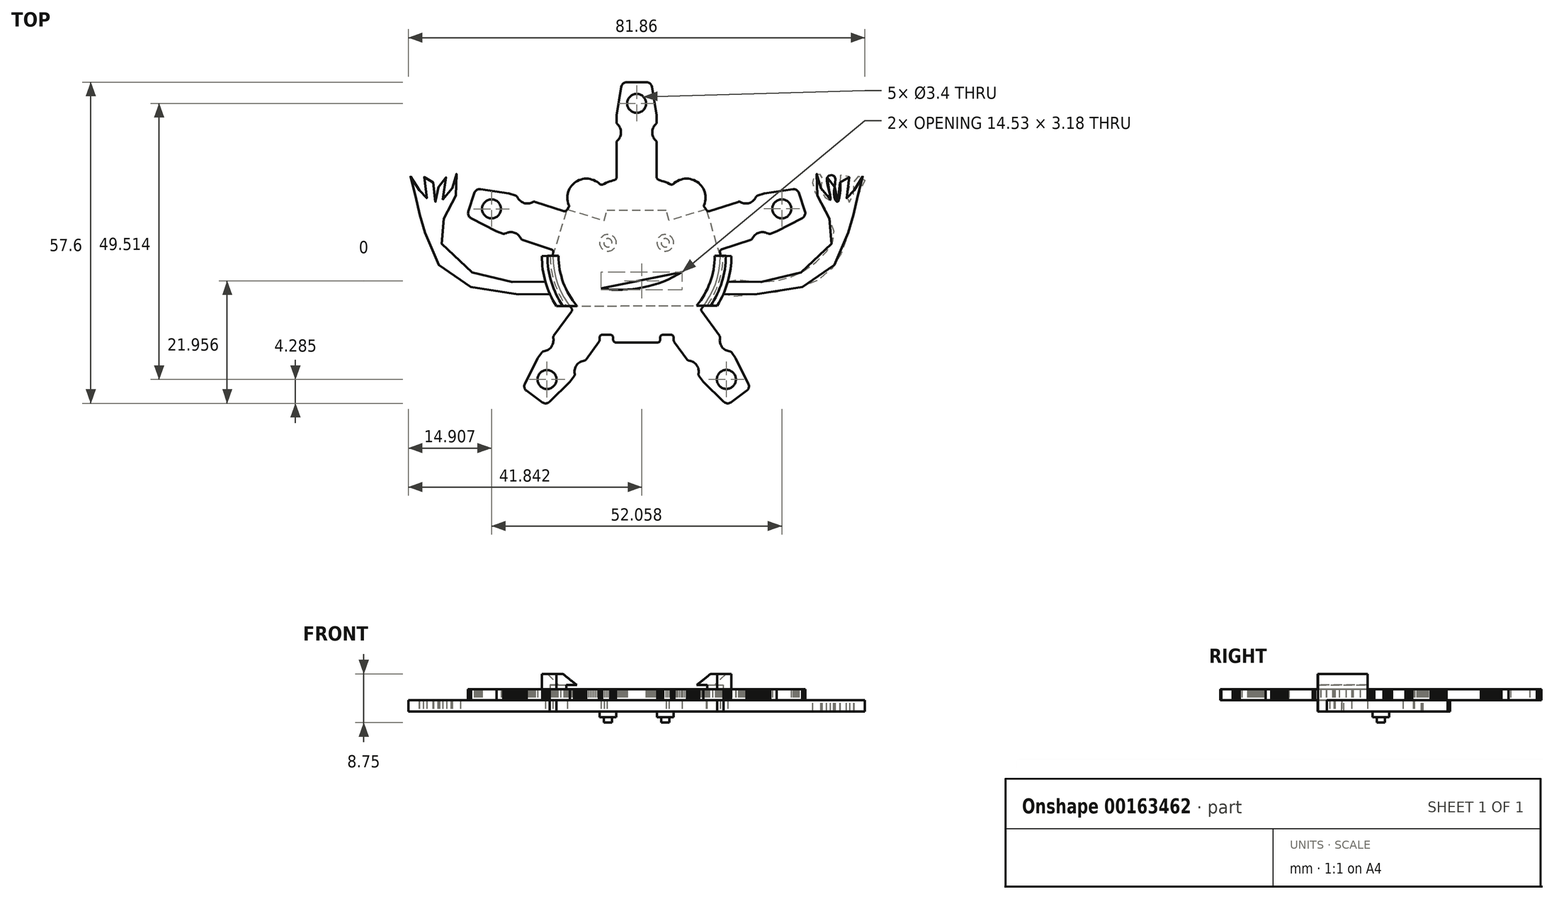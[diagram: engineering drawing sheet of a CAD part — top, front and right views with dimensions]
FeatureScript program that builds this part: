
annotation { "Feature Type Name" : "Feature", "Feature Type Description" : "" }
export const myFeature = defineFeature(function(context is Context, id is Id, definition is map)
    precondition{}
    {
        {
            var Q0;
            Q0=qCreatedBy(makeId("Top.planeOp"),FACE);
            var sketch = newSketch(context, id + "F0", { "sketchPlane" : qUnion([Q0])});
            skLineSegment(sketch, "E0", {"start": v(30.22, 5.42) * mm, "end": v(30.18, 5.6) * mm});
            skLineSegment(sketch, "E1", {"start": v(30.18, 5.6) * mm, "end": v(29.1, 8.94) * mm});
            skLineSegment(sketch, "E2", {"start": v(29.1, 8.94) * mm, "end": v(29.03, 9.1) * mm});
            skLineSegment(sketch, "E3", {"start": v(29.03, 9.1) * mm, "end": v(28.93, 9.25) * mm});
            skLineSegment(sketch, "E4", {"start": v(28.93, 9.25) * mm, "end": v(28.81, 9.38) * mm});
            skLineSegment(sketch, "E5", {"start": v(28.81, 9.38) * mm, "end": v(28.67, 9.48) * mm});
            skLineSegment(sketch, "E6", {"start": v(28.67, 9.48) * mm, "end": v(28.52, 9.56) * mm});
            skLineSegment(sketch, "E7", {"start": v(28.52, 9.56) * mm, "end": v(28.36, 9.6) * mm});
            skLineSegment(sketch, "E8", {"start": v(28.36, 9.6) * mm, "end": v(28.18, 9.63) * mm});
            skLineSegment(sketch, "E9", {"start": v(28.18, 9.63) * mm, "end": v(28, 9.62) * mm});
            skLineSegment(sketch, "E10", {"start": v(28, 9.62) * mm, "end": v(22.92, 8.87) * mm});
            skLineSegment(sketch, "E11", {"start": v(22.92, 8.87) * mm, "end": v(21.71, 8.48) * mm});
            skLineSegment(sketch, "E12", {"start": v(21.71, 8.48) * mm, "end": v(21.66, 8.46) * mm});
            skLineSegment(sketch, "E13", {"start": v(21.66, 8.46) * mm, "end": v(21.62, 8.44) * mm});
            skLineSegment(sketch, "E14", {"start": v(21.62, 8.44) * mm, "end": v(21.58, 8.4) * mm});
            skLineSegment(sketch, "E15", {"start": v(21.58, 8.4) * mm, "end": v(21.54, 8.38) * mm});
            skLineSegment(sketch, "E16", {"start": v(21.54, 8.38) * mm, "end": v(21.5, 8.34) * mm});
            skLineSegment(sketch, "E17", {"start": v(21.5, 8.34) * mm, "end": v(21.47, 8.3) * mm});
            skLineSegment(sketch, "E18", {"start": v(21.47, 8.3) * mm, "end": v(21.44, 8.26) * mm});
            skLineSegment(sketch, "E19", {"start": v(21.44, 8.26) * mm, "end": v(21.32, 8.03) * mm});
            skLineSegment(sketch, "E20", {"start": v(21.32, 8.03) * mm, "end": v(21.2, 7.86) * mm});
            skLineSegment(sketch, "E21", {"start": v(21.2, 7.86) * mm, "end": v(21.07, 7.7) * mm});
            skLineSegment(sketch, "E22", {"start": v(21.07, 7.7) * mm, "end": v(20.92, 7.56) * mm});
            skLineSegment(sketch, "E23", {"start": v(20.92, 7.56) * mm, "end": v(20.77, 7.43) * mm});
            skLineSegment(sketch, "E24", {"start": v(20.77, 7.43) * mm, "end": v(20.6, 7.32) * mm});
            skLineSegment(sketch, "E25", {"start": v(20.6, 7.32) * mm, "end": v(20.4, 7.22) * mm});
            skLineSegment(sketch, "E26", {"start": v(20.4, 7.22) * mm, "end": v(20.22, 7.15) * mm});
            skLineSegment(sketch, "E27", {"start": v(20.22, 7.15) * mm, "end": v(20.02, 7.1) * mm});
            skLineSegment(sketch, "E28", {"start": v(20.02, 7.1) * mm, "end": v(19.81, 7.06) * mm});
            skLineSegment(sketch, "E29", {"start": v(19.81, 7.06) * mm, "end": v(19.6, 7.05) * mm});
            skLineSegment(sketch, "E30", {"start": v(19.6, 7.05) * mm, "end": v(19.4, 7.06) * mm});
            skLineSegment(sketch, "E31", {"start": v(19.4, 7.06) * mm, "end": v(19.2, 7.1) * mm});
            skLineSegment(sketch, "E32", {"start": v(19.2, 7.1) * mm, "end": v(19, 7.14) * mm});
            skLineSegment(sketch, "E33", {"start": v(19, 7.14) * mm, "end": v(18.8, 7.21) * mm});
            skLineSegment(sketch, "E34", {"start": v(18.8, 7.21) * mm, "end": v(18.58, 7.33) * mm});
            skLineSegment(sketch, "E35", {"start": v(18.58, 7.33) * mm, "end": v(18.53, 7.35) * mm});
            skLineSegment(sketch, "E36", {"start": v(18.53, 7.35) * mm, "end": v(18.48, 7.36) * mm});
            skLineSegment(sketch, "E37", {"start": v(18.48, 7.36) * mm, "end": v(18.43, 7.37) * mm});
            skLineSegment(sketch, "E38", {"start": v(18.43, 7.37) * mm, "end": v(18.38, 7.37) * mm});
            skLineSegment(sketch, "E39", {"start": v(18.38, 7.37) * mm, "end": v(18.33, 7.37) * mm});
            skLineSegment(sketch, "E40", {"start": v(18.33, 7.37) * mm, "end": v(18.28, 7.36) * mm});
            skLineSegment(sketch, "E41", {"start": v(18.28, 7.36) * mm, "end": v(18.23, 7.34) * mm});
            skLineSegment(sketch, "E42", {"start": v(18.23, 7.34) * mm, "end": v(13.03, 5.66) * mm});
            skLineSegment(sketch, "E43", {"start": v(13.03, 5.66) * mm, "end": v(13, 5.65) * mm});
            skLineSegment(sketch, "E44", {"start": v(13, 5.65) * mm, "end": v(12.96, 5.65) * mm});
            skLineSegment(sketch, "E45", {"start": v(12.96, 5.65) * mm, "end": v(12.92, 5.64) * mm});
            skLineSegment(sketch, "E46", {"start": v(12.92, 5.64) * mm, "end": v(12.88, 5.64) * mm});
            skLineSegment(sketch, "E47", {"start": v(12.88, 5.64) * mm, "end": v(12.83, 5.64) * mm});
            skLineSegment(sketch, "E48", {"start": v(12.83, 5.64) * mm, "end": v(12.8, 5.64) * mm});
            skLineSegment(sketch, "E49", {"start": v(12.8, 5.64) * mm, "end": v(12.76, 5.65) * mm});
            skLineSegment(sketch, "E50", {"start": v(12.76, 5.65) * mm, "end": v(12.73, 5.66) * mm});
            skLineSegment(sketch, "E51", {"start": v(12.73, 5.66) * mm, "end": v(12.7, 5.68) * mm});
            skLineSegment(sketch, "E52", {"start": v(12.7, 5.68) * mm, "end": v(12.67, 5.7) * mm});
            skLineSegment(sketch, "E53", {"start": v(12.67, 5.7) * mm, "end": v(12.65, 5.72) * mm});
            skLineSegment(sketch, "E54", {"start": v(12.65, 5.72) * mm, "end": v(12.63, 5.74) * mm});
            skLineSegment(sketch, "E55", {"start": v(12.63, 5.74) * mm, "end": v(12.6, 5.77) * mm});
            skLineSegment(sketch, "E56", {"start": v(12.6, 5.77) * mm, "end": v(12.59, 5.8) * mm});
            skLineSegment(sketch, "E57", {"start": v(12.59, 5.8) * mm, "end": v(12.4, 6.07) * mm});
            skLineSegment(sketch, "E58", {"start": v(12.4, 6.07) * mm, "end": v(12.1, 6.48) * mm});
            skLineSegment(sketch, "E59", {"start": v(12.1, 6.48) * mm, "end": v(12.1, 6.5) * mm});
            skLineSegment(sketch, "E60", {"start": v(12.1, 6.5) * mm, "end": v(12.09, 6.52) * mm});
            skLineSegment(sketch, "E61", {"start": v(12.09, 6.52) * mm, "end": v(12.08, 6.54) * mm});
            skLineSegment(sketch, "E62", {"start": v(12.08, 6.54) * mm, "end": v(12.07, 6.56) * mm});
            skLineSegment(sketch, "E63", {"start": v(12.07, 6.56) * mm, "end": v(12.06, 6.58) * mm});
            skLineSegment(sketch, "E64", {"start": v(12.06, 6.58) * mm, "end": v(12.06, 6.6) * mm});
            skLineSegment(sketch, "E65", {"start": v(12.06, 6.6) * mm, "end": v(12.06, 6.63) * mm});
            skLineSegment(sketch, "E66", {"start": v(12.06, 6.63) * mm, "end": v(12.05, 6.65) * mm});
            skLineSegment(sketch, "E67", {"start": v(12.05, 6.65) * mm, "end": v(12.05, 6.67) * mm});
            skLineSegment(sketch, "E68", {"start": v(12.05, 6.67) * mm, "end": v(12.06, 6.7) * mm});
            skLineSegment(sketch, "E69", {"start": v(12.06, 6.7) * mm, "end": v(12.06, 6.71) * mm});
            skLineSegment(sketch, "E70", {"start": v(12.06, 6.71) * mm, "end": v(12.06, 6.73) * mm});
            skLineSegment(sketch, "E71", {"start": v(12.06, 6.73) * mm, "end": v(12.06, 6.73) * mm});
            skLineSegment(sketch, "E72", {"start": v(12.06, 6.73) * mm, "end": v(12.09, 6.78) * mm});
            skLineSegment(sketch, "E73", {"start": v(12.09, 6.78) * mm, "end": v(12.2, 7.09) * mm});
            skLineSegment(sketch, "E74", {"start": v(12.2, 7.09) * mm, "end": v(12.28, 7.42) * mm});
            skLineSegment(sketch, "E75", {"start": v(12.28, 7.42) * mm, "end": v(12.34, 7.75) * mm});
            skLineSegment(sketch, "E76", {"start": v(12.34, 7.75) * mm, "end": v(12.35, 8.1) * mm});
            skLineSegment(sketch, "E77", {"start": v(12.35, 8.1) * mm, "end": v(12.34, 8.45) * mm});
            skLineSegment(sketch, "E78", {"start": v(12.34, 8.45) * mm, "end": v(12.28, 8.79) * mm});
            skLineSegment(sketch, "E79", {"start": v(12.28, 8.79) * mm, "end": v(12.2, 9.11) * mm});
            skLineSegment(sketch, "E80", {"start": v(12.2, 9.11) * mm, "end": v(12.09, 9.42) * mm});
            skLineSegment(sketch, "E81", {"start": v(12.09, 9.42) * mm, "end": v(11.94, 9.72) * mm});
            skLineSegment(sketch, "E82", {"start": v(11.94, 9.72) * mm, "end": v(11.77, 10) * mm});
            skLineSegment(sketch, "E83", {"start": v(11.77, 10) * mm, "end": v(11.58, 10.26) * mm});
            skLineSegment(sketch, "E84", {"start": v(11.58, 10.26) * mm, "end": v(11.36, 10.5) * mm});
            skLineSegment(sketch, "E85", {"start": v(11.36, 10.5) * mm, "end": v(11.12, 10.72) * mm});
            skLineSegment(sketch, "E86", {"start": v(11.12, 10.72) * mm, "end": v(10.85, 10.92) * mm});
            skLineSegment(sketch, "E87", {"start": v(10.85, 10.92) * mm, "end": v(10.57, 11.09) * mm});
            skLineSegment(sketch, "E88", {"start": v(10.57, 11.09) * mm, "end": v(10.28, 11.23) * mm});
            skLineSegment(sketch, "E89", {"start": v(10.28, 11.23) * mm, "end": v(9.96, 11.35) * mm});
            skLineSegment(sketch, "E90", {"start": v(9.96, 11.35) * mm, "end": v(9.64, 11.43) * mm});
            skLineSegment(sketch, "E91", {"start": v(9.64, 11.43) * mm, "end": v(9.3, 11.48) * mm});
            skLineSegment(sketch, "E92", {"start": v(9.3, 11.48) * mm, "end": v(8.95, 11.5) * mm});
            skLineSegment(sketch, "E93", {"start": v(8.95, 11.5) * mm, "end": v(8.6, 11.48) * mm});
            skLineSegment(sketch, "E94", {"start": v(8.6, 11.48) * mm, "end": v(8.27, 11.43) * mm});
            skLineSegment(sketch, "E95", {"start": v(8.27, 11.43) * mm, "end": v(7.94, 11.35) * mm});
            skLineSegment(sketch, "E96", {"start": v(7.94, 11.35) * mm, "end": v(7.63, 11.23) * mm});
            skLineSegment(sketch, "E97", {"start": v(7.63, 11.23) * mm, "end": v(7.33, 11.1) * mm});
            skLineSegment(sketch, "E98", {"start": v(7.33, 11.1) * mm, "end": v(7.05, 10.92) * mm});
            skLineSegment(sketch, "E99", {"start": v(7.05, 10.92) * mm, "end": v(6.8, 10.72) * mm});
            skLineSegment(sketch, "E100", {"start": v(6.8, 10.72) * mm, "end": v(6.63, 10.58) * mm});
            skLineSegment(sketch, "E101", {"start": v(6.63, 10.58) * mm, "end": v(6.55, 10.51) * mm});
            skLineSegment(sketch, "E102", {"start": v(6.55, 10.51) * mm, "end": v(6.47, 10.47) * mm});
            skLineSegment(sketch, "E103", {"start": v(6.47, 10.47) * mm, "end": v(6.37, 10.44) * mm});
            skLineSegment(sketch, "E104", {"start": v(6.37, 10.44) * mm, "end": v(6.27, 10.43) * mm});
            skLineSegment(sketch, "E105", {"start": v(6.27, 10.43) * mm, "end": v(6.17, 10.44) * mm});
            skLineSegment(sketch, "E106", {"start": v(6.17, 10.44) * mm, "end": v(6.08, 10.47) * mm});
            skLineSegment(sketch, "E107", {"start": v(6.08, 10.47) * mm, "end": v(6.02, 10.5) * mm});
            skLineSegment(sketch, "E108", {"start": v(6.02, 10.5) * mm, "end": v(5.84, 10.58) * mm});
            skLineSegment(sketch, "E109", {"start": v(5.84, 10.58) * mm, "end": v(5.53, 10.72) * mm});
            skLineSegment(sketch, "E110", {"start": v(5.53, 10.72) * mm, "end": v(5.2, 10.85) * mm});
            skLineSegment(sketch, "E111", {"start": v(5.2, 10.85) * mm, "end": v(4.88, 10.97) * mm});
            skLineSegment(sketch, "E112", {"start": v(4.88, 10.97) * mm, "end": v(4.56, 11.1) * mm});
            skLineSegment(sketch, "E113", {"start": v(4.56, 11.1) * mm, "end": v(4.22, 11.2) * mm});
            skLineSegment(sketch, "E114", {"start": v(4.22, 11.2) * mm, "end": v(4.02, 11.26) * mm});
            skLineSegment(sketch, "E115", {"start": v(4.02, 11.26) * mm, "end": v(3.9, 11.29) * mm});
            skLineSegment(sketch, "E116", {"start": v(3.9, 11.29) * mm, "end": v(3.82, 11.34) * mm});
            skLineSegment(sketch, "E117", {"start": v(3.82, 11.34) * mm, "end": v(3.75, 11.4) * mm});
            skLineSegment(sketch, "E118", {"start": v(3.75, 11.4) * mm, "end": v(3.68, 11.47) * mm});
            skLineSegment(sketch, "E119", {"start": v(3.68, 11.47) * mm, "end": v(3.64, 11.56) * mm});
            skLineSegment(sketch, "E120", {"start": v(3.64, 11.56) * mm, "end": v(3.6, 11.65) * mm});
            skLineSegment(sketch, "E121", {"start": v(3.6, 11.65) * mm, "end": v(3.6, 11.76) * mm});
            skLineSegment(sketch, "E122", {"start": v(3.6, 11.76) * mm, "end": v(3.6, 17.97) * mm});
            skLineSegment(sketch, "E123", {"start": v(3.6, 17.97) * mm, "end": v(3.6, 18.02) * mm});
            skLineSegment(sketch, "E124", {"start": v(3.6, 18.02) * mm, "end": v(3.59, 18.07) * mm});
            skLineSegment(sketch, "E125", {"start": v(3.59, 18.07) * mm, "end": v(3.58, 18.12) * mm});
            skLineSegment(sketch, "E126", {"start": v(3.58, 18.12) * mm, "end": v(3.56, 18.17) * mm});
            skLineSegment(sketch, "E127", {"start": v(3.56, 18.17) * mm, "end": v(3.54, 18.21) * mm});
            skLineSegment(sketch, "E128", {"start": v(3.54, 18.21) * mm, "end": v(3.5, 18.26) * mm});
            skLineSegment(sketch, "E129", {"start": v(3.5, 18.26) * mm, "end": v(3.48, 18.3) * mm});
            skLineSegment(sketch, "E130", {"start": v(3.48, 18.3) * mm, "end": v(3.3, 18.48) * mm});
            skLineSegment(sketch, "E131", {"start": v(3.3, 18.48) * mm, "end": v(3.17, 18.65) * mm});
            skLineSegment(sketch, "E132", {"start": v(3.17, 18.65) * mm, "end": v(3.06, 18.82) * mm});
            skLineSegment(sketch, "E133", {"start": v(3.06, 18.82) * mm, "end": v(2.97, 19) * mm});
            skLineSegment(sketch, "E134", {"start": v(2.97, 19) * mm, "end": v(2.9, 19.2) * mm});
            skLineSegment(sketch, "E135", {"start": v(2.9, 19.2) * mm, "end": v(2.84, 19.4) * mm});
            skLineSegment(sketch, "E136", {"start": v(2.84, 19.4) * mm, "end": v(2.81, 19.6) * mm});
            skLineSegment(sketch, "E137", {"start": v(2.81, 19.6) * mm, "end": v(2.8, 19.8) * mm});
            skLineSegment(sketch, "E138", {"start": v(2.8, 19.8) * mm, "end": v(2.81, 20) * mm});
            skLineSegment(sketch, "E139", {"start": v(2.81, 20) * mm, "end": v(2.84, 20.21) * mm});
            skLineSegment(sketch, "E140", {"start": v(2.84, 20.21) * mm, "end": v(2.9, 20.41) * mm});
            skLineSegment(sketch, "E141", {"start": v(2.9, 20.41) * mm, "end": v(2.97, 20.6) * mm});
            skLineSegment(sketch, "E142", {"start": v(2.97, 20.6) * mm, "end": v(3.06, 20.78) * mm});
            skLineSegment(sketch, "E143", {"start": v(3.06, 20.78) * mm, "end": v(3.17, 20.96) * mm});
            skLineSegment(sketch, "E144", {"start": v(3.17, 20.96) * mm, "end": v(3.3, 21.12) * mm});
            skLineSegment(sketch, "E145", {"start": v(3.3, 21.12) * mm, "end": v(3.48, 21.3) * mm});
            skLineSegment(sketch, "E146", {"start": v(3.48, 21.3) * mm, "end": v(3.5, 21.35) * mm});
            skLineSegment(sketch, "E147", {"start": v(3.5, 21.35) * mm, "end": v(3.54, 21.39) * mm});
            skLineSegment(sketch, "E148", {"start": v(3.54, 21.39) * mm, "end": v(3.56, 21.44) * mm});
            skLineSegment(sketch, "E149", {"start": v(3.56, 21.44) * mm, "end": v(3.58, 21.48) * mm});
            skLineSegment(sketch, "E150", {"start": v(3.58, 21.48) * mm, "end": v(3.59, 21.53) * mm});
            skLineSegment(sketch, "E151", {"start": v(3.59, 21.53) * mm, "end": v(3.6, 21.58) * mm});
            skLineSegment(sketch, "E152", {"start": v(3.6, 21.58) * mm, "end": v(3.6, 21.63) * mm});
            skLineSegment(sketch, "E153", {"start": v(3.6, 21.63) * mm, "end": v(3.6, 22.9) * mm});
            skLineSegment(sketch, "E154", {"start": v(3.6, 22.9) * mm, "end": v(2.74, 27.97) * mm});
            skLineSegment(sketch, "E155", {"start": v(2.74, 27.97) * mm, "end": v(2.7, 28.14) * mm});
            skLineSegment(sketch, "E156", {"start": v(2.7, 28.14) * mm, "end": v(2.62, 28.3) * mm});
            skLineSegment(sketch, "E157", {"start": v(2.62, 28.3) * mm, "end": v(2.52, 28.44) * mm});
            skLineSegment(sketch, "E158", {"start": v(2.52, 28.44) * mm, "end": v(2.4, 28.57) * mm});
            skLineSegment(sketch, "E159", {"start": v(2.4, 28.57) * mm, "end": v(2.26, 28.67) * mm});
            skLineSegment(sketch, "E160", {"start": v(2.26, 28.67) * mm, "end": v(2.1, 28.74) * mm});
            skLineSegment(sketch, "E161", {"start": v(2.1, 28.74) * mm, "end": v(1.93, 28.79) * mm});
            skLineSegment(sketch, "E162", {"start": v(1.93, 28.79) * mm, "end": v(1.76, 28.8) * mm});
            skLineSegment(sketch, "E163", {"start": v(1.76, 28.8) * mm, "end": v(-1.4, 28.8) * mm});
            skLineSegment(sketch, "E164", {"start": v(-1.4, 28.8) * mm, "end": v(1.6, 28.8) * mm});
            skLineSegment(sketch, "E165", {"start": v(-1.4, 28.8) * mm, "end": v(-1.7, 28.8) * mm});
            skLineSegment(sketch, "E166", {"start": v(-1.7, 28.8) * mm, "end": v(-1.76, 28.8) * mm});
            skLineSegment(sketch, "E167", {"start": v(-1.76, 28.8) * mm, "end": v(-1.93, 28.79) * mm});
            skLineSegment(sketch, "E168", {"start": v(-1.93, 28.79) * mm, "end": v(-2.1, 28.74) * mm});
            skLineSegment(sketch, "E169", {"start": v(-2.1, 28.74) * mm, "end": v(-2.26, 28.67) * mm});
            skLineSegment(sketch, "E170", {"start": v(-2.26, 28.67) * mm, "end": v(-2.4, 28.57) * mm});
            skLineSegment(sketch, "E171", {"start": v(-2.4, 28.57) * mm, "end": v(-2.52, 28.44) * mm});
            skLineSegment(sketch, "E172", {"start": v(-2.52, 28.44) * mm, "end": v(-2.62, 28.3) * mm});
            skLineSegment(sketch, "E173", {"start": v(-2.62, 28.3) * mm, "end": v(-2.7, 28.14) * mm});
            skLineSegment(sketch, "E174", {"start": v(-2.7, 28.14) * mm, "end": v(-2.74, 27.97) * mm});
            skLineSegment(sketch, "E175", {"start": v(-2.74, 27.97) * mm, "end": v(-3.6, 22.9) * mm});
            skLineSegment(sketch, "E176", {"start": v(-3.6, 22.9) * mm, "end": v(-3.6, 21.63) * mm});
            skLineSegment(sketch, "E177", {"start": v(-3.6, 21.63) * mm, "end": v(-3.6, 21.58) * mm});
            skLineSegment(sketch, "E178", {"start": v(-3.6, 21.58) * mm, "end": v(-3.59, 21.53) * mm});
            skLineSegment(sketch, "E179", {"start": v(-3.59, 21.53) * mm, "end": v(-3.58, 21.48) * mm});
            skLineSegment(sketch, "E180", {"start": v(-3.58, 21.48) * mm, "end": v(-3.56, 21.44) * mm});
            skLineSegment(sketch, "E181", {"start": v(-3.56, 21.44) * mm, "end": v(-3.53, 21.39) * mm});
            skLineSegment(sketch, "E182", {"start": v(-3.53, 21.39) * mm, "end": v(-3.5, 21.35) * mm});
            skLineSegment(sketch, "E183", {"start": v(-3.5, 21.35) * mm, "end": v(-3.48, 21.3) * mm});
            skLineSegment(sketch, "E184", {"start": v(-3.48, 21.3) * mm, "end": v(-3.3, 21.12) * mm});
            skLineSegment(sketch, "E185", {"start": v(-3.3, 21.12) * mm, "end": v(-3.17, 20.96) * mm});
            skLineSegment(sketch, "E186", {"start": v(-3.17, 20.96) * mm, "end": v(-3.06, 20.78) * mm});
            skLineSegment(sketch, "E187", {"start": v(-3.06, 20.78) * mm, "end": v(-2.97, 20.6) * mm});
            skLineSegment(sketch, "E188", {"start": v(-2.97, 20.6) * mm, "end": v(-2.9, 20.41) * mm});
            skLineSegment(sketch, "E189", {"start": v(-2.9, 20.41) * mm, "end": v(-2.84, 20.21) * mm});
            skLineSegment(sketch, "E190", {"start": v(-2.84, 20.21) * mm, "end": v(-2.8, 20) * mm});
            skLineSegment(sketch, "E191", {"start": v(-2.8, 20) * mm, "end": v(-2.8, 19.8) * mm});
            skLineSegment(sketch, "E192", {"start": v(-2.8, 19.8) * mm, "end": v(-2.8, 19.6) * mm});
            skLineSegment(sketch, "E193", {"start": v(-2.8, 19.6) * mm, "end": v(-2.84, 19.4) * mm});
            skLineSegment(sketch, "E194", {"start": v(-2.84, 19.4) * mm, "end": v(-2.9, 19.2) * mm});
            skLineSegment(sketch, "E195", {"start": v(-2.9, 19.2) * mm, "end": v(-2.97, 19) * mm});
            skLineSegment(sketch, "E196", {"start": v(-2.97, 19) * mm, "end": v(-3.06, 18.82) * mm});
            skLineSegment(sketch, "E197", {"start": v(-3.06, 18.82) * mm, "end": v(-3.17, 18.65) * mm});
            skLineSegment(sketch, "E198", {"start": v(-3.17, 18.65) * mm, "end": v(-3.3, 18.48) * mm});
            skLineSegment(sketch, "E199", {"start": v(-3.3, 18.48) * mm, "end": v(-3.48, 18.3) * mm});
            skLineSegment(sketch, "E200", {"start": v(-3.48, 18.3) * mm, "end": v(-3.5, 18.26) * mm});
            skLineSegment(sketch, "E201", {"start": v(-3.5, 18.26) * mm, "end": v(-3.53, 18.21) * mm});
            skLineSegment(sketch, "E202", {"start": v(-3.53, 18.21) * mm, "end": v(-3.56, 18.17) * mm});
            skLineSegment(sketch, "E203", {"start": v(-3.56, 18.17) * mm, "end": v(-3.58, 18.12) * mm});
            skLineSegment(sketch, "E204", {"start": v(-3.58, 18.12) * mm, "end": v(-3.59, 18.07) * mm});
            skLineSegment(sketch, "E205", {"start": v(-3.59, 18.07) * mm, "end": v(-3.6, 18.02) * mm});
            skLineSegment(sketch, "E206", {"start": v(-3.6, 18.02) * mm, "end": v(-3.6, 17.97) * mm});
            skLineSegment(sketch, "E207", {"start": v(-3.6, 17.97) * mm, "end": v(-3.6, 11.83) * mm});
            skLineSegment(sketch, "E208", {"start": v(-3.6, 11.83) * mm, "end": v(-3.6, 11.66) * mm});
            skLineSegment(sketch, "E209", {"start": v(-3.6, 11.66) * mm, "end": v(-3.63, 11.56) * mm});
            skLineSegment(sketch, "E210", {"start": v(-3.63, 11.56) * mm, "end": v(-3.68, 11.48) * mm});
            skLineSegment(sketch, "E211", {"start": v(-3.68, 11.48) * mm, "end": v(-3.74, 11.4) * mm});
            skLineSegment(sketch, "E212", {"start": v(-3.74, 11.4) * mm, "end": v(-3.81, 11.34) * mm});
            skLineSegment(sketch, "E213", {"start": v(-3.81, 11.34) * mm, "end": v(-3.9, 11.3) * mm});
            skLineSegment(sketch, "E214", {"start": v(-3.9, 11.3) * mm, "end": v(-3.94, 11.28) * mm});
            skLineSegment(sketch, "E215", {"start": v(-3.94, 11.28) * mm, "end": v(-3.94, 11.28) * mm});
            skLineSegment(sketch, "E216", {"start": v(-3.94, 11.28) * mm, "end": v(-4, 11.27) * mm});
            skLineSegment(sketch, "E217", {"start": v(-4, 11.27) * mm, "end": v(-4.22, 11.2) * mm});
            skLineSegment(sketch, "E218", {"start": v(-4.22, 11.2) * mm, "end": v(-4.55, 11.1) * mm});
            skLineSegment(sketch, "E219", {"start": v(-4.55, 11.1) * mm, "end": v(-4.88, 10.97) * mm});
            skLineSegment(sketch, "E220", {"start": v(-4.88, 10.97) * mm, "end": v(-5.2, 10.85) * mm});
            skLineSegment(sketch, "E221", {"start": v(-5.2, 10.85) * mm, "end": v(-5.53, 10.72) * mm});
            skLineSegment(sketch, "E222", {"start": v(-5.53, 10.72) * mm, "end": v(-5.84, 10.58) * mm});
            skLineSegment(sketch, "E223", {"start": v(-5.84, 10.58) * mm, "end": v(-6.12, 10.45) * mm});
            skLineSegment(sketch, "E224", {"start": v(-6.12, 10.45) * mm, "end": v(-6.12, 10.45) * mm});
            skLineSegment(sketch, "E225", {"start": v(-6.12, 10.45) * mm, "end": v(-6.22, 10.42) * mm});
            skLineSegment(sketch, "E226", {"start": v(-6.22, 10.42) * mm, "end": v(-6.32, 10.41) * mm});
            skLineSegment(sketch, "E227", {"start": v(-6.32, 10.41) * mm, "end": v(-6.42, 10.42) * mm});
            skLineSegment(sketch, "E228", {"start": v(-6.42, 10.42) * mm, "end": v(-6.51, 10.45) * mm});
            skLineSegment(sketch, "E229", {"start": v(-6.51, 10.45) * mm, "end": v(-6.6, 10.5) * mm});
            skLineSegment(sketch, "E230", {"start": v(-6.6, 10.5) * mm, "end": v(-6.66, 10.55) * mm});
            skLineSegment(sketch, "E231", {"start": v(-6.66, 10.55) * mm, "end": v(-6.66, 10.55) * mm});
            skLineSegment(sketch, "E232", {"start": v(-6.66, 10.55) * mm, "end": v(-6.85, 10.72) * mm});
            skLineSegment(sketch, "E233", {"start": v(-6.85, 10.72) * mm, "end": v(-7.12, 10.92) * mm});
            skLineSegment(sketch, "E234", {"start": v(-7.12, 10.92) * mm, "end": v(-7.4, 11.09) * mm});
            skLineSegment(sketch, "E235", {"start": v(-7.4, 11.09) * mm, "end": v(-7.7, 11.23) * mm});
            skLineSegment(sketch, "E236", {"start": v(-7.7, 11.23) * mm, "end": v(-8, 11.35) * mm});
            skLineSegment(sketch, "E237", {"start": v(-8, 11.35) * mm, "end": v(-8.33, 11.43) * mm});
            skLineSegment(sketch, "E238", {"start": v(-8.33, 11.43) * mm, "end": v(-8.67, 11.48) * mm});
            skLineSegment(sketch, "E239", {"start": v(-8.67, 11.48) * mm, "end": v(-9.02, 11.5) * mm});
            skLineSegment(sketch, "E240", {"start": v(-9.02, 11.5) * mm, "end": v(-9.36, 11.48) * mm});
            skLineSegment(sketch, "E241", {"start": v(-9.36, 11.48) * mm, "end": v(-9.7, 11.43) * mm});
            skLineSegment(sketch, "E242", {"start": v(-9.7, 11.43) * mm, "end": v(-10.03, 11.35) * mm});
            skLineSegment(sketch, "E243", {"start": v(-10.03, 11.35) * mm, "end": v(-10.34, 11.23) * mm});
            skLineSegment(sketch, "E244", {"start": v(-10.34, 11.23) * mm, "end": v(-10.64, 11.09) * mm});
            skLineSegment(sketch, "E245", {"start": v(-10.64, 11.09) * mm, "end": v(-10.92, 10.92) * mm});
            skLineSegment(sketch, "E246", {"start": v(-10.92, 10.92) * mm, "end": v(-11.18, 10.72) * mm});
            skLineSegment(sketch, "E247", {"start": v(-11.18, 10.72) * mm, "end": v(-11.42, 10.5) * mm});
            skLineSegment(sketch, "E248", {"start": v(-11.42, 10.5) * mm, "end": v(-11.64, 10.26) * mm});
            skLineSegment(sketch, "E249", {"start": v(-11.64, 10.26) * mm, "end": v(-11.84, 10) * mm});
            skLineSegment(sketch, "E250", {"start": v(-11.84, 10) * mm, "end": v(-12, 9.72) * mm});
            skLineSegment(sketch, "E251", {"start": v(-12, 9.72) * mm, "end": v(-12.15, 9.42) * mm});
            skLineSegment(sketch, "E252", {"start": v(-12.15, 9.42) * mm, "end": v(-12.26, 9.11) * mm});
            skLineSegment(sketch, "E253", {"start": v(-12.26, 9.11) * mm, "end": v(-12.35, 8.79) * mm});
            skLineSegment(sketch, "E254", {"start": v(-12.35, 8.79) * mm, "end": v(-12.4, 8.45) * mm});
            skLineSegment(sketch, "E255", {"start": v(-12.4, 8.45) * mm, "end": v(-12.42, 8.1) * mm});
            skLineSegment(sketch, "E256", {"start": v(-12.42, 8.1) * mm, "end": v(-12.4, 7.75) * mm});
            skLineSegment(sketch, "E257", {"start": v(-12.4, 7.75) * mm, "end": v(-12.35, 7.42) * mm});
            skLineSegment(sketch, "E258", {"start": v(-12.35, 7.42) * mm, "end": v(-12.26, 7.09) * mm});
            skLineSegment(sketch, "E259", {"start": v(-12.26, 7.09) * mm, "end": v(-12.15, 6.78) * mm});
            skLineSegment(sketch, "E260", {"start": v(-12.15, 6.78) * mm, "end": v(-12.1, 6.67) * mm});
            skLineSegment(sketch, "E261", {"start": v(-12.1, 6.67) * mm, "end": v(-12.1, 6.67) * mm});
            skLineSegment(sketch, "E262", {"start": v(-12.1, 6.67) * mm, "end": v(-12.1, 6.64) * mm});
            skLineSegment(sketch, "E263", {"start": v(-12.1, 6.64) * mm, "end": v(-12.1, 6.61) * mm});
            skLineSegment(sketch, "E264", {"start": v(-12.1, 6.61) * mm, "end": v(-12.1, 6.58) * mm});
            skLineSegment(sketch, "E265", {"start": v(-12.1, 6.58) * mm, "end": v(-12.1, 6.56) * mm});
            skLineSegment(sketch, "E266", {"start": v(-12.1, 6.56) * mm, "end": v(-12.1, 6.53) * mm});
            skLineSegment(sketch, "E267", {"start": v(-12.1, 6.53) * mm, "end": v(-12.1, 6.51) * mm});
            skLineSegment(sketch, "E268", {"start": v(-12.1, 6.51) * mm, "end": v(-12.11, 6.5) * mm});
            skLineSegment(sketch, "E269", {"start": v(-12.11, 6.5) * mm, "end": v(-12.12, 6.47) * mm});
            skLineSegment(sketch, "E270", {"start": v(-12.12, 6.47) * mm, "end": v(-12.13, 6.45) * mm});
            skLineSegment(sketch, "E271", {"start": v(-12.13, 6.45) * mm, "end": v(-12.15, 6.43) * mm});
            skLineSegment(sketch, "E272", {"start": v(-12.15, 6.43) * mm, "end": v(-12.44, 6) * mm});
            skLineSegment(sketch, "E273", {"start": v(-12.44, 6) * mm, "end": v(-12.56, 5.83) * mm});
            skLineSegment(sketch, "E274", {"start": v(-12.56, 5.83) * mm, "end": v(-12.58, 5.8) * mm});
            skLineSegment(sketch, "E275", {"start": v(-12.58, 5.8) * mm, "end": v(-12.6, 5.77) * mm});
            skLineSegment(sketch, "E276", {"start": v(-12.6, 5.77) * mm, "end": v(-12.63, 5.74) * mm});
            skLineSegment(sketch, "E277", {"start": v(-12.63, 5.74) * mm, "end": v(-12.66, 5.71) * mm});
            skLineSegment(sketch, "E278", {"start": v(-12.66, 5.71) * mm, "end": v(-12.69, 5.7) * mm});
            skLineSegment(sketch, "E279", {"start": v(-12.69, 5.7) * mm, "end": v(-12.72, 5.67) * mm});
            skLineSegment(sketch, "E280", {"start": v(-12.72, 5.67) * mm, "end": v(-12.76, 5.66) * mm});
            skLineSegment(sketch, "E281", {"start": v(-12.76, 5.66) * mm, "end": v(-12.8, 5.65) * mm});
            skLineSegment(sketch, "E282", {"start": v(-12.8, 5.65) * mm, "end": v(-12.84, 5.64) * mm});
            skLineSegment(sketch, "E283", {"start": v(-12.84, 5.64) * mm, "end": v(-12.88, 5.64) * mm});
            skLineSegment(sketch, "E284", {"start": v(-12.88, 5.64) * mm, "end": v(-12.93, 5.65) * mm});
            skLineSegment(sketch, "E285", {"start": v(-12.93, 5.65) * mm, "end": v(-13, 5.65) * mm});
            skLineSegment(sketch, "E286", {"start": v(-13, 5.65) * mm, "end": v(-13.03, 5.66) * mm});
            skLineSegment(sketch, "E287", {"start": v(-13.03, 5.66) * mm, "end": v(-18.23, 7.34) * mm});
            skLineSegment(sketch, "E288", {"start": v(-18.23, 7.34) * mm, "end": v(-18.28, 7.36) * mm});
            skLineSegment(sketch, "E289", {"start": v(-18.28, 7.36) * mm, "end": v(-18.33, 7.37) * mm});
            skLineSegment(sketch, "E290", {"start": v(-18.33, 7.37) * mm, "end": v(-18.38, 7.37) * mm});
            skLineSegment(sketch, "E291", {"start": v(-18.38, 7.37) * mm, "end": v(-18.43, 7.37) * mm});
            skLineSegment(sketch, "E292", {"start": v(-18.43, 7.37) * mm, "end": v(-18.48, 7.36) * mm});
            skLineSegment(sketch, "E293", {"start": v(-18.48, 7.36) * mm, "end": v(-18.53, 7.35) * mm});
            skLineSegment(sketch, "E294", {"start": v(-18.53, 7.35) * mm, "end": v(-18.58, 7.33) * mm});
            skLineSegment(sketch, "E295", {"start": v(-18.58, 7.33) * mm, "end": v(-18.8, 7.21) * mm});
            skLineSegment(sketch, "E296", {"start": v(-18.8, 7.21) * mm, "end": v(-19, 7.14) * mm});
            skLineSegment(sketch, "E297", {"start": v(-19, 7.14) * mm, "end": v(-19.2, 7.1) * mm});
            skLineSegment(sketch, "E298", {"start": v(-19.2, 7.1) * mm, "end": v(-19.4, 7.06) * mm});
            skLineSegment(sketch, "E299", {"start": v(-19.4, 7.06) * mm, "end": v(-19.6, 7.05) * mm});
            skLineSegment(sketch, "E300", {"start": v(-19.6, 7.05) * mm, "end": v(-19.81, 7.06) * mm});
            skLineSegment(sketch, "E301", {"start": v(-19.81, 7.06) * mm, "end": v(-20.02, 7.1) * mm});
            skLineSegment(sketch, "E302", {"start": v(-20.02, 7.1) * mm, "end": v(-20.22, 7.15) * mm});
            skLineSegment(sketch, "E303", {"start": v(-20.22, 7.15) * mm, "end": v(-20.4, 7.22) * mm});
            skLineSegment(sketch, "E304", {"start": v(-20.4, 7.22) * mm, "end": v(-20.6, 7.32) * mm});
            skLineSegment(sketch, "E305", {"start": v(-20.6, 7.32) * mm, "end": v(-20.77, 7.43) * mm});
            skLineSegment(sketch, "E306", {"start": v(-20.77, 7.43) * mm, "end": v(-20.92, 7.56) * mm});
            skLineSegment(sketch, "E307", {"start": v(-20.92, 7.56) * mm, "end": v(-21.07, 7.7) * mm});
            skLineSegment(sketch, "E308", {"start": v(-21.07, 7.7) * mm, "end": v(-21.2, 7.86) * mm});
            skLineSegment(sketch, "E309", {"start": v(-21.2, 7.86) * mm, "end": v(-21.32, 8.03) * mm});
            skLineSegment(sketch, "E310", {"start": v(-21.32, 8.03) * mm, "end": v(-21.44, 8.26) * mm});
            skLineSegment(sketch, "E311", {"start": v(-21.44, 8.26) * mm, "end": v(-21.47, 8.3) * mm});
            skLineSegment(sketch, "E312", {"start": v(-21.47, 8.3) * mm, "end": v(-21.5, 8.34) * mm});
            skLineSegment(sketch, "E313", {"start": v(-21.5, 8.34) * mm, "end": v(-21.53, 8.38) * mm});
            skLineSegment(sketch, "E314", {"start": v(-21.53, 8.38) * mm, "end": v(-21.57, 8.4) * mm});
            skLineSegment(sketch, "E315", {"start": v(-21.57, 8.4) * mm, "end": v(-21.62, 8.44) * mm});
            skLineSegment(sketch, "E316", {"start": v(-21.62, 8.44) * mm, "end": v(-21.66, 8.46) * mm});
            skLineSegment(sketch, "E317", {"start": v(-21.66, 8.46) * mm, "end": v(-21.71, 8.48) * mm});
            skLineSegment(sketch, "E318", {"start": v(-21.71, 8.48) * mm, "end": v(-22.92, 8.87) * mm});
            skLineSegment(sketch, "E319", {"start": v(-22.92, 8.87) * mm, "end": v(-28, 9.62) * mm});
            skLineSegment(sketch, "E320", {"start": v(-28, 9.62) * mm, "end": v(-28.18, 9.63) * mm});
            skLineSegment(sketch, "E321", {"start": v(-28.18, 9.63) * mm, "end": v(-28.36, 9.6) * mm});
            skLineSegment(sketch, "E322", {"start": v(-28.36, 9.6) * mm, "end": v(-28.52, 9.56) * mm});
            skLineSegment(sketch, "E323", {"start": v(-28.52, 9.56) * mm, "end": v(-28.67, 9.48) * mm});
            skLineSegment(sketch, "E324", {"start": v(-28.67, 9.48) * mm, "end": v(-28.81, 9.37) * mm});
            skLineSegment(sketch, "E325", {"start": v(-28.81, 9.37) * mm, "end": v(-28.93, 9.25) * mm});
            skLineSegment(sketch, "E326", {"start": v(-28.93, 9.25) * mm, "end": v(-29.03, 9.1) * mm});
            skLineSegment(sketch, "E327", {"start": v(-29.03, 9.1) * mm, "end": v(-29.1, 8.94) * mm});
            skLineSegment(sketch, "E328", {"start": v(-29.1, 8.94) * mm, "end": v(-30.18, 5.6) * mm});
            skLineSegment(sketch, "E329", {"start": v(-30.18, 5.6) * mm, "end": v(-30.22, 5.42) * mm});
            skLineSegment(sketch, "E330", {"start": v(-30.22, 5.42) * mm, "end": v(-30.23, 5.25) * mm});
            skLineSegment(sketch, "E331", {"start": v(-30.23, 5.25) * mm, "end": v(-30.2, 5.08) * mm});
            skLineSegment(sketch, "E332", {"start": v(-30.2, 5.08) * mm, "end": v(-30.16, 4.91) * mm});
            skLineSegment(sketch, "E333", {"start": v(-30.16, 4.91) * mm, "end": v(-30.08, 4.76) * mm});
            skLineSegment(sketch, "E334", {"start": v(-30.08, 4.76) * mm, "end": v(-29.98, 4.62) * mm});
            skLineSegment(sketch, "E335", {"start": v(-29.98, 4.62) * mm, "end": v(-29.85, 4.5) * mm});
            skLineSegment(sketch, "E336", {"start": v(-29.85, 4.5) * mm, "end": v(-29.7, 4.4) * mm});
            skLineSegment(sketch, "E337", {"start": v(-29.7, 4.4) * mm, "end": v(-25.14, 2.02) * mm});
            skLineSegment(sketch, "E338", {"start": v(-25.14, 2.02) * mm, "end": v(-23.94, 1.63) * mm});
            skLineSegment(sketch, "E339", {"start": v(-23.94, 1.63) * mm, "end": v(-23.89, 1.62) * mm});
            skLineSegment(sketch, "E340", {"start": v(-23.89, 1.62) * mm, "end": v(-23.84, 1.6) * mm});
            skLineSegment(sketch, "E341", {"start": v(-23.84, 1.6) * mm, "end": v(-23.79, 1.6) * mm});
            skLineSegment(sketch, "E342", {"start": v(-23.79, 1.6) * mm, "end": v(-23.73, 1.6) * mm});
            skLineSegment(sketch, "E343", {"start": v(-23.73, 1.6) * mm, "end": v(-23.68, 1.61) * mm});
            skLineSegment(sketch, "E344", {"start": v(-23.68, 1.61) * mm, "end": v(-23.63, 1.63) * mm});
            skLineSegment(sketch, "E345", {"start": v(-23.63, 1.63) * mm, "end": v(-23.59, 1.65) * mm});
            skLineSegment(sketch, "E346", {"start": v(-23.59, 1.65) * mm, "end": v(-23.35, 1.76) * mm});
            skLineSegment(sketch, "E347", {"start": v(-23.35, 1.76) * mm, "end": v(-23.16, 1.83) * mm});
            skLineSegment(sketch, "E348", {"start": v(-23.16, 1.83) * mm, "end": v(-22.96, 1.88) * mm});
            skLineSegment(sketch, "E349", {"start": v(-22.96, 1.88) * mm, "end": v(-22.76, 1.91) * mm});
            skLineSegment(sketch, "E350", {"start": v(-22.76, 1.91) * mm, "end": v(-22.55, 1.92) * mm});
            skLineSegment(sketch, "E351", {"start": v(-22.55, 1.92) * mm, "end": v(-22.35, 1.91) * mm});
            skLineSegment(sketch, "E352", {"start": v(-22.35, 1.91) * mm, "end": v(-22.15, 1.88) * mm});
            skLineSegment(sketch, "E353", {"start": v(-22.15, 1.88) * mm, "end": v(-21.95, 1.82) * mm});
            skLineSegment(sketch, "E354", {"start": v(-21.95, 1.82) * mm, "end": v(-21.75, 1.75) * mm});
            skLineSegment(sketch, "E355", {"start": v(-21.75, 1.75) * mm, "end": v(-21.57, 1.66) * mm});
            skLineSegment(sketch, "E356", {"start": v(-21.57, 1.66) * mm, "end": v(-21.4, 1.55) * mm});
            skLineSegment(sketch, "E357", {"start": v(-21.4, 1.55) * mm, "end": v(-21.24, 1.42) * mm});
            skLineSegment(sketch, "E358", {"start": v(-21.24, 1.42) * mm, "end": v(-21.1, 1.27) * mm});
            skLineSegment(sketch, "E359", {"start": v(-21.1, 1.27) * mm, "end": v(-20.96, 1.12) * mm});
            skLineSegment(sketch, "E360", {"start": v(-20.96, 1.12) * mm, "end": v(-20.85, 0.95) * mm});
            skLineSegment(sketch, "E361", {"start": v(-20.85, 0.95) * mm, "end": v(-20.72, 0.72) * mm});
            skLineSegment(sketch, "E362", {"start": v(-20.72, 0.72) * mm, "end": v(-20.7, 0.67) * mm});
            skLineSegment(sketch, "E363", {"start": v(-20.7, 0.67) * mm, "end": v(-20.66, 0.63) * mm});
            skLineSegment(sketch, "E364", {"start": v(-20.66, 0.63) * mm, "end": v(-20.63, 0.6) * mm});
            skLineSegment(sketch, "E365", {"start": v(-20.63, 0.6) * mm, "end": v(-20.59, 0.57) * mm});
            skLineSegment(sketch, "E366", {"start": v(-20.59, 0.57) * mm, "end": v(-20.54, 0.54) * mm});
            skLineSegment(sketch, "E367", {"start": v(-20.54, 0.54) * mm, "end": v(-20.5, 0.52) * mm});
            skLineSegment(sketch, "E368", {"start": v(-20.5, 0.52) * mm, "end": v(-20.45, 0.5) * mm});
            skLineSegment(sketch, "E369", {"start": v(-20.45, 0.5) * mm, "end": v(-15.32, -1.17) * mm});
            skLineSegment(sketch, "E370", {"start": v(-15.32, -1.17) * mm, "end": v(-15.3, -1.18) * mm});
            skLineSegment(sketch, "E371", {"start": v(-15.3, -1.18) * mm, "end": v(-15.25, -1.2) * mm});
            skLineSegment(sketch, "E372", {"start": v(-15.25, -1.2) * mm, "end": v(-15.21, -1.21) * mm});
            skLineSegment(sketch, "E373", {"start": v(-15.21, -1.21) * mm, "end": v(-15.16, -1.23) * mm});
            skLineSegment(sketch, "E374", {"start": v(-15.16, -1.23) * mm, "end": v(-15.12, -1.26) * mm});
            skLineSegment(sketch, "E375", {"start": v(-15.12, -1.26) * mm, "end": v(-15.08, -1.29) * mm});
            skLineSegment(sketch, "E376", {"start": v(-15.08, -1.29) * mm, "end": v(-15.05, -1.32) * mm});
            skLineSegment(sketch, "E377", {"start": v(-15.05, -1.32) * mm, "end": v(-15.03, -1.35) * mm});
            skLineSegment(sketch, "E378", {"start": v(-15.03, -1.35) * mm, "end": v(-15.01, -1.39) * mm});
            skLineSegment(sketch, "E379", {"start": v(-15.01, -1.39) * mm, "end": v(-15, -1.43) * mm});
            skLineSegment(sketch, "E380", {"start": v(-15, -1.43) * mm, "end": v(-14.99, -1.46) * mm});
            skLineSegment(sketch, "E381", {"start": v(-14.99, -1.46) * mm, "end": v(-14.98, -1.5) * mm});
            skLineSegment(sketch, "E382", {"start": v(-14.98, -1.5) * mm, "end": v(-14.98, -1.54) * mm});
            skLineSegment(sketch, "E383", {"start": v(-14.98, -1.54) * mm, "end": v(-14.98, -1.58) * mm});
            skLineSegment(sketch, "E384", {"start": v(-14.98, -1.58) * mm, "end": v(-15, -2.18) * mm});
            skLineSegment(sketch, "E385", {"start": v(-15, -2.18) * mm, "end": v(-15, -2.36) * mm});
            skLineSegment(sketch, "E386", {"start": v(-15, -2.36) * mm, "end": v(-14.94, -3.7) * mm});
            skLineSegment(sketch, "E387", {"start": v(-14.94, -3.7) * mm, "end": v(-14.77, -5) * mm});
            skLineSegment(sketch, "E388", {"start": v(-14.77, -5) * mm, "end": v(-14.49, -6.26) * mm});
            skLineSegment(sketch, "E389", {"start": v(-14.49, -6.26) * mm, "end": v(-14.1, -7.48) * mm});
            skLineSegment(sketch, "E390", {"start": v(-14.1, -7.48) * mm, "end": v(-13.62, -8.65) * mm});
            skLineSegment(sketch, "E391", {"start": v(-13.62, -8.65) * mm, "end": v(-13.04, -9.77) * mm});
            skLineSegment(sketch, "E392", {"start": v(-13.04, -9.77) * mm, "end": v(-12.38, -10.84) * mm});
            skLineSegment(sketch, "E393", {"start": v(-12.38, -10.84) * mm, "end": v(-11.6, -11.86) * mm});
            skLineSegment(sketch, "E394", {"start": v(-11.6, -11.86) * mm, "end": v(-11.6, -11.88) * mm});
            skLineSegment(sketch, "E395", {"start": v(-11.6, -11.88) * mm, "end": v(-11.59, -11.9) * mm});
            skLineSegment(sketch, "E396", {"start": v(-11.59, -11.9) * mm, "end": v(-11.58, -11.93) * mm});
            skLineSegment(sketch, "E397", {"start": v(-11.58, -11.93) * mm, "end": v(-11.57, -11.95) * mm});
            skLineSegment(sketch, "E398", {"start": v(-11.57, -11.95) * mm, "end": v(-11.57, -11.98) * mm});
            skLineSegment(sketch, "E399", {"start": v(-11.57, -11.98) * mm, "end": v(-11.57, -12) * mm});
            skLineSegment(sketch, "E400", {"start": v(-11.57, -12) * mm, "end": v(-11.57, -12.03) * mm});
            skLineSegment(sketch, "E401", {"start": v(-11.57, -12.03) * mm, "end": v(-11.57, -12.06) * mm});
            skLineSegment(sketch, "E402", {"start": v(-11.57, -12.06) * mm, "end": v(-11.58, -12.1) * mm});
            skLineSegment(sketch, "E403", {"start": v(-11.58, -12.1) * mm, "end": v(-11.6, -12.14) * mm});
            skLineSegment(sketch, "E404", {"start": v(-11.6, -12.14) * mm, "end": v(-11.6, -12.18) * mm});
            skLineSegment(sketch, "E405", {"start": v(-11.6, -12.18) * mm, "end": v(-11.62, -12.22) * mm});
            skLineSegment(sketch, "E406", {"start": v(-11.62, -12.22) * mm, "end": v(-11.65, -12.27) * mm});
            skLineSegment(sketch, "E407", {"start": v(-11.65, -12.27) * mm, "end": v(-11.65, -12.28) * mm});
            skLineSegment(sketch, "E408", {"start": v(-11.65, -12.28) * mm, "end": v(-14.87, -16.7) * mm});
            skLineSegment(sketch, "E409", {"start": v(-14.87, -16.7) * mm, "end": v(-14.9, -16.75) * mm});
            skLineSegment(sketch, "E410", {"start": v(-14.9, -16.75) * mm, "end": v(-14.92, -16.8) * mm});
            skLineSegment(sketch, "E411", {"start": v(-14.92, -16.8) * mm, "end": v(-14.94, -16.84) * mm});
            skLineSegment(sketch, "E412", {"start": v(-14.94, -16.84) * mm, "end": v(-14.95, -16.89) * mm});
            skLineSegment(sketch, "E413", {"start": v(-14.95, -16.89) * mm, "end": v(-14.96, -16.94) * mm});
            skLineSegment(sketch, "E414", {"start": v(-14.96, -16.94) * mm, "end": v(-14.96, -16.99) * mm});
            skLineSegment(sketch, "E415", {"start": v(-14.96, -16.99) * mm, "end": v(-14.96, -17.04) * mm});
            skLineSegment(sketch, "E416", {"start": v(-14.96, -17.04) * mm, "end": v(-14.92, -17.3) * mm});
            skLineSegment(sketch, "E417", {"start": v(-14.92, -17.3) * mm, "end": v(-14.92, -17.5) * mm});
            skLineSegment(sketch, "E418", {"start": v(-14.92, -17.5) * mm, "end": v(-14.93, -17.7) * mm});
            skLineSegment(sketch, "E419", {"start": v(-14.93, -17.7) * mm, "end": v(-14.96, -17.9) * mm});
            skLineSegment(sketch, "E420", {"start": v(-14.96, -17.9) * mm, "end": v(-15.02, -18.1) * mm});
            skLineSegment(sketch, "E421", {"start": v(-15.02, -18.1) * mm, "end": v(-15.1, -18.3) * mm});
            skLineSegment(sketch, "E422", {"start": v(-15.1, -18.3) * mm, "end": v(-15.18, -18.48) * mm});
            skLineSegment(sketch, "E423", {"start": v(-15.18, -18.48) * mm, "end": v(-15.3, -18.65) * mm});
            skLineSegment(sketch, "E424", {"start": v(-15.3, -18.65) * mm, "end": v(-15.43, -18.82) * mm});
            skLineSegment(sketch, "E425", {"start": v(-15.43, -18.82) * mm, "end": v(-15.57, -18.96) * mm});
            skLineSegment(sketch, "E426", {"start": v(-15.57, -18.96) * mm, "end": v(-15.73, -19.1) * mm});
            skLineSegment(sketch, "E427", {"start": v(-15.73, -19.1) * mm, "end": v(-15.9, -19.2) * mm});
            skLineSegment(sketch, "E428", {"start": v(-15.9, -19.2) * mm, "end": v(-16.08, -19.3) * mm});
            skLineSegment(sketch, "E429", {"start": v(-16.08, -19.3) * mm, "end": v(-16.27, -19.37) * mm});
            skLineSegment(sketch, "E430", {"start": v(-16.27, -19.37) * mm, "end": v(-16.47, -19.43) * mm});
            skLineSegment(sketch, "E431", {"start": v(-16.47, -19.43) * mm, "end": v(-16.73, -19.47) * mm});
            skLineSegment(sketch, "E432", {"start": v(-16.73, -19.47) * mm, "end": v(-16.78, -19.49) * mm});
            skLineSegment(sketch, "E433", {"start": v(-16.78, -19.49) * mm, "end": v(-16.83, -19.5) * mm});
            skLineSegment(sketch, "E434", {"start": v(-16.83, -19.5) * mm, "end": v(-16.87, -19.53) * mm});
            skLineSegment(sketch, "E435", {"start": v(-16.87, -19.53) * mm, "end": v(-16.91, -19.56) * mm});
            skLineSegment(sketch, "E436", {"start": v(-16.91, -19.56) * mm, "end": v(-16.95, -19.6) * mm});
            skLineSegment(sketch, "E437", {"start": v(-16.95, -19.6) * mm, "end": v(-16.99, -19.63) * mm});
            skLineSegment(sketch, "E438", {"start": v(-16.99, -19.63) * mm, "end": v(-17.02, -19.67) * mm});
            skLineSegment(sketch, "E439", {"start": v(-17.02, -19.67) * mm, "end": v(-17.77, -20.7) * mm});
            skLineSegment(sketch, "E440", {"start": v(-17.77, -20.7) * mm, "end": v(-20.05, -25.3) * mm});
            skLineSegment(sketch, "E441", {"start": v(-20.05, -25.3) * mm, "end": v(-20.12, -25.46) * mm});
            skLineSegment(sketch, "E442", {"start": v(-20.12, -25.46) * mm, "end": v(-20.15, -25.64) * mm});
            skLineSegment(sketch, "E443", {"start": v(-20.15, -25.64) * mm, "end": v(-20.15, -25.8) * mm});
            skLineSegment(sketch, "E444", {"start": v(-20.15, -25.8) * mm, "end": v(-20.13, -25.98) * mm});
            skLineSegment(sketch, "E445", {"start": v(-20.13, -25.98) * mm, "end": v(-20.07, -26.14) * mm});
            skLineSegment(sketch, "E446", {"start": v(-20.07, -26.14) * mm, "end": v(-19.99, -26.3) * mm});
            skLineSegment(sketch, "E447", {"start": v(-19.99, -26.3) * mm, "end": v(-19.88, -26.43) * mm});
            skLineSegment(sketch, "E448", {"start": v(-19.88, -26.43) * mm, "end": v(-19.74, -26.55) * mm});
            skLineSegment(sketch, "E449", {"start": v(-19.74, -26.55) * mm, "end": v(-16.9, -28.61) * mm});
            skLineSegment(sketch, "E450", {"start": v(-16.9, -28.61) * mm, "end": v(-16.75, -28.7) * mm});
            skLineSegment(sketch, "E451", {"start": v(-16.75, -28.7) * mm, "end": v(-16.58, -28.77) * mm});
            skLineSegment(sketch, "E452", {"start": v(-16.58, -28.77) * mm, "end": v(-16.41, -28.8) * mm});
            skLineSegment(sketch, "E453", {"start": v(-16.41, -28.8) * mm, "end": v(-16.24, -28.8) * mm});
            skLineSegment(sketch, "E454", {"start": v(-16.24, -28.8) * mm, "end": v(-16.07, -28.78) * mm});
            skLineSegment(sketch, "E455", {"start": v(-16.07, -28.78) * mm, "end": v(-15.9, -28.72) * mm});
            skLineSegment(sketch, "E456", {"start": v(-15.9, -28.72) * mm, "end": v(-15.75, -28.63) * mm});
            skLineSegment(sketch, "E457", {"start": v(-15.75, -28.63) * mm, "end": v(-15.61, -28.52) * mm});
            skLineSegment(sketch, "E458", {"start": v(-15.61, -28.52) * mm, "end": v(-11.94, -24.92) * mm});
            skLineSegment(sketch, "E459", {"start": v(-11.94, -24.92) * mm, "end": v(-11.2, -23.9) * mm});
            skLineSegment(sketch, "E460", {"start": v(-11.2, -23.9) * mm, "end": v(-11.17, -23.86) * mm});
            skLineSegment(sketch, "E461", {"start": v(-11.17, -23.86) * mm, "end": v(-11.15, -23.81) * mm});
            skLineSegment(sketch, "E462", {"start": v(-11.15, -23.81) * mm, "end": v(-11.13, -23.76) * mm});
            skLineSegment(sketch, "E463", {"start": v(-11.13, -23.76) * mm, "end": v(-11.11, -23.71) * mm});
            skLineSegment(sketch, "E464", {"start": v(-11.11, -23.71) * mm, "end": v(-11.1, -23.66) * mm});
            skLineSegment(sketch, "E465", {"start": v(-11.1, -23.66) * mm, "end": v(-11.1, -23.61) * mm});
            skLineSegment(sketch, "E466", {"start": v(-11.1, -23.61) * mm, "end": v(-11.1, -23.56) * mm});
            skLineSegment(sketch, "E467", {"start": v(-11.1, -23.56) * mm, "end": v(-11.14, -23.3) * mm});
            skLineSegment(sketch, "E468", {"start": v(-11.14, -23.3) * mm, "end": v(-11.15, -23.1) * mm});
            skLineSegment(sketch, "E469", {"start": v(-11.15, -23.1) * mm, "end": v(-11.14, -22.9) * mm});
            skLineSegment(sketch, "E470", {"start": v(-11.14, -22.9) * mm, "end": v(-11.1, -22.7) * mm});
            skLineSegment(sketch, "E471", {"start": v(-11.1, -22.7) * mm, "end": v(-11.05, -22.5) * mm});
            skLineSegment(sketch, "E472", {"start": v(-11.05, -22.5) * mm, "end": v(-10.97, -22.3) * mm});
            skLineSegment(sketch, "E473", {"start": v(-10.97, -22.3) * mm, "end": v(-10.88, -22.12) * mm});
            skLineSegment(sketch, "E474", {"start": v(-10.88, -22.12) * mm, "end": v(-10.77, -21.95) * mm});
            skLineSegment(sketch, "E475", {"start": v(-10.77, -21.95) * mm, "end": v(-10.64, -21.78) * mm});
            skLineSegment(sketch, "E476", {"start": v(-10.64, -21.78) * mm, "end": v(-10.5, -21.64) * mm});
            skLineSegment(sketch, "E477", {"start": v(-10.5, -21.64) * mm, "end": v(-10.33, -21.51) * mm});
            skLineSegment(sketch, "E478", {"start": v(-10.33, -21.51) * mm, "end": v(-10.16, -21.4) * mm});
            skLineSegment(sketch, "E479", {"start": v(-10.16, -21.4) * mm, "end": v(-9.98, -21.3) * mm});
            skLineSegment(sketch, "E480", {"start": v(-9.98, -21.3) * mm, "end": v(-9.79, -21.23) * mm});
            skLineSegment(sketch, "E481", {"start": v(-9.79, -21.23) * mm, "end": v(-9.6, -21.17) * mm});
            skLineSegment(sketch, "E482", {"start": v(-9.6, -21.17) * mm, "end": v(-9.34, -21.13) * mm});
            skLineSegment(sketch, "E483", {"start": v(-9.34, -21.13) * mm, "end": v(-9.29, -21.11) * mm});
            skLineSegment(sketch, "E484", {"start": v(-9.29, -21.11) * mm, "end": v(-9.24, -21.1) * mm});
            skLineSegment(sketch, "E485", {"start": v(-9.24, -21.1) * mm, "end": v(-9.2, -21.07) * mm});
            skLineSegment(sketch, "E486", {"start": v(-9.2, -21.07) * mm, "end": v(-9.15, -21.04) * mm});
            skLineSegment(sketch, "E487", {"start": v(-9.15, -21.04) * mm, "end": v(-9.11, -21.01) * mm});
            skLineSegment(sketch, "E488", {"start": v(-9.11, -21.01) * mm, "end": v(-9.07, -20.97) * mm});
            skLineSegment(sketch, "E489", {"start": v(-9.07, -20.97) * mm, "end": v(-9.04, -20.93) * mm});
            skLineSegment(sketch, "E490", {"start": v(-9.04, -20.93) * mm, "end": v(-6.75, -17.8) * mm});
            skLineSegment(sketch, "E491", {"start": v(-6.75, -17.8) * mm, "end": v(-6.7, -17.7) * mm});
            skLineSegment(sketch, "E492", {"start": v(-6.7, -17.7) * mm, "end": v(-6.67, -17.6) * mm});
            skLineSegment(sketch, "E493", {"start": v(-6.67, -17.6) * mm, "end": v(-6.66, -17.52) * mm});
            skLineSegment(sketch, "E494", {"start": v(-6.66, -17.52) * mm, "end": v(-6.66, -17.02) * mm});
            skLineSegment(sketch, "E495", {"start": v(-6.66, -17.02) * mm, "end": v(-6.65, -16.9) * mm});
            skLineSegment(sketch, "E496", {"start": v(-6.65, -16.9) * mm, "end": v(-6.62, -16.8) * mm});
            skLineSegment(sketch, "E497", {"start": v(-6.62, -16.8) * mm, "end": v(-6.58, -16.72) * mm});
            skLineSegment(sketch, "E498", {"start": v(-6.58, -16.72) * mm, "end": v(-6.52, -16.65) * mm});
            skLineSegment(sketch, "E499", {"start": v(-6.52, -16.65) * mm, "end": v(-6.44, -16.59) * mm});
            skLineSegment(sketch, "E500", {"start": v(-6.44, -16.59) * mm, "end": v(-6.36, -16.54) * mm});
            skLineSegment(sketch, "E501", {"start": v(-6.36, -16.54) * mm, "end": v(-6.26, -16.51) * mm});
            skLineSegment(sketch, "E502", {"start": v(-6.26, -16.51) * mm, "end": v(-6.18, -16.5) * mm});
            skLineSegment(sketch, "E503", {"start": v(-6.18, -16.5) * mm, "end": v(-4.7, -16.5) * mm});
            skLineSegment(sketch, "E504", {"start": v(-4.7, -16.5) * mm, "end": v(-4.7, -16.5) * mm});
            skLineSegment(sketch, "E505", {"start": v(-4.7, -16.5) * mm, "end": v(-4.6, -16.51) * mm});
            skLineSegment(sketch, "E506", {"start": v(-4.6, -16.51) * mm, "end": v(-4.51, -16.54) * mm});
            skLineSegment(sketch, "E507", {"start": v(-4.51, -16.54) * mm, "end": v(-4.43, -16.59) * mm});
            skLineSegment(sketch, "E508", {"start": v(-4.43, -16.59) * mm, "end": v(-4.35, -16.65) * mm});
            skLineSegment(sketch, "E509", {"start": v(-4.35, -16.65) * mm, "end": v(-4.3, -16.72) * mm});
            skLineSegment(sketch, "E510", {"start": v(-4.3, -16.72) * mm, "end": v(-4.24, -16.8) * mm});
            skLineSegment(sketch, "E511", {"start": v(-4.24, -16.8) * mm, "end": v(-4.21, -16.9) * mm});
            skLineSegment(sketch, "E512", {"start": v(-4.21, -16.9) * mm, "end": v(-4.2, -17.05) * mm});
            skLineSegment(sketch, "E513", {"start": v(-4.2, -17.05) * mm, "end": v(-4.2, -17.37) * mm});
            skLineSegment(sketch, "E514", {"start": v(-4.2, -17.37) * mm, "end": v(-4.2, -17.5) * mm});
            skLineSegment(sketch, "E515", {"start": v(-4.2, -17.5) * mm, "end": v(-4.17, -17.59) * mm});
            skLineSegment(sketch, "E516", {"start": v(-4.17, -17.59) * mm, "end": v(-4.12, -17.67) * mm});
            skLineSegment(sketch, "E517", {"start": v(-4.12, -17.67) * mm, "end": v(-4.06, -17.75) * mm});
            skLineSegment(sketch, "E518", {"start": v(-4.06, -17.75) * mm, "end": v(-3.99, -17.8) * mm});
            skLineSegment(sketch, "E519", {"start": v(-3.99, -17.8) * mm, "end": v(-3.9, -17.85) * mm});
            skLineSegment(sketch, "E520", {"start": v(-3.9, -17.85) * mm, "end": v(-3.8, -17.88) * mm});
            skLineSegment(sketch, "E521", {"start": v(-3.8, -17.88) * mm, "end": v(-3.7, -17.9) * mm});
            skLineSegment(sketch, "E522", {"start": v(-3.7, -17.9) * mm, "end": v(3.71, -17.9) * mm});
            skLineSegment(sketch, "E523", {"start": v(3.71, -17.9) * mm, "end": v(3.81, -17.89) * mm});
            skLineSegment(sketch, "E524", {"start": v(3.81, -17.89) * mm, "end": v(3.9, -17.86) * mm});
            skLineSegment(sketch, "E525", {"start": v(3.9, -17.86) * mm, "end": v(4, -17.81) * mm});
            skLineSegment(sketch, "E526", {"start": v(4, -17.81) * mm, "end": v(4.06, -17.75) * mm});
            skLineSegment(sketch, "E527", {"start": v(4.06, -17.75) * mm, "end": v(4.13, -17.68) * mm});
            skLineSegment(sketch, "E528", {"start": v(4.13, -17.68) * mm, "end": v(4.17, -17.6) * mm});
            skLineSegment(sketch, "E529", {"start": v(4.17, -17.6) * mm, "end": v(4.2, -17.5) * mm});
            skLineSegment(sketch, "E530", {"start": v(4.2, -17.5) * mm, "end": v(4.21, -17.37) * mm});
            skLineSegment(sketch, "E531", {"start": v(4.21, -17.37) * mm, "end": v(4.21, -17) * mm});
            skLineSegment(sketch, "E532", {"start": v(4.21, -17) * mm, "end": v(4.22, -16.9) * mm});
            skLineSegment(sketch, "E533", {"start": v(4.22, -16.9) * mm, "end": v(4.25, -16.8) * mm});
            skLineSegment(sketch, "E534", {"start": v(4.25, -16.8) * mm, "end": v(4.3, -16.72) * mm});
            skLineSegment(sketch, "E535", {"start": v(4.3, -16.72) * mm, "end": v(4.36, -16.64) * mm});
            skLineSegment(sketch, "E536", {"start": v(4.36, -16.64) * mm, "end": v(4.43, -16.58) * mm});
            skLineSegment(sketch, "E537", {"start": v(4.43, -16.58) * mm, "end": v(4.52, -16.54) * mm});
            skLineSegment(sketch, "E538", {"start": v(4.52, -16.54) * mm, "end": v(4.6, -16.5) * mm});
            skLineSegment(sketch, "E539", {"start": v(4.6, -16.5) * mm, "end": v(4.71, -16.5) * mm});
            skLineSegment(sketch, "E540", {"start": v(4.71, -16.5) * mm, "end": v(4.71, -16.5) * mm});
            skLineSegment(sketch, "E541", {"start": v(4.71, -16.5) * mm, "end": v(6.16, -16.5) * mm});
            skLineSegment(sketch, "E542", {"start": v(6.16, -16.5) * mm, "end": v(6.16, -16.5) * mm});
            skLineSegment(sketch, "E543", {"start": v(6.16, -16.5) * mm, "end": v(6.26, -16.5) * mm});
            skLineSegment(sketch, "E544", {"start": v(6.26, -16.5) * mm, "end": v(6.35, -16.54) * mm});
            skLineSegment(sketch, "E545", {"start": v(6.35, -16.54) * mm, "end": v(6.44, -16.58) * mm});
            skLineSegment(sketch, "E546", {"start": v(6.44, -16.58) * mm, "end": v(6.51, -16.64) * mm});
            skLineSegment(sketch, "E547", {"start": v(6.51, -16.64) * mm, "end": v(6.57, -16.72) * mm});
            skLineSegment(sketch, "E548", {"start": v(6.57, -16.72) * mm, "end": v(6.62, -16.8) * mm});
            skLineSegment(sketch, "E549", {"start": v(6.62, -16.8) * mm, "end": v(6.65, -16.9) * mm});
            skLineSegment(sketch, "E550", {"start": v(6.65, -16.9) * mm, "end": v(6.66, -17) * mm});
            skLineSegment(sketch, "E551", {"start": v(6.66, -17) * mm, "end": v(6.66, -17) * mm});
            skLineSegment(sketch, "E552", {"start": v(6.66, -17) * mm, "end": v(6.66, -17.52) * mm});
            skLineSegment(sketch, "E553", {"start": v(6.66, -17.52) * mm, "end": v(6.67, -17.6) * mm});
            skLineSegment(sketch, "E554", {"start": v(6.67, -17.6) * mm, "end": v(6.7, -17.7) * mm});
            skLineSegment(sketch, "E555", {"start": v(6.7, -17.7) * mm, "end": v(6.75, -17.79) * mm});
            skLineSegment(sketch, "E556", {"start": v(6.75, -17.79) * mm, "end": v(6.76, -17.8) * mm});
            skLineSegment(sketch, "E557", {"start": v(6.76, -17.8) * mm, "end": v(9.04, -20.93) * mm});
            skLineSegment(sketch, "E558", {"start": v(9.04, -20.93) * mm, "end": v(9.07, -20.97) * mm});
            skLineSegment(sketch, "E559", {"start": v(9.07, -20.97) * mm, "end": v(9.1, -21) * mm});
            skLineSegment(sketch, "E560", {"start": v(9.1, -21) * mm, "end": v(9.15, -21.04) * mm});
            skLineSegment(sketch, "E561", {"start": v(9.15, -21.04) * mm, "end": v(9.2, -21.07) * mm});
            skLineSegment(sketch, "E562", {"start": v(9.2, -21.07) * mm, "end": v(9.24, -21.1) * mm});
            skLineSegment(sketch, "E563", {"start": v(9.24, -21.1) * mm, "end": v(9.29, -21.1) * mm});
            skLineSegment(sketch, "E564", {"start": v(9.29, -21.1) * mm, "end": v(9.33, -21.12) * mm});
            skLineSegment(sketch, "E565", {"start": v(9.33, -21.12) * mm, "end": v(9.59, -21.17) * mm});
            skLineSegment(sketch, "E566", {"start": v(9.59, -21.17) * mm, "end": v(9.79, -21.22) * mm});
            skLineSegment(sketch, "E567", {"start": v(9.79, -21.22) * mm, "end": v(9.98, -21.3) * mm});
            skLineSegment(sketch, "E568", {"start": v(9.98, -21.3) * mm, "end": v(10.16, -21.4) * mm});
            skLineSegment(sketch, "E569", {"start": v(10.16, -21.4) * mm, "end": v(10.33, -21.5) * mm});
            skLineSegment(sketch, "E570", {"start": v(10.33, -21.5) * mm, "end": v(10.49, -21.64) * mm});
            skLineSegment(sketch, "E571", {"start": v(10.49, -21.64) * mm, "end": v(10.63, -21.78) * mm});
            skLineSegment(sketch, "E572", {"start": v(10.63, -21.78) * mm, "end": v(10.77, -21.94) * mm});
            skLineSegment(sketch, "E573", {"start": v(10.77, -21.94) * mm, "end": v(10.88, -22.12) * mm});
            skLineSegment(sketch, "E574", {"start": v(10.88, -22.12) * mm, "end": v(10.97, -22.3) * mm});
            skLineSegment(sketch, "E575", {"start": v(10.97, -22.3) * mm, "end": v(11.05, -22.5) * mm});
            skLineSegment(sketch, "E576", {"start": v(11.05, -22.5) * mm, "end": v(11.1, -22.69) * mm});
            skLineSegment(sketch, "E577", {"start": v(11.1, -22.69) * mm, "end": v(11.13, -22.89) * mm});
            skLineSegment(sketch, "E578", {"start": v(11.13, -22.89) * mm, "end": v(11.15, -23.1) * mm});
            skLineSegment(sketch, "E579", {"start": v(11.15, -23.1) * mm, "end": v(11.14, -23.3) * mm});
            skLineSegment(sketch, "E580", {"start": v(11.14, -23.3) * mm, "end": v(11.1, -23.56) * mm});
            skLineSegment(sketch, "E581", {"start": v(11.1, -23.56) * mm, "end": v(11.1, -23.6) * mm});
            skLineSegment(sketch, "E582", {"start": v(11.1, -23.6) * mm, "end": v(11.1, -23.66) * mm});
            skLineSegment(sketch, "E583", {"start": v(11.1, -23.66) * mm, "end": v(11.11, -23.7) * mm});
            skLineSegment(sketch, "E584", {"start": v(11.11, -23.7) * mm, "end": v(11.13, -23.76) * mm});
            skLineSegment(sketch, "E585", {"start": v(11.13, -23.76) * mm, "end": v(11.14, -23.8) * mm});
            skLineSegment(sketch, "E586", {"start": v(11.14, -23.8) * mm, "end": v(11.17, -23.85) * mm});
            skLineSegment(sketch, "E587", {"start": v(11.17, -23.85) * mm, "end": v(11.2, -23.9) * mm});
            skLineSegment(sketch, "E588", {"start": v(11.2, -23.9) * mm, "end": v(11.94, -24.92) * mm});
            skLineSegment(sketch, "E589", {"start": v(11.94, -24.92) * mm, "end": v(15.61, -28.51) * mm});
            skLineSegment(sketch, "E590", {"start": v(15.61, -28.51) * mm, "end": v(15.75, -28.63) * mm});
            skLineSegment(sketch, "E591", {"start": v(15.75, -28.63) * mm, "end": v(15.9, -28.71) * mm});
            skLineSegment(sketch, "E592", {"start": v(15.9, -28.71) * mm, "end": v(16.07, -28.77) * mm});
            skLineSegment(sketch, "E593", {"start": v(16.07, -28.77) * mm, "end": v(16.24, -28.8) * mm});
            skLineSegment(sketch, "E594", {"start": v(16.24, -28.8) * mm, "end": v(16.41, -28.8) * mm});
            skLineSegment(sketch, "E595", {"start": v(16.41, -28.8) * mm, "end": v(16.58, -28.76) * mm});
            skLineSegment(sketch, "E596", {"start": v(16.58, -28.76) * mm, "end": v(16.75, -28.7) * mm});
            skLineSegment(sketch, "E597", {"start": v(16.75, -28.7) * mm, "end": v(16.9, -28.6) * mm});
            skLineSegment(sketch, "E598", {"start": v(16.9, -28.6) * mm, "end": v(19.74, -26.55) * mm});
            skLineSegment(sketch, "E599", {"start": v(19.74, -26.55) * mm, "end": v(19.88, -26.43) * mm});
            skLineSegment(sketch, "E600", {"start": v(19.88, -26.43) * mm, "end": v(19.99, -26.3) * mm});
            skLineSegment(sketch, "E601", {"start": v(19.99, -26.3) * mm, "end": v(20.07, -26.14) * mm});
            skLineSegment(sketch, "E602", {"start": v(20.07, -26.14) * mm, "end": v(20.12, -25.97) * mm});
            skLineSegment(sketch, "E603", {"start": v(20.12, -25.97) * mm, "end": v(20.15, -25.8) * mm});
            skLineSegment(sketch, "E604", {"start": v(20.15, -25.8) * mm, "end": v(20.15, -25.63) * mm});
            skLineSegment(sketch, "E605", {"start": v(20.15, -25.63) * mm, "end": v(20.11, -25.46) * mm});
            skLineSegment(sketch, "E606", {"start": v(20.11, -25.46) * mm, "end": v(20.05, -25.3) * mm});
            skLineSegment(sketch, "E607", {"start": v(20.05, -25.3) * mm, "end": v(17.76, -20.69) * mm});
            skLineSegment(sketch, "E608", {"start": v(17.76, -20.69) * mm, "end": v(17.02, -19.66) * mm});
            skLineSegment(sketch, "E609", {"start": v(17.02, -19.66) * mm, "end": v(16.99, -19.62) * mm});
            skLineSegment(sketch, "E610", {"start": v(16.99, -19.62) * mm, "end": v(16.95, -19.59) * mm});
            skLineSegment(sketch, "E611", {"start": v(16.95, -19.59) * mm, "end": v(16.91, -19.55) * mm});
            skLineSegment(sketch, "E612", {"start": v(16.91, -19.55) * mm, "end": v(16.87, -19.53) * mm});
            skLineSegment(sketch, "E613", {"start": v(16.87, -19.53) * mm, "end": v(16.82, -19.5) * mm});
            skLineSegment(sketch, "E614", {"start": v(16.82, -19.5) * mm, "end": v(16.78, -19.48) * mm});
            skLineSegment(sketch, "E615", {"start": v(16.78, -19.48) * mm, "end": v(16.73, -19.47) * mm});
            skLineSegment(sketch, "E616", {"start": v(16.73, -19.47) * mm, "end": v(16.47, -19.42) * mm});
            skLineSegment(sketch, "E617", {"start": v(16.47, -19.42) * mm, "end": v(16.27, -19.37) * mm});
            skLineSegment(sketch, "E618", {"start": v(16.27, -19.37) * mm, "end": v(16.08, -19.3) * mm});
            skLineSegment(sketch, "E619", {"start": v(16.08, -19.3) * mm, "end": v(15.9, -19.2) * mm});
            skLineSegment(sketch, "E620", {"start": v(15.9, -19.2) * mm, "end": v(15.73, -19.09) * mm});
            skLineSegment(sketch, "E621", {"start": v(15.73, -19.09) * mm, "end": v(15.57, -18.96) * mm});
            skLineSegment(sketch, "E622", {"start": v(15.57, -18.96) * mm, "end": v(15.43, -18.81) * mm});
            skLineSegment(sketch, "E623", {"start": v(15.43, -18.81) * mm, "end": v(15.3, -18.65) * mm});
            skLineSegment(sketch, "E624", {"start": v(15.3, -18.65) * mm, "end": v(15.18, -18.48) * mm});
            skLineSegment(sketch, "E625", {"start": v(15.18, -18.48) * mm, "end": v(15.09, -18.3) * mm});
            skLineSegment(sketch, "E626", {"start": v(15.09, -18.3) * mm, "end": v(15.01, -18.1) * mm});
            skLineSegment(sketch, "E627", {"start": v(15.01, -18.1) * mm, "end": v(14.96, -17.9) * mm});
            skLineSegment(sketch, "E628", {"start": v(14.96, -17.9) * mm, "end": v(14.93, -17.7) * mm});
            skLineSegment(sketch, "E629", {"start": v(14.93, -17.7) * mm, "end": v(14.91, -17.5) * mm});
            skLineSegment(sketch, "E630", {"start": v(14.91, -17.5) * mm, "end": v(14.92, -17.3) * mm});
            skLineSegment(sketch, "E631", {"start": v(14.92, -17.3) * mm, "end": v(14.96, -17.04) * mm});
            skLineSegment(sketch, "E632", {"start": v(14.96, -17.04) * mm, "end": v(14.96, -16.98) * mm});
            skLineSegment(sketch, "E633", {"start": v(14.96, -16.98) * mm, "end": v(14.96, -16.93) * mm});
            skLineSegment(sketch, "E634", {"start": v(14.96, -16.93) * mm, "end": v(14.95, -16.88) * mm});
            skLineSegment(sketch, "E635", {"start": v(14.95, -16.88) * mm, "end": v(14.94, -16.83) * mm});
            skLineSegment(sketch, "E636", {"start": v(14.94, -16.83) * mm, "end": v(14.92, -16.79) * mm});
            skLineSegment(sketch, "E637", {"start": v(14.92, -16.79) * mm, "end": v(14.9, -16.74) * mm});
            skLineSegment(sketch, "E638", {"start": v(14.9, -16.74) * mm, "end": v(14.87, -16.7) * mm});
            skLineSegment(sketch, "E639", {"start": v(14.87, -16.7) * mm, "end": v(11.63, -12.24) * mm});
            skLineSegment(sketch, "E640", {"start": v(11.63, -12.24) * mm, "end": v(11.6, -12.2) * mm});
            skLineSegment(sketch, "E641", {"start": v(11.6, -12.2) * mm, "end": v(11.6, -12.16) * mm});
            skLineSegment(sketch, "E642", {"start": v(11.6, -12.16) * mm, "end": v(11.58, -12.13) * mm});
            skLineSegment(sketch, "E643", {"start": v(11.58, -12.13) * mm, "end": v(11.57, -12.1) * mm});
            skLineSegment(sketch, "E644", {"start": v(11.57, -12.1) * mm, "end": v(11.57, -12.06) * mm});
            skLineSegment(sketch, "E645", {"start": v(11.57, -12.06) * mm, "end": v(11.57, -12.04) * mm});
            skLineSegment(sketch, "E646", {"start": v(11.57, -12.04) * mm, "end": v(11.57, -12) * mm});
            skLineSegment(sketch, "E647", {"start": v(11.57, -12) * mm, "end": v(11.57, -11.96) * mm});
            skLineSegment(sketch, "E648", {"start": v(11.57, -11.96) * mm, "end": v(11.58, -11.93) * mm});
            skLineSegment(sketch, "E649", {"start": v(11.58, -11.93) * mm, "end": v(11.6, -11.9) * mm});
            skLineSegment(sketch, "E650", {"start": v(11.6, -11.9) * mm, "end": v(11.6, -11.87) * mm});
            skLineSegment(sketch, "E651", {"start": v(11.6, -11.87) * mm, "end": v(11.63, -11.84) * mm});
            skLineSegment(sketch, "E652", {"start": v(11.63, -11.84) * mm, "end": v(11.65, -11.81) * mm});
            skLineSegment(sketch, "E653", {"start": v(11.65, -11.81) * mm, "end": v(11.67, -11.78) * mm});
            skLineSegment(sketch, "E654", {"start": v(11.67, -11.78) * mm, "end": v(12.41, -10.79) * mm});
            skLineSegment(sketch, "E655", {"start": v(12.41, -10.79) * mm, "end": v(13.07, -9.73) * mm});
            skLineSegment(sketch, "E656", {"start": v(13.07, -9.73) * mm, "end": v(13.64, -8.61) * mm});
            skLineSegment(sketch, "E657", {"start": v(13.64, -8.61) * mm, "end": v(14.12, -7.45) * mm});
            skLineSegment(sketch, "E658", {"start": v(14.12, -7.45) * mm, "end": v(14.5, -6.23) * mm});
            skLineSegment(sketch, "E659", {"start": v(14.5, -6.23) * mm, "end": v(14.77, -4.98) * mm});
            skLineSegment(sketch, "E660", {"start": v(14.77, -4.98) * mm, "end": v(14.94, -3.69) * mm});
            skLineSegment(sketch, "E661", {"start": v(14.94, -3.69) * mm, "end": v(15, -2.36) * mm});
            skLineSegment(sketch, "E662", {"start": v(15, -2.36) * mm, "end": v(15, -2) * mm});
            skLineSegment(sketch, "E663", {"start": v(15, -2) * mm, "end": v(14.98, -1.58) * mm});
            skLineSegment(sketch, "E664", {"start": v(14.98, -1.58) * mm, "end": v(14.98, -1.55) * mm});
            skLineSegment(sketch, "E665", {"start": v(14.98, -1.55) * mm, "end": v(14.98, -1.5) * mm});
            skLineSegment(sketch, "E666", {"start": v(14.98, -1.5) * mm, "end": v(14.99, -1.47) * mm});
            skLineSegment(sketch, "E667", {"start": v(14.99, -1.47) * mm, "end": v(15, -1.43) * mm});
            skLineSegment(sketch, "E668", {"start": v(15, -1.43) * mm, "end": v(15, -1.4) * mm});
            skLineSegment(sketch, "E669", {"start": v(15, -1.4) * mm, "end": v(15.02, -1.36) * mm});
            skLineSegment(sketch, "E670", {"start": v(15.02, -1.36) * mm, "end": v(15.04, -1.33) * mm});
            skLineSegment(sketch, "E671", {"start": v(15.04, -1.33) * mm, "end": v(15.06, -1.3) * mm});
            skLineSegment(sketch, "E672", {"start": v(15.06, -1.3) * mm, "end": v(15.1, -1.28) * mm});
            skLineSegment(sketch, "E673", {"start": v(15.1, -1.28) * mm, "end": v(15.12, -1.26) * mm});
            skLineSegment(sketch, "E674", {"start": v(15.12, -1.26) * mm, "end": v(15.15, -1.24) * mm});
            skLineSegment(sketch, "E675", {"start": v(15.15, -1.24) * mm, "end": v(15.18, -1.22) * mm});
            skLineSegment(sketch, "E676", {"start": v(15.18, -1.22) * mm, "end": v(15.2, -1.21) * mm});
            skLineSegment(sketch, "E677", {"start": v(15.2, -1.21) * mm, "end": v(15.23, -1.2) * mm});
            skLineSegment(sketch, "E678", {"start": v(15.23, -1.2) * mm, "end": v(20.45, 0.5) * mm});
            skLineSegment(sketch, "E679", {"start": v(20.45, 0.5) * mm, "end": v(20.5, 0.52) * mm});
            skLineSegment(sketch, "E680", {"start": v(20.5, 0.52) * mm, "end": v(20.54, 0.54) * mm});
            skLineSegment(sketch, "E681", {"start": v(20.54, 0.54) * mm, "end": v(20.59, 0.57) * mm});
            skLineSegment(sketch, "E682", {"start": v(20.59, 0.57) * mm, "end": v(20.63, 0.6) * mm});
            skLineSegment(sketch, "E683", {"start": v(20.63, 0.6) * mm, "end": v(20.66, 0.63) * mm});
            skLineSegment(sketch, "E684", {"start": v(20.66, 0.63) * mm, "end": v(20.7, 0.67) * mm});
            skLineSegment(sketch, "E685", {"start": v(20.7, 0.67) * mm, "end": v(20.73, 0.72) * mm});
            skLineSegment(sketch, "E686", {"start": v(20.73, 0.72) * mm, "end": v(20.85, 0.95) * mm});
            skLineSegment(sketch, "E687", {"start": v(20.85, 0.95) * mm, "end": v(20.96, 1.12) * mm});
            skLineSegment(sketch, "E688", {"start": v(20.96, 1.12) * mm, "end": v(21.1, 1.27) * mm});
            skLineSegment(sketch, "E689", {"start": v(21.1, 1.27) * mm, "end": v(21.24, 1.42) * mm});
            skLineSegment(sketch, "E690", {"start": v(21.24, 1.42) * mm, "end": v(21.4, 1.55) * mm});
            skLineSegment(sketch, "E691", {"start": v(21.4, 1.55) * mm, "end": v(21.57, 1.66) * mm});
            skLineSegment(sketch, "E692", {"start": v(21.57, 1.66) * mm, "end": v(21.75, 1.75) * mm});
            skLineSegment(sketch, "E693", {"start": v(21.75, 1.75) * mm, "end": v(21.95, 1.82) * mm});
            skLineSegment(sketch, "E694", {"start": v(21.95, 1.82) * mm, "end": v(22.15, 1.88) * mm});
            skLineSegment(sketch, "E695", {"start": v(22.15, 1.88) * mm, "end": v(22.35, 1.91) * mm});
            skLineSegment(sketch, "E696", {"start": v(22.35, 1.91) * mm, "end": v(22.55, 1.92) * mm});
            skLineSegment(sketch, "E697", {"start": v(22.55, 1.92) * mm, "end": v(22.76, 1.91) * mm});
            skLineSegment(sketch, "E698", {"start": v(22.76, 1.91) * mm, "end": v(22.96, 1.88) * mm});
            skLineSegment(sketch, "E699", {"start": v(22.96, 1.88) * mm, "end": v(23.16, 1.83) * mm});
            skLineSegment(sketch, "E700", {"start": v(23.16, 1.83) * mm, "end": v(23.35, 1.76) * mm});
            skLineSegment(sketch, "E701", {"start": v(23.35, 1.76) * mm, "end": v(23.59, 1.65) * mm});
            skLineSegment(sketch, "E702", {"start": v(23.59, 1.65) * mm, "end": v(23.63, 1.63) * mm});
            skLineSegment(sketch, "E703", {"start": v(23.63, 1.63) * mm, "end": v(23.68, 1.61) * mm});
            skLineSegment(sketch, "E704", {"start": v(23.68, 1.61) * mm, "end": v(23.73, 1.6) * mm});
            skLineSegment(sketch, "E705", {"start": v(23.73, 1.6) * mm, "end": v(23.79, 1.6) * mm});
            skLineSegment(sketch, "E706", {"start": v(23.79, 1.6) * mm, "end": v(23.84, 1.6) * mm});
            skLineSegment(sketch, "E707", {"start": v(23.84, 1.6) * mm, "end": v(23.89, 1.62) * mm});
            skLineSegment(sketch, "E708", {"start": v(23.89, 1.62) * mm, "end": v(23.94, 1.63) * mm});
            skLineSegment(sketch, "E709", {"start": v(23.94, 1.63) * mm, "end": v(25.14, 2.02) * mm});
            skLineSegment(sketch, "E710", {"start": v(25.14, 2.02) * mm, "end": v(29.7, 4.4) * mm});
            skLineSegment(sketch, "E711", {"start": v(29.7, 4.4) * mm, "end": v(29.85, 4.5) * mm});
            skLineSegment(sketch, "E712", {"start": v(29.85, 4.5) * mm, "end": v(29.98, 4.62) * mm});
            skLineSegment(sketch, "E713", {"start": v(29.98, 4.62) * mm, "end": v(30.08, 4.76) * mm});
            skLineSegment(sketch, "E714", {"start": v(30.08, 4.76) * mm, "end": v(30.16, 4.91) * mm});
            skLineSegment(sketch, "E715", {"start": v(30.16, 4.91) * mm, "end": v(30.2, 5.08) * mm});
            skLineSegment(sketch, "E716", {"start": v(30.2, 5.08) * mm, "end": v(30.23, 5.25) * mm});
            skLineSegment(sketch, "E717", {"start": v(30.23, 5.25) * mm, "end": v(30.22, 5.42) * mm});
            skLineSegment(sketch, "E718", {"start": v(-6.23, -2.28) * mm, "end": v(-6.23, -1.51) * mm});
            skArc(sketch, "E719", {"start": v(-6.23, -1.51) * mm, "mid": v(-6.26, -1.45) * mm, "end": v(-6.31, -1.43) * mm});
            skLineSegment(sketch, "E720", {"start": v(-6.31, -1.43) * mm, "end": v(-7.19, -1.43) * mm});
            skArc(sketch, "E721", {"start": v(-7.19, -1.43) * mm, "mid": v(-7.24, -1.45) * mm, "end": v(-7.27, -1.51) * mm});
            skLineSegment(sketch, "E722", {"start": v(-7.27, -1.51) * mm, "end": v(-7.27, -2.28) * mm});
            skArc(sketch, "E723", {"start": v(-7.27, -2.28) * mm, "mid": v(-7.24, -2.34) * mm, "end": v(-7.19, -2.37) * mm});
            skLineSegment(sketch, "E724", {"start": v(-7.19, -2.37) * mm, "end": v(-6.31, -2.37) * mm});
            skArc(sketch, "E725", {"start": v(-6.31, -2.37) * mm, "mid": v(-6.26, -2.34) * mm, "end": v(-6.23, -2.28) * mm});
            skLineSegment(sketch, "E726", {"start": v(-4.53, -2.28) * mm, "end": v(-4.53, -1.51) * mm});
            skArc(sketch, "E727", {"start": v(-4.53, -1.51) * mm, "mid": v(-4.56, -1.45) * mm, "end": v(-4.61, -1.43) * mm});
            skLineSegment(sketch, "E728", {"start": v(-4.61, -1.43) * mm, "end": v(-5.49, -1.43) * mm});
            skArc(sketch, "E729", {"start": v(-5.49, -1.43) * mm, "mid": v(-5.54, -1.45) * mm, "end": v(-5.57, -1.51) * mm});
            skLineSegment(sketch, "E730", {"start": v(-5.57, -1.51) * mm, "end": v(-5.57, -2.28) * mm});
            skArc(sketch, "E731", {"start": v(-5.57, -2.28) * mm, "mid": v(-5.54, -2.34) * mm, "end": v(-5.49, -2.37) * mm});
            skLineSegment(sketch, "E732", {"start": v(-5.49, -2.37) * mm, "end": v(-4.61, -2.37) * mm});
            skArc(sketch, "E733", {"start": v(-4.61, -2.37) * mm, "mid": v(-4.56, -2.34) * mm, "end": v(-4.53, -2.28) * mm});
            skLineSegment(sketch, "E734", {"start": v(-6.27, 1.37) * mm, "end": v(-6.27, 2.14) * mm});
            skArc(sketch, "E735", {"start": v(-6.27, 2.14) * mm, "mid": v(-6.3, 2.2) * mm, "end": v(-6.35, 2.22) * mm});
            skLineSegment(sketch, "E736", {"start": v(-6.35, 2.22) * mm, "end": v(-7.23, 2.22) * mm});
            skArc(sketch, "E737", {"start": v(-7.23, 2.22) * mm, "mid": v(-7.28, 2.2) * mm, "end": v(-7.3, 2.14) * mm});
            skLineSegment(sketch, "E738", {"start": v(-7.3, 2.14) * mm, "end": v(-7.3, 1.37) * mm});
            skArc(sketch, "E739", {"start": v(-7.3, 1.37) * mm, "mid": v(-7.28, 1.3) * mm, "end": v(-7.23, 1.28) * mm});
            skLineSegment(sketch, "E740", {"start": v(-7.23, 1.28) * mm, "end": v(-6.35, 1.28) * mm});
            skArc(sketch, "E741", {"start": v(-6.35, 1.28) * mm, "mid": v(-6.3, 1.3) * mm, "end": v(-6.27, 1.37) * mm});
            skLineSegment(sketch, "E742", {"start": v(-4.57, 1.37) * mm, "end": v(-4.57, 2.14) * mm});
            skArc(sketch, "E743", {"start": v(-4.57, 2.14) * mm, "mid": v(-4.6, 2.2) * mm, "end": v(-4.65, 2.22) * mm});
            skLineSegment(sketch, "E744", {"start": v(-4.65, 2.22) * mm, "end": v(-5.53, 2.22) * mm});
            skArc(sketch, "E745", {"start": v(-5.53, 2.22) * mm, "mid": v(-5.58, 2.2) * mm, "end": v(-5.6, 2.14) * mm});
            skLineSegment(sketch, "E746", {"start": v(-5.6, 2.14) * mm, "end": v(-5.6, 1.37) * mm});
            skArc(sketch, "E747", {"start": v(-5.6, 1.37) * mm, "mid": v(-5.58, 1.3) * mm, "end": v(-5.53, 1.28) * mm});
            skLineSegment(sketch, "E748", {"start": v(-5.53, 1.28) * mm, "end": v(-4.65, 1.28) * mm});
            skArc(sketch, "E749", {"start": v(-4.65, 1.28) * mm, "mid": v(-4.6, 1.3) * mm, "end": v(-4.57, 1.37) * mm});
            skLineSegment(sketch, "E750", {"start": v(8.02, -5.3) * mm, "end": v(8.02, -6.07) * mm});
            skArc(sketch, "E751", {"start": v(8.02, -6.07) * mm, "mid": v(8.05, -6.13) * mm, "end": v(8.1, -6.16) * mm});
            skLineSegment(sketch, "E752", {"start": v(8.1, -6.16) * mm, "end": v(8.98, -6.16) * mm});
            skArc(sketch, "E753", {"start": v(8.98, -6.16) * mm, "mid": v(9.03, -6.13) * mm, "end": v(9.06, -6.07) * mm});
            skLineSegment(sketch, "E754", {"start": v(9.06, -6.07) * mm, "end": v(9.06, -5.3) * mm});
            skArc(sketch, "E755", {"start": v(9.06, -5.3) * mm, "mid": v(9.03, -5.24) * mm, "end": v(8.98, -5.22) * mm});
            skLineSegment(sketch, "E756", {"start": v(8.98, -5.22) * mm, "end": v(8.1, -5.22) * mm});
            skArc(sketch, "E757", {"start": v(8.1, -5.22) * mm, "mid": v(8.05, -5.24) * mm, "end": v(8.02, -5.3) * mm});
            skLineSegment(sketch, "E758", {"start": v(6.32, -5.3) * mm, "end": v(6.32, -6.07) * mm});
            skArc(sketch, "E759", {"start": v(6.32, -6.07) * mm, "mid": v(6.35, -6.13) * mm, "end": v(6.4, -6.16) * mm});
            skLineSegment(sketch, "E760", {"start": v(6.4, -6.16) * mm, "end": v(7.28, -6.16) * mm});
            skArc(sketch, "E761", {"start": v(7.28, -6.16) * mm, "mid": v(7.33, -6.13) * mm, "end": v(7.36, -6.07) * mm});
            skLineSegment(sketch, "E762", {"start": v(7.36, -6.07) * mm, "end": v(7.36, -5.3) * mm});
            skArc(sketch, "E763", {"start": v(7.36, -5.3) * mm, "mid": v(7.33, -5.24) * mm, "end": v(7.28, -5.22) * mm});
            skLineSegment(sketch, "E764", {"start": v(7.28, -5.22) * mm, "end": v(6.4, -5.22) * mm});
            skArc(sketch, "E765", {"start": v(6.4, -5.22) * mm, "mid": v(6.35, -5.24) * mm, "end": v(6.32, -5.3) * mm});
            skLineSegment(sketch, "E766", {"start": v(-2.19, -9.57) * mm, "end": v(-1.41, -9.57) * mm});
            skArc(sketch, "E767", {"start": v(-1.41, -9.57) * mm, "mid": v(-1.36, -9.54) * mm, "end": v(-1.33, -9.48) * mm});
            skLineSegment(sketch, "E768", {"start": v(-1.33, -9.48) * mm, "end": v(-1.33, -8.61) * mm});
            skArc(sketch, "E769", {"start": v(-1.33, -8.61) * mm, "mid": v(-1.36, -8.55) * mm, "end": v(-1.41, -8.53) * mm});
            skLineSegment(sketch, "E770", {"start": v(-1.41, -8.53) * mm, "end": v(-2.19, -8.53) * mm});
            skArc(sketch, "E771", {"start": v(-2.19, -8.53) * mm, "mid": v(-2.24, -8.55) * mm, "end": v(-2.27, -8.61) * mm});
            skLineSegment(sketch, "E772", {"start": v(-2.27, -8.61) * mm, "end": v(-2.27, -9.48) * mm});
            skArc(sketch, "E773", {"start": v(-2.27, -9.48) * mm, "mid": v(-2.24, -9.54) * mm, "end": v(-2.19, -9.57) * mm});
            skLineSegment(sketch, "E774", {"start": v(-2.19, -11.27) * mm, "end": v(-1.41, -11.27) * mm});
            skArc(sketch, "E775", {"start": v(-1.41, -11.27) * mm, "mid": v(-1.36, -11.24) * mm, "end": v(-1.33, -11.18) * mm});
            skLineSegment(sketch, "E776", {"start": v(-1.33, -11.18) * mm, "end": v(-1.33, -10.31) * mm});
            skArc(sketch, "E777", {"start": v(-1.33, -10.31) * mm, "mid": v(-1.36, -10.25) * mm, "end": v(-1.41, -10.23) * mm});
            skLineSegment(sketch, "E778", {"start": v(-1.41, -10.23) * mm, "end": v(-2.19, -10.23) * mm});
            skArc(sketch, "E779", {"start": v(-2.19, -10.23) * mm, "mid": v(-2.24, -10.25) * mm, "end": v(-2.27, -10.31) * mm});
            skLineSegment(sketch, "E780", {"start": v(-2.27, -10.31) * mm, "end": v(-2.27, -11.18) * mm});
            skArc(sketch, "E781", {"start": v(-2.27, -11.18) * mm, "mid": v(-2.24, -11.24) * mm, "end": v(-2.19, -11.27) * mm});
            skLineSegment(sketch, "E782", {"start": v(-0.37, -9.59) * mm, "end": v(0.4, -9.59) * mm});
            skArc(sketch, "E783", {"start": v(0.4, -9.59) * mm, "mid": v(0.46, -9.56) * mm, "end": v(0.49, -9.5) * mm});
            skLineSegment(sketch, "E784", {"start": v(0.49, -9.5) * mm, "end": v(0.49, -8.63) * mm});
            skArc(sketch, "E785", {"start": v(0.49, -8.63) * mm, "mid": v(0.46, -8.57) * mm, "end": v(0.4, -8.55) * mm});
            skLineSegment(sketch, "E786", {"start": v(0.4, -8.55) * mm, "end": v(-0.37, -8.55) * mm});
            skArc(sketch, "E787", {"start": v(-0.37, -8.55) * mm, "mid": v(-0.42, -8.57) * mm, "end": v(-0.45, -8.63) * mm});
            skLineSegment(sketch, "E788", {"start": v(-0.45, -8.63) * mm, "end": v(-0.45, -9.5) * mm});
            skArc(sketch, "E789", {"start": v(-0.45, -9.5) * mm, "mid": v(-0.42, -9.56) * mm, "end": v(-0.37, -9.59) * mm});
            skLineSegment(sketch, "E790", {"start": v(-0.37, -11.29) * mm, "end": v(0.4, -11.29) * mm});
            skArc(sketch, "E791", {"start": v(0.4, -11.29) * mm, "mid": v(0.46, -11.26) * mm, "end": v(0.49, -11.2) * mm});
            skLineSegment(sketch, "E792", {"start": v(0.49, -11.2) * mm, "end": v(0.49, -10.33) * mm});
            skArc(sketch, "E793", {"start": v(0.49, -10.33) * mm, "mid": v(0.46, -10.27) * mm, "end": v(0.4, -10.25) * mm});
            skLineSegment(sketch, "E794", {"start": v(0.4, -10.25) * mm, "end": v(-0.37, -10.25) * mm});
            skArc(sketch, "E795", {"start": v(-0.37, -10.25) * mm, "mid": v(-0.42, -10.27) * mm, "end": v(-0.45, -10.33) * mm});
            skLineSegment(sketch, "E796", {"start": v(-0.45, -10.33) * mm, "end": v(-0.45, -11.2) * mm});
            skArc(sketch, "E797", {"start": v(-0.45, -11.2) * mm, "mid": v(-0.42, -11.26) * mm, "end": v(-0.37, -11.29) * mm});
            skLineSegment(sketch, "E798", {"start": v(-2.25, 18.36) * mm, "end": v(-2.23, 14.76) * mm});
            skArc(sketch, "E799", {"start": v(-2.36, 14.76) * mm, "mid": v(-2.23, 14.63) * mm, "end": v(-2.1, 14.76) * mm});
            skArc(sketch, "E800", {"start": v(-2.12, 18.36) * mm, "mid": v(-2.25, 18.48) * mm, "end": v(-2.37, 18.36) * mm});
            skLineSegment(sketch, "E801", {"start": v(-2.23, 14.76) * mm, "end": v(-2.2, 14.53) * mm});
            skArc(sketch, "E802", {"start": v(-2.32, 14.51) * mm, "mid": v(-2.18, 14.4) * mm, "end": v(-2.07, 14.55) * mm});
            skArc(sketch, "E803", {"start": v(-2.1, 14.78) * mm, "mid": v(-2.25, 14.88) * mm, "end": v(-2.36, 14.74) * mm});
            skLineSegment(sketch, "E804", {"start": v(-2.2, 14.53) * mm, "end": v(-2.14, 14.32) * mm});
            skArc(sketch, "E805", {"start": v(-2.26, 14.29) * mm, "mid": v(-2.11, 14.2) * mm, "end": v(-2.02, 14.35) * mm});
            skArc(sketch, "E806", {"start": v(-2.08, 14.56) * mm, "mid": v(-2.23, 14.65) * mm, "end": v(-2.32, 14.5) * mm});
            skLineSegment(sketch, "E807", {"start": v(-2.14, 14.32) * mm, "end": v(-2.06, 14.11) * mm});
            skArc(sketch, "E808", {"start": v(-2.18, 14.07) * mm, "mid": v(-2.02, 14) * mm, "end": v(-1.95, 14.16) * mm});
            skArc(sketch, "E809", {"start": v(-2.02, 14.36) * mm, "mid": v(-2.19, 14.43) * mm, "end": v(-2.26, 14.27) * mm});
            skLineSegment(sketch, "E810", {"start": v(-2.06, 14.11) * mm, "end": v(-1.97, 13.92) * mm});
            skArc(sketch, "E811", {"start": v(-2.08, 13.86) * mm, "mid": v(-1.91, 13.8) * mm, "end": v(-1.86, 13.97) * mm});
            skArc(sketch, "E812", {"start": v(-1.95, 14.17) * mm, "mid": v(-2.12, 14.22) * mm, "end": v(-2.18, 14.06) * mm});
            skLineSegment(sketch, "E813", {"start": v(-1.97, 13.92) * mm, "end": v(-1.86, 13.73) * mm});
            skArc(sketch, "E814", {"start": v(-1.96, 13.67) * mm, "mid": v(-1.8, 13.62) * mm, "end": v(-1.75, 13.8) * mm});
            skArc(sketch, "E815", {"start": v(-1.86, 13.98) * mm, "mid": v(-2.03, 14.02) * mm, "end": v(-2.08, 13.85) * mm});
            skLineSegment(sketch, "E816", {"start": v(-1.86, 13.73) * mm, "end": v(-1.72, 13.56) * mm});
            skArc(sketch, "E817", {"start": v(-1.82, 13.48) * mm, "mid": v(-1.65, 13.46) * mm, "end": v(-1.63, 13.63) * mm});
            skArc(sketch, "E818", {"start": v(-1.76, 13.8) * mm, "mid": v(-1.93, 13.83) * mm, "end": v(-1.96, 13.66) * mm});
            skLineSegment(sketch, "E819", {"start": v(-1.72, 13.56) * mm, "end": v(-1.58, 13.4) * mm});
            skArc(sketch, "E820", {"start": v(-1.67, 13.31) * mm, "mid": v(-1.5, 13.3) * mm, "end": v(-1.49, 13.48) * mm});
            skArc(sketch, "E821", {"start": v(-1.63, 13.64) * mm, "mid": v(-1.8, 13.65) * mm, "end": v(-1.82, 13.47) * mm});
            skLineSegment(sketch, "E822", {"start": v(-1.58, 13.4) * mm, "end": v(-1.42, 13.25) * mm});
            skArc(sketch, "E823", {"start": v(-1.5, 13.16) * mm, "mid": v(-1.33, 13.17) * mm, "end": v(-1.33, 13.35) * mm});
            skArc(sketch, "E824", {"start": v(-1.5, 13.5) * mm, "mid": v(-1.67, 13.48) * mm, "end": v(-1.66, 13.3) * mm});
            skLineSegment(sketch, "E825", {"start": v(-1.42, 13.25) * mm, "end": v(-1.24, 13.13) * mm});
            skArc(sketch, "E826", {"start": v(-1.32, 13.03) * mm, "mid": v(-1.14, 13.05) * mm, "end": v(-1.17, 13.23) * mm});
            skArc(sketch, "E827", {"start": v(-1.34, 13.36) * mm, "mid": v(-1.52, 13.33) * mm, "end": v(-1.5, 13.15) * mm});
            skLineSegment(sketch, "E828", {"start": v(-1.24, 13.13) * mm, "end": v(-1.06, 13.01) * mm});
            skArc(sketch, "E829", {"start": v(-1.12, 12.9) * mm, "mid": v(-0.95, 12.95) * mm, "end": v(-1, 13.12) * mm});
            skArc(sketch, "E830", {"start": v(-1.18, 13.23) * mm, "mid": v(-1.35, 13.2) * mm, "end": v(-1.3, 13.02) * mm});
            skLineSegment(sketch, "E831", {"start": v(-1.06, 13.01) * mm, "end": v(-0.86, 12.92) * mm});
            skArc(sketch, "E832", {"start": v(-0.91, 12.8) * mm, "mid": v(-0.75, 12.87) * mm, "end": v(-0.8, 13.03) * mm});
            skArc(sketch, "E833", {"start": v(-1, 13.13) * mm, "mid": v(-1.17, 13.07) * mm, "end": v(-1.11, 12.9) * mm});
            skLineSegment(sketch, "E834", {"start": v(-0.86, 12.92) * mm, "end": v(-0.65, 12.85) * mm});
            skArc(sketch, "E835", {"start": v(-0.7, 12.73) * mm, "mid": v(-0.54, 12.8) * mm, "end": v(-0.61, 12.96) * mm});
            skArc(sketch, "E836", {"start": v(-0.82, 13.04) * mm, "mid": v(-0.98, 12.96) * mm, "end": v(-0.9, 12.8) * mm});
            skLineSegment(sketch, "E837", {"start": v(-0.65, 12.85) * mm, "end": v(-0.44, 12.8) * mm});
            skArc(sketch, "E838", {"start": v(-0.47, 12.67) * mm, "mid": v(-0.32, 12.76) * mm, "end": v(-0.4, 12.91) * mm});
            skArc(sketch, "E839", {"start": v(-0.62, 12.97) * mm, "mid": v(-0.77, 12.88) * mm, "end": v(-0.68, 12.72) * mm});
            skLineSegment(sketch, "E840", {"start": v(-0.44, 12.8) * mm, "end": v(-0.21, 12.76) * mm});
            skArc(sketch, "E841", {"start": v(-0.23, 12.64) * mm, "mid": v(-0.1, 12.74) * mm, "end": v(-0.2, 12.88) * mm});
            skArc(sketch, "E842", {"start": v(-0.42, 12.92) * mm, "mid": v(-0.56, 12.8) * mm, "end": v(-0.46, 12.67) * mm});
            skLineSegment(sketch, "E843", {"start": v(-0.21, 12.76) * mm, "end": v(0, 12.75) * mm});
            skArc(sketch, "E844", {"start": v(0, 12.62) * mm, "mid": v(0.13, 12.74) * mm, "end": v(0, 12.87) * mm});
            skArc(sketch, "E845", {"start": v(-0.2, 12.88) * mm, "mid": v(-0.34, 12.76) * mm, "end": v(-0.22, 12.63) * mm});
            skLineSegment(sketch, "E846", {"start": v(0, 12.75) * mm, "end": v(0.25, 12.76) * mm});
            skArc(sketch, "E847", {"start": v(0.25, 12.64) * mm, "mid": v(0.37, 12.77) * mm, "end": v(0.24, 12.89) * mm});
            skArc(sketch, "E848", {"start": v(0, 12.87) * mm, "mid": v(-0.12, 12.74) * mm, "end": v(0, 12.62) * mm});
            skLineSegment(sketch, "E849", {"start": v(0.25, 12.76) * mm, "end": v(0.47, 12.8) * mm});
            skArc(sketch, "E850", {"start": v(0.49, 12.67) * mm, "mid": v(0.6, 12.82) * mm, "end": v(0.45, 12.92) * mm});
            skArc(sketch, "E851", {"start": v(0.23, 12.88) * mm, "mid": v(0.12, 12.74) * mm, "end": v(0.27, 12.64) * mm});
            skLineSegment(sketch, "E852", {"start": v(0.47, 12.8) * mm, "end": v(0.69, 12.85) * mm});
            skArc(sketch, "E853", {"start": v(0.72, 12.73) * mm, "mid": v(0.8, 12.88) * mm, "end": v(0.65, 12.97) * mm});
            skArc(sketch, "E854", {"start": v(0.44, 12.92) * mm, "mid": v(0.35, 12.76) * mm, "end": v(0.5, 12.68) * mm});
            skLineSegment(sketch, "E855", {"start": v(0.69, 12.85) * mm, "end": v(0.9, 12.93) * mm});
            skArc(sketch, "E856", {"start": v(0.93, 12.81) * mm, "mid": v(1, 12.97) * mm, "end": v(0.85, 13.05) * mm});
            skArc(sketch, "E857", {"start": v(0.64, 12.97) * mm, "mid": v(0.57, 12.8) * mm, "end": v(0.73, 12.74) * mm});
            skLineSegment(sketch, "E858", {"start": v(0.9, 12.93) * mm, "end": v(1.09, 13.03) * mm});
            skArc(sketch, "E859", {"start": v(1.14, 12.91) * mm, "mid": v(1.2, 13.08) * mm, "end": v(1.03, 13.14) * mm});
            skArc(sketch, "E860", {"start": v(0.84, 13.04) * mm, "mid": v(0.78, 12.88) * mm, "end": v(0.95, 12.82) * mm});
            skLineSegment(sketch, "E861", {"start": v(1.09, 13.03) * mm, "end": v(1.27, 13.14) * mm});
            skArc(sketch, "E862", {"start": v(1.34, 13.03) * mm, "mid": v(1.38, 13.2) * mm, "end": v(1.2, 13.25) * mm});
            skArc(sketch, "E863", {"start": v(1.02, 13.13) * mm, "mid": v(0.98, 12.96) * mm, "end": v(1.15, 12.92) * mm});
            skLineSegment(sketch, "E864", {"start": v(1.27, 13.14) * mm, "end": v(1.44, 13.27) * mm});
            skArc(sketch, "E865", {"start": v(1.52, 13.17) * mm, "mid": v(1.54, 13.35) * mm, "end": v(1.37, 13.37) * mm});
            skArc(sketch, "E866", {"start": v(1.2, 13.24) * mm, "mid": v(1.17, 13.06) * mm, "end": v(1.35, 13.04) * mm});
            skLineSegment(sketch, "E867", {"start": v(1.44, 13.27) * mm, "end": v(1.6, 13.42) * mm});
            skArc(sketch, "E868", {"start": v(1.69, 13.32) * mm, "mid": v(1.7, 13.5) * mm, "end": v(1.52, 13.5) * mm});
            skArc(sketch, "E869", {"start": v(1.36, 13.36) * mm, "mid": v(1.35, 13.19) * mm, "end": v(1.53, 13.18) * mm});
            skLineSegment(sketch, "E870", {"start": v(1.6, 13.42) * mm, "end": v(1.75, 13.58) * mm});
            skArc(sketch, "E871", {"start": v(1.84, 13.5) * mm, "mid": v(1.83, 13.67) * mm, "end": v(1.65, 13.66) * mm});
            skArc(sketch, "E872", {"start": v(1.51, 13.5) * mm, "mid": v(1.52, 13.32) * mm, "end": v(1.7, 13.33) * mm});
            skLineSegment(sketch, "E873", {"start": v(1.75, 13.58) * mm, "end": v(1.88, 13.75) * mm});
            skArc(sketch, "E874", {"start": v(1.98, 13.68) * mm, "mid": v(1.95, 13.85) * mm, "end": v(1.78, 13.82) * mm});
            skArc(sketch, "E875", {"start": v(1.65, 13.65) * mm, "mid": v(1.67, 13.48) * mm, "end": v(1.85, 13.5) * mm});
            skLineSegment(sketch, "E876", {"start": v(1.88, 13.75) * mm, "end": v(1.99, 13.94) * mm});
            skArc(sketch, "E877", {"start": v(2.1, 13.87) * mm, "mid": v(2.05, 14.04) * mm, "end": v(1.88, 14) * mm});
            skArc(sketch, "E878", {"start": v(1.77, 13.81) * mm, "mid": v(1.81, 13.64) * mm, "end": v(1.98, 13.69) * mm});
            skLineSegment(sketch, "E879", {"start": v(1.99, 13.94) * mm, "end": v(2.08, 14.13) * mm});
            skArc(sketch, "E880", {"start": v(2.2, 14.08) * mm, "mid": v(2.14, 14.25) * mm, "end": v(1.97, 14.19) * mm});
            skArc(sketch, "E881", {"start": v(1.88, 14) * mm, "mid": v(1.94, 13.82) * mm, "end": v(2.1, 13.88) * mm});
            skLineSegment(sketch, "E882", {"start": v(2.08, 14.13) * mm, "end": v(2.16, 14.34) * mm});
            skArc(sketch, "E883", {"start": v(2.27, 14.3) * mm, "mid": v(2.2, 14.46) * mm, "end": v(2.04, 14.38) * mm});
            skArc(sketch, "E884", {"start": v(1.96, 14.18) * mm, "mid": v(2.04, 14.02) * mm, "end": v(2.2, 14.1) * mm});
            skLineSegment(sketch, "E885", {"start": v(2.16, 14.34) * mm, "end": v(2.21, 14.56) * mm});
            skArc(sketch, "E886", {"start": v(2.33, 14.53) * mm, "mid": v(2.24, 14.68) * mm, "end": v(2.09, 14.59) * mm});
            skArc(sketch, "E887", {"start": v(2.04, 14.37) * mm, "mid": v(2.13, 14.22) * mm, "end": v(2.28, 14.31) * mm});
            skLineSegment(sketch, "E888", {"start": v(2.21, 14.56) * mm, "end": v(2.24, 14.78) * mm});
            skArc(sketch, "E889", {"start": v(2.37, 14.76) * mm, "mid": v(2.26, 14.9) * mm, "end": v(2.12, 14.8) * mm});
            skArc(sketch, "E890", {"start": v(2.09, 14.58) * mm, "mid": v(2.2, 14.43) * mm, "end": v(2.33, 14.54) * mm});
            skLineSegment(sketch, "E891", {"start": v(2.24, 14.78) * mm, "end": v(2.25, 15.03) * mm});
            skArc(sketch, "E892", {"start": v(2.38, 15.02) * mm, "mid": v(2.26, 15.15) * mm, "end": v(2.13, 15.03) * mm});
            skArc(sketch, "E893", {"start": v(2.12, 14.79) * mm, "mid": v(2.24, 14.66) * mm, "end": v(2.37, 14.78) * mm});
            skLineSegment(sketch, "E894", {"start": v(2.25, 15.03) * mm, "end": v(2.25, 18.36) * mm});
            skArc(sketch, "E895", {"start": v(2.38, 18.36) * mm, "mid": v(2.25, 18.48) * mm, "end": v(2.13, 18.36) * mm});
            skArc(sketch, "E896", {"start": v(2.13, 15.03) * mm, "mid": v(2.25, 14.9) * mm, "end": v(2.38, 15.03) * mm});
            skLineSegment(sketch, "E897", {"start": v(2.25, 18.36) * mm, "end": v(1.53, 20.57) * mm});
            skArc(sketch, "E898", {"start": v(1.65, 20.61) * mm, "mid": v(1.5, 20.7) * mm, "end": v(1.41, 20.54) * mm});
            skArc(sketch, "E899", {"start": v(2.14, 18.32) * mm, "mid": v(2.3, 18.24) * mm, "end": v(2.37, 18.4) * mm});
            skLineSegment(sketch, "E900", {"start": v(1.53, 20.57) * mm, "end": v(0.96, 21.46) * mm});
            skArc(sketch, "E901", {"start": v(1.06, 21.53) * mm, "mid": v(0.9, 21.56) * mm, "end": v(0.85, 21.4) * mm});
            skArc(sketch, "E902", {"start": v(1.43, 20.5) * mm, "mid": v(1.6, 20.47) * mm, "end": v(1.64, 20.64) * mm});
            skLineSegment(sketch, "E903", {"start": v(0.96, 21.46) * mm, "end": v(-0.95, 21.46) * mm});
            skArc(sketch, "E904", {"start": v(-0.95, 21.58) * mm, "mid": v(-1.07, 21.46) * mm, "end": v(-0.95, 21.33) * mm});
            skArc(sketch, "E905", {"start": v(0.96, 21.33) * mm, "mid": v(1.08, 21.46) * mm, "end": v(0.96, 21.58) * mm});
            skLineSegment(sketch, "E906", {"start": v(-0.95, 21.46) * mm, "end": v(-1.52, 20.57) * mm});
            skArc(sketch, "E907", {"start": v(-1.63, 20.64) * mm, "mid": v(-1.6, 20.47) * mm, "end": v(-1.42, 20.5) * mm});
            skArc(sketch, "E908", {"start": v(-0.84, 21.4) * mm, "mid": v(-0.88, 21.56) * mm, "end": v(-1.05, 21.53) * mm});
            skLineSegment(sketch, "E909", {"start": v(-1.52, 20.57) * mm, "end": v(-2.25, 18.36) * mm});
            skArc(sketch, "E910", {"start": v(-2.36, 18.4) * mm, "mid": v(-2.28, 18.24) * mm, "end": v(-2.13, 18.32) * mm});
            skArc(sketch, "E911", {"start": v(-1.4, 20.54) * mm, "mid": v(-1.49, 20.7) * mm, "end": v(-1.64, 20.61) * mm});
            skLineSegment(sketch, "E912", {"start": v(-1.03, 13) * mm, "end": v(1.03, 13) * mm});
            skArc(sketch, "E913", {"start": v(1.03, 12.87) * mm, "mid": v(1.16, 13) * mm, "end": v(1.03, 13.12) * mm});
            skArc(sketch, "E914", {"start": v(-1.03, 13.12) * mm, "mid": v(-1.15, 13) * mm, "end": v(-1.03, 12.87) * mm});
            skLineSegment(sketch, "E915", {"start": v(-1.67, 13.5) * mm, "end": v(1.68, 13.5) * mm});
            skArc(sketch, "E916", {"start": v(1.68, 13.37) * mm, "mid": v(1.8, 13.5) * mm, "end": v(1.68, 13.62) * mm});
            skArc(sketch, "E917", {"start": v(-1.67, 13.62) * mm, "mid": v(-1.8, 13.5) * mm, "end": v(-1.67, 13.37) * mm});
            skLineSegment(sketch, "E918", {"start": v(-2, 14) * mm, "end": v(2.02, 14) * mm});
            skArc(sketch, "E919", {"start": v(2.02, 13.87) * mm, "mid": v(2.14, 14) * mm, "end": v(2.02, 14.12) * mm});
            skArc(sketch, "E920", {"start": v(-2, 14.12) * mm, "mid": v(-2.13, 14) * mm, "end": v(-2, 13.87) * mm});
            skLineSegment(sketch, "E921", {"start": v(-2.19, 14.5) * mm, "end": v(2.2, 14.5) * mm});
            skArc(sketch, "E922", {"start": v(2.2, 14.37) * mm, "mid": v(2.32, 14.5) * mm, "end": v(2.2, 14.62) * mm});
            skArc(sketch, "E923", {"start": v(-2.19, 14.62) * mm, "mid": v(-2.31, 14.5) * mm, "end": v(-2.19, 14.37) * mm});
            skLineSegment(sketch, "E924", {"start": v(-2.23, 15) * mm, "end": v(2.25, 15) * mm});
            skArc(sketch, "E925", {"start": v(2.25, 14.87) * mm, "mid": v(2.38, 15) * mm, "end": v(2.25, 15.12) * mm});
            skArc(sketch, "E926", {"start": v(-2.23, 15.12) * mm, "mid": v(-2.36, 15) * mm, "end": v(-2.23, 14.87) * mm});
            skLineSegment(sketch, "E927", {"start": v(-2.24, 15.5) * mm, "end": v(2.25, 15.5) * mm});
            skArc(sketch, "E928", {"start": v(2.25, 15.37) * mm, "mid": v(2.38, 15.5) * mm, "end": v(2.25, 15.62) * mm});
            skArc(sketch, "E929", {"start": v(-2.24, 15.62) * mm, "mid": v(-2.36, 15.5) * mm, "end": v(-2.24, 15.37) * mm});
            skLineSegment(sketch, "E930", {"start": v(-2.24, 16) * mm, "end": v(2.25, 16) * mm});
            skArc(sketch, "E931", {"start": v(2.25, 15.87) * mm, "mid": v(2.38, 16) * mm, "end": v(2.25, 16.12) * mm});
            skArc(sketch, "E932", {"start": v(-2.24, 16.12) * mm, "mid": v(-2.36, 16) * mm, "end": v(-2.24, 15.87) * mm});
            skLineSegment(sketch, "E933", {"start": v(-2.24, 16.5) * mm, "end": v(2.25, 16.5) * mm});
            skArc(sketch, "E934", {"start": v(2.25, 16.37) * mm, "mid": v(2.38, 16.5) * mm, "end": v(2.25, 16.62) * mm});
            skArc(sketch, "E935", {"start": v(-2.24, 16.62) * mm, "mid": v(-2.36, 16.5) * mm, "end": v(-2.24, 16.37) * mm});
            skLineSegment(sketch, "E936", {"start": v(-2.24, 17) * mm, "end": v(2.25, 17) * mm});
            skArc(sketch, "E937", {"start": v(2.25, 16.87) * mm, "mid": v(2.38, 17) * mm, "end": v(2.25, 17.12) * mm});
            skArc(sketch, "E938", {"start": v(-2.24, 17.12) * mm, "mid": v(-2.37, 17) * mm, "end": v(-2.24, 16.87) * mm});
            skLineSegment(sketch, "E939", {"start": v(-2.24, 17.5) * mm, "end": v(2.25, 17.5) * mm});
            skArc(sketch, "E940", {"start": v(2.25, 17.37) * mm, "mid": v(2.38, 17.5) * mm, "end": v(2.25, 17.62) * mm});
            skArc(sketch, "E941", {"start": v(-2.24, 17.62) * mm, "mid": v(-2.37, 17.5) * mm, "end": v(-2.24, 17.37) * mm});
            skLineSegment(sketch, "E942", {"start": v(-2.24, 18) * mm, "end": v(2.25, 18) * mm});
            skArc(sketch, "E943", {"start": v(2.25, 17.87) * mm, "mid": v(2.38, 18) * mm, "end": v(2.25, 18.12) * mm});
            skArc(sketch, "E944", {"start": v(-2.24, 18.12) * mm, "mid": v(-2.37, 18) * mm, "end": v(-2.24, 17.87) * mm});
            skLineSegment(sketch, "E945", {"start": v(-2.2, 18.5) * mm, "end": v(2.2, 18.5) * mm});
            skArc(sketch, "E946", {"start": v(2.2, 18.37) * mm, "mid": v(2.33, 18.5) * mm, "end": v(2.2, 18.62) * mm});
            skArc(sketch, "E947", {"start": v(-2.2, 18.62) * mm, "mid": v(-2.32, 18.5) * mm, "end": v(-2.2, 18.37) * mm});
            skLineSegment(sketch, "E948", {"start": v(-2.04, 19) * mm, "end": v(2.05, 19) * mm});
            skArc(sketch, "E949", {"start": v(2.05, 18.87) * mm, "mid": v(2.17, 19) * mm, "end": v(2.05, 19.12) * mm});
            skArc(sketch, "E950", {"start": v(-2.04, 19.12) * mm, "mid": v(-2.16, 19) * mm, "end": v(-2.04, 18.87) * mm});
            skLineSegment(sketch, "E951", {"start": v(-1.87, 19.5) * mm, "end": v(1.88, 19.5) * mm});
            skArc(sketch, "E952", {"start": v(1.88, 19.37) * mm, "mid": v(2, 19.5) * mm, "end": v(1.88, 19.62) * mm});
            skArc(sketch, "E953", {"start": v(-1.87, 19.62) * mm, "mid": v(-2, 19.5) * mm, "end": v(-1.87, 19.37) * mm});
            skLineSegment(sketch, "E954", {"start": v(-1.71, 20) * mm, "end": v(1.72, 20) * mm});
            skArc(sketch, "E955", {"start": v(1.72, 19.87) * mm, "mid": v(1.85, 20) * mm, "end": v(1.72, 20.12) * mm});
            skArc(sketch, "E956", {"start": v(-1.71, 20.12) * mm, "mid": v(-1.84, 20) * mm, "end": v(-1.71, 19.87) * mm});
            skLineSegment(sketch, "E957", {"start": v(-1.55, 20.5) * mm, "end": v(1.56, 20.5) * mm});
            skArc(sketch, "E958", {"start": v(1.56, 20.37) * mm, "mid": v(1.68, 20.5) * mm, "end": v(1.56, 20.62) * mm});
            skArc(sketch, "E959", {"start": v(-1.55, 20.62) * mm, "mid": v(-1.67, 20.5) * mm, "end": v(-1.55, 20.37) * mm});
            skLineSegment(sketch, "E960", {"start": v(-1.25, 21) * mm, "end": v(1.26, 21) * mm});
            skArc(sketch, "E961", {"start": v(1.26, 20.87) * mm, "mid": v(1.38, 21) * mm, "end": v(1.26, 21.12) * mm});
            skArc(sketch, "E962", {"start": v(-1.25, 21.12) * mm, "mid": v(-1.37, 21) * mm, "end": v(-1.25, 20.87) * mm});
            skLineSegment(sketch, "E963", {"start": v(-2.43, 28.4) * mm, "end": v(-2.33, 28.3) * mm});
            skArc(sketch, "E964", {"start": v(-2.36, 28.26) * mm, "mid": v(-2.3, 28.26) * mm, "end": v(-2.3, 28.33) * mm});
            skArc(sketch, "E965", {"start": v(-2.4, 28.43) * mm, "mid": v(-2.47, 28.43) * mm, "end": v(-2.47, 28.36) * mm});
            skLineSegment(sketch, "E966", {"start": v(-2.33, 28.3) * mm, "end": v(-2.2, 28.2) * mm});
            skArc(sketch, "E967", {"start": v(-2.23, 28.16) * mm, "mid": v(-2.16, 28.18) * mm, "end": v(-2.17, 28.25) * mm});
            skArc(sketch, "E968", {"start": v(-2.3, 28.34) * mm, "mid": v(-2.37, 28.32) * mm, "end": v(-2.36, 28.25) * mm});
            skLineSegment(sketch, "E969", {"start": v(-2.2, 28.2) * mm, "end": v(-2.06, 28.14) * mm});
            skArc(sketch, "E970", {"start": v(-2.08, 28.1) * mm, "mid": v(-2.02, 28.12) * mm, "end": v(-2.04, 28.18) * mm});
            skArc(sketch, "E971", {"start": v(-2.18, 28.25) * mm, "mid": v(-2.25, 28.23) * mm, "end": v(-2.22, 28.16) * mm});
            skLineSegment(sketch, "E972", {"start": v(-2.06, 28.14) * mm, "end": v(-1.9, 28.1) * mm});
            skArc(sketch, "E973", {"start": v(-1.92, 28.05) * mm, "mid": v(-1.86, 28.09) * mm, "end": v(-1.9, 28.15) * mm});
            skArc(sketch, "E974", {"start": v(-2.05, 28.19) * mm, "mid": v(-2.11, 28.15) * mm, "end": v(-2.07, 28.1) * mm});
            skLineSegment(sketch, "E975", {"start": v(-1.9, 28.1) * mm, "end": v(-1.83, 28.09) * mm});
            skArc(sketch, "E976", {"start": v(-1.84, 28.04) * mm, "mid": v(-1.78, 28.08) * mm, "end": v(-1.82, 28.14) * mm});
            skArc(sketch, "E977", {"start": v(-1.9, 28.15) * mm, "mid": v(-1.96, 28.1) * mm, "end": v(-1.92, 28.05) * mm});
            skLineSegment(sketch, "E978", {"start": v(-1.83, 28.09) * mm, "end": v(1.92, 28.1) * mm});
            skArc(sketch, "E979", {"start": v(1.92, 28.05) * mm, "mid": v(1.97, 28.1) * mm, "end": v(1.92, 28.15) * mm});
            skArc(sketch, "E980", {"start": v(-1.83, 28.14) * mm, "mid": v(-1.88, 28.09) * mm, "end": v(-1.83, 28.04) * mm});
            skLineSegment(sketch, "E981", {"start": v(1.92, 28.1) * mm, "end": v(2.08, 28.14) * mm});
            skArc(sketch, "E982", {"start": v(2.1, 28.1) * mm, "mid": v(2.12, 28.16) * mm, "end": v(2.06, 28.2) * mm});
            skArc(sketch, "E983", {"start": v(1.91, 28.15) * mm, "mid": v(1.88, 28.09) * mm, "end": v(1.94, 28.05) * mm});
            skLineSegment(sketch, "E984", {"start": v(2.08, 28.14) * mm, "end": v(2.22, 28.2) * mm});
            skArc(sketch, "E985", {"start": v(2.24, 28.16) * mm, "mid": v(2.26, 28.23) * mm, "end": v(2.2, 28.25) * mm});
            skArc(sketch, "E986", {"start": v(2.05, 28.19) * mm, "mid": v(2.03, 28.12) * mm, "end": v(2.1, 28.1) * mm});
            skLineSegment(sketch, "E987", {"start": v(2.22, 28.2) * mm, "end": v(2.34, 28.3) * mm});
            skArc(sketch, "E988", {"start": v(2.37, 28.26) * mm, "mid": v(2.38, 28.33) * mm, "end": v(2.31, 28.34) * mm});
            skArc(sketch, "E989", {"start": v(2.19, 28.25) * mm, "mid": v(2.18, 28.18) * mm, "end": v(2.25, 28.17) * mm});
            skLineSegment(sketch, "E990", {"start": v(2.34, 28.3) * mm, "end": v(2.44, 28.4) * mm});
            skArc(sketch, "E991", {"start": v(2.47, 28.36) * mm, "mid": v(2.47, 28.43) * mm, "end": v(2.4, 28.43) * mm});
            skArc(sketch, "E992", {"start": v(2.3, 28.34) * mm, "mid": v(2.3, 28.26) * mm, "end": v(2.38, 28.26) * mm});
            skLineSegment(sketch, "E993", {"start": v(2.44, 28.4) * mm, "end": v(2.34, 28.5) * mm});
            skArc(sketch, "E994", {"start": v(2.37, 28.53) * mm, "mid": v(2.3, 28.53) * mm, "end": v(2.3, 28.46) * mm});
            skArc(sketch, "E995", {"start": v(2.4, 28.36) * mm, "mid": v(2.47, 28.36) * mm, "end": v(2.47, 28.43) * mm});
            skLineSegment(sketch, "E996", {"start": v(2.34, 28.5) * mm, "end": v(2.2, 28.58) * mm});
            skArc(sketch, "E997", {"start": v(2.24, 28.62) * mm, "mid": v(2.17, 28.6) * mm, "end": v(2.18, 28.54) * mm});
            skArc(sketch, "E998", {"start": v(2.3, 28.45) * mm, "mid": v(2.38, 28.46) * mm, "end": v(2.36, 28.53) * mm});
            skLineSegment(sketch, "E999", {"start": v(2.2, 28.58) * mm, "end": v(2.07, 28.65) * mm});
            skArc(sketch, "E1000", {"start": v(2.09, 28.7) * mm, "mid": v(2.02, 28.67) * mm, "end": v(2.05, 28.6) * mm});
            skArc(sketch, "E1001", {"start": v(2.19, 28.54) * mm, "mid": v(2.25, 28.56) * mm, "end": v(2.23, 28.63) * mm});
            skLineSegment(sketch, "E1002", {"start": v(2.07, 28.65) * mm, "end": v(1.91, 28.69) * mm});
            skArc(sketch, "E1003", {"start": v(1.93, 28.74) * mm, "mid": v(1.87, 28.7) * mm, "end": v(1.9, 28.64) * mm});
            skArc(sketch, "E1004", {"start": v(2.05, 28.6) * mm, "mid": v(2.12, 28.63) * mm, "end": v(2.08, 28.7) * mm});
            skLineSegment(sketch, "E1005", {"start": v(1.91, 28.69) * mm, "end": v(1.84, 28.7) * mm});
            skArc(sketch, "E1006", {"start": v(1.84, 28.75) * mm, "mid": v(1.79, 28.7) * mm, "end": v(1.83, 28.65) * mm});
            skArc(sketch, "E1007", {"start": v(1.9, 28.64) * mm, "mid": v(1.96, 28.68) * mm, "end": v(1.92, 28.74) * mm});
            skLineSegment(sketch, "E1008", {"start": v(1.84, 28.7) * mm, "end": v(-1.92, 28.69) * mm});
            skArc(sketch, "E1009", {"start": v(-1.92, 28.74) * mm, "mid": v(-1.97, 28.69) * mm, "end": v(-1.92, 28.64) * mm});
            skArc(sketch, "E1010", {"start": v(1.84, 28.65) * mm, "mid": v(1.88, 28.7) * mm, "end": v(1.83, 28.75) * mm});
            skLineSegment(sketch, "E1011", {"start": v(-1.92, 28.69) * mm, "end": v(-2.07, 28.64) * mm});
            skArc(sketch, "E1012", {"start": v(-2.08, 28.7) * mm, "mid": v(-2.12, 28.63) * mm, "end": v(-2.06, 28.6) * mm});
            skArc(sketch, "E1013", {"start": v(-1.9, 28.64) * mm, "mid": v(-1.87, 28.7) * mm, "end": v(-1.93, 28.74) * mm});
            skLineSegment(sketch, "E1014", {"start": v(-2.07, 28.64) * mm, "end": v(-2.21, 28.58) * mm});
            skArc(sketch, "E1015", {"start": v(-2.23, 28.62) * mm, "mid": v(-2.26, 28.56) * mm, "end": v(-2.19, 28.53) * mm});
            skArc(sketch, "E1016", {"start": v(-2.05, 28.6) * mm, "mid": v(-2.03, 28.67) * mm, "end": v(-2.1, 28.69) * mm});
            skLineSegment(sketch, "E1017", {"start": v(-2.21, 28.58) * mm, "end": v(-2.34, 28.49) * mm});
            skArc(sketch, "E1018", {"start": v(-2.37, 28.53) * mm, "mid": v(-2.38, 28.46) * mm, "end": v(-2.3, 28.45) * mm});
            skArc(sketch, "E1019", {"start": v(-2.18, 28.54) * mm, "mid": v(-2.17, 28.6) * mm, "end": v(-2.24, 28.62) * mm});
            skLineSegment(sketch, "E1020", {"start": v(-2.34, 28.49) * mm, "end": v(-2.43, 28.4) * mm});
            skArc(sketch, "E1021", {"start": v(-2.47, 28.43) * mm, "mid": v(-2.47, 28.36) * mm, "end": v(-2.4, 28.36) * mm});
            skArc(sketch, "E1022", {"start": v(-2.3, 28.45) * mm, "mid": v(-2.3, 28.52) * mm, "end": v(-2.37, 28.52) * mm});
            skLineSegment(sketch, "E1023", {"start": v(-2.19, 28.2) * mm, "end": v(2.2, 28.2) * mm});
            skArc(sketch, "E1024", {"start": v(2.2, 28.15) * mm, "mid": v(2.24, 28.2) * mm, "end": v(2.2, 28.25) * mm});
            skArc(sketch, "E1025", {"start": v(-2.19, 28.25) * mm, "mid": v(-2.24, 28.2) * mm, "end": v(-2.19, 28.15) * mm});
            skLineSegment(sketch, "E1026", {"start": v(-2.43, 28.4) * mm, "end": v(2.43, 28.4) * mm});
            skArc(sketch, "E1027", {"start": v(2.43, 28.35) * mm, "mid": v(2.48, 28.4) * mm, "end": v(2.43, 28.45) * mm});
            skArc(sketch, "E1028", {"start": v(-2.43, 28.45) * mm, "mid": v(-2.48, 28.4) * mm, "end": v(-2.43, 28.35) * mm});
            skLineSegment(sketch, "E1029", {"start": v(-2.17, 28.6) * mm, "end": v(2.17, 28.6) * mm});
            skArc(sketch, "E1030", {"start": v(2.17, 28.55) * mm, "mid": v(2.22, 28.6) * mm, "end": v(2.17, 28.65) * mm});
            skArc(sketch, "E1031", {"start": v(-2.17, 28.65) * mm, "mid": v(-2.22, 28.6) * mm, "end": v(-2.17, 28.55) * mm});
            skCircle(sketch, "E1032", {"center": v(0, 15) * mm, "radius": 1.7 * mm});
            skArc(sketch, "E1033", {"start": v(0, 14.12) * mm, "mid": v(0.88, 15) * mm, "end": v(0, 15.87) * mm});
            skArc(sketch, "E1034", {"start": v(0, 15.87) * mm, "mid": v(-0.87, 15) * mm, "end": v(0, 14.12) * mm});
            skCircle(sketch, "E1035", {"center": v(0, 25) * mm, "radius": 1.7 * mm});
            skArc(sketch, "E1036", {"start": v(0, 24.12) * mm, "mid": v(0.88, 25) * mm, "end": v(0, 25.87) * mm});
            skArc(sketch, "E1037", {"start": v(0, 25.87) * mm, "mid": v(-0.87, 25) * mm, "end": v(0, 24.12) * mm});
            skLineSegment(sketch, "E1038", {"start": v(-3.8, 0.7) * mm, "end": v(-3.8, 0.5) * mm});
            skArc(sketch, "E1039", {"start": v(-3.8, 0.5) * mm, "mid": v(-3.78, 0.47) * mm, "end": v(-3.75, 0.45) * mm});
            skLineSegment(sketch, "E1040", {"start": v(-3.75, 0.45) * mm, "end": v(-3.05, 0.45) * mm});
            skArc(sketch, "E1041", {"start": v(-3.05, 0.45) * mm, "mid": v(-3.02, 0.47) * mm, "end": v(-3, 0.5) * mm});
            skLineSegment(sketch, "E1042", {"start": v(-3, 0.5) * mm, "end": v(-3, 0.7) * mm});
            skArc(sketch, "E1043", {"start": v(-3, 0.7) * mm, "mid": v(-3.02, 0.74) * mm, "end": v(-3.05, 0.75) * mm});
            skLineSegment(sketch, "E1044", {"start": v(-3.05, 0.75) * mm, "end": v(-3.75, 0.75) * mm});
            skArc(sketch, "E1045", {"start": v(-3.75, 0.75) * mm, "mid": v(-3.78, 0.74) * mm, "end": v(-3.8, 0.7) * mm});
            skLineSegment(sketch, "E1046", {"start": v(-3.8, 0.2) * mm, "end": v(-3.8, 0) * mm});
            skArc(sketch, "E1047", {"start": v(-3.8, 0) * mm, "mid": v(-3.78, -0.03) * mm, "end": v(-3.75, -0.05) * mm});
            skLineSegment(sketch, "E1048", {"start": v(-3.75, -0.05) * mm, "end": v(-3.05, -0.05) * mm});
            skArc(sketch, "E1049", {"start": v(-3.05, -0.05) * mm, "mid": v(-3.02, -0.03) * mm, "end": v(-3, 0) * mm});
            skLineSegment(sketch, "E1050", {"start": v(-3, 0) * mm, "end": v(-3, 0.2) * mm});
            skArc(sketch, "E1051", {"start": v(-3, 0.2) * mm, "mid": v(-3.02, 0.24) * mm, "end": v(-3.05, 0.25) * mm});
            skLineSegment(sketch, "E1052", {"start": v(-3.05, 0.25) * mm, "end": v(-3.75, 0.25) * mm});
            skArc(sketch, "E1053", {"start": v(-3.75, 0.25) * mm, "mid": v(-3.78, 0.24) * mm, "end": v(-3.8, 0.2) * mm});
            skLineSegment(sketch, "E1054", {"start": v(-3.8, -0.3) * mm, "end": v(-3.8, -0.5) * mm});
            skArc(sketch, "E1055", {"start": v(-3.8, -0.5) * mm, "mid": v(-3.78, -0.53) * mm, "end": v(-3.75, -0.55) * mm});
            skLineSegment(sketch, "E1056", {"start": v(-3.75, -0.55) * mm, "end": v(-3.05, -0.55) * mm});
            skArc(sketch, "E1057", {"start": v(-3.05, -0.55) * mm, "mid": v(-3.02, -0.53) * mm, "end": v(-3, -0.5) * mm});
            skLineSegment(sketch, "E1058", {"start": v(-3, -0.5) * mm, "end": v(-3, -0.3) * mm});
            skArc(sketch, "E1059", {"start": v(-3, -0.3) * mm, "mid": v(-3.02, -0.26) * mm, "end": v(-3.05, -0.25) * mm});
            skLineSegment(sketch, "E1060", {"start": v(-3.05, -0.25) * mm, "end": v(-3.75, -0.25) * mm});
            skArc(sketch, "E1061", {"start": v(-3.75, -0.25) * mm, "mid": v(-3.78, -0.26) * mm, "end": v(-3.8, -0.3) * mm});
            skLineSegment(sketch, "E1062", {"start": v(-3.8, -0.8) * mm, "end": v(-3.8, -1) * mm});
            skArc(sketch, "E1063", {"start": v(-3.8, -1) * mm, "mid": v(-3.78, -1.03) * mm, "end": v(-3.75, -1.05) * mm});
            skLineSegment(sketch, "E1064", {"start": v(-3.75, -1.05) * mm, "end": v(-3.05, -1.05) * mm});
            skArc(sketch, "E1065", {"start": v(-3.05, -1.05) * mm, "mid": v(-3.02, -1.03) * mm, "end": v(-3, -1) * mm});
            skLineSegment(sketch, "E1066", {"start": v(-3, -1) * mm, "end": v(-3, -0.8) * mm});
            skArc(sketch, "E1067", {"start": v(-3, -0.8) * mm, "mid": v(-3.02, -0.76) * mm, "end": v(-3.05, -0.75) * mm});
            skLineSegment(sketch, "E1068", {"start": v(-3.05, -0.75) * mm, "end": v(-3.75, -0.75) * mm});
            skArc(sketch, "E1069", {"start": v(-3.75, -0.75) * mm, "mid": v(-3.78, -0.76) * mm, "end": v(-3.8, -0.8) * mm});
            skLineSegment(sketch, "E1070", {"start": v(-3.8, -1.3) * mm, "end": v(-3.8, -1.5) * mm});
            skArc(sketch, "E1071", {"start": v(-3.8, -1.5) * mm, "mid": v(-3.78, -1.53) * mm, "end": v(-3.75, -1.55) * mm});
            skLineSegment(sketch, "E1072", {"start": v(-3.75, -1.55) * mm, "end": v(-3.05, -1.55) * mm});
            skArc(sketch, "E1073", {"start": v(-3.05, -1.55) * mm, "mid": v(-3.02, -1.53) * mm, "end": v(-3, -1.5) * mm});
            skLineSegment(sketch, "E1074", {"start": v(-3, -1.5) * mm, "end": v(-3, -1.3) * mm});
            skArc(sketch, "E1075", {"start": v(-3, -1.3) * mm, "mid": v(-3.02, -1.26) * mm, "end": v(-3.05, -1.25) * mm});
            skLineSegment(sketch, "E1076", {"start": v(-3.05, -1.25) * mm, "end": v(-3.75, -1.25) * mm});
            skArc(sketch, "E1077", {"start": v(-3.75, -1.25) * mm, "mid": v(-3.78, -1.26) * mm, "end": v(-3.8, -1.3) * mm});
            skLineSegment(sketch, "E1078", {"start": v(-3.8, -1.8) * mm, "end": v(-3.8, -2) * mm});
            skArc(sketch, "E1079", {"start": v(-3.8, -2) * mm, "mid": v(-3.78, -2.03) * mm, "end": v(-3.75, -2.05) * mm});
            skLineSegment(sketch, "E1080", {"start": v(-3.75, -2.05) * mm, "end": v(-3.05, -2.05) * mm});
            skArc(sketch, "E1081", {"start": v(-3.05, -2.05) * mm, "mid": v(-3.02, -2.03) * mm, "end": v(-3, -2) * mm});
            skLineSegment(sketch, "E1082", {"start": v(-3, -2) * mm, "end": v(-3, -1.8) * mm});
            skArc(sketch, "E1083", {"start": v(-3, -1.8) * mm, "mid": v(-3.02, -1.76) * mm, "end": v(-3.05, -1.75) * mm});
            skLineSegment(sketch, "E1084", {"start": v(-3.05, -1.75) * mm, "end": v(-3.75, -1.75) * mm});
            skArc(sketch, "E1085", {"start": v(-3.75, -1.75) * mm, "mid": v(-3.78, -1.76) * mm, "end": v(-3.8, -1.8) * mm});
            skLineSegment(sketch, "E1086", {"start": v(-3, -2.5) * mm, "end": v(-3, -2.3) * mm});
            skArc(sketch, "E1087", {"start": v(-3, -2.3) * mm, "mid": v(-3.02, -2.26) * mm, "end": v(-3.05, -2.25) * mm});
            skLineSegment(sketch, "E1088", {"start": v(-3.05, -2.25) * mm, "end": v(-3.75, -2.25) * mm});
            skArc(sketch, "E1089", {"start": v(-3.75, -2.25) * mm, "mid": v(-3.78, -2.26) * mm, "end": v(-3.8, -2.3) * mm});
            skLineSegment(sketch, "E1090", {"start": v(-3.8, -2.3) * mm, "end": v(-3.8, -2.5) * mm});
            skArc(sketch, "E1091", {"start": v(-3.8, -2.5) * mm, "mid": v(-3.78, -2.53) * mm, "end": v(-3.75, -2.55) * mm});
            skLineSegment(sketch, "E1092", {"start": v(-3.75, -2.55) * mm, "end": v(-3.05, -2.55) * mm});
            skArc(sketch, "E1093", {"start": v(-3.05, -2.55) * mm, "mid": v(-3.02, -2.53) * mm, "end": v(-3, -2.5) * mm});
            skLineSegment(sketch, "E1094", {"start": v(-3, -3) * mm, "end": v(-3, -2.8) * mm});
            skArc(sketch, "E1095", {"start": v(-3, -2.8) * mm, "mid": v(-3.02, -2.76) * mm, "end": v(-3.05, -2.75) * mm});
            skLineSegment(sketch, "E1096", {"start": v(-3.05, -2.75) * mm, "end": v(-3.75, -2.75) * mm});
            skArc(sketch, "E1097", {"start": v(-3.75, -2.75) * mm, "mid": v(-3.78, -2.76) * mm, "end": v(-3.8, -2.8) * mm});
            skLineSegment(sketch, "E1098", {"start": v(-3.8, -2.8) * mm, "end": v(-3.8, -3) * mm});
            skArc(sketch, "E1099", {"start": v(-3.8, -3) * mm, "mid": v(-3.78, -3.03) * mm, "end": v(-3.75, -3.05) * mm});
            skLineSegment(sketch, "E1100", {"start": v(-3.75, -3.05) * mm, "end": v(-3.05, -3.05) * mm});
            skArc(sketch, "E1101", {"start": v(-3.05, -3.05) * mm, "mid": v(-3.02, -3.03) * mm, "end": v(-3, -3) * mm});
            skLineSegment(sketch, "E1102", {"start": v(-3, -3.5) * mm, "end": v(-3, -3.3) * mm});
            skArc(sketch, "E1103", {"start": v(-3, -3.3) * mm, "mid": v(-3.02, -3.26) * mm, "end": v(-3.05, -3.25) * mm});
            skLineSegment(sketch, "E1104", {"start": v(-3.05, -3.25) * mm, "end": v(-3.75, -3.25) * mm});
            skArc(sketch, "E1105", {"start": v(-3.75, -3.25) * mm, "mid": v(-3.78, -3.26) * mm, "end": v(-3.8, -3.3) * mm});
            skLineSegment(sketch, "E1106", {"start": v(-3.8, -3.3) * mm, "end": v(-3.8, -3.5) * mm});
            skArc(sketch, "E1107", {"start": v(-3.8, -3.5) * mm, "mid": v(-3.78, -3.53) * mm, "end": v(-3.75, -3.55) * mm});
            skLineSegment(sketch, "E1108", {"start": v(-3.75, -3.55) * mm, "end": v(-3.05, -3.55) * mm});
            skArc(sketch, "E1109", {"start": v(-3.05, -3.55) * mm, "mid": v(-3.02, -3.53) * mm, "end": v(-3, -3.5) * mm});
            skLineSegment(sketch, "E1110", {"start": v(-3, -4) * mm, "end": v(-3, -3.8) * mm});
            skArc(sketch, "E1111", {"start": v(-3, -3.8) * mm, "mid": v(-3.02, -3.76) * mm, "end": v(-3.05, -3.75) * mm});
            skLineSegment(sketch, "E1112", {"start": v(-3.05, -3.75) * mm, "end": v(-3.75, -3.75) * mm});
            skArc(sketch, "E1113", {"start": v(-3.75, -3.75) * mm, "mid": v(-3.78, -3.76) * mm, "end": v(-3.8, -3.8) * mm});
            skLineSegment(sketch, "E1114", {"start": v(-3.8, -3.8) * mm, "end": v(-3.8, -4) * mm});
            skArc(sketch, "E1115", {"start": v(-3.8, -4) * mm, "mid": v(-3.78, -4.03) * mm, "end": v(-3.75, -4.05) * mm});
            skLineSegment(sketch, "E1116", {"start": v(-3.75, -4.05) * mm, "end": v(-3.05, -4.05) * mm});
            skArc(sketch, "E1117", {"start": v(-3.05, -4.05) * mm, "mid": v(-3.02, -4.03) * mm, "end": v(-3, -4) * mm});
            skLineSegment(sketch, "E1118", {"start": v(-3, -4.5) * mm, "end": v(-3, -4.3) * mm});
            skArc(sketch, "E1119", {"start": v(-3, -4.3) * mm, "mid": v(-3.02, -4.26) * mm, "end": v(-3.05, -4.25) * mm});
            skLineSegment(sketch, "E1120", {"start": v(-3.05, -4.25) * mm, "end": v(-3.75, -4.25) * mm});
            skArc(sketch, "E1121", {"start": v(-3.75, -4.25) * mm, "mid": v(-3.78, -4.26) * mm, "end": v(-3.8, -4.3) * mm});
            skLineSegment(sketch, "E1122", {"start": v(-3.8, -4.3) * mm, "end": v(-3.8, -4.5) * mm});
            skArc(sketch, "E1123", {"start": v(-3.8, -4.5) * mm, "mid": v(-3.78, -4.53) * mm, "end": v(-3.75, -4.55) * mm});
            skLineSegment(sketch, "E1124", {"start": v(-3.75, -4.55) * mm, "end": v(-3.05, -4.55) * mm});
            skArc(sketch, "E1125", {"start": v(-3.05, -4.55) * mm, "mid": v(-3.02, -4.53) * mm, "end": v(-3, -4.5) * mm});
            skLineSegment(sketch, "E1126", {"start": v(-2.6, -5.7) * mm, "end": v(-2.4, -5.7) * mm});
            skArc(sketch, "E1127", {"start": v(-2.4, -5.7) * mm, "mid": v(-2.37, -5.68) * mm, "end": v(-2.35, -5.65) * mm});
            skLineSegment(sketch, "E1128", {"start": v(-2.35, -5.65) * mm, "end": v(-2.35, -4.95) * mm});
            skArc(sketch, "E1129", {"start": v(-2.35, -4.95) * mm, "mid": v(-2.37, -4.91) * mm, "end": v(-2.4, -4.9) * mm});
            skLineSegment(sketch, "E1130", {"start": v(-2.4, -4.9) * mm, "end": v(-2.6, -4.9) * mm});
            skArc(sketch, "E1131", {"start": v(-2.6, -4.9) * mm, "mid": v(-2.63, -4.91) * mm, "end": v(-2.65, -4.95) * mm});
            skLineSegment(sketch, "E1132", {"start": v(-2.65, -4.95) * mm, "end": v(-2.65, -5.65) * mm});
            skArc(sketch, "E1133", {"start": v(-2.65, -5.65) * mm, "mid": v(-2.63, -5.68) * mm, "end": v(-2.6, -5.7) * mm});
            skLineSegment(sketch, "E1134", {"start": v(-2.1, -5.7) * mm, "end": v(-1.9, -5.7) * mm});
            skArc(sketch, "E1135", {"start": v(-1.9, -5.7) * mm, "mid": v(-1.87, -5.68) * mm, "end": v(-1.85, -5.65) * mm});
            skLineSegment(sketch, "E1136", {"start": v(-1.85, -5.65) * mm, "end": v(-1.85, -4.95) * mm});
            skArc(sketch, "E1137", {"start": v(-1.85, -4.95) * mm, "mid": v(-1.87, -4.91) * mm, "end": v(-1.9, -4.9) * mm});
            skLineSegment(sketch, "E1138", {"start": v(-1.9, -4.9) * mm, "end": v(-2.1, -4.9) * mm});
            skArc(sketch, "E1139", {"start": v(-2.1, -4.9) * mm, "mid": v(-2.13, -4.91) * mm, "end": v(-2.15, -4.95) * mm});
            skLineSegment(sketch, "E1140", {"start": v(-2.15, -4.95) * mm, "end": v(-2.15, -5.65) * mm});
            skArc(sketch, "E1141", {"start": v(-2.15, -5.65) * mm, "mid": v(-2.13, -5.68) * mm, "end": v(-2.1, -5.7) * mm});
            skLineSegment(sketch, "E1142", {"start": v(-1.6, -5.7) * mm, "end": v(-1.4, -5.7) * mm});
            skArc(sketch, "E1143", {"start": v(-1.4, -5.7) * mm, "mid": v(-1.37, -5.68) * mm, "end": v(-1.35, -5.65) * mm});
            skLineSegment(sketch, "E1144", {"start": v(-1.35, -5.65) * mm, "end": v(-1.35, -4.95) * mm});
            skArc(sketch, "E1145", {"start": v(-1.35, -4.95) * mm, "mid": v(-1.37, -4.91) * mm, "end": v(-1.4, -4.9) * mm});
            skLineSegment(sketch, "E1146", {"start": v(-1.4, -4.9) * mm, "end": v(-1.6, -4.9) * mm});
            skArc(sketch, "E1147", {"start": v(-1.6, -4.9) * mm, "mid": v(-1.63, -4.91) * mm, "end": v(-1.65, -4.95) * mm});
            skLineSegment(sketch, "E1148", {"start": v(-1.65, -4.95) * mm, "end": v(-1.65, -5.65) * mm});
            skArc(sketch, "E1149", {"start": v(-1.65, -5.65) * mm, "mid": v(-1.63, -5.68) * mm, "end": v(-1.6, -5.7) * mm});
            skLineSegment(sketch, "E1150", {"start": v(-1.1, -5.7) * mm, "end": v(-0.9, -5.7) * mm});
            skArc(sketch, "E1151", {"start": v(-0.9, -5.7) * mm, "mid": v(-0.87, -5.68) * mm, "end": v(-0.85, -5.65) * mm});
            skLineSegment(sketch, "E1152", {"start": v(-0.85, -5.65) * mm, "end": v(-0.85, -4.95) * mm});
            skArc(sketch, "E1153", {"start": v(-0.85, -4.95) * mm, "mid": v(-0.87, -4.91) * mm, "end": v(-0.9, -4.9) * mm});
            skLineSegment(sketch, "E1154", {"start": v(-0.9, -4.9) * mm, "end": v(-1.1, -4.9) * mm});
            skArc(sketch, "E1155", {"start": v(-1.1, -4.9) * mm, "mid": v(-1.13, -4.91) * mm, "end": v(-1.15, -4.95) * mm});
            skLineSegment(sketch, "E1156", {"start": v(-1.15, -4.95) * mm, "end": v(-1.15, -5.65) * mm});
            skArc(sketch, "E1157", {"start": v(-1.15, -5.65) * mm, "mid": v(-1.13, -5.68) * mm, "end": v(-1.1, -5.7) * mm});
            skLineSegment(sketch, "E1158", {"start": v(-0.6, -5.7) * mm, "end": v(-0.4, -5.7) * mm});
            skArc(sketch, "E1159", {"start": v(-0.4, -5.7) * mm, "mid": v(-0.37, -5.68) * mm, "end": v(-0.35, -5.65) * mm});
            skLineSegment(sketch, "E1160", {"start": v(-0.35, -5.65) * mm, "end": v(-0.35, -4.95) * mm});
            skArc(sketch, "E1161", {"start": v(-0.35, -4.95) * mm, "mid": v(-0.37, -4.91) * mm, "end": v(-0.4, -4.9) * mm});
            skLineSegment(sketch, "E1162", {"start": v(-0.4, -4.9) * mm, "end": v(-0.6, -4.9) * mm});
            skArc(sketch, "E1163", {"start": v(-0.6, -4.9) * mm, "mid": v(-0.63, -4.91) * mm, "end": v(-0.65, -4.95) * mm});
            skLineSegment(sketch, "E1164", {"start": v(-0.65, -4.95) * mm, "end": v(-0.65, -5.65) * mm});
            skArc(sketch, "E1165", {"start": v(-0.65, -5.65) * mm, "mid": v(-0.63, -5.68) * mm, "end": v(-0.6, -5.7) * mm});
            skLineSegment(sketch, "E1166", {"start": v(-0.1, -5.7) * mm, "end": v(0.1, -5.7) * mm});
            skArc(sketch, "E1167", {"start": v(0.1, -5.7) * mm, "mid": v(0.13, -5.68) * mm, "end": v(0.15, -5.65) * mm});
            skLineSegment(sketch, "E1168", {"start": v(0.15, -5.65) * mm, "end": v(0.15, -4.95) * mm});
            skArc(sketch, "E1169", {"start": v(0.15, -4.95) * mm, "mid": v(0.13, -4.91) * mm, "end": v(0.1, -4.9) * mm});
            skLineSegment(sketch, "E1170", {"start": v(0.1, -4.9) * mm, "end": v(-0.1, -4.9) * mm});
            skArc(sketch, "E1171", {"start": v(-0.1, -4.9) * mm, "mid": v(-0.13, -4.91) * mm, "end": v(-0.15, -4.95) * mm});
            skLineSegment(sketch, "E1172", {"start": v(-0.15, -4.95) * mm, "end": v(-0.15, -5.65) * mm});
            skArc(sketch, "E1173", {"start": v(-0.15, -5.65) * mm, "mid": v(-0.13, -5.68) * mm, "end": v(-0.1, -5.7) * mm});
            skLineSegment(sketch, "E1174", {"start": v(0.6, -4.9) * mm, "end": v(0.4, -4.9) * mm});
            skArc(sketch, "E1175", {"start": v(0.4, -4.9) * mm, "mid": v(0.37, -4.91) * mm, "end": v(0.35, -4.95) * mm});
            skLineSegment(sketch, "E1176", {"start": v(0.35, -4.95) * mm, "end": v(0.35, -5.65) * mm});
            skArc(sketch, "E1177", {"start": v(0.35, -5.65) * mm, "mid": v(0.37, -5.68) * mm, "end": v(0.4, -5.7) * mm});
            skLineSegment(sketch, "E1178", {"start": v(0.4, -5.7) * mm, "end": v(0.6, -5.7) * mm});
            skArc(sketch, "E1179", {"start": v(0.6, -5.7) * mm, "mid": v(0.63, -5.68) * mm, "end": v(0.65, -5.65) * mm});
            skLineSegment(sketch, "E1180", {"start": v(0.65, -5.65) * mm, "end": v(0.65, -4.95) * mm});
            skArc(sketch, "E1181", {"start": v(0.65, -4.95) * mm, "mid": v(0.63, -4.91) * mm, "end": v(0.6, -4.9) * mm});
            skLineSegment(sketch, "E1182", {"start": v(1.1, -4.9) * mm, "end": v(0.9, -4.9) * mm});
            skArc(sketch, "E1183", {"start": v(0.9, -4.9) * mm, "mid": v(0.87, -4.91) * mm, "end": v(0.85, -4.95) * mm});
            skLineSegment(sketch, "E1184", {"start": v(0.85, -4.95) * mm, "end": v(0.85, -5.65) * mm});
            skArc(sketch, "E1185", {"start": v(0.85, -5.65) * mm, "mid": v(0.87, -5.68) * mm, "end": v(0.9, -5.7) * mm});
            skLineSegment(sketch, "E1186", {"start": v(0.9, -5.7) * mm, "end": v(1.1, -5.7) * mm});
            skArc(sketch, "E1187", {"start": v(1.1, -5.7) * mm, "mid": v(1.13, -5.68) * mm, "end": v(1.15, -5.65) * mm});
            skLineSegment(sketch, "E1188", {"start": v(1.15, -5.65) * mm, "end": v(1.15, -4.95) * mm});
            skArc(sketch, "E1189", {"start": v(1.15, -4.95) * mm, "mid": v(1.13, -4.91) * mm, "end": v(1.1, -4.9) * mm});
            skLineSegment(sketch, "E1190", {"start": v(1.6, -4.9) * mm, "end": v(1.4, -4.9) * mm});
            skArc(sketch, "E1191", {"start": v(1.4, -4.9) * mm, "mid": v(1.37, -4.91) * mm, "end": v(1.35, -4.95) * mm});
            skLineSegment(sketch, "E1192", {"start": v(1.35, -4.95) * mm, "end": v(1.35, -5.65) * mm});
            skArc(sketch, "E1193", {"start": v(1.35, -5.65) * mm, "mid": v(1.37, -5.68) * mm, "end": v(1.4, -5.7) * mm});
            skLineSegment(sketch, "E1194", {"start": v(1.4, -5.7) * mm, "end": v(1.6, -5.7) * mm});
            skArc(sketch, "E1195", {"start": v(1.6, -5.7) * mm, "mid": v(1.63, -5.68) * mm, "end": v(1.65, -5.65) * mm});
            skLineSegment(sketch, "E1196", {"start": v(1.65, -5.65) * mm, "end": v(1.65, -4.95) * mm});
            skArc(sketch, "E1197", {"start": v(1.65, -4.95) * mm, "mid": v(1.63, -4.91) * mm, "end": v(1.6, -4.9) * mm});
            skLineSegment(sketch, "E1198", {"start": v(2.1, -4.9) * mm, "end": v(1.9, -4.9) * mm});
            skArc(sketch, "E1199", {"start": v(1.9, -4.9) * mm, "mid": v(1.87, -4.91) * mm, "end": v(1.85, -4.95) * mm});
            skLineSegment(sketch, "E1200", {"start": v(1.85, -4.95) * mm, "end": v(1.85, -5.65) * mm});
            skArc(sketch, "E1201", {"start": v(1.85, -5.65) * mm, "mid": v(1.87, -5.68) * mm, "end": v(1.9, -5.7) * mm});
            skLineSegment(sketch, "E1202", {"start": v(1.9, -5.7) * mm, "end": v(2.1, -5.7) * mm});
            skArc(sketch, "E1203", {"start": v(2.1, -5.7) * mm, "mid": v(2.13, -5.68) * mm, "end": v(2.15, -5.65) * mm});
            skLineSegment(sketch, "E1204", {"start": v(2.15, -5.65) * mm, "end": v(2.15, -4.95) * mm});
            skArc(sketch, "E1205", {"start": v(2.15, -4.95) * mm, "mid": v(2.13, -4.91) * mm, "end": v(2.1, -4.9) * mm});
            skLineSegment(sketch, "E1206", {"start": v(2.6, -4.9) * mm, "end": v(2.4, -4.9) * mm});
            skArc(sketch, "E1207", {"start": v(2.4, -4.9) * mm, "mid": v(2.37, -4.91) * mm, "end": v(2.35, -4.95) * mm});
            skLineSegment(sketch, "E1208", {"start": v(2.35, -4.95) * mm, "end": v(2.35, -5.65) * mm});
            skArc(sketch, "E1209", {"start": v(2.35, -5.65) * mm, "mid": v(2.37, -5.68) * mm, "end": v(2.4, -5.7) * mm});
            skLineSegment(sketch, "E1210", {"start": v(2.4, -5.7) * mm, "end": v(2.6, -5.7) * mm});
            skArc(sketch, "E1211", {"start": v(2.6, -5.7) * mm, "mid": v(2.63, -5.68) * mm, "end": v(2.65, -5.65) * mm});
            skLineSegment(sketch, "E1212", {"start": v(2.65, -5.65) * mm, "end": v(2.65, -4.95) * mm});
            skArc(sketch, "E1213", {"start": v(2.65, -4.95) * mm, "mid": v(2.63, -4.91) * mm, "end": v(2.6, -4.9) * mm});
            skLineSegment(sketch, "E1214", {"start": v(3.8, -4.5) * mm, "end": v(3.8, -4.3) * mm});
            skArc(sketch, "E1215", {"start": v(3.8, -4.3) * mm, "mid": v(3.78, -4.26) * mm, "end": v(3.75, -4.25) * mm});
            skLineSegment(sketch, "E1216", {"start": v(3.75, -4.25) * mm, "end": v(3.05, -4.25) * mm});
            skArc(sketch, "E1217", {"start": v(3.05, -4.25) * mm, "mid": v(3.02, -4.26) * mm, "end": v(3, -4.3) * mm});
            skLineSegment(sketch, "E1218", {"start": v(3, -4.3) * mm, "end": v(3, -4.5) * mm});
            skArc(sketch, "E1219", {"start": v(3, -4.5) * mm, "mid": v(3.02, -4.53) * mm, "end": v(3.05, -4.55) * mm});
            skLineSegment(sketch, "E1220", {"start": v(3.05, -4.55) * mm, "end": v(3.75, -4.55) * mm});
            skArc(sketch, "E1221", {"start": v(3.75, -4.55) * mm, "mid": v(3.78, -4.53) * mm, "end": v(3.8, -4.5) * mm});
            skLineSegment(sketch, "E1222", {"start": v(3.8, -4) * mm, "end": v(3.8, -3.8) * mm});
            skArc(sketch, "E1223", {"start": v(3.8, -3.8) * mm, "mid": v(3.78, -3.76) * mm, "end": v(3.75, -3.75) * mm});
            skLineSegment(sketch, "E1224", {"start": v(3.75, -3.75) * mm, "end": v(3.05, -3.75) * mm});
            skArc(sketch, "E1225", {"start": v(3.05, -3.75) * mm, "mid": v(3.02, -3.76) * mm, "end": v(3, -3.8) * mm});
            skLineSegment(sketch, "E1226", {"start": v(3, -3.8) * mm, "end": v(3, -4) * mm});
            skArc(sketch, "E1227", {"start": v(3, -4) * mm, "mid": v(3.02, -4.03) * mm, "end": v(3.05, -4.05) * mm});
            skLineSegment(sketch, "E1228", {"start": v(3.05, -4.05) * mm, "end": v(3.75, -4.05) * mm});
            skArc(sketch, "E1229", {"start": v(3.75, -4.05) * mm, "mid": v(3.78, -4.03) * mm, "end": v(3.8, -4) * mm});
            skLineSegment(sketch, "E1230", {"start": v(3.8, -3.5) * mm, "end": v(3.8, -3.3) * mm});
            skArc(sketch, "E1231", {"start": v(3.8, -3.3) * mm, "mid": v(3.78, -3.26) * mm, "end": v(3.75, -3.25) * mm});
            skLineSegment(sketch, "E1232", {"start": v(3.75, -3.25) * mm, "end": v(3.05, -3.25) * mm});
            skArc(sketch, "E1233", {"start": v(3.05, -3.25) * mm, "mid": v(3.02, -3.26) * mm, "end": v(3, -3.3) * mm});
            skLineSegment(sketch, "E1234", {"start": v(3, -3.3) * mm, "end": v(3, -3.5) * mm});
            skArc(sketch, "E1235", {"start": v(3, -3.5) * mm, "mid": v(3.02, -3.53) * mm, "end": v(3.05, -3.55) * mm});
            skLineSegment(sketch, "E1236", {"start": v(3.05, -3.55) * mm, "end": v(3.75, -3.55) * mm});
            skArc(sketch, "E1237", {"start": v(3.75, -3.55) * mm, "mid": v(3.78, -3.53) * mm, "end": v(3.8, -3.5) * mm});
            skLineSegment(sketch, "E1238", {"start": v(3.8, -3) * mm, "end": v(3.8, -2.8) * mm});
            skArc(sketch, "E1239", {"start": v(3.8, -2.8) * mm, "mid": v(3.78, -2.76) * mm, "end": v(3.75, -2.75) * mm});
            skLineSegment(sketch, "E1240", {"start": v(3.75, -2.75) * mm, "end": v(3.05, -2.75) * mm});
            skArc(sketch, "E1241", {"start": v(3.05, -2.75) * mm, "mid": v(3.02, -2.76) * mm, "end": v(3, -2.8) * mm});
            skLineSegment(sketch, "E1242", {"start": v(3, -2.8) * mm, "end": v(3, -3) * mm});
            skArc(sketch, "E1243", {"start": v(3, -3) * mm, "mid": v(3.02, -3.03) * mm, "end": v(3.05, -3.05) * mm});
            skLineSegment(sketch, "E1244", {"start": v(3.05, -3.05) * mm, "end": v(3.75, -3.05) * mm});
            skArc(sketch, "E1245", {"start": v(3.75, -3.05) * mm, "mid": v(3.78, -3.03) * mm, "end": v(3.8, -3) * mm});
            skLineSegment(sketch, "E1246", {"start": v(3.8, -2.5) * mm, "end": v(3.8, -2.3) * mm});
            skArc(sketch, "E1247", {"start": v(3.8, -2.3) * mm, "mid": v(3.78, -2.26) * mm, "end": v(3.75, -2.25) * mm});
            skLineSegment(sketch, "E1248", {"start": v(3.75, -2.25) * mm, "end": v(3.05, -2.25) * mm});
            skArc(sketch, "E1249", {"start": v(3.05, -2.25) * mm, "mid": v(3.02, -2.26) * mm, "end": v(3, -2.3) * mm});
            skLineSegment(sketch, "E1250", {"start": v(3, -2.3) * mm, "end": v(3, -2.5) * mm});
            skArc(sketch, "E1251", {"start": v(3, -2.5) * mm, "mid": v(3.02, -2.53) * mm, "end": v(3.05, -2.55) * mm});
            skLineSegment(sketch, "E1252", {"start": v(3.05, -2.55) * mm, "end": v(3.75, -2.55) * mm});
            skArc(sketch, "E1253", {"start": v(3.75, -2.55) * mm, "mid": v(3.78, -2.53) * mm, "end": v(3.8, -2.5) * mm});
            skLineSegment(sketch, "E1254", {"start": v(3.8, -2) * mm, "end": v(3.8, -1.8) * mm});
            skArc(sketch, "E1255", {"start": v(3.8, -1.8) * mm, "mid": v(3.78, -1.76) * mm, "end": v(3.75, -1.75) * mm});
            skLineSegment(sketch, "E1256", {"start": v(3.75, -1.75) * mm, "end": v(3.05, -1.75) * mm});
            skArc(sketch, "E1257", {"start": v(3.05, -1.75) * mm, "mid": v(3.02, -1.76) * mm, "end": v(3, -1.8) * mm});
            skLineSegment(sketch, "E1258", {"start": v(3, -1.8) * mm, "end": v(3, -2) * mm});
            skArc(sketch, "E1259", {"start": v(3, -2) * mm, "mid": v(3.02, -2.03) * mm, "end": v(3.05, -2.05) * mm});
            skLineSegment(sketch, "E1260", {"start": v(3.05, -2.05) * mm, "end": v(3.75, -2.05) * mm});
            skArc(sketch, "E1261", {"start": v(3.75, -2.05) * mm, "mid": v(3.78, -2.03) * mm, "end": v(3.8, -2) * mm});
            skLineSegment(sketch, "E1262", {"start": v(3, -1.3) * mm, "end": v(3, -1.5) * mm});
            skArc(sketch, "E1263", {"start": v(3, -1.5) * mm, "mid": v(3.02, -1.53) * mm, "end": v(3.05, -1.55) * mm});
            skLineSegment(sketch, "E1264", {"start": v(3.05, -1.55) * mm, "end": v(3.75, -1.55) * mm});
            skArc(sketch, "E1265", {"start": v(3.75, -1.55) * mm, "mid": v(3.78, -1.53) * mm, "end": v(3.8, -1.5) * mm});
            skLineSegment(sketch, "E1266", {"start": v(3.8, -1.5) * mm, "end": v(3.8, -1.3) * mm});
            skArc(sketch, "E1267", {"start": v(3.8, -1.3) * mm, "mid": v(3.78, -1.26) * mm, "end": v(3.75, -1.25) * mm});
            skLineSegment(sketch, "E1268", {"start": v(3.75, -1.25) * mm, "end": v(3.05, -1.25) * mm});
            skArc(sketch, "E1269", {"start": v(3.05, -1.25) * mm, "mid": v(3.02, -1.26) * mm, "end": v(3, -1.3) * mm});
            skLineSegment(sketch, "E1270", {"start": v(3, -0.8) * mm, "end": v(3, -1) * mm});
            skArc(sketch, "E1271", {"start": v(3, -1) * mm, "mid": v(3.02, -1.03) * mm, "end": v(3.05, -1.05) * mm});
            skLineSegment(sketch, "E1272", {"start": v(3.05, -1.05) * mm, "end": v(3.75, -1.05) * mm});
            skArc(sketch, "E1273", {"start": v(3.75, -1.05) * mm, "mid": v(3.78, -1.03) * mm, "end": v(3.8, -1) * mm});
            skLineSegment(sketch, "E1274", {"start": v(3.8, -1) * mm, "end": v(3.8, -0.8) * mm});
            skArc(sketch, "E1275", {"start": v(3.8, -0.8) * mm, "mid": v(3.78, -0.76) * mm, "end": v(3.75, -0.75) * mm});
            skLineSegment(sketch, "E1276", {"start": v(3.75, -0.75) * mm, "end": v(3.05, -0.75) * mm});
            skArc(sketch, "E1277", {"start": v(3.05, -0.75) * mm, "mid": v(3.02, -0.76) * mm, "end": v(3, -0.8) * mm});
            skLineSegment(sketch, "E1278", {"start": v(3, -0.3) * mm, "end": v(3, -0.5) * mm});
            skArc(sketch, "E1279", {"start": v(3, -0.5) * mm, "mid": v(3.02, -0.53) * mm, "end": v(3.05, -0.55) * mm});
            skLineSegment(sketch, "E1280", {"start": v(3.05, -0.55) * mm, "end": v(3.75, -0.55) * mm});
            skArc(sketch, "E1281", {"start": v(3.75, -0.55) * mm, "mid": v(3.78, -0.53) * mm, "end": v(3.8, -0.5) * mm});
            skLineSegment(sketch, "E1282", {"start": v(3.8, -0.5) * mm, "end": v(3.8, -0.3) * mm});
            skArc(sketch, "E1283", {"start": v(3.8, -0.3) * mm, "mid": v(3.78, -0.26) * mm, "end": v(3.75, -0.25) * mm});
            skLineSegment(sketch, "E1284", {"start": v(3.75, -0.25) * mm, "end": v(3.05, -0.25) * mm});
            skArc(sketch, "E1285", {"start": v(3.05, -0.25) * mm, "mid": v(3.02, -0.26) * mm, "end": v(3, -0.3) * mm});
            skLineSegment(sketch, "E1286", {"start": v(3, 0.2) * mm, "end": v(3, 0) * mm});
            skArc(sketch, "E1287", {"start": v(3, 0) * mm, "mid": v(3.02, -0.03) * mm, "end": v(3.05, -0.05) * mm});
            skLineSegment(sketch, "E1288", {"start": v(3.05, -0.05) * mm, "end": v(3.75, -0.05) * mm});
            skArc(sketch, "E1289", {"start": v(3.75, -0.05) * mm, "mid": v(3.78, -0.03) * mm, "end": v(3.8, 0) * mm});
            skLineSegment(sketch, "E1290", {"start": v(3.8, 0) * mm, "end": v(3.8, 0.2) * mm});
            skArc(sketch, "E1291", {"start": v(3.8, 0.2) * mm, "mid": v(3.78, 0.24) * mm, "end": v(3.75, 0.25) * mm});
            skLineSegment(sketch, "E1292", {"start": v(3.75, 0.25) * mm, "end": v(3.05, 0.25) * mm});
            skArc(sketch, "E1293", {"start": v(3.05, 0.25) * mm, "mid": v(3.02, 0.24) * mm, "end": v(3, 0.2) * mm});
            skLineSegment(sketch, "E1294", {"start": v(3, 0.7) * mm, "end": v(3, 0.5) * mm});
            skArc(sketch, "E1295", {"start": v(3, 0.5) * mm, "mid": v(3.02, 0.47) * mm, "end": v(3.05, 0.45) * mm});
            skLineSegment(sketch, "E1296", {"start": v(3.05, 0.45) * mm, "end": v(3.75, 0.45) * mm});
            skArc(sketch, "E1297", {"start": v(3.75, 0.45) * mm, "mid": v(3.78, 0.47) * mm, "end": v(3.8, 0.5) * mm});
            skLineSegment(sketch, "E1298", {"start": v(3.8, 0.5) * mm, "end": v(3.8, 0.7) * mm});
            skArc(sketch, "E1299", {"start": v(3.8, 0.7) * mm, "mid": v(3.78, 0.74) * mm, "end": v(3.75, 0.75) * mm});
            skLineSegment(sketch, "E1300", {"start": v(3.75, 0.75) * mm, "end": v(3.05, 0.75) * mm});
            skArc(sketch, "E1301", {"start": v(3.05, 0.75) * mm, "mid": v(3.02, 0.74) * mm, "end": v(3, 0.7) * mm});
            skLineSegment(sketch, "E1302", {"start": v(2.6, 1.9) * mm, "end": v(2.4, 1.9) * mm});
            skArc(sketch, "E1303", {"start": v(2.4, 1.9) * mm, "mid": v(2.37, 1.89) * mm, "end": v(2.35, 1.85) * mm});
            skLineSegment(sketch, "E1304", {"start": v(2.35, 1.85) * mm, "end": v(2.35, 1.15) * mm});
            skArc(sketch, "E1305", {"start": v(2.35, 1.15) * mm, "mid": v(2.37, 1.12) * mm, "end": v(2.4, 1.1) * mm});
            skLineSegment(sketch, "E1306", {"start": v(2.4, 1.1) * mm, "end": v(2.6, 1.1) * mm});
            skArc(sketch, "E1307", {"start": v(2.6, 1.1) * mm, "mid": v(2.63, 1.12) * mm, "end": v(2.65, 1.15) * mm});
            skLineSegment(sketch, "E1308", {"start": v(2.65, 1.15) * mm, "end": v(2.65, 1.85) * mm});
            skArc(sketch, "E1309", {"start": v(2.65, 1.85) * mm, "mid": v(2.63, 1.89) * mm, "end": v(2.6, 1.9) * mm});
            skLineSegment(sketch, "E1310", {"start": v(2.1, 1.9) * mm, "end": v(1.9, 1.9) * mm});
            skArc(sketch, "E1311", {"start": v(1.9, 1.9) * mm, "mid": v(1.87, 1.89) * mm, "end": v(1.85, 1.85) * mm});
            skLineSegment(sketch, "E1312", {"start": v(1.85, 1.85) * mm, "end": v(1.85, 1.15) * mm});
            skArc(sketch, "E1313", {"start": v(1.85, 1.15) * mm, "mid": v(1.87, 1.12) * mm, "end": v(1.9, 1.1) * mm});
            skLineSegment(sketch, "E1314", {"start": v(1.9, 1.1) * mm, "end": v(2.1, 1.1) * mm});
            skArc(sketch, "E1315", {"start": v(2.1, 1.1) * mm, "mid": v(2.13, 1.12) * mm, "end": v(2.15, 1.15) * mm});
            skLineSegment(sketch, "E1316", {"start": v(2.15, 1.15) * mm, "end": v(2.15, 1.85) * mm});
            skArc(sketch, "E1317", {"start": v(2.15, 1.85) * mm, "mid": v(2.13, 1.89) * mm, "end": v(2.1, 1.9) * mm});
            skLineSegment(sketch, "E1318", {"start": v(1.6, 1.9) * mm, "end": v(1.4, 1.9) * mm});
            skArc(sketch, "E1319", {"start": v(1.4, 1.9) * mm, "mid": v(1.37, 1.89) * mm, "end": v(1.35, 1.85) * mm});
            skLineSegment(sketch, "E1320", {"start": v(1.35, 1.85) * mm, "end": v(1.35, 1.15) * mm});
            skArc(sketch, "E1321", {"start": v(1.35, 1.15) * mm, "mid": v(1.37, 1.12) * mm, "end": v(1.4, 1.1) * mm});
            skLineSegment(sketch, "E1322", {"start": v(1.4, 1.1) * mm, "end": v(1.6, 1.1) * mm});
            skArc(sketch, "E1323", {"start": v(1.6, 1.1) * mm, "mid": v(1.63, 1.12) * mm, "end": v(1.65, 1.15) * mm});
            skLineSegment(sketch, "E1324", {"start": v(1.65, 1.15) * mm, "end": v(1.65, 1.85) * mm});
            skArc(sketch, "E1325", {"start": v(1.65, 1.85) * mm, "mid": v(1.63, 1.89) * mm, "end": v(1.6, 1.9) * mm});
            skLineSegment(sketch, "E1326", {"start": v(1.1, 1.9) * mm, "end": v(0.9, 1.9) * mm});
            skArc(sketch, "E1327", {"start": v(0.9, 1.9) * mm, "mid": v(0.87, 1.89) * mm, "end": v(0.85, 1.85) * mm});
            skLineSegment(sketch, "E1328", {"start": v(0.85, 1.85) * mm, "end": v(0.85, 1.15) * mm});
            skArc(sketch, "E1329", {"start": v(0.85, 1.15) * mm, "mid": v(0.87, 1.12) * mm, "end": v(0.9, 1.1) * mm});
            skLineSegment(sketch, "E1330", {"start": v(0.9, 1.1) * mm, "end": v(1.1, 1.1) * mm});
            skArc(sketch, "E1331", {"start": v(1.1, 1.1) * mm, "mid": v(1.13, 1.12) * mm, "end": v(1.15, 1.15) * mm});
            skLineSegment(sketch, "E1332", {"start": v(1.15, 1.15) * mm, "end": v(1.15, 1.85) * mm});
            skArc(sketch, "E1333", {"start": v(1.15, 1.85) * mm, "mid": v(1.13, 1.89) * mm, "end": v(1.1, 1.9) * mm});
            skLineSegment(sketch, "E1334", {"start": v(0.6, 1.9) * mm, "end": v(0.4, 1.9) * mm});
            skArc(sketch, "E1335", {"start": v(0.4, 1.9) * mm, "mid": v(0.37, 1.89) * mm, "end": v(0.35, 1.85) * mm});
            skLineSegment(sketch, "E1336", {"start": v(0.35, 1.85) * mm, "end": v(0.35, 1.15) * mm});
            skArc(sketch, "E1337", {"start": v(0.35, 1.15) * mm, "mid": v(0.37, 1.12) * mm, "end": v(0.4, 1.1) * mm});
            skLineSegment(sketch, "E1338", {"start": v(0.4, 1.1) * mm, "end": v(0.6, 1.1) * mm});
            skArc(sketch, "E1339", {"start": v(0.6, 1.1) * mm, "mid": v(0.63, 1.12) * mm, "end": v(0.65, 1.15) * mm});
            skLineSegment(sketch, "E1340", {"start": v(0.65, 1.15) * mm, "end": v(0.65, 1.85) * mm});
            skArc(sketch, "E1341", {"start": v(0.65, 1.85) * mm, "mid": v(0.63, 1.89) * mm, "end": v(0.6, 1.9) * mm});
            skLineSegment(sketch, "E1342", {"start": v(0.1, 1.9) * mm, "end": v(-0.1, 1.9) * mm});
            skArc(sketch, "E1343", {"start": v(-0.1, 1.9) * mm, "mid": v(-0.13, 1.89) * mm, "end": v(-0.15, 1.85) * mm});
            skLineSegment(sketch, "E1344", {"start": v(-0.15, 1.85) * mm, "end": v(-0.15, 1.15) * mm});
            skArc(sketch, "E1345", {"start": v(-0.15, 1.15) * mm, "mid": v(-0.13, 1.12) * mm, "end": v(-0.1, 1.1) * mm});
            skLineSegment(sketch, "E1346", {"start": v(-0.1, 1.1) * mm, "end": v(0.1, 1.1) * mm});
            skArc(sketch, "E1347", {"start": v(0.1, 1.1) * mm, "mid": v(0.13, 1.12) * mm, "end": v(0.15, 1.15) * mm});
            skLineSegment(sketch, "E1348", {"start": v(0.15, 1.15) * mm, "end": v(0.15, 1.85) * mm});
            skArc(sketch, "E1349", {"start": v(0.15, 1.85) * mm, "mid": v(0.13, 1.89) * mm, "end": v(0.1, 1.9) * mm});
            skLineSegment(sketch, "E1350", {"start": v(-0.6, 1.1) * mm, "end": v(-0.4, 1.1) * mm});
            skArc(sketch, "E1351", {"start": v(-0.4, 1.1) * mm, "mid": v(-0.37, 1.12) * mm, "end": v(-0.35, 1.15) * mm});
            skLineSegment(sketch, "E1352", {"start": v(-0.35, 1.15) * mm, "end": v(-0.35, 1.85) * mm});
            skArc(sketch, "E1353", {"start": v(-0.35, 1.85) * mm, "mid": v(-0.37, 1.89) * mm, "end": v(-0.4, 1.9) * mm});
            skLineSegment(sketch, "E1354", {"start": v(-0.4, 1.9) * mm, "end": v(-0.6, 1.9) * mm});
            skArc(sketch, "E1355", {"start": v(-0.6, 1.9) * mm, "mid": v(-0.63, 1.89) * mm, "end": v(-0.65, 1.85) * mm});
            skLineSegment(sketch, "E1356", {"start": v(-0.65, 1.85) * mm, "end": v(-0.65, 1.15) * mm});
            skArc(sketch, "E1357", {"start": v(-0.65, 1.15) * mm, "mid": v(-0.63, 1.12) * mm, "end": v(-0.6, 1.1) * mm});
            skLineSegment(sketch, "E1358", {"start": v(-1.1, 1.1) * mm, "end": v(-0.9, 1.1) * mm});
            skArc(sketch, "E1359", {"start": v(-0.9, 1.1) * mm, "mid": v(-0.87, 1.12) * mm, "end": v(-0.85, 1.15) * mm});
            skLineSegment(sketch, "E1360", {"start": v(-0.85, 1.15) * mm, "end": v(-0.85, 1.85) * mm});
            skArc(sketch, "E1361", {"start": v(-0.85, 1.85) * mm, "mid": v(-0.87, 1.89) * mm, "end": v(-0.9, 1.9) * mm});
            skLineSegment(sketch, "E1362", {"start": v(-0.9, 1.9) * mm, "end": v(-1.1, 1.9) * mm});
            skArc(sketch, "E1363", {"start": v(-1.1, 1.9) * mm, "mid": v(-1.13, 1.89) * mm, "end": v(-1.15, 1.85) * mm});
            skLineSegment(sketch, "E1364", {"start": v(-1.15, 1.85) * mm, "end": v(-1.15, 1.15) * mm});
            skArc(sketch, "E1365", {"start": v(-1.15, 1.15) * mm, "mid": v(-1.13, 1.12) * mm, "end": v(-1.1, 1.1) * mm});
            skLineSegment(sketch, "E1366", {"start": v(-1.6, 1.1) * mm, "end": v(-1.4, 1.1) * mm});
            skArc(sketch, "E1367", {"start": v(-1.4, 1.1) * mm, "mid": v(-1.37, 1.12) * mm, "end": v(-1.35, 1.15) * mm});
            skLineSegment(sketch, "E1368", {"start": v(-1.35, 1.15) * mm, "end": v(-1.35, 1.85) * mm});
            skArc(sketch, "E1369", {"start": v(-1.35, 1.85) * mm, "mid": v(-1.37, 1.89) * mm, "end": v(-1.4, 1.9) * mm});
            skLineSegment(sketch, "E1370", {"start": v(-1.4, 1.9) * mm, "end": v(-1.6, 1.9) * mm});
            skArc(sketch, "E1371", {"start": v(-1.6, 1.9) * mm, "mid": v(-1.63, 1.89) * mm, "end": v(-1.65, 1.85) * mm});
            skLineSegment(sketch, "E1372", {"start": v(-1.65, 1.85) * mm, "end": v(-1.65, 1.15) * mm});
            skArc(sketch, "E1373", {"start": v(-1.65, 1.15) * mm, "mid": v(-1.63, 1.12) * mm, "end": v(-1.6, 1.1) * mm});
            skLineSegment(sketch, "E1374", {"start": v(-2.1, 1.1) * mm, "end": v(-1.9, 1.1) * mm});
            skArc(sketch, "E1375", {"start": v(-1.9, 1.1) * mm, "mid": v(-1.87, 1.12) * mm, "end": v(-1.85, 1.15) * mm});
            skLineSegment(sketch, "E1376", {"start": v(-1.85, 1.15) * mm, "end": v(-1.85, 1.85) * mm});
            skArc(sketch, "E1377", {"start": v(-1.85, 1.85) * mm, "mid": v(-1.87, 1.89) * mm, "end": v(-1.9, 1.9) * mm});
            skLineSegment(sketch, "E1378", {"start": v(-1.9, 1.9) * mm, "end": v(-2.1, 1.9) * mm});
            skArc(sketch, "E1379", {"start": v(-2.1, 1.9) * mm, "mid": v(-2.13, 1.89) * mm, "end": v(-2.15, 1.85) * mm});
            skLineSegment(sketch, "E1380", {"start": v(-2.15, 1.85) * mm, "end": v(-2.15, 1.15) * mm});
            skArc(sketch, "E1381", {"start": v(-2.15, 1.15) * mm, "mid": v(-2.13, 1.12) * mm, "end": v(-2.1, 1.1) * mm});
            skLineSegment(sketch, "E1382", {"start": v(-2.6, 1.1) * mm, "end": v(-2.4, 1.1) * mm});
            skArc(sketch, "E1383", {"start": v(-2.4, 1.1) * mm, "mid": v(-2.37, 1.12) * mm, "end": v(-2.35, 1.15) * mm});
            skLineSegment(sketch, "E1384", {"start": v(-2.35, 1.15) * mm, "end": v(-2.35, 1.85) * mm});
            skArc(sketch, "E1385", {"start": v(-2.35, 1.85) * mm, "mid": v(-2.37, 1.89) * mm, "end": v(-2.4, 1.9) * mm});
            skLineSegment(sketch, "E1386", {"start": v(-2.4, 1.9) * mm, "end": v(-2.6, 1.9) * mm});
            skArc(sketch, "E1387", {"start": v(-2.6, 1.9) * mm, "mid": v(-2.63, 1.89) * mm, "end": v(-2.65, 1.85) * mm});
            skLineSegment(sketch, "E1388", {"start": v(-2.65, 1.85) * mm, "end": v(-2.65, 1.15) * mm});
            skArc(sketch, "E1389", {"start": v(-2.65, 1.15) * mm, "mid": v(-2.63, 1.12) * mm, "end": v(-2.6, 1.1) * mm});
            skLineSegment(sketch, "E1390", {"start": v(2.94, -8.5) * mm, "end": v(2.94, -9.6) * mm});
            skArc(sketch, "E1391", {"start": v(2.94, -9.6) * mm, "mid": v(2.96, -9.64) * mm, "end": v(3, -9.65) * mm});
            skLineSegment(sketch, "E1392", {"start": v(3, -9.65) * mm, "end": v(3.45, -9.65) * mm});
            skArc(sketch, "E1393", {"start": v(3.45, -9.65) * mm, "mid": v(3.48, -9.64) * mm, "end": v(3.5, -9.6) * mm});
            skLineSegment(sketch, "E1394", {"start": v(3.5, -9.6) * mm, "end": v(3.5, -8.5) * mm});
            skArc(sketch, "E1395", {"start": v(3.5, -8.5) * mm, "mid": v(3.48, -8.46) * mm, "end": v(3.45, -8.45) * mm});
            skLineSegment(sketch, "E1396", {"start": v(3.45, -8.45) * mm, "end": v(3, -8.45) * mm});
            skArc(sketch, "E1397", {"start": v(3, -8.45) * mm, "mid": v(2.96, -8.46) * mm, "end": v(2.94, -8.5) * mm});
            skLineSegment(sketch, "E1398", {"start": v(2, -8.5) * mm, "end": v(2, -9.6) * mm});
            skArc(sketch, "E1399", {"start": v(2, -9.6) * mm, "mid": v(2, -9.64) * mm, "end": v(2.04, -9.65) * mm});
            skLineSegment(sketch, "E1400", {"start": v(2.04, -9.65) * mm, "end": v(2.5, -9.65) * mm});
            skArc(sketch, "E1401", {"start": v(2.5, -9.65) * mm, "mid": v(2.53, -9.64) * mm, "end": v(2.55, -9.6) * mm});
            skLineSegment(sketch, "E1402", {"start": v(2.55, -9.6) * mm, "end": v(2.55, -8.5) * mm});
            skArc(sketch, "E1403", {"start": v(2.55, -8.5) * mm, "mid": v(2.53, -8.46) * mm, "end": v(2.5, -8.45) * mm});
            skLineSegment(sketch, "E1404", {"start": v(2.5, -8.45) * mm, "end": v(2.04, -8.45) * mm});
            skArc(sketch, "E1405", {"start": v(2.04, -8.45) * mm, "mid": v(2, -8.46) * mm, "end": v(2, -8.5) * mm});
            skLineSegment(sketch, "E1406", {"start": v(1.04, -8.5) * mm, "end": v(1.04, -9.6) * mm});
            skArc(sketch, "E1407", {"start": v(1.04, -9.6) * mm, "mid": v(1.06, -9.64) * mm, "end": v(1.1, -9.65) * mm});
            skLineSegment(sketch, "E1408", {"start": v(1.1, -9.65) * mm, "end": v(1.55, -9.65) * mm});
            skArc(sketch, "E1409", {"start": v(1.55, -9.65) * mm, "mid": v(1.58, -9.64) * mm, "end": v(1.6, -9.6) * mm});
            skLineSegment(sketch, "E1410", {"start": v(1.6, -9.6) * mm, "end": v(1.6, -8.5) * mm});
            skArc(sketch, "E1411", {"start": v(1.6, -8.5) * mm, "mid": v(1.58, -8.46) * mm, "end": v(1.55, -8.45) * mm});
            skLineSegment(sketch, "E1412", {"start": v(1.55, -8.45) * mm, "end": v(1.1, -8.45) * mm});
            skArc(sketch, "E1413", {"start": v(1.1, -8.45) * mm, "mid": v(1.06, -8.46) * mm, "end": v(1.04, -8.5) * mm});
            skLineSegment(sketch, "E1414", {"start": v(1.04, -11.1) * mm, "end": v(1.04, -12.2) * mm});
            skArc(sketch, "E1415", {"start": v(1.04, -12.2) * mm, "mid": v(1.06, -12.24) * mm, "end": v(1.1, -12.25) * mm});
            skLineSegment(sketch, "E1416", {"start": v(1.1, -12.25) * mm, "end": v(1.55, -12.25) * mm});
            skArc(sketch, "E1417", {"start": v(1.55, -12.25) * mm, "mid": v(1.58, -12.24) * mm, "end": v(1.6, -12.2) * mm});
            skLineSegment(sketch, "E1418", {"start": v(1.6, -12.2) * mm, "end": v(1.6, -11.1) * mm});
            skArc(sketch, "E1419", {"start": v(1.6, -11.1) * mm, "mid": v(1.58, -11.06) * mm, "end": v(1.55, -11.05) * mm});
            skLineSegment(sketch, "E1420", {"start": v(1.55, -11.05) * mm, "end": v(1.1, -11.05) * mm});
            skArc(sketch, "E1421", {"start": v(1.1, -11.05) * mm, "mid": v(1.06, -11.06) * mm, "end": v(1.04, -11.1) * mm});
            skLineSegment(sketch, "E1422", {"start": v(2.94, -11.1) * mm, "end": v(2.94, -12.2) * mm});
            skArc(sketch, "E1423", {"start": v(2.94, -12.2) * mm, "mid": v(2.96, -12.24) * mm, "end": v(3, -12.25) * mm});
            skLineSegment(sketch, "E1424", {"start": v(3, -12.25) * mm, "end": v(3.45, -12.25) * mm});
            skArc(sketch, "E1425", {"start": v(3.45, -12.25) * mm, "mid": v(3.48, -12.24) * mm, "end": v(3.5, -12.2) * mm});
            skLineSegment(sketch, "E1426", {"start": v(3.5, -12.2) * mm, "end": v(3.5, -11.1) * mm});
            skArc(sketch, "E1427", {"start": v(3.5, -11.1) * mm, "mid": v(3.48, -11.06) * mm, "end": v(3.45, -11.05) * mm});
            skLineSegment(sketch, "E1428", {"start": v(3.45, -11.05) * mm, "end": v(3, -11.05) * mm});
            skArc(sketch, "E1429", {"start": v(3, -11.05) * mm, "mid": v(2.96, -11.06) * mm, "end": v(2.94, -11.1) * mm});
            skLineSegment(sketch, "E1430", {"start": v(6.07, -8.91) * mm, "end": v(5.43, -8.91) * mm});
            skArc(sketch, "E1431", {"start": v(5.43, -8.91) * mm, "mid": v(5.39, -8.93) * mm, "end": v(5.37, -8.98) * mm});
            skLineSegment(sketch, "E1432", {"start": v(5.37, -8.98) * mm, "end": v(5.37, -9.61) * mm});
            skArc(sketch, "E1433", {"start": v(5.37, -9.61) * mm, "mid": v(5.39, -9.66) * mm, "end": v(5.43, -9.68) * mm});
            skLineSegment(sketch, "E1434", {"start": v(5.43, -9.68) * mm, "end": v(6.07, -9.68) * mm});
            skArc(sketch, "E1435", {"start": v(6.07, -9.68) * mm, "mid": v(6.11, -9.66) * mm, "end": v(6.13, -9.61) * mm});
            skLineSegment(sketch, "E1436", {"start": v(6.13, -9.61) * mm, "end": v(6.13, -8.98) * mm});
            skArc(sketch, "E1437", {"start": v(6.13, -8.98) * mm, "mid": v(6.11, -8.93) * mm, "end": v(6.07, -8.91) * mm});
            skLineSegment(sketch, "E1438", {"start": v(4.57, -8.91) * mm, "end": v(3.93, -8.91) * mm});
            skArc(sketch, "E1439", {"start": v(3.93, -8.91) * mm, "mid": v(3.89, -8.93) * mm, "end": v(3.87, -8.98) * mm});
            skLineSegment(sketch, "E1440", {"start": v(3.87, -8.98) * mm, "end": v(3.87, -9.61) * mm});
            skArc(sketch, "E1441", {"start": v(3.87, -9.61) * mm, "mid": v(3.89, -9.66) * mm, "end": v(3.93, -9.68) * mm});
            skLineSegment(sketch, "E1442", {"start": v(3.93, -9.68) * mm, "end": v(4.57, -9.68) * mm});
            skArc(sketch, "E1443", {"start": v(4.57, -9.68) * mm, "mid": v(4.61, -9.66) * mm, "end": v(4.63, -9.61) * mm});
            skLineSegment(sketch, "E1444", {"start": v(4.63, -9.61) * mm, "end": v(4.63, -8.98) * mm});
            skArc(sketch, "E1445", {"start": v(4.63, -8.98) * mm, "mid": v(4.61, -8.93) * mm, "end": v(4.57, -8.91) * mm});
            skLineSegment(sketch, "E1446", {"start": v(4.27, -7.21) * mm, "end": v(3.63, -7.21) * mm});
            skArc(sketch, "E1447", {"start": v(3.63, -7.21) * mm, "mid": v(3.59, -7.23) * mm, "end": v(3.57, -7.28) * mm});
            skLineSegment(sketch, "E1448", {"start": v(3.57, -7.28) * mm, "end": v(3.57, -7.91) * mm});
            skArc(sketch, "E1449", {"start": v(3.57, -7.91) * mm, "mid": v(3.59, -7.96) * mm, "end": v(3.63, -7.98) * mm});
            skLineSegment(sketch, "E1450", {"start": v(3.63, -7.98) * mm, "end": v(4.27, -7.98) * mm});
            skArc(sketch, "E1451", {"start": v(4.27, -7.98) * mm, "mid": v(4.31, -7.96) * mm, "end": v(4.33, -7.91) * mm});
            skLineSegment(sketch, "E1452", {"start": v(4.33, -7.91) * mm, "end": v(4.33, -7.28) * mm});
            skArc(sketch, "E1453", {"start": v(4.33, -7.28) * mm, "mid": v(4.31, -7.23) * mm, "end": v(4.27, -7.21) * mm});
            skLineSegment(sketch, "E1454", {"start": v(2.77, -7.21) * mm, "end": v(2.13, -7.21) * mm});
            skArc(sketch, "E1455", {"start": v(2.13, -7.21) * mm, "mid": v(2.09, -7.23) * mm, "end": v(2.07, -7.28) * mm});
            skLineSegment(sketch, "E1456", {"start": v(2.07, -7.28) * mm, "end": v(2.07, -7.91) * mm});
            skArc(sketch, "E1457", {"start": v(2.07, -7.91) * mm, "mid": v(2.09, -7.96) * mm, "end": v(2.13, -7.98) * mm});
            skLineSegment(sketch, "E1458", {"start": v(2.13, -7.98) * mm, "end": v(2.77, -7.98) * mm});
            skArc(sketch, "E1459", {"start": v(2.77, -7.98) * mm, "mid": v(2.81, -7.96) * mm, "end": v(2.83, -7.91) * mm});
            skLineSegment(sketch, "E1460", {"start": v(2.83, -7.91) * mm, "end": v(2.83, -7.28) * mm});
            skArc(sketch, "E1461", {"start": v(2.83, -7.28) * mm, "mid": v(2.81, -7.23) * mm, "end": v(2.77, -7.21) * mm});
            skLineSegment(sketch, "E1462", {"start": v(-4.27, -7.98) * mm, "end": v(-3.63, -7.98) * mm});
            skArc(sketch, "E1463", {"start": v(-3.63, -7.98) * mm, "mid": v(-3.59, -7.96) * mm, "end": v(-3.57, -7.91) * mm});
            skLineSegment(sketch, "E1464", {"start": v(-3.57, -7.91) * mm, "end": v(-3.57, -7.28) * mm});
            skArc(sketch, "E1465", {"start": v(-3.57, -7.28) * mm, "mid": v(-3.59, -7.23) * mm, "end": v(-3.63, -7.21) * mm});
            skLineSegment(sketch, "E1466", {"start": v(-3.63, -7.21) * mm, "end": v(-4.27, -7.21) * mm});
            skArc(sketch, "E1467", {"start": v(-4.27, -7.21) * mm, "mid": v(-4.31, -7.23) * mm, "end": v(-4.33, -7.28) * mm});
            skLineSegment(sketch, "E1468", {"start": v(-4.33, -7.28) * mm, "end": v(-4.33, -7.91) * mm});
            skArc(sketch, "E1469", {"start": v(-4.33, -7.91) * mm, "mid": v(-4.31, -7.96) * mm, "end": v(-4.27, -7.98) * mm});
            skLineSegment(sketch, "E1470", {"start": v(-2.77, -7.98) * mm, "end": v(-2.13, -7.98) * mm});
            skArc(sketch, "E1471", {"start": v(-2.13, -7.98) * mm, "mid": v(-2.09, -7.96) * mm, "end": v(-2.07, -7.91) * mm});
            skLineSegment(sketch, "E1472", {"start": v(-2.07, -7.91) * mm, "end": v(-2.07, -7.28) * mm});
            skArc(sketch, "E1473", {"start": v(-2.07, -7.28) * mm, "mid": v(-2.09, -7.23) * mm, "end": v(-2.13, -7.21) * mm});
            skLineSegment(sketch, "E1474", {"start": v(-2.13, -7.21) * mm, "end": v(-2.77, -7.21) * mm});
            skArc(sketch, "E1475", {"start": v(-2.77, -7.21) * mm, "mid": v(-2.81, -7.23) * mm, "end": v(-2.83, -7.28) * mm});
            skLineSegment(sketch, "E1476", {"start": v(-2.83, -7.28) * mm, "end": v(-2.83, -7.91) * mm});
            skArc(sketch, "E1477", {"start": v(-2.83, -7.91) * mm, "mid": v(-2.81, -7.96) * mm, "end": v(-2.77, -7.98) * mm});
            skLineSegment(sketch, "E1478", {"start": v(-5.8, 7.32) * mm, "end": v(-6.11, 6.77) * mm});
            skArc(sketch, "E1479", {"start": v(-6.11, 6.77) * mm, "mid": v(-6.12, 6.72) * mm, "end": v(-6.09, 6.68) * mm});
            skLineSegment(sketch, "E1480", {"start": v(-6.09, 6.68) * mm, "end": v(-5.54, 6.36) * mm});
            skArc(sketch, "E1481", {"start": v(-5.54, 6.36) * mm, "mid": v(-5.5, 6.36) * mm, "end": v(-5.45, 6.39) * mm});
            skLineSegment(sketch, "E1482", {"start": v(-5.45, 6.39) * mm, "end": v(-5.14, 6.93) * mm});
            skArc(sketch, "E1483", {"start": v(-5.14, 6.93) * mm, "mid": v(-5.13, 6.98) * mm, "end": v(-5.16, 7.03) * mm});
            skLineSegment(sketch, "E1484", {"start": v(-5.16, 7.03) * mm, "end": v(-5.7, 7.34) * mm});
            skArc(sketch, "E1485", {"start": v(-5.7, 7.34) * mm, "mid": v(-5.76, 7.35) * mm, "end": v(-5.8, 7.32) * mm});
            skLineSegment(sketch, "E1486", {"start": v(-6.55, 6.02) * mm, "end": v(-6.86, 5.47) * mm});
            skArc(sketch, "E1487", {"start": v(-6.86, 5.47) * mm, "mid": v(-6.87, 5.42) * mm, "end": v(-6.84, 5.38) * mm});
            skLineSegment(sketch, "E1488", {"start": v(-6.84, 5.38) * mm, "end": v(-6.3, 5.06) * mm});
            skArc(sketch, "E1489", {"start": v(-6.3, 5.06) * mm, "mid": v(-6.24, 5.06) * mm, "end": v(-6.2, 5.09) * mm});
            skLineSegment(sketch, "E1490", {"start": v(-6.2, 5.09) * mm, "end": v(-5.89, 5.63) * mm});
            skArc(sketch, "E1491", {"start": v(-5.89, 5.63) * mm, "mid": v(-5.88, 5.69) * mm, "end": v(-5.91, 5.73) * mm});
            skLineSegment(sketch, "E1492", {"start": v(-5.91, 5.73) * mm, "end": v(-6.46, 6.04) * mm});
            skArc(sketch, "E1493", {"start": v(-6.46, 6.04) * mm, "mid": v(-6.5, 6.05) * mm, "end": v(-6.55, 6.02) * mm});
            skLineSegment(sketch, "E1494", {"start": v(6.86, 5.47) * mm, "end": v(6.55, 6.02) * mm});
            skArc(sketch, "E1495", {"start": v(6.55, 6.02) * mm, "mid": v(6.5, 6.05) * mm, "end": v(6.46, 6.04) * mm});
            skLineSegment(sketch, "E1496", {"start": v(6.46, 6.04) * mm, "end": v(5.91, 5.73) * mm});
            skArc(sketch, "E1497", {"start": v(5.91, 5.73) * mm, "mid": v(5.88, 5.69) * mm, "end": v(5.89, 5.63) * mm});
            skLineSegment(sketch, "E1498", {"start": v(5.89, 5.63) * mm, "end": v(6.2, 5.09) * mm});
            skArc(sketch, "E1499", {"start": v(6.2, 5.09) * mm, "mid": v(6.24, 5.06) * mm, "end": v(6.3, 5.06) * mm});
            skLineSegment(sketch, "E1500", {"start": v(6.3, 5.06) * mm, "end": v(6.84, 5.38) * mm});
            skArc(sketch, "E1501", {"start": v(6.84, 5.38) * mm, "mid": v(6.87, 5.42) * mm, "end": v(6.86, 5.47) * mm});
            skLineSegment(sketch, "E1502", {"start": v(6.11, 6.77) * mm, "end": v(5.8, 7.32) * mm});
            skArc(sketch, "E1503", {"start": v(5.8, 7.32) * mm, "mid": v(5.76, 7.35) * mm, "end": v(5.7, 7.34) * mm});
            skLineSegment(sketch, "E1504", {"start": v(5.7, 7.34) * mm, "end": v(5.16, 7.03) * mm});
            skArc(sketch, "E1505", {"start": v(5.16, 7.03) * mm, "mid": v(5.13, 6.98) * mm, "end": v(5.14, 6.93) * mm});
            skLineSegment(sketch, "E1506", {"start": v(5.14, 6.93) * mm, "end": v(5.45, 6.39) * mm});
            skArc(sketch, "E1507", {"start": v(5.45, 6.39) * mm, "mid": v(5.5, 6.36) * mm, "end": v(5.54, 6.36) * mm});
            skLineSegment(sketch, "E1508", {"start": v(5.54, 6.36) * mm, "end": v(6.09, 6.68) * mm});
            skArc(sketch, "E1509", {"start": v(6.09, 6.68) * mm, "mid": v(6.12, 6.72) * mm, "end": v(6.11, 6.77) * mm});
            skLineSegment(sketch, "E1510", {"start": v(19.02, 6.17) * mm, "end": v(15.6, 5.05) * mm});
            skArc(sketch, "E1511", {"start": v(15.56, 5.17) * mm, "mid": v(15.48, 5) * mm, "end": v(15.64, 4.93) * mm});
            skArc(sketch, "E1512", {"start": v(19.06, 6.05) * mm, "mid": v(19.14, 6.21) * mm, "end": v(18.98, 6.3) * mm});
            skLineSegment(sketch, "E1513", {"start": v(15.6, 5.05) * mm, "end": v(15.4, 4.95) * mm});
            skArc(sketch, "E1514", {"start": v(15.34, 5.06) * mm, "mid": v(15.29, 4.89) * mm, "end": v(15.46, 4.83) * mm});
            skArc(sketch, "E1515", {"start": v(15.66, 4.94) * mm, "mid": v(15.71, 5.1) * mm, "end": v(15.55, 5.16) * mm});
            skLineSegment(sketch, "E1516", {"start": v(15.4, 4.95) * mm, "end": v(15.21, 4.83) * mm});
            skArc(sketch, "E1517", {"start": v(15.15, 4.93) * mm, "mid": v(15.1, 4.76) * mm, "end": v(15.28, 4.72) * mm});
            skArc(sketch, "E1518", {"start": v(15.47, 4.84) * mm, "mid": v(15.5, 5.01) * mm, "end": v(15.33, 5.05) * mm});
            skLineSegment(sketch, "E1519", {"start": v(15.21, 4.83) * mm, "end": v(15.04, 4.69) * mm});
            skArc(sketch, "E1520", {"start": v(14.96, 4.79) * mm, "mid": v(14.94, 4.61) * mm, "end": v(15.12, 4.6) * mm});
            skArc(sketch, "E1521", {"start": v(15.3, 4.73) * mm, "mid": v(15.31, 4.9) * mm, "end": v(15.14, 4.92) * mm});
            skLineSegment(sketch, "E1522", {"start": v(15.04, 4.69) * mm, "end": v(14.88, 4.54) * mm});
            skArc(sketch, "E1523", {"start": v(14.8, 4.63) * mm, "mid": v(14.8, 4.45) * mm, "end": v(14.97, 4.45) * mm});
            skArc(sketch, "E1524", {"start": v(15.13, 4.6) * mm, "mid": v(15.13, 4.78) * mm, "end": v(14.95, 4.78) * mm});
            skLineSegment(sketch, "E1525", {"start": v(14.88, 4.54) * mm, "end": v(14.74, 4.37) * mm});
            skArc(sketch, "E1526", {"start": v(14.65, 4.45) * mm, "mid": v(14.66, 4.28) * mm, "end": v(14.84, 4.3) * mm});
            skArc(sketch, "E1527", {"start": v(14.98, 4.46) * mm, "mid": v(14.97, 4.63) * mm, "end": v(14.79, 4.62) * mm});
            skLineSegment(sketch, "E1528", {"start": v(14.74, 4.37) * mm, "end": v(14.62, 4.2) * mm});
            skArc(sketch, "E1529", {"start": v(14.52, 4.27) * mm, "mid": v(14.55, 4.1) * mm, "end": v(14.72, 4.12) * mm});
            skArc(sketch, "E1530", {"start": v(14.85, 4.3) * mm, "mid": v(14.82, 4.47) * mm, "end": v(14.64, 4.44) * mm});
            skLineSegment(sketch, "E1531", {"start": v(14.62, 4.2) * mm, "end": v(14.51, 4) * mm});
            skArc(sketch, "E1532", {"start": v(14.4, 4.07) * mm, "mid": v(14.45, 3.9) * mm, "end": v(14.62, 3.94) * mm});
            skArc(sketch, "E1533", {"start": v(14.73, 4.13) * mm, "mid": v(14.68, 4.3) * mm, "end": v(14.51, 4.26) * mm});
            skLineSegment(sketch, "E1534", {"start": v(14.51, 4) * mm, "end": v(14.43, 3.8) * mm});
            skArc(sketch, "E1535", {"start": v(14.31, 3.86) * mm, "mid": v(14.38, 3.7) * mm, "end": v(14.54, 3.76) * mm});
            skArc(sketch, "E1536", {"start": v(14.63, 3.96) * mm, "mid": v(14.56, 4.12) * mm, "end": v(14.4, 4.06) * mm});
            skLineSegment(sketch, "E1537", {"start": v(14.43, 3.8) * mm, "end": v(14.36, 3.6) * mm});
            skArc(sketch, "E1538", {"start": v(14.24, 3.64) * mm, "mid": v(14.32, 3.48) * mm, "end": v(14.48, 3.56) * mm});
            skArc(sketch, "E1539", {"start": v(14.54, 3.77) * mm, "mid": v(14.47, 3.93) * mm, "end": v(14.3, 3.85) * mm});
            skLineSegment(sketch, "E1540", {"start": v(14.36, 3.6) * mm, "end": v(14.3, 3.4) * mm});
            skArc(sketch, "E1541", {"start": v(14.19, 3.42) * mm, "mid": v(14.28, 3.27) * mm, "end": v(14.43, 3.36) * mm});
            skArc(sketch, "E1542", {"start": v(14.48, 3.57) * mm, "mid": v(14.39, 3.72) * mm, "end": v(14.24, 3.63) * mm});
            skLineSegment(sketch, "E1543", {"start": v(14.3, 3.4) * mm, "end": v(14.28, 3.18) * mm});
            skArc(sketch, "E1544", {"start": v(14.16, 3.2) * mm, "mid": v(14.26, 3.05) * mm, "end": v(14.4, 3.16) * mm});
            skArc(sketch, "E1545", {"start": v(14.43, 3.38) * mm, "mid": v(14.32, 3.52) * mm, "end": v(14.18, 3.4) * mm});
            skLineSegment(sketch, "E1546", {"start": v(14.28, 3.18) * mm, "end": v(14.27, 2.95) * mm});
            skArc(sketch, "E1547", {"start": v(14.15, 2.96) * mm, "mid": v(14.27, 2.83) * mm, "end": v(14.4, 2.95) * mm});
            skArc(sketch, "E1548", {"start": v(14.4, 3.17) * mm, "mid": v(14.28, 3.3) * mm, "end": v(14.16, 3.18) * mm});
            skLineSegment(sketch, "E1549", {"start": v(14.27, 2.95) * mm, "end": v(14.29, 2.73) * mm});
            skArc(sketch, "E1550", {"start": v(14.16, 2.72) * mm, "mid": v(14.3, 2.6) * mm, "end": v(14.41, 2.74) * mm});
            skArc(sketch, "E1551", {"start": v(14.4, 2.96) * mm, "mid": v(14.27, 3.08) * mm, "end": v(14.15, 2.95) * mm});
            skLineSegment(sketch, "E1552", {"start": v(14.29, 2.73) * mm, "end": v(14.33, 2.5) * mm});
            skArc(sketch, "E1553", {"start": v(14.2, 2.49) * mm, "mid": v(14.35, 2.39) * mm, "end": v(14.45, 2.53) * mm});
            skArc(sketch, "E1554", {"start": v(14.41, 2.75) * mm, "mid": v(14.27, 2.86) * mm, "end": v(14.17, 2.71) * mm});
            skLineSegment(sketch, "E1555", {"start": v(14.33, 2.5) * mm, "end": v(14.38, 2.3) * mm});
            skArc(sketch, "E1556", {"start": v(14.26, 2.27) * mm, "mid": v(14.42, 2.18) * mm, "end": v(14.5, 2.33) * mm});
            skArc(sketch, "E1557", {"start": v(14.45, 2.54) * mm, "mid": v(14.3, 2.63) * mm, "end": v(14.2, 2.48) * mm});
            skLineSegment(sketch, "E1558", {"start": v(14.38, 2.3) * mm, "end": v(14.47, 2.07) * mm});
            skArc(sketch, "E1559", {"start": v(14.35, 2.03) * mm, "mid": v(14.52, 1.96) * mm, "end": v(14.59, 2.12) * mm});
            skArc(sketch, "E1560", {"start": v(14.5, 2.35) * mm, "mid": v(14.34, 2.42) * mm, "end": v(14.27, 2.26) * mm});
            skLineSegment(sketch, "E1561", {"start": v(14.47, 2.07) * mm, "end": v(14.57, 1.87) * mm});
            skArc(sketch, "E1562", {"start": v(14.46, 1.81) * mm, "mid": v(14.63, 1.76) * mm, "end": v(14.69, 1.93) * mm});
            skArc(sketch, "E1563", {"start": v(14.58, 2.13) * mm, "mid": v(14.41, 2.18) * mm, "end": v(14.36, 2.02) * mm});
            skLineSegment(sketch, "E1564", {"start": v(14.57, 1.87) * mm, "end": v(14.7, 1.68) * mm});
            skArc(sketch, "E1565", {"start": v(14.59, 1.62) * mm, "mid": v(14.76, 1.58) * mm, "end": v(14.8, 1.75) * mm});
            skArc(sketch, "E1566", {"start": v(14.68, 1.94) * mm, "mid": v(14.5, 1.98) * mm, "end": v(14.47, 1.8) * mm});
            skLineSegment(sketch, "E1567", {"start": v(14.7, 1.68) * mm, "end": v(14.83, 1.51) * mm});
            skArc(sketch, "E1568", {"start": v(14.73, 1.43) * mm, "mid": v(14.9, 1.41) * mm, "end": v(14.93, 1.6) * mm});
            skArc(sketch, "E1569", {"start": v(14.8, 1.76) * mm, "mid": v(14.62, 1.78) * mm, "end": v(14.6, 1.6) * mm});
            skLineSegment(sketch, "E1570", {"start": v(14.83, 1.51) * mm, "end": v(14.98, 1.36) * mm});
            skArc(sketch, "E1571", {"start": v(14.9, 1.27) * mm, "mid": v(15.07, 1.27) * mm, "end": v(15.07, 1.44) * mm});
            skArc(sketch, "E1572", {"start": v(14.92, 1.6) * mm, "mid": v(14.74, 1.6) * mm, "end": v(14.74, 1.43) * mm});
            skLineSegment(sketch, "E1573", {"start": v(14.98, 1.36) * mm, "end": v(15.15, 1.21) * mm});
            skArc(sketch, "E1574", {"start": v(15.07, 1.12) * mm, "mid": v(15.24, 1.13) * mm, "end": v(15.23, 1.3) * mm});
            skArc(sketch, "E1575", {"start": v(15.06, 1.45) * mm, "mid": v(14.89, 1.44) * mm, "end": v(14.9, 1.26) * mm});
            skLineSegment(sketch, "E1576", {"start": v(15.15, 1.21) * mm, "end": v(15.33, 1.1) * mm});
            skArc(sketch, "E1577", {"start": v(15.25, 0.99) * mm, "mid": v(15.43, 1.02) * mm, "end": v(15.4, 1.2) * mm});
            skArc(sketch, "E1578", {"start": v(15.22, 1.32) * mm, "mid": v(15.05, 1.29) * mm, "end": v(15.08, 1.11) * mm});
            skLineSegment(sketch, "E1579", {"start": v(15.33, 1.1) * mm, "end": v(15.51, 0.98) * mm});
            skArc(sketch, "E1580", {"start": v(15.45, 0.88) * mm, "mid": v(15.62, 0.92) * mm, "end": v(15.57, 1.1) * mm});
            skArc(sketch, "E1581", {"start": v(15.39, 1.2) * mm, "mid": v(15.22, 1.15) * mm, "end": v(15.26, 0.98) * mm});
            skLineSegment(sketch, "E1582", {"start": v(15.51, 0.98) * mm, "end": v(15.71, 0.9) * mm});
            skArc(sketch, "E1583", {"start": v(15.66, 0.78) * mm, "mid": v(15.83, 0.85) * mm, "end": v(15.76, 1.01) * mm});
            skArc(sketch, "E1584", {"start": v(15.56, 1.1) * mm, "mid": v(15.4, 1.04) * mm, "end": v(15.46, 0.87) * mm});
            skLineSegment(sketch, "E1585", {"start": v(15.71, 0.9) * mm, "end": v(15.92, 0.83) * mm});
            skArc(sketch, "E1586", {"start": v(15.88, 0.7) * mm, "mid": v(16.03, 0.79) * mm, "end": v(15.96, 0.95) * mm});
            skArc(sketch, "E1587", {"start": v(15.75, 1.02) * mm, "mid": v(15.6, 0.94) * mm, "end": v(15.67, 0.78) * mm});
            skLineSegment(sketch, "E1588", {"start": v(15.92, 0.83) * mm, "end": v(16.13, 0.78) * mm});
            skArc(sketch, "E1589", {"start": v(16.1, 0.66) * mm, "mid": v(16.25, 0.75) * mm, "end": v(16.16, 0.9) * mm});
            skArc(sketch, "E1590", {"start": v(15.94, 0.95) * mm, "mid": v(15.8, 0.86) * mm, "end": v(15.89, 0.7) * mm});
            skLineSegment(sketch, "E1591", {"start": v(16.13, 0.78) * mm, "end": v(16.34, 0.75) * mm});
            skArc(sketch, "E1592", {"start": v(16.33, 0.63) * mm, "mid": v(16.47, 0.74) * mm, "end": v(16.36, 0.88) * mm});
            skArc(sketch, "E1593", {"start": v(16.14, 0.9) * mm, "mid": v(16, 0.8) * mm, "end": v(16.11, 0.66) * mm});
            skLineSegment(sketch, "E1594", {"start": v(16.34, 0.75) * mm, "end": v(16.56, 0.74) * mm});
            skArc(sketch, "E1595", {"start": v(16.56, 0.62) * mm, "mid": v(16.69, 0.74) * mm, "end": v(16.57, 0.87) * mm});
            skArc(sketch, "E1596", {"start": v(16.35, 0.88) * mm, "mid": v(16.22, 0.76) * mm, "end": v(16.34, 0.63) * mm});
            skLineSegment(sketch, "E1597", {"start": v(16.56, 0.74) * mm, "end": v(16.79, 0.76) * mm});
            skArc(sketch, "E1598", {"start": v(16.8, 0.63) * mm, "mid": v(16.91, 0.77) * mm, "end": v(16.78, 0.88) * mm});
            skArc(sketch, "E1599", {"start": v(16.56, 0.87) * mm, "mid": v(16.44, 0.74) * mm, "end": v(16.57, 0.62) * mm});
            skLineSegment(sketch, "E1600", {"start": v(16.79, 0.76) * mm, "end": v(17, 0.8) * mm});
            skArc(sketch, "E1601", {"start": v(17.03, 0.67) * mm, "mid": v(17.13, 0.82) * mm, "end": v(16.99, 0.92) * mm});
            skArc(sketch, "E1602", {"start": v(16.77, 0.88) * mm, "mid": v(16.66, 0.74) * mm, "end": v(16.8, 0.64) * mm});
            skLineSegment(sketch, "E1603", {"start": v(17, 0.8) * mm, "end": v(17.25, 0.86) * mm});
            skArc(sketch, "E1604", {"start": v(17.28, 0.74) * mm, "mid": v(17.37, 0.9) * mm, "end": v(17.22, 0.98) * mm});
            skArc(sketch, "E1605", {"start": v(16.98, 0.92) * mm, "mid": v(16.89, 0.76) * mm, "end": v(17.04, 0.68) * mm});
            skLineSegment(sketch, "E1606", {"start": v(17.25, 0.86) * mm, "end": v(20.41, 1.9) * mm});
            skArc(sketch, "E1607", {"start": v(20.45, 1.77) * mm, "mid": v(20.53, 1.93) * mm, "end": v(20.38, 2.01) * mm});
            skArc(sketch, "E1608", {"start": v(17.2, 0.98) * mm, "mid": v(17.13, 0.82) * mm, "end": v(17.29, 0.74) * mm});
            skLineSegment(sketch, "E1609", {"start": v(20.41, 1.9) * mm, "end": v(22.3, 3.26) * mm});
            skArc(sketch, "E1610", {"start": v(22.37, 3.16) * mm, "mid": v(22.4, 3.34) * mm, "end": v(22.23, 3.36) * mm});
            skArc(sketch, "E1611", {"start": v(20.34, 2) * mm, "mid": v(20.31, 1.82) * mm, "end": v(20.49, 1.8) * mm});
            skLineSegment(sketch, "E1612", {"start": v(22.3, 3.26) * mm, "end": v(22.96, 4.08) * mm});
            skArc(sketch, "E1613", {"start": v(23.06, 4) * mm, "mid": v(23.04, 4.18) * mm, "end": v(22.87, 4.16) * mm});
            skArc(sketch, "E1614", {"start": v(22.2, 3.34) * mm, "mid": v(22.22, 3.17) * mm, "end": v(22.4, 3.18) * mm});
            skLineSegment(sketch, "E1615", {"start": v(22.96, 4.08) * mm, "end": v(22.38, 5.9) * mm});
            skArc(sketch, "E1616", {"start": v(22.5, 5.94) * mm, "mid": v(22.34, 6.02) * mm, "end": v(22.26, 5.86) * mm});
            skArc(sketch, "E1617", {"start": v(22.85, 4.05) * mm, "mid": v(23, 3.97) * mm, "end": v(23.08, 4.12) * mm});
            skLineSegment(sketch, "E1618", {"start": v(22.38, 5.9) * mm, "end": v(21.35, 6.17) * mm});
            skArc(sketch, "E1619", {"start": v(21.39, 6.3) * mm, "mid": v(21.23, 6.2) * mm, "end": v(21.32, 6.05) * mm});
            skArc(sketch, "E1620", {"start": v(22.34, 5.78) * mm, "mid": v(22.5, 5.86) * mm, "end": v(22.4, 6.02) * mm});
            skLineSegment(sketch, "E1621", {"start": v(21.35, 6.17) * mm, "end": v(19.02, 6.17) * mm});
            skArc(sketch, "E1622", {"start": v(19.02, 6.3) * mm, "mid": v(18.9, 6.17) * mm, "end": v(19.02, 6.05) * mm});
            skArc(sketch, "E1623", {"start": v(21.35, 6.05) * mm, "mid": v(21.48, 6.17) * mm, "end": v(21.35, 6.3) * mm});
            skLineSegment(sketch, "E1624", {"start": v(14.3, 3.36) * mm, "end": v(14.94, 1.4) * mm});
            skArc(sketch, "E1625", {"start": v(14.82, 1.36) * mm, "mid": v(14.98, 1.28) * mm, "end": v(15.06, 1.44) * mm});
            skArc(sketch, "E1626", {"start": v(14.42, 3.4) * mm, "mid": v(14.27, 3.48) * mm, "end": v(14.19, 3.32) * mm});
            skLineSegment(sketch, "E1627", {"start": v(14.58, 4.12) * mm, "end": v(15.62, 0.94) * mm});
            skArc(sketch, "E1628", {"start": v(15.5, 0.9) * mm, "mid": v(15.65, 0.82) * mm, "end": v(15.73, 0.98) * mm});
            skArc(sketch, "E1629", {"start": v(14.7, 4.16) * mm, "mid": v(14.54, 4.24) * mm, "end": v(14.46, 4.09) * mm});
            skLineSegment(sketch, "E1630", {"start": v(14.95, 4.6) * mm, "end": v(16.2, 0.77) * mm});
            skArc(sketch, "E1631", {"start": v(16.08, 0.73) * mm, "mid": v(16.23, 0.65) * mm, "end": v(16.32, 0.8) * mm});
            skArc(sketch, "E1632", {"start": v(15.07, 4.64) * mm, "mid": v(14.91, 4.72) * mm, "end": v(14.83, 4.56) * mm});
            skLineSegment(sketch, "E1633", {"start": v(15.37, 4.93) * mm, "end": v(16.73, 0.76) * mm});
            skArc(sketch, "E1634", {"start": v(16.6, 0.72) * mm, "mid": v(16.77, 0.64) * mm, "end": v(16.85, 0.8) * mm});
            skArc(sketch, "E1635", {"start": v(15.5, 4.97) * mm, "mid": v(15.33, 5.05) * mm, "end": v(15.25, 4.89) * mm});
            skLineSegment(sketch, "E1636", {"start": v(15.83, 5.12) * mm, "end": v(17.22, 0.86) * mm});
            skArc(sketch, "E1637", {"start": v(17.1, 0.82) * mm, "mid": v(17.26, 0.74) * mm, "end": v(17.34, 0.9) * mm});
            skArc(sketch, "E1638", {"start": v(15.95, 5.16) * mm, "mid": v(15.8, 5.24) * mm, "end": v(15.71, 5.09) * mm});
            skLineSegment(sketch, "E1639", {"start": v(16.3, 5.28) * mm, "end": v(17.7, 1) * mm});
            skArc(sketch, "E1640", {"start": v(17.58, 0.97) * mm, "mid": v(17.73, 0.89) * mm, "end": v(17.81, 1.05) * mm});
            skArc(sketch, "E1641", {"start": v(16.43, 5.32) * mm, "mid": v(16.27, 5.4) * mm, "end": v(16.19, 5.24) * mm});
            skLineSegment(sketch, "E1642", {"start": v(16.78, 5.44) * mm, "end": v(18.17, 1.16) * mm});
            skArc(sketch, "E1643", {"start": v(18.05, 1.12) * mm, "mid": v(18.21, 1.04) * mm, "end": v(18.3, 1.2) * mm});
            skArc(sketch, "E1644", {"start": v(16.9, 5.47) * mm, "mid": v(16.74, 5.55) * mm, "end": v(16.66, 5.4) * mm});
            skLineSegment(sketch, "E1645", {"start": v(17.26, 5.6) * mm, "end": v(18.65, 1.32) * mm});
            skArc(sketch, "E1646", {"start": v(18.53, 1.28) * mm, "mid": v(18.69, 1.2) * mm, "end": v(18.77, 1.36) * mm});
            skArc(sketch, "E1647", {"start": v(17.38, 5.63) * mm, "mid": v(17.22, 5.71) * mm, "end": v(17.14, 5.55) * mm});
            skLineSegment(sketch, "E1648", {"start": v(17.73, 5.75) * mm, "end": v(19.12, 1.47) * mm});
            skArc(sketch, "E1649", {"start": v(19, 1.43) * mm, "mid": v(19.16, 1.35) * mm, "end": v(19.24, 1.51) * mm});
            skArc(sketch, "E1650", {"start": v(17.85, 5.79) * mm, "mid": v(17.7, 5.87) * mm, "end": v(17.61, 5.7) * mm});
            skLineSegment(sketch, "E1651", {"start": v(18.2, 5.9) * mm, "end": v(19.6, 1.63) * mm});
            skArc(sketch, "E1652", {"start": v(19.48, 1.59) * mm, "mid": v(19.64, 1.5) * mm, "end": v(19.72, 1.67) * mm});
            skArc(sketch, "E1653", {"start": v(18.33, 5.94) * mm, "mid": v(18.17, 6.02) * mm, "end": v(18.09, 5.87) * mm});
            skLineSegment(sketch, "E1654", {"start": v(18.68, 6.06) * mm, "end": v(20.07, 1.78) * mm});
            skArc(sketch, "E1655", {"start": v(19.95, 1.74) * mm, "mid": v(20.11, 1.66) * mm, "end": v(20.2, 1.82) * mm});
            skArc(sketch, "E1656", {"start": v(18.8, 6.1) * mm, "mid": v(18.64, 6.18) * mm, "end": v(18.56, 6.02) * mm});
            skLineSegment(sketch, "E1657", {"start": v(19.17, 6.17) * mm, "end": v(20.53, 1.98) * mm});
            skArc(sketch, "E1658", {"start": v(20.42, 1.94) * mm, "mid": v(20.57, 1.86) * mm, "end": v(20.65, 2.02) * mm});
            skArc(sketch, "E1659", {"start": v(19.3, 6.21) * mm, "mid": v(19.13, 6.3) * mm, "end": v(19.05, 6.13) * mm});
            skLineSegment(sketch, "E1660", {"start": v(19.7, 6.17) * mm, "end": v(20.96, 2.29) * mm});
            skArc(sketch, "E1661", {"start": v(20.84, 2.25) * mm, "mid": v(21, 2.17) * mm, "end": v(21.08, 2.33) * mm});
            skArc(sketch, "E1662", {"start": v(19.82, 6.21) * mm, "mid": v(19.66, 6.3) * mm, "end": v(19.58, 6.13) * mm});
            skLineSegment(sketch, "E1663", {"start": v(20.22, 6.17) * mm, "end": v(21.39, 2.6) * mm});
            skArc(sketch, "E1664", {"start": v(21.27, 2.56) * mm, "mid": v(21.42, 2.48) * mm, "end": v(21.5, 2.64) * mm});
            skArc(sketch, "E1665", {"start": v(20.34, 6.2) * mm, "mid": v(20.19, 6.3) * mm, "end": v(20.1, 6.13) * mm});
            skLineSegment(sketch, "E1666", {"start": v(20.75, 6.17) * mm, "end": v(21.81, 2.9) * mm});
            skArc(sketch, "E1667", {"start": v(21.7, 2.87) * mm, "mid": v(21.85, 2.79) * mm, "end": v(21.93, 2.95) * mm});
            skArc(sketch, "E1668", {"start": v(20.87, 6.2) * mm, "mid": v(20.71, 6.29) * mm, "end": v(20.63, 6.13) * mm});
            skLineSegment(sketch, "E1669", {"start": v(21.28, 6.17) * mm, "end": v(22.24, 3.22) * mm});
            skArc(sketch, "E1670", {"start": v(22.12, 3.18) * mm, "mid": v(22.27, 3.1) * mm, "end": v(22.35, 3.26) * mm});
            skArc(sketch, "E1671", {"start": v(21.4, 6.2) * mm, "mid": v(21.24, 6.29) * mm, "end": v(21.16, 6.13) * mm});
            skLineSegment(sketch, "E1672", {"start": v(21.84, 6.04) * mm, "end": v(22.62, 3.66) * mm});
            skArc(sketch, "E1673", {"start": v(22.5, 3.62) * mm, "mid": v(22.66, 3.54) * mm, "end": v(22.74, 3.7) * mm});
            skArc(sketch, "E1674", {"start": v(21.96, 6.08) * mm, "mid": v(21.8, 6.16) * mm, "end": v(21.73, 6) * mm});
            skLineSegment(sketch, "E1675", {"start": v(28.51, 9.45) * mm, "end": v(28.45, 9.32) * mm});
            skArc(sketch, "E1676", {"start": v(28.4, 9.35) * mm, "mid": v(28.43, 9.28) * mm, "end": v(28.5, 9.3) * mm});
            skArc(sketch, "E1677", {"start": v(28.56, 9.43) * mm, "mid": v(28.53, 9.5) * mm, "end": v(28.47, 9.47) * mm});
            skLineSegment(sketch, "E1678", {"start": v(28.45, 9.32) * mm, "end": v(28.4, 9.18) * mm});
            skArc(sketch, "E1679", {"start": v(28.36, 9.19) * mm, "mid": v(28.39, 9.13) * mm, "end": v(28.45, 9.16) * mm});
            skArc(sketch, "E1680", {"start": v(28.5, 9.3) * mm, "mid": v(28.46, 9.37) * mm, "end": v(28.4, 9.34) * mm});
            skLineSegment(sketch, "E1681", {"start": v(28.4, 9.18) * mm, "end": v(28.38, 9.02) * mm});
            skArc(sketch, "E1682", {"start": v(28.33, 9.03) * mm, "mid": v(28.38, 8.97) * mm, "end": v(28.43, 9.01) * mm});
            skArc(sketch, "E1683", {"start": v(28.45, 9.17) * mm, "mid": v(28.4, 9.22) * mm, "end": v(28.35, 9.18) * mm});
            skLineSegment(sketch, "E1684", {"start": v(28.38, 9.02) * mm, "end": v(28.4, 8.86) * mm});
            skArc(sketch, "E1685", {"start": v(28.34, 8.86) * mm, "mid": v(28.4, 8.81) * mm, "end": v(28.44, 8.86) * mm});
            skArc(sketch, "E1686", {"start": v(28.43, 9.02) * mm, "mid": v(28.38, 9.07) * mm, "end": v(28.33, 9.02) * mm});
            skLineSegment(sketch, "E1687", {"start": v(28.4, 8.86) * mm, "end": v(28.4, 8.78) * mm});
            skArc(sketch, "E1688", {"start": v(28.36, 8.77) * mm, "mid": v(28.42, 8.73) * mm, "end": v(28.46, 8.8) * mm});
            skArc(sketch, "E1689", {"start": v(28.44, 8.87) * mm, "mid": v(28.38, 8.91) * mm, "end": v(28.34, 8.85) * mm});
            skLineSegment(sketch, "E1690", {"start": v(28.4, 8.78) * mm, "end": v(29.58, 5.22) * mm});
            skArc(sketch, "E1691", {"start": v(29.53, 5.2) * mm, "mid": v(29.6, 5.17) * mm, "end": v(29.63, 5.23) * mm});
            skArc(sketch, "E1692", {"start": v(28.45, 8.8) * mm, "mid": v(28.4, 8.83) * mm, "end": v(28.36, 8.77) * mm});
            skLineSegment(sketch, "E1693", {"start": v(29.58, 5.22) * mm, "end": v(29.67, 5.09) * mm});
            skArc(sketch, "E1694", {"start": v(29.62, 5.06) * mm, "mid": v(29.7, 5.04) * mm, "end": v(29.7, 5.11) * mm});
            skArc(sketch, "E1695", {"start": v(29.62, 5.24) * mm, "mid": v(29.55, 5.26) * mm, "end": v(29.54, 5.19) * mm});
            skLineSegment(sketch, "E1696", {"start": v(29.67, 5.09) * mm, "end": v(29.77, 4.97) * mm});
            skArc(sketch, "E1697", {"start": v(29.74, 4.94) * mm, "mid": v(29.8, 4.94) * mm, "end": v(29.8, 5) * mm});
            skArc(sketch, "E1698", {"start": v(29.7, 5.12) * mm, "mid": v(29.63, 5.12) * mm, "end": v(29.63, 5.05) * mm});
            skLineSegment(sketch, "E1699", {"start": v(29.77, 4.97) * mm, "end": v(29.9, 4.88) * mm});
            skArc(sketch, "E1700", {"start": v(29.87, 4.84) * mm, "mid": v(29.94, 4.85) * mm, "end": v(29.93, 4.92) * mm});
            skArc(sketch, "E1701", {"start": v(29.8, 5.01) * mm, "mid": v(29.73, 5) * mm, "end": v(29.74, 4.93) * mm});
            skLineSegment(sketch, "E1702", {"start": v(29.9, 4.88) * mm, "end": v(30.01, 4.82) * mm});
            skArc(sketch, "E1703", {"start": v(30, 4.78) * mm, "mid": v(30.06, 4.8) * mm, "end": v(30.04, 4.87) * mm});
            skArc(sketch, "E1704", {"start": v(29.92, 4.93) * mm, "mid": v(29.85, 4.9) * mm, "end": v(29.87, 4.84) * mm});
            skLineSegment(sketch, "E1705", {"start": v(30.01, 4.82) * mm, "end": v(30.08, 4.95) * mm});
            skArc(sketch, "E1706", {"start": v(30.12, 4.92) * mm, "mid": v(30.1, 5) * mm, "end": v(30.03, 4.97) * mm});
            skArc(sketch, "E1707", {"start": v(29.97, 4.84) * mm, "mid": v(30, 4.78) * mm, "end": v(30.06, 4.8) * mm});
            skLineSegment(sketch, "E1708", {"start": v(30.08, 4.95) * mm, "end": v(30.12, 5.1) * mm});
            skArc(sketch, "E1709", {"start": v(30.17, 5.08) * mm, "mid": v(30.14, 5.14) * mm, "end": v(30.08, 5.11) * mm});
            skArc(sketch, "E1710", {"start": v(30.03, 4.96) * mm, "mid": v(30.06, 4.9) * mm, "end": v(30.13, 4.93) * mm});
            skLineSegment(sketch, "E1711", {"start": v(30.12, 5.1) * mm, "end": v(30.14, 5.25) * mm});
            skArc(sketch, "E1712", {"start": v(30.2, 5.24) * mm, "mid": v(30.15, 5.3) * mm, "end": v(30.1, 5.26) * mm});
            skArc(sketch, "E1713", {"start": v(30.07, 5.1) * mm, "mid": v(30.12, 5.05) * mm, "end": v(30.17, 5.09) * mm});
            skLineSegment(sketch, "E1714", {"start": v(30.14, 5.25) * mm, "end": v(30.13, 5.4) * mm});
            skArc(sketch, "E1715", {"start": v(30.18, 5.41) * mm, "mid": v(30.13, 5.46) * mm, "end": v(30.08, 5.4) * mm});
            skArc(sketch, "E1716", {"start": v(30.1, 5.25) * mm, "mid": v(30.15, 5.2) * mm, "end": v(30.2, 5.25) * mm});
            skLineSegment(sketch, "E1717", {"start": v(30.13, 5.4) * mm, "end": v(30.12, 5.49) * mm});
            skArc(sketch, "E1718", {"start": v(30.17, 5.5) * mm, "mid": v(30.11, 5.54) * mm, "end": v(30.07, 5.48) * mm});
            skArc(sketch, "E1719", {"start": v(30.09, 5.4) * mm, "mid": v(30.14, 5.36) * mm, "end": v(30.18, 5.42) * mm});
            skLineSegment(sketch, "E1720", {"start": v(30.12, 5.49) * mm, "end": v(28.95, 9.05) * mm});
            skArc(sketch, "E1721", {"start": v(29, 9.07) * mm, "mid": v(28.93, 9.1) * mm, "end": v(28.9, 9.04) * mm});
            skArc(sketch, "E1722", {"start": v(30.07, 5.47) * mm, "mid": v(30.14, 5.44) * mm, "end": v(30.17, 5.5) * mm});
            skLineSegment(sketch, "E1723", {"start": v(28.95, 9.05) * mm, "end": v(28.86, 9.19) * mm});
            skArc(sketch, "E1724", {"start": v(28.9, 9.21) * mm, "mid": v(28.83, 9.23) * mm, "end": v(28.82, 9.16) * mm});
            skArc(sketch, "E1725", {"start": v(28.9, 9.03) * mm, "mid": v(28.98, 9.01) * mm, "end": v(29, 9.08) * mm});
            skLineSegment(sketch, "E1726", {"start": v(28.86, 9.19) * mm, "end": v(28.75, 9.3) * mm});
            skArc(sketch, "E1727", {"start": v(28.79, 9.33) * mm, "mid": v(28.72, 9.33) * mm, "end": v(28.72, 9.26) * mm});
            skArc(sketch, "E1728", {"start": v(28.82, 9.15) * mm, "mid": v(28.9, 9.15) * mm, "end": v(28.9, 9.22) * mm});
            skLineSegment(sketch, "E1729", {"start": v(28.75, 9.3) * mm, "end": v(28.63, 9.39) * mm});
            skArc(sketch, "E1730", {"start": v(28.66, 9.43) * mm, "mid": v(28.59, 9.42) * mm, "end": v(28.6, 9.35) * mm});
            skArc(sketch, "E1731", {"start": v(28.72, 9.26) * mm, "mid": v(28.8, 9.27) * mm, "end": v(28.78, 9.34) * mm});
            skLineSegment(sketch, "E1732", {"start": v(28.63, 9.39) * mm, "end": v(28.51, 9.45) * mm});
            skArc(sketch, "E1733", {"start": v(28.53, 9.5) * mm, "mid": v(28.47, 9.47) * mm, "end": v(28.49, 9.4) * mm});
            skArc(sketch, "E1734", {"start": v(28.6, 9.35) * mm, "mid": v(28.67, 9.37) * mm, "end": v(28.65, 9.43) * mm});
            skLineSegment(sketch, "E1735", {"start": v(28.4, 9.16) * mm, "end": v(29.76, 5) * mm});
            skArc(sketch, "E1736", {"start": v(29.7, 4.98) * mm, "mid": v(29.77, 4.94) * mm, "end": v(29.8, 5) * mm});
            skArc(sketch, "E1737", {"start": v(28.45, 9.18) * mm, "mid": v(28.39, 9.2) * mm, "end": v(28.35, 9.14) * mm});
            skLineSegment(sketch, "E1738", {"start": v(28.52, 9.45) * mm, "end": v(30.02, 4.83) * mm});
            skArc(sketch, "E1739", {"start": v(29.97, 4.81) * mm, "mid": v(30.03, 4.78) * mm, "end": v(30.07, 4.84) * mm});
            skArc(sketch, "E1740", {"start": v(28.57, 9.46) * mm, "mid": v(28.5, 9.5) * mm, "end": v(28.47, 9.43) * mm});
            skLineSegment(sketch, "E1741", {"start": v(28.79, 9.26) * mm, "end": v(30.13, 5.14) * mm});
            skArc(sketch, "E1742", {"start": v(30.08, 5.12) * mm, "mid": v(30.14, 5.09) * mm, "end": v(30.18, 5.15) * mm});
            skArc(sketch, "E1743", {"start": v(28.84, 9.28) * mm, "mid": v(28.77, 9.3) * mm, "end": v(28.74, 9.25) * mm});
            skCircle(sketch, "E1744", {"center": v(16.52, 3) * mm, "radius": 1.7 * mm});
            skArc(sketch, "E1745", {"start": v(16.52, 2.12) * mm, "mid": v(17.4, 3) * mm, "end": v(16.52, 3.87) * mm});
            skArc(sketch, "E1746", {"start": v(16.52, 3.87) * mm, "mid": v(15.65, 3) * mm, "end": v(16.52, 2.12) * mm});
            skCircle(sketch, "E1747", {"center": v(26.03, 6.09) * mm, "radius": 1.7 * mm});
            skArc(sketch, "E1748", {"start": v(26.03, 5.21) * mm, "mid": v(26.91, 6.09) * mm, "end": v(26.03, 6.96) * mm});
            skArc(sketch, "E1749", {"start": v(26.03, 6.96) * mm, "mid": v(25.16, 6.09) * mm, "end": v(26.03, 5.21) * mm});
            skLineSegment(sketch, "E1750", {"start": v(14.01, -17.8) * mm, "end": v(11.89, -14.9) * mm});
            skArc(sketch, "E1751", {"start": v(11.99, -14.83) * mm, "mid": v(11.81, -14.8) * mm, "end": v(11.79, -14.97) * mm});
            skArc(sketch, "E1752", {"start": v(13.91, -17.88) * mm, "mid": v(14.09, -17.9) * mm, "end": v(14.12, -17.73) * mm});
            skLineSegment(sketch, "E1753", {"start": v(11.89, -14.9) * mm, "end": v(11.73, -14.74) * mm});
            skArc(sketch, "E1754", {"start": v(11.82, -14.65) * mm, "mid": v(11.64, -14.65) * mm, "end": v(11.64, -14.83) * mm});
            skArc(sketch, "E1755", {"start": v(11.8, -14.99) * mm, "mid": v(11.98, -14.99) * mm, "end": v(11.98, -14.81) * mm});
            skLineSegment(sketch, "E1756", {"start": v(11.73, -14.74) * mm, "end": v(11.56, -14.6) * mm});
            skArc(sketch, "E1757", {"start": v(11.64, -14.5) * mm, "mid": v(11.46, -14.52) * mm, "end": v(11.48, -14.7) * mm});
            skArc(sketch, "E1758", {"start": v(11.65, -14.84) * mm, "mid": v(11.83, -14.82) * mm, "end": v(11.8, -14.64) * mm});
            skLineSegment(sketch, "E1759", {"start": v(11.56, -14.6) * mm, "end": v(11.37, -14.48) * mm});
            skArc(sketch, "E1760", {"start": v(11.44, -14.37) * mm, "mid": v(11.27, -14.4) * mm, "end": v(11.3, -14.58) * mm});
            skArc(sketch, "E1761", {"start": v(11.49, -14.7) * mm, "mid": v(11.66, -14.67) * mm, "end": v(11.63, -14.5) * mm});
            skLineSegment(sketch, "E1762", {"start": v(11.37, -14.48) * mm, "end": v(11.18, -14.38) * mm});
            skArc(sketch, "E1763", {"start": v(11.24, -14.27) * mm, "mid": v(11.07, -14.32) * mm, "end": v(11.12, -14.49) * mm});
            skArc(sketch, "E1764", {"start": v(11.31, -14.59) * mm, "mid": v(11.48, -14.54) * mm, "end": v(11.43, -14.37) * mm});
            skLineSegment(sketch, "E1765", {"start": v(11.18, -14.38) * mm, "end": v(10.98, -14.3) * mm});
            skArc(sketch, "E1766", {"start": v(11.03, -14.18) * mm, "mid": v(10.86, -14.25) * mm, "end": v(10.93, -14.4) * mm});
            skArc(sketch, "E1767", {"start": v(11.13, -14.5) * mm, "mid": v(11.3, -14.42) * mm, "end": v(11.23, -14.26) * mm});
            skLineSegment(sketch, "E1768", {"start": v(10.98, -14.3) * mm, "end": v(10.77, -14.23) * mm});
            skArc(sketch, "E1769", {"start": v(10.8, -14.11) * mm, "mid": v(10.65, -14.2) * mm, "end": v(10.74, -14.35) * mm});
            skArc(sketch, "E1770", {"start": v(10.94, -14.41) * mm, "mid": v(11.1, -14.33) * mm, "end": v(11.02, -14.17) * mm});
            skLineSegment(sketch, "E1771", {"start": v(10.77, -14.23) * mm, "end": v(10.56, -14.19) * mm});
            skArc(sketch, "E1772", {"start": v(10.59, -14.06) * mm, "mid": v(10.44, -14.16) * mm, "end": v(10.54, -14.3) * mm});
            skArc(sketch, "E1773", {"start": v(10.75, -14.35) * mm, "mid": v(10.9, -14.25) * mm, "end": v(10.8, -14.1) * mm});
            skLineSegment(sketch, "E1774", {"start": v(10.56, -14.19) * mm, "end": v(10.35, -14.16) * mm});
            skArc(sketch, "E1775", {"start": v(10.36, -14.04) * mm, "mid": v(10.22, -14.15) * mm, "end": v(10.33, -14.29) * mm});
            skArc(sketch, "E1776", {"start": v(10.55, -14.31) * mm, "mid": v(10.69, -14.2) * mm, "end": v(10.57, -14.06) * mm});
            skLineSegment(sketch, "E1777", {"start": v(10.35, -14.16) * mm, "end": v(10.13, -14.16) * mm});
            skArc(sketch, "E1778", {"start": v(10.13, -14.04) * mm, "mid": v(10, -14.16) * mm, "end": v(10.13, -14.29) * mm});
            skArc(sketch, "E1779", {"start": v(10.35, -14.29) * mm, "mid": v(10.47, -14.17) * mm, "end": v(10.35, -14.04) * mm});
            skLineSegment(sketch, "E1780", {"start": v(10.13, -14.16) * mm, "end": v(9.91, -14.18) * mm});
            skArc(sketch, "E1781", {"start": v(9.9, -14.06) * mm, "mid": v(9.79, -14.2) * mm, "end": v(9.92, -14.3) * mm});
            skArc(sketch, "E1782", {"start": v(10.14, -14.29) * mm, "mid": v(10.25, -14.15) * mm, "end": v(10.12, -14.04) * mm});
            skLineSegment(sketch, "E1783", {"start": v(9.91, -14.18) * mm, "end": v(9.7, -14.22) * mm});
            skArc(sketch, "E1784", {"start": v(9.68, -14.1) * mm, "mid": v(9.58, -14.25) * mm, "end": v(9.72, -14.34) * mm});
            skArc(sketch, "E1785", {"start": v(9.94, -14.3) * mm, "mid": v(10.04, -14.16) * mm, "end": v(9.9, -14.06) * mm});
            skLineSegment(sketch, "E1786", {"start": v(9.7, -14.22) * mm, "end": v(9.49, -14.28) * mm});
            skArc(sketch, "E1787", {"start": v(9.45, -14.16) * mm, "mid": v(9.37, -14.32) * mm, "end": v(9.52, -14.4) * mm});
            skArc(sketch, "E1788", {"start": v(9.73, -14.34) * mm, "mid": v(9.82, -14.19) * mm, "end": v(9.66, -14.1) * mm});
            skLineSegment(sketch, "E1789", {"start": v(9.49, -14.28) * mm, "end": v(9.28, -14.37) * mm});
            skArc(sketch, "E1790", {"start": v(9.23, -14.25) * mm, "mid": v(9.16, -14.41) * mm, "end": v(9.33, -14.48) * mm});
            skArc(sketch, "E1791", {"start": v(9.53, -14.4) * mm, "mid": v(9.6, -14.24) * mm, "end": v(9.44, -14.17) * mm});
            skLineSegment(sketch, "E1792", {"start": v(9.28, -14.37) * mm, "end": v(9.08, -14.47) * mm});
            skArc(sketch, "E1793", {"start": v(9.02, -14.36) * mm, "mid": v(8.97, -14.53) * mm, "end": v(9.14, -14.58) * mm});
            skArc(sketch, "E1794", {"start": v(9.34, -14.48) * mm, "mid": v(9.4, -14.3) * mm, "end": v(9.22, -14.26) * mm});
            skLineSegment(sketch, "E1795", {"start": v(9.08, -14.47) * mm, "end": v(8.9, -14.6) * mm});
            skArc(sketch, "E1796", {"start": v(8.83, -14.49) * mm, "mid": v(8.8, -14.66) * mm, "end": v(8.97, -14.7) * mm});
            skArc(sketch, "E1797", {"start": v(9.15, -14.58) * mm, "mid": v(9.18, -14.4) * mm, "end": v(9.01, -14.37) * mm});
            skLineSegment(sketch, "E1798", {"start": v(8.9, -14.6) * mm, "end": v(8.7, -14.74) * mm});
            skArc(sketch, "E1799", {"start": v(8.63, -14.65) * mm, "mid": v(8.61, -14.82) * mm, "end": v(8.79, -14.84) * mm});
            skArc(sketch, "E1800", {"start": v(8.98, -14.69) * mm, "mid": v(9, -14.51) * mm, "end": v(8.82, -14.5) * mm});
            skLineSegment(sketch, "E1801", {"start": v(8.7, -14.74) * mm, "end": v(8.55, -14.9) * mm});
            skArc(sketch, "E1802", {"start": v(8.46, -14.82) * mm, "mid": v(8.46, -15) * mm, "end": v(8.64, -15) * mm});
            skArc(sketch, "E1803", {"start": v(8.8, -14.83) * mm, "mid": v(8.8, -14.66) * mm, "end": v(8.62, -14.66) * mm});
            skLineSegment(sketch, "E1804", {"start": v(8.55, -14.9) * mm, "end": v(8.4, -15.08) * mm});
            skArc(sketch, "E1805", {"start": v(8.31, -15) * mm, "mid": v(8.33, -15.17) * mm, "end": v(8.5, -15.16) * mm});
            skArc(sketch, "E1806", {"start": v(8.65, -14.98) * mm, "mid": v(8.63, -14.8) * mm, "end": v(8.45, -14.82) * mm});
            skLineSegment(sketch, "E1807", {"start": v(8.4, -15.08) * mm, "end": v(8.29, -15.26) * mm});
            skArc(sketch, "E1808", {"start": v(8.18, -15.2) * mm, "mid": v(8.22, -15.36) * mm, "end": v(8.4, -15.33) * mm});
            skArc(sketch, "E1809", {"start": v(8.51, -15.15) * mm, "mid": v(8.48, -14.97) * mm, "end": v(8.3, -15) * mm});
            skLineSegment(sketch, "E1810", {"start": v(8.29, -15.26) * mm, "end": v(8.18, -15.45) * mm});
            skArc(sketch, "E1811", {"start": v(8.07, -15.4) * mm, "mid": v(8.13, -15.56) * mm, "end": v(8.3, -15.51) * mm});
            skArc(sketch, "E1812", {"start": v(8.4, -15.32) * mm, "mid": v(8.35, -15.15) * mm, "end": v(8.18, -15.2) * mm});
            skLineSegment(sketch, "E1813", {"start": v(8.18, -15.45) * mm, "end": v(8.1, -15.65) * mm});
            skArc(sketch, "E1814", {"start": v(7.99, -15.6) * mm, "mid": v(8.05, -15.77) * mm, "end": v(8.22, -15.7) * mm});
            skArc(sketch, "E1815", {"start": v(8.3, -15.5) * mm, "mid": v(8.23, -15.34) * mm, "end": v(8.07, -15.4) * mm});
            skLineSegment(sketch, "E1816", {"start": v(8.1, -15.65) * mm, "end": v(8.04, -15.86) * mm});
            skArc(sketch, "E1817", {"start": v(7.92, -15.82) * mm, "mid": v(8, -15.98) * mm, "end": v(8.16, -15.9) * mm});
            skArc(sketch, "E1818", {"start": v(8.22, -15.69) * mm, "mid": v(8.14, -15.53) * mm, "end": v(7.98, -15.62) * mm});
            skLineSegment(sketch, "E1819", {"start": v(8.04, -15.86) * mm, "end": v(8, -16.07) * mm});
            skArc(sketch, "E1820", {"start": v(7.87, -16.05) * mm, "mid": v(7.97, -16.2) * mm, "end": v(8.12, -16.1) * mm});
            skArc(sketch, "E1821", {"start": v(8.16, -15.88) * mm, "mid": v(8.06, -15.74) * mm, "end": v(7.92, -15.84) * mm});
            skLineSegment(sketch, "E1822", {"start": v(8, -16.07) * mm, "end": v(7.97, -16.29) * mm});
            skArc(sketch, "E1823", {"start": v(7.85, -16.27) * mm, "mid": v(7.96, -16.41) * mm, "end": v(8.1, -16.3) * mm});
            skArc(sketch, "E1824", {"start": v(8.12, -16.08) * mm, "mid": v(8, -15.95) * mm, "end": v(7.87, -16.06) * mm});
            skLineSegment(sketch, "E1825", {"start": v(7.97, -16.29) * mm, "end": v(7.97, -16.5) * mm});
            skArc(sketch, "E1826", {"start": v(7.85, -16.5) * mm, "mid": v(7.97, -16.63) * mm, "end": v(8.1, -16.5) * mm});
            skArc(sketch, "E1827", {"start": v(8.1, -16.29) * mm, "mid": v(7.98, -16.16) * mm, "end": v(7.85, -16.29) * mm});
            skLineSegment(sketch, "E1828", {"start": v(7.97, -16.5) * mm, "end": v(8, -16.72) * mm});
            skArc(sketch, "E1829", {"start": v(7.87, -16.73) * mm, "mid": v(8, -16.84) * mm, "end": v(8.12, -16.7) * mm});
            skArc(sketch, "E1830", {"start": v(8.1, -16.5) * mm, "mid": v(7.96, -16.38) * mm, "end": v(7.85, -16.51) * mm});
            skLineSegment(sketch, "E1831", {"start": v(8, -16.72) * mm, "end": v(8.03, -16.93) * mm});
            skArc(sketch, "E1832", {"start": v(7.9, -16.96) * mm, "mid": v(8.05, -17.06) * mm, "end": v(8.15, -16.91) * mm});
            skArc(sketch, "E1833", {"start": v(8.11, -16.7) * mm, "mid": v(7.97, -16.6) * mm, "end": v(7.87, -16.74) * mm});
            skLineSegment(sketch, "E1834", {"start": v(8.03, -16.93) * mm, "end": v(8.1, -17.15) * mm});
            skArc(sketch, "E1835", {"start": v(7.97, -17.18) * mm, "mid": v(8.13, -17.27) * mm, "end": v(8.21, -17.11) * mm});
            skArc(sketch, "E1836", {"start": v(8.15, -16.9) * mm, "mid": v(8, -16.81) * mm, "end": v(7.91, -16.97) * mm});
            skLineSegment(sketch, "E1837", {"start": v(8.1, -17.15) * mm, "end": v(8.18, -17.35) * mm});
            skArc(sketch, "E1838", {"start": v(8.06, -17.4) * mm, "mid": v(8.22, -17.47) * mm, "end": v(8.3, -17.3) * mm});
            skArc(sketch, "E1839", {"start": v(8.2, -17.1) * mm, "mid": v(8.05, -17.03) * mm, "end": v(7.98, -17.2) * mm});
            skLineSegment(sketch, "E1840", {"start": v(8.18, -17.35) * mm, "end": v(8.28, -17.55) * mm});
            skArc(sketch, "E1841", {"start": v(8.17, -17.6) * mm, "mid": v(8.34, -17.66) * mm, "end": v(8.4, -17.5) * mm});
            skArc(sketch, "E1842", {"start": v(8.29, -17.3) * mm, "mid": v(8.12, -17.24) * mm, "end": v(8.06, -17.4) * mm});
            skLineSegment(sketch, "E1843", {"start": v(8.28, -17.55) * mm, "end": v(8.42, -17.76) * mm});
            skArc(sketch, "E1844", {"start": v(8.31, -17.83) * mm, "mid": v(8.49, -17.86) * mm, "end": v(8.52, -17.7) * mm});
            skArc(sketch, "E1845", {"start": v(8.38, -17.48) * mm, "mid": v(8.21, -17.45) * mm, "end": v(8.18, -17.62) * mm});
            skLineSegment(sketch, "E1846", {"start": v(8.42, -17.76) * mm, "end": v(10.37, -20.45) * mm});
            skArc(sketch, "E1847", {"start": v(10.27, -20.53) * mm, "mid": v(10.45, -20.55) * mm, "end": v(10.48, -20.38) * mm});
            skArc(sketch, "E1848", {"start": v(8.52, -17.69) * mm, "mid": v(8.34, -17.66) * mm, "end": v(8.32, -17.83) * mm});
            skLineSegment(sketch, "E1849", {"start": v(10.37, -20.45) * mm, "end": v(12.26, -21.82) * mm});
            skArc(sketch, "E1850", {"start": v(12.19, -21.92) * mm, "mid": v(12.36, -21.9) * mm, "end": v(12.33, -21.72) * mm});
            skArc(sketch, "E1851", {"start": v(10.45, -20.35) * mm, "mid": v(10.27, -20.38) * mm, "end": v(10.3, -20.55) * mm});
            skLineSegment(sketch, "E1852", {"start": v(12.26, -21.82) * mm, "end": v(13.25, -22.2) * mm});
            skArc(sketch, "E1853", {"start": v(13.2, -22.32) * mm, "mid": v(13.36, -22.24) * mm, "end": v(13.3, -22.08) * mm});
            skArc(sketch, "E1854", {"start": v(12.3, -21.7) * mm, "mid": v(12.14, -21.78) * mm, "end": v(12.22, -21.94) * mm});
            skLineSegment(sketch, "E1855", {"start": v(13.25, -22.2) * mm, "end": v(14.79, -21.08) * mm});
            skArc(sketch, "E1856", {"start": v(14.86, -21.18) * mm, "mid": v(14.89, -21) * mm, "end": v(14.72, -20.98) * mm});
            skArc(sketch, "E1857", {"start": v(13.17, -22.1) * mm, "mid": v(13.15, -22.27) * mm, "end": v(13.32, -22.3) * mm});
            skLineSegment(sketch, "E1858", {"start": v(14.79, -21.08) * mm, "end": v(14.73, -20.02) * mm});
            skArc(sketch, "E1859", {"start": v(14.86, -20.02) * mm, "mid": v(14.73, -19.9) * mm, "end": v(14.6, -20.03) * mm});
            skArc(sketch, "E1860", {"start": v(14.66, -21.09) * mm, "mid": v(14.8, -21.2) * mm, "end": v(14.91, -21.07) * mm});
            skLineSegment(sketch, "E1861", {"start": v(14.73, -20.02) * mm, "end": v(14.01, -17.8) * mm});
            skArc(sketch, "E1862", {"start": v(14.13, -17.77) * mm, "mid": v(13.98, -17.69) * mm, "end": v(13.9, -17.85) * mm});
            skArc(sketch, "E1863", {"start": v(14.61, -20.06) * mm, "mid": v(14.77, -20.14) * mm, "end": v(14.85, -19.99) * mm});
            skLineSegment(sketch, "E1864", {"start": v(9.88, -14.19) * mm, "end": v(8.21, -15.4) * mm});
            skArc(sketch, "E1865", {"start": v(8.14, -15.3) * mm, "mid": v(8.11, -15.47) * mm, "end": v(8.29, -15.5) * mm});
            skArc(sketch, "E1866", {"start": v(9.95, -14.29) * mm, "mid": v(9.98, -14.11) * mm, "end": v(9.8, -14.09) * mm});
            skLineSegment(sketch, "E1867", {"start": v(10.7, -14.21) * mm, "end": v(7.98, -16.18) * mm});
            skArc(sketch, "E1868", {"start": v(7.91, -16.08) * mm, "mid": v(7.88, -16.26) * mm, "end": v(8.06, -16.28) * mm});
            skArc(sketch, "E1869", {"start": v(10.77, -14.32) * mm, "mid": v(10.8, -14.14) * mm, "end": v(10.62, -14.11) * mm});
            skLineSegment(sketch, "E1870", {"start": v(11.26, -14.42) * mm, "end": v(8, -16.79) * mm});
            skArc(sketch, "E1871", {"start": v(7.93, -16.69) * mm, "mid": v(7.9, -16.86) * mm, "end": v(8.08, -16.89) * mm});
            skArc(sketch, "E1872", {"start": v(11.34, -14.52) * mm, "mid": v(11.36, -14.35) * mm, "end": v(11.19, -14.32) * mm});
            skLineSegment(sketch, "E1873", {"start": v(11.7, -14.72) * mm, "end": v(8.15, -17.3) * mm});
            skArc(sketch, "E1874", {"start": v(8.08, -17.2) * mm, "mid": v(8.05, -17.37) * mm, "end": v(8.23, -17.4) * mm});
            skArc(sketch, "E1875", {"start": v(11.77, -14.82) * mm, "mid": v(11.8, -14.64) * mm, "end": v(11.63, -14.62) * mm});
            skLineSegment(sketch, "E1876", {"start": v(12.03, -15.1) * mm, "end": v(8.4, -17.73) * mm});
            skArc(sketch, "E1877", {"start": v(8.33, -17.63) * mm, "mid": v(8.3, -17.8) * mm, "end": v(8.47, -17.84) * mm});
            skArc(sketch, "E1878", {"start": v(12.1, -15.2) * mm, "mid": v(12.13, -15.02) * mm, "end": v(11.96, -15) * mm});
            skLineSegment(sketch, "E1879", {"start": v(12.33, -15.5) * mm, "end": v(8.7, -18.14) * mm});
            skArc(sketch, "E1880", {"start": v(8.62, -18.04) * mm, "mid": v(8.6, -18.21) * mm, "end": v(8.77, -18.24) * mm});
            skArc(sketch, "E1881", {"start": v(12.4, -15.6) * mm, "mid": v(12.43, -15.43) * mm, "end": v(12.25, -15.4) * mm});
            skLineSegment(sketch, "E1882", {"start": v(12.62, -15.9) * mm, "end": v(8.99, -18.54) * mm});
            skArc(sketch, "E1883", {"start": v(8.91, -18.44) * mm, "mid": v(8.89, -18.62) * mm, "end": v(9.06, -18.65) * mm});
            skArc(sketch, "E1884", {"start": v(12.7, -16) * mm, "mid": v(12.72, -15.83) * mm, "end": v(12.55, -15.8) * mm});
            skLineSegment(sketch, "E1885", {"start": v(12.92, -16.3) * mm, "end": v(9.28, -18.95) * mm});
            skArc(sketch, "E1886", {"start": v(9.2, -18.85) * mm, "mid": v(9.18, -19.02) * mm, "end": v(9.35, -19.05) * mm});
            skArc(sketch, "E1887", {"start": v(13, -16.4) * mm, "mid": v(13.02, -16.23) * mm, "end": v(12.84, -16.2) * mm});
            skLineSegment(sketch, "E1888", {"start": v(13.21, -16.71) * mm, "end": v(9.58, -19.35) * mm});
            skArc(sketch, "E1889", {"start": v(9.5, -19.25) * mm, "mid": v(9.47, -19.43) * mm, "end": v(9.65, -19.45) * mm});
            skArc(sketch, "E1890", {"start": v(13.29, -16.81) * mm, "mid": v(13.31, -16.64) * mm, "end": v(13.14, -16.6) * mm});
            skLineSegment(sketch, "E1891", {"start": v(13.5, -17.11) * mm, "end": v(9.87, -19.76) * mm});
            skArc(sketch, "E1892", {"start": v(9.8, -19.66) * mm, "mid": v(9.77, -19.83) * mm, "end": v(9.94, -19.86) * mm});
            skArc(sketch, "E1893", {"start": v(13.58, -17.22) * mm, "mid": v(13.6, -17.04) * mm, "end": v(13.43, -17.01) * mm});
            skLineSegment(sketch, "E1894", {"start": v(13.8, -17.52) * mm, "end": v(10.16, -20.16) * mm});
            skArc(sketch, "E1895", {"start": v(10.09, -20.06) * mm, "mid": v(10.06, -20.24) * mm, "end": v(10.24, -20.26) * mm});
            skArc(sketch, "E1896", {"start": v(13.88, -17.62) * mm, "mid": v(13.9, -17.44) * mm, "end": v(13.73, -17.42) * mm});
            skLineSegment(sketch, "E1897", {"start": v(14.06, -17.95) * mm, "end": v(10.5, -20.54) * mm});
            skArc(sketch, "E1898", {"start": v(10.42, -20.44) * mm, "mid": v(10.4, -20.61) * mm, "end": v(10.57, -20.64) * mm});
            skArc(sketch, "E1899", {"start": v(14.13, -18.05) * mm, "mid": v(14.16, -17.88) * mm, "end": v(13.99, -17.85) * mm});
            skLineSegment(sketch, "E1900", {"start": v(14.22, -18.45) * mm, "end": v(10.92, -20.85) * mm});
            skArc(sketch, "E1901", {"start": v(10.85, -20.75) * mm, "mid": v(10.82, -20.92) * mm, "end": v(11, -20.95) * mm});
            skArc(sketch, "E1902", {"start": v(14.3, -18.55) * mm, "mid": v(14.32, -18.38) * mm, "end": v(14.15, -18.35) * mm});
            skLineSegment(sketch, "E1903", {"start": v(14.38, -18.95) * mm, "end": v(11.35, -21.16) * mm});
            skArc(sketch, "E1904", {"start": v(11.27, -21.06) * mm, "mid": v(11.24, -21.23) * mm, "end": v(11.42, -21.26) * mm});
            skArc(sketch, "E1905", {"start": v(14.46, -19.05) * mm, "mid": v(14.49, -18.88) * mm, "end": v(14.31, -18.85) * mm});
            skLineSegment(sketch, "E1906", {"start": v(14.55, -19.45) * mm, "end": v(11.77, -21.47) * mm});
            skArc(sketch, "E1907", {"start": v(11.7, -21.36) * mm, "mid": v(11.67, -21.54) * mm, "end": v(11.84, -21.57) * mm});
            skArc(sketch, "E1908", {"start": v(14.62, -19.55) * mm, "mid": v(14.65, -19.38) * mm, "end": v(14.47, -19.35) * mm});
            skLineSegment(sketch, "E1909", {"start": v(14.7, -19.95) * mm, "end": v(12.2, -21.77) * mm});
            skArc(sketch, "E1910", {"start": v(12.12, -21.67) * mm, "mid": v(12.1, -21.85) * mm, "end": v(12.27, -21.88) * mm});
            skArc(sketch, "E1911", {"start": v(14.78, -20.05) * mm, "mid": v(14.81, -19.88) * mm, "end": v(14.64, -19.85) * mm});
            skLineSegment(sketch, "E1912", {"start": v(14.76, -20.53) * mm, "end": v(12.73, -22) * mm});
            skArc(sketch, "E1913", {"start": v(12.66, -21.9) * mm, "mid": v(12.63, -22.08) * mm, "end": v(12.8, -22.1) * mm});
            skArc(sketch, "E1914", {"start": v(14.83, -20.63) * mm, "mid": v(14.86, -20.46) * mm, "end": v(14.69, -20.43) * mm});
            skLineSegment(sketch, "E1915", {"start": v(20.06, -25.82) * mm, "end": v(19.92, -25.8) * mm});
            skArc(sketch, "E1916", {"start": v(19.93, -25.75) * mm, "mid": v(19.87, -25.79) * mm, "end": v(19.92, -25.85) * mm});
            skArc(sketch, "E1917", {"start": v(20.06, -25.87) * mm, "mid": v(20.11, -25.83) * mm, "end": v(20.07, -25.77) * mm});
            skLineSegment(sketch, "E1918", {"start": v(19.92, -25.8) * mm, "end": v(19.77, -25.8) * mm});
            skArc(sketch, "E1919", {"start": v(19.77, -25.75) * mm, "mid": v(19.72, -25.8) * mm, "end": v(19.77, -25.85) * mm});
            skArc(sketch, "E1920", {"start": v(19.92, -25.85) * mm, "mid": v(19.97, -25.8) * mm, "end": v(19.92, -25.75) * mm});
            skLineSegment(sketch, "E1921", {"start": v(19.77, -25.8) * mm, "end": v(19.62, -25.83) * mm});
            skArc(sketch, "E1922", {"start": v(19.6, -25.78) * mm, "mid": v(19.57, -25.84) * mm, "end": v(19.63, -25.88) * mm});
            skArc(sketch, "E1923", {"start": v(19.78, -25.85) * mm, "mid": v(19.82, -25.79) * mm, "end": v(19.76, -25.75) * mm});
            skLineSegment(sketch, "E1924", {"start": v(19.62, -25.83) * mm, "end": v(19.47, -25.88) * mm});
            skArc(sketch, "E1925", {"start": v(19.45, -25.84) * mm, "mid": v(19.42, -25.9) * mm, "end": v(19.49, -25.93) * mm});
            skArc(sketch, "E1926", {"start": v(19.63, -25.88) * mm, "mid": v(19.66, -25.81) * mm, "end": v(19.6, -25.78) * mm});
            skLineSegment(sketch, "E1927", {"start": v(19.47, -25.88) * mm, "end": v(19.4, -25.92) * mm});
            skArc(sketch, "E1928", {"start": v(19.37, -25.88) * mm, "mid": v(19.35, -25.95) * mm, "end": v(19.42, -25.97) * mm});
            skArc(sketch, "E1929", {"start": v(19.5, -25.93) * mm, "mid": v(19.51, -25.86) * mm, "end": v(19.44, -25.84) * mm});
            skLineSegment(sketch, "E1930", {"start": v(19.4, -25.92) * mm, "end": v(16.37, -28.14) * mm});
            skArc(sketch, "E1931", {"start": v(16.34, -28.1) * mm, "mid": v(16.33, -28.17) * mm, "end": v(16.4, -28.18) * mm});
            skArc(sketch, "E1932", {"start": v(19.43, -25.96) * mm, "mid": v(19.44, -25.9) * mm, "end": v(19.37, -25.88) * mm});
            skLineSegment(sketch, "E1933", {"start": v(16.37, -28.14) * mm, "end": v(16.27, -28.26) * mm});
            skArc(sketch, "E1934", {"start": v(16.23, -28.23) * mm, "mid": v(16.24, -28.3) * mm, "end": v(16.3, -28.3) * mm});
            skArc(sketch, "E1935", {"start": v(16.4, -28.17) * mm, "mid": v(16.4, -28.1) * mm, "end": v(16.33, -28.1) * mm});
            skLineSegment(sketch, "E1936", {"start": v(16.27, -28.26) * mm, "end": v(16.2, -28.4) * mm});
            skArc(sketch, "E1937", {"start": v(16.15, -28.38) * mm, "mid": v(16.17, -28.44) * mm, "end": v(16.24, -28.42) * mm});
            skArc(sketch, "E1938", {"start": v(16.31, -28.29) * mm, "mid": v(16.3, -28.22) * mm, "end": v(16.23, -28.24) * mm});
            skLineSegment(sketch, "E1939", {"start": v(16.2, -28.4) * mm, "end": v(16.15, -28.55) * mm});
            skArc(sketch, "E1940", {"start": v(16.1, -28.53) * mm, "mid": v(16.13, -28.6) * mm, "end": v(16.2, -28.56) * mm});
            skArc(sketch, "E1941", {"start": v(16.24, -28.42) * mm, "mid": v(16.21, -28.35) * mm, "end": v(16.15, -28.38) * mm});
            skLineSegment(sketch, "E1942", {"start": v(16.15, -28.55) * mm, "end": v(16.13, -28.68) * mm});
            skArc(sketch, "E1943", {"start": v(16.08, -28.67) * mm, "mid": v(16.12, -28.73) * mm, "end": v(16.18, -28.69) * mm});
            skArc(sketch, "E1944", {"start": v(16.2, -28.56) * mm, "mid": v(16.15, -28.5) * mm, "end": v(16.1, -28.54) * mm});
            skLineSegment(sketch, "E1945", {"start": v(16.13, -28.68) * mm, "end": v(16.27, -28.7) * mm});
            skArc(sketch, "E1946", {"start": v(16.26, -28.75) * mm, "mid": v(16.32, -28.7) * mm, "end": v(16.27, -28.65) * mm});
            skArc(sketch, "E1947", {"start": v(16.13, -28.63) * mm, "mid": v(16.08, -28.67) * mm, "end": v(16.12, -28.73) * mm});
            skLineSegment(sketch, "E1948", {"start": v(16.27, -28.7) * mm, "end": v(16.42, -28.7) * mm});
            skArc(sketch, "E1949", {"start": v(16.42, -28.75) * mm, "mid": v(16.47, -28.7) * mm, "end": v(16.42, -28.65) * mm});
            skArc(sketch, "E1950", {"start": v(16.26, -28.65) * mm, "mid": v(16.22, -28.7) * mm, "end": v(16.27, -28.75) * mm});
            skLineSegment(sketch, "E1951", {"start": v(16.42, -28.7) * mm, "end": v(16.57, -28.67) * mm});
            skArc(sketch, "E1952", {"start": v(16.58, -28.72) * mm, "mid": v(16.62, -28.66) * mm, "end": v(16.56, -28.62) * mm});
            skArc(sketch, "E1953", {"start": v(16.41, -28.65) * mm, "mid": v(16.37, -28.7) * mm, "end": v(16.43, -28.75) * mm});
            skLineSegment(sketch, "E1954", {"start": v(16.57, -28.67) * mm, "end": v(16.72, -28.61) * mm});
            skArc(sketch, "E1955", {"start": v(16.74, -28.66) * mm, "mid": v(16.77, -28.6) * mm, "end": v(16.7, -28.56) * mm});
            skArc(sketch, "E1956", {"start": v(16.56, -28.62) * mm, "mid": v(16.53, -28.68) * mm, "end": v(16.6, -28.71) * mm});
            skLineSegment(sketch, "E1957", {"start": v(16.72, -28.61) * mm, "end": v(16.8, -28.57) * mm});
            skArc(sketch, "E1958", {"start": v(16.82, -28.62) * mm, "mid": v(16.84, -28.55) * mm, "end": v(16.77, -28.53) * mm});
            skArc(sketch, "E1959", {"start": v(16.7, -28.57) * mm, "mid": v(16.68, -28.63) * mm, "end": v(16.75, -28.65) * mm});
            skLineSegment(sketch, "E1960", {"start": v(16.8, -28.57) * mm, "end": v(19.82, -26.36) * mm});
            skArc(sketch, "E1961", {"start": v(19.85, -26.4) * mm, "mid": v(19.86, -26.33) * mm, "end": v(19.8, -26.32) * mm});
            skArc(sketch, "E1962", {"start": v(16.76, -28.53) * mm, "mid": v(16.75, -28.6) * mm, "end": v(16.82, -28.61) * mm});
            skLineSegment(sketch, "E1963", {"start": v(19.82, -26.36) * mm, "end": v(19.92, -26.23) * mm});
            skArc(sketch, "E1964", {"start": v(19.96, -26.26) * mm, "mid": v(19.95, -26.2) * mm, "end": v(19.88, -26.2) * mm});
            skArc(sketch, "E1965", {"start": v(19.78, -26.32) * mm, "mid": v(19.8, -26.4) * mm, "end": v(19.86, -26.39) * mm});
            skLineSegment(sketch, "E1966", {"start": v(19.92, -26.23) * mm, "end": v(20, -26.1) * mm});
            skArc(sketch, "E1967", {"start": v(20.04, -26.12) * mm, "mid": v(20.02, -26.05) * mm, "end": v(19.95, -26.07) * mm});
            skArc(sketch, "E1968", {"start": v(19.88, -26.2) * mm, "mid": v(19.9, -26.28) * mm, "end": v(19.96, -26.26) * mm});
            skLineSegment(sketch, "E1969", {"start": v(20, -26.1) * mm, "end": v(20.04, -25.95) * mm});
            skArc(sketch, "E1970", {"start": v(20.1, -25.96) * mm, "mid": v(20.06, -25.9) * mm, "end": v(20, -25.93) * mm});
            skArc(sketch, "E1971", {"start": v(19.95, -26.08) * mm, "mid": v(19.98, -26.14) * mm, "end": v(20.04, -26.11) * mm});
            skLineSegment(sketch, "E1972", {"start": v(20.04, -25.95) * mm, "end": v(20.06, -25.82) * mm});
            skArc(sketch, "E1973", {"start": v(20.11, -25.83) * mm, "mid": v(20.07, -25.77) * mm, "end": v(20.01, -25.8) * mm});
            skArc(sketch, "E1974", {"start": v(20, -25.94) * mm, "mid": v(20.04, -26) * mm, "end": v(20.1, -25.96) * mm});
            skLineSegment(sketch, "E1975", {"start": v(19.75, -25.8) * mm, "end": v(16.2, -28.38) * mm});
            skArc(sketch, "E1976", {"start": v(16.18, -28.34) * mm, "mid": v(16.17, -28.4) * mm, "end": v(16.24, -28.42) * mm});
            skArc(sketch, "E1977", {"start": v(19.78, -25.84) * mm, "mid": v(19.8, -25.77) * mm, "end": v(19.72, -25.76) * mm});
            skLineSegment(sketch, "E1978", {"start": v(20.06, -25.82) * mm, "end": v(16.13, -28.68) * mm});
            skArc(sketch, "E1979", {"start": v(16.1, -28.64) * mm, "mid": v(16.1, -28.7) * mm, "end": v(16.16, -28.72) * mm});
            skArc(sketch, "E1980", {"start": v(20.1, -25.87) * mm, "mid": v(20.1, -25.8) * mm, "end": v(20.03, -25.78) * mm});
            skLineSegment(sketch, "E1981", {"start": v(19.97, -26.14) * mm, "end": v(16.46, -28.69) * mm});
            skArc(sketch, "E1982", {"start": v(16.43, -28.65) * mm, "mid": v(16.42, -28.72) * mm, "end": v(16.5, -28.73) * mm});
            skArc(sketch, "E1983", {"start": v(20, -26.18) * mm, "mid": v(20.01, -26.11) * mm, "end": v(19.94, -26.1) * mm});
            skCircle(sketch, "E1984", {"center": v(10.22, -16.41) * mm, "radius": 1.7 * mm});
            skArc(sketch, "E1985", {"start": v(10.22, -17.29) * mm, "mid": v(11.1, -16.41) * mm, "end": v(10.22, -15.54) * mm});
            skArc(sketch, "E1986", {"start": v(10.22, -15.54) * mm, "mid": v(9.35, -16.41) * mm, "end": v(10.22, -17.29) * mm});
            skCircle(sketch, "E1987", {"center": v(16.1, -24.5) * mm, "radius": 1.7 * mm});
            skArc(sketch, "E1988", {"start": v(16.1, -25.38) * mm, "mid": v(16.98, -24.5) * mm, "end": v(16.1, -23.63) * mm});
            skArc(sketch, "E1989", {"start": v(16.1, -23.63) * mm, "mid": v(15.22, -24.5) * mm, "end": v(16.1, -25.38) * mm});
            skLineSegment(sketch, "E1990", {"start": v(-4.8, -10.73) * mm, "end": v(-4.8, -10.27) * mm});
            skArc(sketch, "E1991", {"start": v(-4.8, -10.27) * mm, "mid": v(-4.8, -10.23) * mm, "end": v(-4.84, -10.22) * mm});
            skLineSegment(sketch, "E1992", {"start": v(-4.84, -10.22) * mm, "end": v(-5.24, -10.22) * mm});
            skArc(sketch, "E1993", {"start": v(-5.24, -10.22) * mm, "mid": v(-5.27, -10.23) * mm, "end": v(-5.28, -10.27) * mm});
            skLineSegment(sketch, "E1994", {"start": v(-5.28, -10.27) * mm, "end": v(-5.28, -10.73) * mm});
            skArc(sketch, "E1995", {"start": v(-5.28, -10.73) * mm, "mid": v(-5.27, -10.76) * mm, "end": v(-5.24, -10.78) * mm});
            skLineSegment(sketch, "E1996", {"start": v(-5.24, -10.78) * mm, "end": v(-4.84, -10.78) * mm});
            skArc(sketch, "E1997", {"start": v(-4.84, -10.78) * mm, "mid": v(-4.8, -10.76) * mm, "end": v(-4.8, -10.73) * mm});
            skLineSegment(sketch, "E1998", {"start": v(-3.92, -10.73) * mm, "end": v(-3.92, -10.27) * mm});
            skArc(sketch, "E1999", {"start": v(-3.92, -10.27) * mm, "mid": v(-3.93, -10.23) * mm, "end": v(-3.96, -10.22) * mm});
            skLineSegment(sketch, "E2000", {"start": v(-3.96, -10.22) * mm, "end": v(-4.36, -10.22) * mm});
            skArc(sketch, "E2001", {"start": v(-4.36, -10.22) * mm, "mid": v(-4.4, -10.23) * mm, "end": v(-4.4, -10.27) * mm});
            skLineSegment(sketch, "E2002", {"start": v(-4.4, -10.27) * mm, "end": v(-4.4, -10.73) * mm});
            skArc(sketch, "E2003", {"start": v(-4.4, -10.73) * mm, "mid": v(-4.4, -10.76) * mm, "end": v(-4.36, -10.78) * mm});
            skLineSegment(sketch, "E2004", {"start": v(-4.36, -10.78) * mm, "end": v(-3.96, -10.78) * mm});
            skArc(sketch, "E2005", {"start": v(-3.96, -10.78) * mm, "mid": v(-3.93, -10.76) * mm, "end": v(-3.92, -10.73) * mm});
            skLineSegment(sketch, "E2006", {"start": v(-4.8, -11.93) * mm, "end": v(-4.8, -11.47) * mm});
            skArc(sketch, "E2007", {"start": v(-4.8, -11.47) * mm, "mid": v(-4.8, -11.43) * mm, "end": v(-4.84, -11.42) * mm});
            skLineSegment(sketch, "E2008", {"start": v(-4.84, -11.42) * mm, "end": v(-5.24, -11.42) * mm});
            skArc(sketch, "E2009", {"start": v(-5.24, -11.42) * mm, "mid": v(-5.27, -11.43) * mm, "end": v(-5.28, -11.47) * mm});
            skLineSegment(sketch, "E2010", {"start": v(-5.28, -11.47) * mm, "end": v(-5.28, -11.93) * mm});
            skArc(sketch, "E2011", {"start": v(-5.28, -11.93) * mm, "mid": v(-5.27, -11.96) * mm, "end": v(-5.24, -11.98) * mm});
            skLineSegment(sketch, "E2012", {"start": v(-5.24, -11.98) * mm, "end": v(-4.84, -11.98) * mm});
            skArc(sketch, "E2013", {"start": v(-4.84, -11.98) * mm, "mid": v(-4.8, -11.96) * mm, "end": v(-4.8, -11.93) * mm});
            skLineSegment(sketch, "E2014", {"start": v(-3.92, -11.93) * mm, "end": v(-3.92, -11.47) * mm});
            skArc(sketch, "E2015", {"start": v(-3.92, -11.47) * mm, "mid": v(-3.93, -11.43) * mm, "end": v(-3.96, -11.42) * mm});
            skLineSegment(sketch, "E2016", {"start": v(-3.96, -11.42) * mm, "end": v(-4.36, -11.42) * mm});
            skArc(sketch, "E2017", {"start": v(-4.36, -11.42) * mm, "mid": v(-4.4, -11.43) * mm, "end": v(-4.4, -11.47) * mm});
            skLineSegment(sketch, "E2018", {"start": v(-4.4, -11.47) * mm, "end": v(-4.4, -11.93) * mm});
            skArc(sketch, "E2019", {"start": v(-4.4, -11.93) * mm, "mid": v(-4.4, -11.96) * mm, "end": v(-4.36, -11.98) * mm});
            skLineSegment(sketch, "E2020", {"start": v(-4.36, -11.98) * mm, "end": v(-3.96, -11.98) * mm});
            skArc(sketch, "E2021", {"start": v(-3.96, -11.98) * mm, "mid": v(-3.93, -11.96) * mm, "end": v(-3.92, -11.93) * mm});
            skLineSegment(sketch, "E2022", {"start": v(9.92, -10.64) * mm, "end": v(10.2, -11.02) * mm});
            skArc(sketch, "E2023", {"start": v(10.2, -11.02) * mm, "mid": v(10.23, -11.04) * mm, "end": v(10.26, -11.03) * mm});
            skLineSegment(sketch, "E2024", {"start": v(10.26, -11.03) * mm, "end": v(10.58, -10.8) * mm});
            skArc(sketch, "E2025", {"start": v(10.58, -10.8) * mm, "mid": v(10.6, -10.77) * mm, "end": v(10.6, -10.73) * mm});
            skLineSegment(sketch, "E2026", {"start": v(10.6, -10.73) * mm, "end": v(10.32, -10.36) * mm});
            skArc(sketch, "E2027", {"start": v(10.32, -10.36) * mm, "mid": v(10.29, -10.34) * mm, "end": v(10.25, -10.35) * mm});
            skLineSegment(sketch, "E2028", {"start": v(10.25, -10.35) * mm, "end": v(9.93, -10.58) * mm});
            skArc(sketch, "E2029", {"start": v(9.93, -10.58) * mm, "mid": v(9.91, -10.6) * mm, "end": v(9.92, -10.64) * mm});
            skLineSegment(sketch, "E2030", {"start": v(9.2, -11.16) * mm, "end": v(9.48, -11.54) * mm});
            skArc(sketch, "E2031", {"start": v(9.48, -11.54) * mm, "mid": v(9.51, -11.56) * mm, "end": v(9.55, -11.55) * mm});
            skLineSegment(sketch, "E2032", {"start": v(9.55, -11.55) * mm, "end": v(9.87, -11.32) * mm});
            skArc(sketch, "E2033", {"start": v(9.87, -11.32) * mm, "mid": v(9.89, -11.29) * mm, "end": v(9.88, -11.25) * mm});
            skLineSegment(sketch, "E2034", {"start": v(9.88, -11.25) * mm, "end": v(9.6, -10.87) * mm});
            skArc(sketch, "E2035", {"start": v(9.6, -10.87) * mm, "mid": v(9.57, -10.86) * mm, "end": v(9.54, -10.86) * mm});
            skLineSegment(sketch, "E2036", {"start": v(9.54, -10.86) * mm, "end": v(9.22, -11.1) * mm});
            skArc(sketch, "E2037", {"start": v(9.22, -11.1) * mm, "mid": v(9.2, -11.13) * mm, "end": v(9.2, -11.16) * mm});
            skLineSegment(sketch, "E2038", {"start": v(11.02, 4.12) * mm, "end": v(11.46, 4.26) * mm});
            skArc(sketch, "E2039", {"start": v(11.46, 4.26) * mm, "mid": v(11.49, 4.28) * mm, "end": v(11.5, 4.32) * mm});
            skLineSegment(sketch, "E2040", {"start": v(11.5, 4.32) * mm, "end": v(11.37, 4.7) * mm});
            skArc(sketch, "E2041", {"start": v(11.37, 4.7) * mm, "mid": v(11.35, 4.72) * mm, "end": v(11.3, 4.73) * mm});
            skLineSegment(sketch, "E2042", {"start": v(11.3, 4.73) * mm, "end": v(10.87, 4.58) * mm});
            skArc(sketch, "E2043", {"start": v(10.87, 4.58) * mm, "mid": v(10.84, 4.56) * mm, "end": v(10.84, 4.52) * mm});
            skLineSegment(sketch, "E2044", {"start": v(10.84, 4.52) * mm, "end": v(10.96, 4.15) * mm});
            skArc(sketch, "E2045", {"start": v(10.96, 4.15) * mm, "mid": v(10.98, 4.12) * mm, "end": v(11.02, 4.12) * mm});
            skLineSegment(sketch, "E2046", {"start": v(11.3, 3.28) * mm, "end": v(11.73, 3.42) * mm});
            skArc(sketch, "E2047", {"start": v(11.73, 3.42) * mm, "mid": v(11.76, 3.45) * mm, "end": v(11.76, 3.48) * mm});
            skLineSegment(sketch, "E2048", {"start": v(11.76, 3.48) * mm, "end": v(11.64, 3.86) * mm});
            skArc(sketch, "E2049", {"start": v(11.64, 3.86) * mm, "mid": v(11.62, 3.89) * mm, "end": v(11.58, 3.89) * mm});
            skLineSegment(sketch, "E2050", {"start": v(11.58, 3.89) * mm, "end": v(11.14, 3.74) * mm});
            skArc(sketch, "E2051", {"start": v(11.14, 3.74) * mm, "mid": v(11.11, 3.72) * mm, "end": v(11.1, 3.69) * mm});
            skLineSegment(sketch, "E2052", {"start": v(11.1, 3.69) * mm, "end": v(11.23, 3.3) * mm});
            skArc(sketch, "E2053", {"start": v(11.23, 3.3) * mm, "mid": v(11.25, 3.28) * mm, "end": v(11.3, 3.28) * mm});
            skLineSegment(sketch, "E2054", {"start": v(1.7, 5.33) * mm, "end": v(1.7, 4.87) * mm});
            skArc(sketch, "E2055", {"start": v(1.7, 4.87) * mm, "mid": v(1.7, 4.83) * mm, "end": v(1.74, 4.82) * mm});
            skLineSegment(sketch, "E2056", {"start": v(1.74, 4.82) * mm, "end": v(2.14, 4.82) * mm});
            skArc(sketch, "E2057", {"start": v(2.14, 4.82) * mm, "mid": v(2.17, 4.83) * mm, "end": v(2.18, 4.87) * mm});
            skLineSegment(sketch, "E2058", {"start": v(2.18, 4.87) * mm, "end": v(2.18, 5.33) * mm});
            skArc(sketch, "E2059", {"start": v(2.18, 5.33) * mm, "mid": v(2.17, 5.36) * mm, "end": v(2.14, 5.38) * mm});
            skLineSegment(sketch, "E2060", {"start": v(2.14, 5.38) * mm, "end": v(1.74, 5.38) * mm});
            skArc(sketch, "E2061", {"start": v(1.74, 5.38) * mm, "mid": v(1.7, 5.36) * mm, "end": v(1.7, 5.33) * mm});
            skLineSegment(sketch, "E2062", {"start": v(0.82, 5.33) * mm, "end": v(0.82, 4.87) * mm});
            skArc(sketch, "E2063", {"start": v(0.82, 4.87) * mm, "mid": v(0.83, 4.83) * mm, "end": v(0.86, 4.82) * mm});
            skLineSegment(sketch, "E2064", {"start": v(0.86, 4.82) * mm, "end": v(1.26, 4.82) * mm});
            skArc(sketch, "E2065", {"start": v(1.26, 4.82) * mm, "mid": v(1.3, 4.83) * mm, "end": v(1.3, 4.87) * mm});
            skLineSegment(sketch, "E2066", {"start": v(1.3, 4.87) * mm, "end": v(1.3, 5.33) * mm});
            skArc(sketch, "E2067", {"start": v(1.3, 5.33) * mm, "mid": v(1.3, 5.36) * mm, "end": v(1.26, 5.38) * mm});
            skLineSegment(sketch, "E2068", {"start": v(1.26, 5.38) * mm, "end": v(0.86, 5.38) * mm});
            skArc(sketch, "E2069", {"start": v(0.86, 5.38) * mm, "mid": v(0.83, 5.36) * mm, "end": v(0.82, 5.33) * mm});
            skLineSegment(sketch, "E2070", {"start": v(-11.42, 4.25) * mm, "end": v(-10.98, 4.1) * mm});
            skArc(sketch, "E2071", {"start": v(-10.98, 4.1) * mm, "mid": v(-10.94, 4.1) * mm, "end": v(-10.92, 4.14) * mm});
            skLineSegment(sketch, "E2072", {"start": v(-10.92, 4.14) * mm, "end": v(-10.8, 4.51) * mm});
            skArc(sketch, "E2073", {"start": v(-10.8, 4.51) * mm, "mid": v(-10.8, 4.55) * mm, "end": v(-10.83, 4.57) * mm});
            skLineSegment(sketch, "E2074", {"start": v(-10.83, 4.57) * mm, "end": v(-11.27, 4.72) * mm});
            skArc(sketch, "E2075", {"start": v(-11.27, 4.72) * mm, "mid": v(-11.3, 4.71) * mm, "end": v(-11.33, 4.69) * mm});
            skLineSegment(sketch, "E2076", {"start": v(-11.33, 4.69) * mm, "end": v(-11.45, 4.3) * mm});
            skArc(sketch, "E2077", {"start": v(-11.45, 4.3) * mm, "mid": v(-11.45, 4.27) * mm, "end": v(-11.42, 4.25) * mm});
            skLineSegment(sketch, "E2078", {"start": v(-11.7, 3.41) * mm, "end": v(-11.25, 3.27) * mm});
            skArc(sketch, "E2079", {"start": v(-11.25, 3.27) * mm, "mid": v(-11.21, 3.27) * mm, "end": v(-11.2, 3.3) * mm});
            skLineSegment(sketch, "E2080", {"start": v(-11.2, 3.3) * mm, "end": v(-11.07, 3.68) * mm});
            skArc(sketch, "E2081", {"start": v(-11.07, 3.68) * mm, "mid": v(-11.07, 3.71) * mm, "end": v(-11.1, 3.73) * mm});
            skLineSegment(sketch, "E2082", {"start": v(-11.1, 3.73) * mm, "end": v(-11.54, 3.88) * mm});
            skArc(sketch, "E2083", {"start": v(-11.54, 3.88) * mm, "mid": v(-11.58, 3.88) * mm, "end": v(-11.6, 3.85) * mm});
            skLineSegment(sketch, "E2084", {"start": v(-11.6, 3.85) * mm, "end": v(-11.72, 3.47) * mm});
            skArc(sketch, "E2085", {"start": v(-11.72, 3.47) * mm, "mid": v(-11.72, 3.44) * mm, "end": v(-11.7, 3.41) * mm});
            skLineSegment(sketch, "E2086", {"start": v(-10.05, -11.12) * mm, "end": v(-9.77, -10.74) * mm});
            skArc(sketch, "E2087", {"start": v(-9.77, -10.74) * mm, "mid": v(-9.76, -10.7) * mm, "end": v(-9.78, -10.68) * mm});
            skLineSegment(sketch, "E2088", {"start": v(-9.78, -10.68) * mm, "end": v(-10.1, -10.45) * mm});
            skArc(sketch, "E2089", {"start": v(-10.1, -10.45) * mm, "mid": v(-10.14, -10.44) * mm, "end": v(-10.17, -10.46) * mm});
            skLineSegment(sketch, "E2090", {"start": v(-10.17, -10.46) * mm, "end": v(-10.44, -10.83) * mm});
            skArc(sketch, "E2091", {"start": v(-10.44, -10.83) * mm, "mid": v(-10.45, -10.87) * mm, "end": v(-10.43, -10.9) * mm});
            skLineSegment(sketch, "E2092", {"start": v(-10.43, -10.9) * mm, "end": v(-10.11, -11.13) * mm});
            skArc(sketch, "E2093", {"start": v(-10.11, -11.13) * mm, "mid": v(-10.08, -11.14) * mm, "end": v(-10.05, -11.12) * mm});
            skLineSegment(sketch, "E2094", {"start": v(-9.33, -11.64) * mm, "end": v(-9.06, -11.26) * mm});
            skArc(sketch, "E2095", {"start": v(-9.06, -11.26) * mm, "mid": v(-9.05, -11.23) * mm, "end": v(-9.07, -11.2) * mm});
            skLineSegment(sketch, "E2096", {"start": v(-9.07, -11.2) * mm, "end": v(-9.39, -10.96) * mm});
            skArc(sketch, "E2097", {"start": v(-9.39, -10.96) * mm, "mid": v(-9.42, -10.96) * mm, "end": v(-9.45, -10.97) * mm});
            skLineSegment(sketch, "E2098", {"start": v(-9.45, -10.97) * mm, "end": v(-9.73, -11.35) * mm});
            skArc(sketch, "E2099", {"start": v(-9.73, -11.35) * mm, "mid": v(-9.74, -11.39) * mm, "end": v(-9.72, -11.42) * mm});
            skLineSegment(sketch, "E2100", {"start": v(-9.72, -11.42) * mm, "end": v(-9.4, -11.65) * mm});
            skArc(sketch, "E2101", {"start": v(-9.4, -11.65) * mm, "mid": v(-9.36, -11.66) * mm, "end": v(-9.33, -11.64) * mm});
            skLineSegment(sketch, "E2102", {"start": v(7.82, -12.14) * mm, "end": v(8.1, -12.52) * mm});
            skArc(sketch, "E2103", {"start": v(8.1, -12.52) * mm, "mid": v(8.13, -12.54) * mm, "end": v(8.16, -12.53) * mm});
            skLineSegment(sketch, "E2104", {"start": v(8.16, -12.53) * mm, "end": v(8.48, -12.3) * mm});
            skArc(sketch, "E2105", {"start": v(8.48, -12.3) * mm, "mid": v(8.5, -12.27) * mm, "end": v(8.5, -12.23) * mm});
            skLineSegment(sketch, "E2106", {"start": v(8.5, -12.23) * mm, "end": v(8.22, -11.86) * mm});
            skArc(sketch, "E2107", {"start": v(8.22, -11.86) * mm, "mid": v(8.19, -11.84) * mm, "end": v(8.15, -11.85) * mm});
            skLineSegment(sketch, "E2108", {"start": v(8.15, -11.85) * mm, "end": v(7.83, -12.08) * mm});
            skArc(sketch, "E2109", {"start": v(7.83, -12.08) * mm, "mid": v(7.81, -12.1) * mm, "end": v(7.82, -12.14) * mm});
            skLineSegment(sketch, "E2110", {"start": v(7.1, -12.66) * mm, "end": v(7.38, -13.04) * mm});
            skArc(sketch, "E2111", {"start": v(7.38, -13.04) * mm, "mid": v(7.41, -13.06) * mm, "end": v(7.45, -13.05) * mm});
            skLineSegment(sketch, "E2112", {"start": v(7.45, -13.05) * mm, "end": v(7.77, -12.82) * mm});
            skArc(sketch, "E2113", {"start": v(7.77, -12.82) * mm, "mid": v(7.79, -12.79) * mm, "end": v(7.78, -12.75) * mm});
            skLineSegment(sketch, "E2114", {"start": v(7.78, -12.75) * mm, "end": v(7.5, -12.37) * mm});
            skArc(sketch, "E2115", {"start": v(7.5, -12.37) * mm, "mid": v(7.47, -12.36) * mm, "end": v(7.44, -12.36) * mm});
            skLineSegment(sketch, "E2116", {"start": v(7.44, -12.36) * mm, "end": v(7.12, -12.6) * mm});
            skArc(sketch, "E2117", {"start": v(7.12, -12.6) * mm, "mid": v(7.1, -12.63) * mm, "end": v(7.1, -12.66) * mm});
            skLineSegment(sketch, "E2118", {"start": v(11.85, 1.72) * mm, "end": v(12.3, 1.86) * mm});
            skArc(sketch, "E2119", {"start": v(12.3, 1.86) * mm, "mid": v(12.32, 1.88) * mm, "end": v(12.32, 1.92) * mm});
            skLineSegment(sketch, "E2120", {"start": v(12.32, 1.92) * mm, "end": v(12.2, 2.3) * mm});
            skArc(sketch, "E2121", {"start": v(12.2, 2.3) * mm, "mid": v(12.18, 2.32) * mm, "end": v(12.14, 2.33) * mm});
            skLineSegment(sketch, "E2122", {"start": v(12.14, 2.33) * mm, "end": v(11.7, 2.18) * mm});
            skArc(sketch, "E2123", {"start": v(11.7, 2.18) * mm, "mid": v(11.67, 2.16) * mm, "end": v(11.67, 2.12) * mm});
            skLineSegment(sketch, "E2124", {"start": v(11.67, 2.12) * mm, "end": v(11.79, 1.75) * mm});
            skArc(sketch, "E2125", {"start": v(11.79, 1.75) * mm, "mid": v(11.81, 1.72) * mm, "end": v(11.85, 1.72) * mm});
            skLineSegment(sketch, "E2126", {"start": v(12.12, 0.88) * mm, "end": v(12.56, 1.02) * mm});
            skArc(sketch, "E2127", {"start": v(12.56, 1.02) * mm, "mid": v(12.59, 1.05) * mm, "end": v(12.6, 1.08) * mm});
            skLineSegment(sketch, "E2128", {"start": v(12.6, 1.08) * mm, "end": v(12.47, 1.46) * mm});
            skArc(sketch, "E2129", {"start": v(12.47, 1.46) * mm, "mid": v(12.45, 1.49) * mm, "end": v(12.41, 1.49) * mm});
            skLineSegment(sketch, "E2130", {"start": v(12.41, 1.49) * mm, "end": v(11.97, 1.34) * mm});
            skArc(sketch, "E2131", {"start": v(11.97, 1.34) * mm, "mid": v(11.94, 1.32) * mm, "end": v(11.94, 1.29) * mm});
            skLineSegment(sketch, "E2132", {"start": v(11.94, 1.29) * mm, "end": v(12.06, 0.9) * mm});
            skArc(sketch, "E2133", {"start": v(12.06, 0.9) * mm, "mid": v(12.08, 0.88) * mm, "end": v(12.12, 0.88) * mm});
            skLineSegment(sketch, "E2134", {"start": v(-1.3, 5.33) * mm, "end": v(-1.3, 4.87) * mm});
            skArc(sketch, "E2135", {"start": v(-1.3, 4.87) * mm, "mid": v(-1.3, 4.83) * mm, "end": v(-1.26, 4.82) * mm});
            skLineSegment(sketch, "E2136", {"start": v(-1.26, 4.82) * mm, "end": v(-0.86, 4.82) * mm});
            skArc(sketch, "E2137", {"start": v(-0.86, 4.82) * mm, "mid": v(-0.83, 4.83) * mm, "end": v(-0.82, 4.87) * mm});
            skLineSegment(sketch, "E2138", {"start": v(-0.82, 4.87) * mm, "end": v(-0.82, 5.33) * mm});
            skArc(sketch, "E2139", {"start": v(-0.82, 5.33) * mm, "mid": v(-0.83, 5.36) * mm, "end": v(-0.86, 5.38) * mm});
            skLineSegment(sketch, "E2140", {"start": v(-0.86, 5.38) * mm, "end": v(-1.26, 5.38) * mm});
            skArc(sketch, "E2141", {"start": v(-1.26, 5.38) * mm, "mid": v(-1.3, 5.36) * mm, "end": v(-1.3, 5.33) * mm});
            skLineSegment(sketch, "E2142", {"start": v(-2.18, 5.33) * mm, "end": v(-2.18, 4.87) * mm});
            skArc(sketch, "E2143", {"start": v(-2.18, 4.87) * mm, "mid": v(-2.17, 4.83) * mm, "end": v(-2.14, 4.82) * mm});
            skLineSegment(sketch, "E2144", {"start": v(-2.14, 4.82) * mm, "end": v(-1.74, 4.82) * mm});
            skArc(sketch, "E2145", {"start": v(-1.74, 4.82) * mm, "mid": v(-1.7, 4.83) * mm, "end": v(-1.7, 4.87) * mm});
            skLineSegment(sketch, "E2146", {"start": v(-1.7, 4.87) * mm, "end": v(-1.7, 5.33) * mm});
            skArc(sketch, "E2147", {"start": v(-1.7, 5.33) * mm, "mid": v(-1.7, 5.36) * mm, "end": v(-1.74, 5.38) * mm});
            skLineSegment(sketch, "E2148", {"start": v(-1.74, 5.38) * mm, "end": v(-2.14, 5.38) * mm});
            skArc(sketch, "E2149", {"start": v(-2.14, 5.38) * mm, "mid": v(-2.17, 5.36) * mm, "end": v(-2.18, 5.33) * mm});
            skLineSegment(sketch, "E2150", {"start": v(-12.16, 1.86) * mm, "end": v(-11.72, 1.72) * mm});
            skArc(sketch, "E2151", {"start": v(-11.72, 1.72) * mm, "mid": v(-11.68, 1.72) * mm, "end": v(-11.66, 1.75) * mm});
            skLineSegment(sketch, "E2152", {"start": v(-11.66, 1.75) * mm, "end": v(-11.54, 2.12) * mm});
            skArc(sketch, "E2153", {"start": v(-11.54, 2.12) * mm, "mid": v(-11.54, 2.16) * mm, "end": v(-11.57, 2.18) * mm});
            skLineSegment(sketch, "E2154", {"start": v(-11.57, 2.18) * mm, "end": v(-12, 2.33) * mm});
            skArc(sketch, "E2155", {"start": v(-12, 2.33) * mm, "mid": v(-12.05, 2.32) * mm, "end": v(-12.07, 2.3) * mm});
            skLineSegment(sketch, "E2156", {"start": v(-12.07, 2.3) * mm, "end": v(-12.2, 1.92) * mm});
            skArc(sketch, "E2157", {"start": v(-12.2, 1.92) * mm, "mid": v(-12.19, 1.88) * mm, "end": v(-12.16, 1.86) * mm});
            skLineSegment(sketch, "E2158", {"start": v(-12.43, 1.02) * mm, "end": v(-12, 0.88) * mm});
            skArc(sketch, "E2159", {"start": v(-12, 0.88) * mm, "mid": v(-11.95, 0.88) * mm, "end": v(-11.93, 0.9) * mm});
            skLineSegment(sketch, "E2160", {"start": v(-11.93, 0.9) * mm, "end": v(-11.8, 1.29) * mm});
            skArc(sketch, "E2161", {"start": v(-11.8, 1.29) * mm, "mid": v(-11.81, 1.32) * mm, "end": v(-11.84, 1.34) * mm});
            skLineSegment(sketch, "E2162", {"start": v(-11.84, 1.34) * mm, "end": v(-12.28, 1.49) * mm});
            skArc(sketch, "E2163", {"start": v(-12.28, 1.49) * mm, "mid": v(-12.32, 1.49) * mm, "end": v(-12.34, 1.46) * mm});
            skLineSegment(sketch, "E2164", {"start": v(-12.34, 1.46) * mm, "end": v(-12.46, 1.08) * mm});
            skArc(sketch, "E2165", {"start": v(-12.46, 1.08) * mm, "mid": v(-12.46, 1.05) * mm, "end": v(-12.43, 1.02) * mm});
            skLineSegment(sketch, "E2166", {"start": v(-8.05, -12.52) * mm, "end": v(-7.77, -12.14) * mm});
            skArc(sketch, "E2167", {"start": v(-7.77, -12.14) * mm, "mid": v(-7.76, -12.1) * mm, "end": v(-7.78, -12.08) * mm});
            skLineSegment(sketch, "E2168", {"start": v(-7.78, -12.08) * mm, "end": v(-8.1, -11.85) * mm});
            skArc(sketch, "E2169", {"start": v(-8.1, -11.85) * mm, "mid": v(-8.14, -11.84) * mm, "end": v(-8.17, -11.86) * mm});
            skLineSegment(sketch, "E2170", {"start": v(-8.17, -11.86) * mm, "end": v(-8.44, -12.23) * mm});
            skArc(sketch, "E2171", {"start": v(-8.44, -12.23) * mm, "mid": v(-8.45, -12.27) * mm, "end": v(-8.43, -12.3) * mm});
            skLineSegment(sketch, "E2172", {"start": v(-8.43, -12.3) * mm, "end": v(-8.11, -12.53) * mm});
            skArc(sketch, "E2173", {"start": v(-8.11, -12.53) * mm, "mid": v(-8.08, -12.54) * mm, "end": v(-8.05, -12.52) * mm});
            skLineSegment(sketch, "E2174", {"start": v(-7.33, -13.04) * mm, "end": v(-7.06, -12.66) * mm});
            skArc(sketch, "E2175", {"start": v(-7.06, -12.66) * mm, "mid": v(-7.05, -12.63) * mm, "end": v(-7.07, -12.6) * mm});
            skLineSegment(sketch, "E2176", {"start": v(-7.07, -12.6) * mm, "end": v(-7.39, -12.36) * mm});
            skArc(sketch, "E2177", {"start": v(-7.39, -12.36) * mm, "mid": v(-7.42, -12.36) * mm, "end": v(-7.45, -12.37) * mm});
            skLineSegment(sketch, "E2178", {"start": v(-7.45, -12.37) * mm, "end": v(-7.73, -12.75) * mm});
            skArc(sketch, "E2179", {"start": v(-7.73, -12.75) * mm, "mid": v(-7.74, -12.79) * mm, "end": v(-7.72, -12.82) * mm});
            skLineSegment(sketch, "E2180", {"start": v(-7.72, -12.82) * mm, "end": v(-7.4, -13.05) * mm});
            skArc(sketch, "E2181", {"start": v(-7.4, -13.05) * mm, "mid": v(-7.36, -13.06) * mm, "end": v(-7.33, -13.04) * mm});
            skLineSegment(sketch, "E2182", {"start": v(4.6, -10.73) * mm, "end": v(4.6, -10.27) * mm});
            skArc(sketch, "E2183", {"start": v(4.6, -10.27) * mm, "mid": v(4.6, -10.23) * mm, "end": v(4.56, -10.22) * mm});
            skLineSegment(sketch, "E2184", {"start": v(4.56, -10.22) * mm, "end": v(4.16, -10.22) * mm});
            skArc(sketch, "E2185", {"start": v(4.16, -10.22) * mm, "mid": v(4.13, -10.23) * mm, "end": v(4.12, -10.27) * mm});
            skLineSegment(sketch, "E2186", {"start": v(4.12, -10.27) * mm, "end": v(4.12, -10.73) * mm});
            skArc(sketch, "E2187", {"start": v(4.12, -10.73) * mm, "mid": v(4.13, -10.76) * mm, "end": v(4.16, -10.78) * mm});
            skLineSegment(sketch, "E2188", {"start": v(4.16, -10.78) * mm, "end": v(4.56, -10.78) * mm});
            skArc(sketch, "E2189", {"start": v(4.56, -10.78) * mm, "mid": v(4.6, -10.76) * mm, "end": v(4.6, -10.73) * mm});
            skLineSegment(sketch, "E2190", {"start": v(5.48, -10.73) * mm, "end": v(5.48, -10.27) * mm});
            skArc(sketch, "E2191", {"start": v(5.48, -10.27) * mm, "mid": v(5.47, -10.23) * mm, "end": v(5.44, -10.22) * mm});
            skLineSegment(sketch, "E2192", {"start": v(5.44, -10.22) * mm, "end": v(5.04, -10.22) * mm});
            skArc(sketch, "E2193", {"start": v(5.04, -10.22) * mm, "mid": v(5, -10.23) * mm, "end": v(5, -10.27) * mm});
            skLineSegment(sketch, "E2194", {"start": v(5, -10.27) * mm, "end": v(5, -10.73) * mm});
            skArc(sketch, "E2195", {"start": v(5, -10.73) * mm, "mid": v(5, -10.76) * mm, "end": v(5.04, -10.78) * mm});
            skLineSegment(sketch, "E2196", {"start": v(5.04, -10.78) * mm, "end": v(5.44, -10.78) * mm});
            skArc(sketch, "E2197", {"start": v(5.44, -10.78) * mm, "mid": v(5.47, -10.76) * mm, "end": v(5.48, -10.73) * mm});
            skLineSegment(sketch, "E2198", {"start": v(4.97, -7.4) * mm, "end": v(5.43, -7.4) * mm});
            skArc(sketch, "E2199", {"start": v(5.43, -7.4) * mm, "mid": v(5.47, -7.39) * mm, "end": v(5.48, -7.36) * mm});
            skLineSegment(sketch, "E2200", {"start": v(5.48, -7.36) * mm, "end": v(5.48, -6.96) * mm});
            skArc(sketch, "E2201", {"start": v(5.48, -6.96) * mm, "mid": v(5.47, -6.93) * mm, "end": v(5.43, -6.91) * mm});
            skLineSegment(sketch, "E2202", {"start": v(5.43, -6.91) * mm, "end": v(4.97, -6.91) * mm});
            skArc(sketch, "E2203", {"start": v(4.97, -6.91) * mm, "mid": v(4.93, -6.93) * mm, "end": v(4.92, -6.96) * mm});
            skLineSegment(sketch, "E2204", {"start": v(4.92, -6.96) * mm, "end": v(4.92, -7.36) * mm});
            skArc(sketch, "E2205", {"start": v(4.92, -7.36) * mm, "mid": v(4.93, -7.39) * mm, "end": v(4.97, -7.4) * mm});
            skLineSegment(sketch, "E2206", {"start": v(4.97, -8.28) * mm, "end": v(5.43, -8.28) * mm});
            skArc(sketch, "E2207", {"start": v(5.43, -8.28) * mm, "mid": v(5.47, -8.27) * mm, "end": v(5.48, -8.24) * mm});
            skLineSegment(sketch, "E2208", {"start": v(5.48, -8.24) * mm, "end": v(5.48, -7.84) * mm});
            skArc(sketch, "E2209", {"start": v(5.48, -7.84) * mm, "mid": v(5.47, -7.8) * mm, "end": v(5.43, -7.8) * mm});
            skLineSegment(sketch, "E2210", {"start": v(5.43, -7.8) * mm, "end": v(4.97, -7.8) * mm});
            skArc(sketch, "E2211", {"start": v(4.97, -7.8) * mm, "mid": v(4.93, -7.8) * mm, "end": v(4.92, -7.84) * mm});
            skLineSegment(sketch, "E2212", {"start": v(4.92, -7.84) * mm, "end": v(4.92, -8.24) * mm});
            skArc(sketch, "E2213", {"start": v(4.92, -8.24) * mm, "mid": v(4.93, -8.27) * mm, "end": v(4.97, -8.28) * mm});
            skLineSegment(sketch, "E2214", {"start": v(-7.87, -1.6) * mm, "end": v(-8.33, -1.6) * mm});
            skArc(sketch, "E2215", {"start": v(-8.33, -1.6) * mm, "mid": v(-8.37, -1.6) * mm, "end": v(-8.38, -1.64) * mm});
            skLineSegment(sketch, "E2216", {"start": v(-8.38, -1.64) * mm, "end": v(-8.38, -2.04) * mm});
            skArc(sketch, "E2217", {"start": v(-8.38, -2.04) * mm, "mid": v(-8.37, -2.07) * mm, "end": v(-8.33, -2.08) * mm});
            skLineSegment(sketch, "E2218", {"start": v(-8.33, -2.08) * mm, "end": v(-7.87, -2.08) * mm});
            skArc(sketch, "E2219", {"start": v(-7.87, -2.08) * mm, "mid": v(-7.83, -2.07) * mm, "end": v(-7.82, -2.04) * mm});
            skLineSegment(sketch, "E2220", {"start": v(-7.82, -2.04) * mm, "end": v(-7.82, -1.64) * mm});
            skArc(sketch, "E2221", {"start": v(-7.82, -1.64) * mm, "mid": v(-7.83, -1.6) * mm, "end": v(-7.87, -1.6) * mm});
            skLineSegment(sketch, "E2222", {"start": v(-7.87, -0.71) * mm, "end": v(-8.33, -0.71) * mm});
            skArc(sketch, "E2223", {"start": v(-8.33, -0.71) * mm, "mid": v(-8.37, -0.73) * mm, "end": v(-8.38, -0.76) * mm});
            skLineSegment(sketch, "E2224", {"start": v(-8.38, -0.76) * mm, "end": v(-8.38, -1.16) * mm});
            skArc(sketch, "E2225", {"start": v(-8.38, -1.16) * mm, "mid": v(-8.37, -1.19) * mm, "end": v(-8.33, -1.2) * mm});
            skLineSegment(sketch, "E2226", {"start": v(-8.33, -1.2) * mm, "end": v(-7.87, -1.2) * mm});
            skArc(sketch, "E2227", {"start": v(-7.87, -1.2) * mm, "mid": v(-7.83, -1.19) * mm, "end": v(-7.82, -1.16) * mm});
            skLineSegment(sketch, "E2228", {"start": v(-7.82, -1.16) * mm, "end": v(-7.82, -0.76) * mm});
            skArc(sketch, "E2229", {"start": v(-7.82, -0.76) * mm, "mid": v(-7.83, -0.73) * mm, "end": v(-7.87, -0.71) * mm});
            skLineSegment(sketch, "E2230", {"start": v(-5.13, 8.8) * mm, "end": v(-4.67, 8.8) * mm});
            skArc(sketch, "E2231", {"start": v(-4.67, 8.8) * mm, "mid": v(-4.63, 8.81) * mm, "end": v(-4.62, 8.84) * mm});
            skLineSegment(sketch, "E2232", {"start": v(-4.62, 8.84) * mm, "end": v(-4.62, 9.24) * mm});
            skArc(sketch, "E2233", {"start": v(-4.62, 9.24) * mm, "mid": v(-4.63, 9.27) * mm, "end": v(-4.67, 9.29) * mm});
            skLineSegment(sketch, "E2234", {"start": v(-4.67, 9.29) * mm, "end": v(-5.13, 9.29) * mm});
            skArc(sketch, "E2235", {"start": v(-5.13, 9.29) * mm, "mid": v(-5.17, 9.27) * mm, "end": v(-5.18, 9.24) * mm});
            skLineSegment(sketch, "E2236", {"start": v(-5.18, 9.24) * mm, "end": v(-5.18, 8.84) * mm});
            skArc(sketch, "E2237", {"start": v(-5.18, 8.84) * mm, "mid": v(-5.17, 8.81) * mm, "end": v(-5.13, 8.8) * mm});
            skLineSegment(sketch, "E2238", {"start": v(-5.13, 7.92) * mm, "end": v(-4.67, 7.92) * mm});
            skArc(sketch, "E2239", {"start": v(-4.67, 7.92) * mm, "mid": v(-4.63, 7.93) * mm, "end": v(-4.62, 7.96) * mm});
            skLineSegment(sketch, "E2240", {"start": v(-4.62, 7.96) * mm, "end": v(-4.62, 8.36) * mm});
            skArc(sketch, "E2241", {"start": v(-4.62, 8.36) * mm, "mid": v(-4.63, 8.4) * mm, "end": v(-4.67, 8.4) * mm});
            skLineSegment(sketch, "E2242", {"start": v(-4.67, 8.4) * mm, "end": v(-5.13, 8.4) * mm});
            skArc(sketch, "E2243", {"start": v(-5.13, 8.4) * mm, "mid": v(-5.17, 8.4) * mm, "end": v(-5.18, 8.36) * mm});
            skLineSegment(sketch, "E2244", {"start": v(-5.18, 8.36) * mm, "end": v(-5.18, 7.96) * mm});
            skArc(sketch, "E2245", {"start": v(-5.18, 7.96) * mm, "mid": v(-5.17, 7.93) * mm, "end": v(-5.13, 7.92) * mm});
            skLineSegment(sketch, "E2246", {"start": v(5.13, 8.4) * mm, "end": v(4.67, 8.4) * mm});
            skArc(sketch, "E2247", {"start": v(4.67, 8.4) * mm, "mid": v(4.63, 8.4) * mm, "end": v(4.62, 8.36) * mm});
            skLineSegment(sketch, "E2248", {"start": v(4.62, 8.36) * mm, "end": v(4.62, 7.96) * mm});
            skArc(sketch, "E2249", {"start": v(4.62, 7.96) * mm, "mid": v(4.63, 7.93) * mm, "end": v(4.67, 7.92) * mm});
            skLineSegment(sketch, "E2250", {"start": v(4.67, 7.92) * mm, "end": v(5.13, 7.92) * mm});
            skArc(sketch, "E2251", {"start": v(5.13, 7.92) * mm, "mid": v(5.17, 7.93) * mm, "end": v(5.18, 7.96) * mm});
            skLineSegment(sketch, "E2252", {"start": v(5.18, 7.96) * mm, "end": v(5.18, 8.36) * mm});
            skArc(sketch, "E2253", {"start": v(5.18, 8.36) * mm, "mid": v(5.17, 8.4) * mm, "end": v(5.13, 8.4) * mm});
            skLineSegment(sketch, "E2254", {"start": v(5.13, 9.29) * mm, "end": v(4.67, 9.29) * mm});
            skArc(sketch, "E2255", {"start": v(4.67, 9.29) * mm, "mid": v(4.63, 9.27) * mm, "end": v(4.62, 9.24) * mm});
            skLineSegment(sketch, "E2256", {"start": v(4.62, 9.24) * mm, "end": v(4.62, 8.84) * mm});
            skArc(sketch, "E2257", {"start": v(4.62, 8.84) * mm, "mid": v(4.63, 8.81) * mm, "end": v(4.67, 8.8) * mm});
            skLineSegment(sketch, "E2258", {"start": v(4.67, 8.8) * mm, "end": v(5.13, 8.8) * mm});
            skArc(sketch, "E2259", {"start": v(5.13, 8.8) * mm, "mid": v(5.17, 8.81) * mm, "end": v(5.18, 8.84) * mm});
            skLineSegment(sketch, "E2260", {"start": v(5.18, 8.84) * mm, "end": v(5.18, 9.24) * mm});
            skArc(sketch, "E2261", {"start": v(5.18, 9.24) * mm, "mid": v(5.17, 9.27) * mm, "end": v(5.13, 9.29) * mm});
            skLineSegment(sketch, "E2262", {"start": v(5, -11.47) * mm, "end": v(5, -11.93) * mm});
            skArc(sketch, "E2263", {"start": v(5, -11.93) * mm, "mid": v(5, -11.96) * mm, "end": v(5.04, -11.98) * mm});
            skLineSegment(sketch, "E2264", {"start": v(5.04, -11.98) * mm, "end": v(5.44, -11.98) * mm});
            skArc(sketch, "E2265", {"start": v(5.44, -11.98) * mm, "mid": v(5.47, -11.96) * mm, "end": v(5.48, -11.93) * mm});
            skLineSegment(sketch, "E2266", {"start": v(5.48, -11.93) * mm, "end": v(5.48, -11.47) * mm});
            skArc(sketch, "E2267", {"start": v(5.48, -11.47) * mm, "mid": v(5.47, -11.43) * mm, "end": v(5.44, -11.42) * mm});
            skLineSegment(sketch, "E2268", {"start": v(5.44, -11.42) * mm, "end": v(5.04, -11.42) * mm});
            skArc(sketch, "E2269", {"start": v(5.04, -11.42) * mm, "mid": v(5, -11.43) * mm, "end": v(5, -11.47) * mm});
            skLineSegment(sketch, "E2270", {"start": v(4.12, -11.47) * mm, "end": v(4.12, -11.93) * mm});
            skArc(sketch, "E2271", {"start": v(4.12, -11.93) * mm, "mid": v(4.13, -11.96) * mm, "end": v(4.16, -11.98) * mm});
            skLineSegment(sketch, "E2272", {"start": v(4.16, -11.98) * mm, "end": v(4.56, -11.98) * mm});
            skArc(sketch, "E2273", {"start": v(4.56, -11.98) * mm, "mid": v(4.6, -11.96) * mm, "end": v(4.6, -11.93) * mm});
            skLineSegment(sketch, "E2274", {"start": v(4.6, -11.93) * mm, "end": v(4.6, -11.47) * mm});
            skArc(sketch, "E2275", {"start": v(4.6, -11.47) * mm, "mid": v(4.6, -11.43) * mm, "end": v(4.56, -11.42) * mm});
            skLineSegment(sketch, "E2276", {"start": v(4.56, -11.42) * mm, "end": v(4.16, -11.42) * mm});
            skArc(sketch, "E2277", {"start": v(4.16, -11.42) * mm, "mid": v(4.13, -11.43) * mm, "end": v(4.12, -11.47) * mm});
            skLineSegment(sketch, "E2278", {"start": v(-5.43, -7.4) * mm, "end": v(-4.97, -7.4) * mm});
            skArc(sketch, "E2279", {"start": v(-4.97, -7.4) * mm, "mid": v(-4.93, -7.39) * mm, "end": v(-4.92, -7.36) * mm});
            skLineSegment(sketch, "E2280", {"start": v(-4.92, -7.36) * mm, "end": v(-4.92, -6.96) * mm});
            skArc(sketch, "E2281", {"start": v(-4.92, -6.96) * mm, "mid": v(-4.93, -6.93) * mm, "end": v(-4.97, -6.91) * mm});
            skLineSegment(sketch, "E2282", {"start": v(-4.97, -6.91) * mm, "end": v(-5.43, -6.91) * mm});
            skArc(sketch, "E2283", {"start": v(-5.43, -6.91) * mm, "mid": v(-5.47, -6.93) * mm, "end": v(-5.48, -6.96) * mm});
            skLineSegment(sketch, "E2284", {"start": v(-5.48, -6.96) * mm, "end": v(-5.48, -7.36) * mm});
            skArc(sketch, "E2285", {"start": v(-5.48, -7.36) * mm, "mid": v(-5.47, -7.39) * mm, "end": v(-5.43, -7.4) * mm});
            skLineSegment(sketch, "E2286", {"start": v(-5.43, -8.28) * mm, "end": v(-4.97, -8.28) * mm});
            skArc(sketch, "E2287", {"start": v(-4.97, -8.28) * mm, "mid": v(-4.93, -8.27) * mm, "end": v(-4.92, -8.24) * mm});
            skLineSegment(sketch, "E2288", {"start": v(-4.92, -8.24) * mm, "end": v(-4.92, -7.84) * mm});
            skArc(sketch, "E2289", {"start": v(-4.92, -7.84) * mm, "mid": v(-4.93, -7.8) * mm, "end": v(-4.97, -7.8) * mm});
            skLineSegment(sketch, "E2290", {"start": v(-4.97, -7.8) * mm, "end": v(-5.43, -7.8) * mm});
            skArc(sketch, "E2291", {"start": v(-5.43, -7.8) * mm, "mid": v(-5.47, -7.8) * mm, "end": v(-5.48, -7.84) * mm});
            skLineSegment(sketch, "E2292", {"start": v(-5.48, -7.84) * mm, "end": v(-5.48, -8.24) * mm});
            skArc(sketch, "E2293", {"start": v(-5.48, -8.24) * mm, "mid": v(-5.47, -8.27) * mm, "end": v(-5.43, -8.28) * mm});
            skLineSegment(sketch, "E2294", {"start": v(5.87, -13.6) * mm, "end": v(6.15, -13.97) * mm});
            skArc(sketch, "E2295", {"start": v(6.15, -13.97) * mm, "mid": v(6.18, -13.99) * mm, "end": v(6.21, -13.98) * mm});
            skLineSegment(sketch, "E2296", {"start": v(6.21, -13.98) * mm, "end": v(6.53, -13.75) * mm});
            skArc(sketch, "E2297", {"start": v(6.53, -13.75) * mm, "mid": v(6.55, -13.72) * mm, "end": v(6.54, -13.68) * mm});
            skLineSegment(sketch, "E2298", {"start": v(6.54, -13.68) * mm, "end": v(6.27, -13.3) * mm});
            skArc(sketch, "E2299", {"start": v(6.27, -13.3) * mm, "mid": v(6.24, -13.29) * mm, "end": v(6.2, -13.3) * mm});
            skLineSegment(sketch, "E2300", {"start": v(6.2, -13.3) * mm, "end": v(5.88, -13.53) * mm});
            skArc(sketch, "E2301", {"start": v(5.88, -13.53) * mm, "mid": v(5.86, -13.56) * mm, "end": v(5.87, -13.6) * mm});
            skLineSegment(sketch, "E2302", {"start": v(5.16, -14.11) * mm, "end": v(5.43, -14.49) * mm});
            skArc(sketch, "E2303", {"start": v(5.43, -14.49) * mm, "mid": v(5.46, -14.5) * mm, "end": v(5.5, -14.5) * mm});
            skLineSegment(sketch, "E2304", {"start": v(5.5, -14.5) * mm, "end": v(5.82, -14.27) * mm});
            skArc(sketch, "E2305", {"start": v(5.82, -14.27) * mm, "mid": v(5.84, -14.24) * mm, "end": v(5.83, -14.2) * mm});
            skLineSegment(sketch, "E2306", {"start": v(5.83, -14.2) * mm, "end": v(5.55, -13.82) * mm});
            skArc(sketch, "E2307", {"start": v(5.55, -13.82) * mm, "mid": v(5.52, -13.8) * mm, "end": v(5.49, -13.81) * mm});
            skLineSegment(sketch, "E2308", {"start": v(5.49, -13.81) * mm, "end": v(5.17, -14.05) * mm});
            skArc(sketch, "E2309", {"start": v(5.17, -14.05) * mm, "mid": v(5.15, -14.08) * mm, "end": v(5.16, -14.11) * mm});
            skLineSegment(sketch, "E2310", {"start": v(12.6, -0.61) * mm, "end": v(13.04, -0.47) * mm});
            skArc(sketch, "E2311", {"start": v(13.04, -0.47) * mm, "mid": v(13.07, -0.45) * mm, "end": v(13.07, -0.41) * mm});
            skLineSegment(sketch, "E2312", {"start": v(13.07, -0.41) * mm, "end": v(12.95, -0.03) * mm});
            skArc(sketch, "E2313", {"start": v(12.95, -0.03) * mm, "mid": v(12.93, 0) * mm, "end": v(12.89, 0) * mm});
            skLineSegment(sketch, "E2314", {"start": v(12.89, 0) * mm, "end": v(12.45, -0.15) * mm});
            skArc(sketch, "E2315", {"start": v(12.45, -0.15) * mm, "mid": v(12.42, -0.17) * mm, "end": v(12.42, -0.2) * mm});
            skLineSegment(sketch, "E2316", {"start": v(12.42, -0.2) * mm, "end": v(12.54, -0.58) * mm});
            skArc(sketch, "E2317", {"start": v(12.54, -0.58) * mm, "mid": v(12.56, -0.61) * mm, "end": v(12.6, -0.61) * mm});
            skLineSegment(sketch, "E2318", {"start": v(12.87, -1.45) * mm, "end": v(13.31, -1.3) * mm});
            skArc(sketch, "E2319", {"start": v(13.31, -1.3) * mm, "mid": v(13.34, -1.28) * mm, "end": v(13.34, -1.25) * mm});
            skLineSegment(sketch, "E2320", {"start": v(13.34, -1.25) * mm, "end": v(13.22, -0.87) * mm});
            skArc(sketch, "E2321", {"start": v(13.22, -0.87) * mm, "mid": v(13.2, -0.84) * mm, "end": v(13.16, -0.84) * mm});
            skLineSegment(sketch, "E2322", {"start": v(13.16, -0.84) * mm, "end": v(12.72, -0.99) * mm});
            skArc(sketch, "E2323", {"start": v(12.72, -0.99) * mm, "mid": v(12.7, -1) * mm, "end": v(12.69, -1.04) * mm});
            skLineSegment(sketch, "E2324", {"start": v(12.69, -1.04) * mm, "end": v(12.81, -1.42) * mm});
            skArc(sketch, "E2325", {"start": v(12.81, -1.42) * mm, "mid": v(12.83, -1.45) * mm, "end": v(12.87, -1.45) * mm});
            skLineSegment(sketch, "E2326", {"start": v(-3.7, 5.33) * mm, "end": v(-3.7, 4.87) * mm});
            skArc(sketch, "E2327", {"start": v(-3.7, 4.87) * mm, "mid": v(-3.7, 4.83) * mm, "end": v(-3.66, 4.82) * mm});
            skLineSegment(sketch, "E2328", {"start": v(-3.66, 4.82) * mm, "end": v(-3.26, 4.82) * mm});
            skArc(sketch, "E2329", {"start": v(-3.26, 4.82) * mm, "mid": v(-3.23, 4.83) * mm, "end": v(-3.22, 4.87) * mm});
            skLineSegment(sketch, "E2330", {"start": v(-3.22, 4.87) * mm, "end": v(-3.22, 5.33) * mm});
            skArc(sketch, "E2331", {"start": v(-3.22, 5.33) * mm, "mid": v(-3.23, 5.36) * mm, "end": v(-3.26, 5.38) * mm});
            skLineSegment(sketch, "E2332", {"start": v(-3.26, 5.38) * mm, "end": v(-3.66, 5.38) * mm});
            skArc(sketch, "E2333", {"start": v(-3.66, 5.38) * mm, "mid": v(-3.7, 5.36) * mm, "end": v(-3.7, 5.33) * mm});
            skLineSegment(sketch, "E2334", {"start": v(-4.58, 5.33) * mm, "end": v(-4.58, 4.87) * mm});
            skArc(sketch, "E2335", {"start": v(-4.58, 4.87) * mm, "mid": v(-4.57, 4.83) * mm, "end": v(-4.54, 4.82) * mm});
            skLineSegment(sketch, "E2336", {"start": v(-4.54, 4.82) * mm, "end": v(-4.14, 4.82) * mm});
            skArc(sketch, "E2337", {"start": v(-4.14, 4.82) * mm, "mid": v(-4.1, 4.83) * mm, "end": v(-4.1, 4.87) * mm});
            skLineSegment(sketch, "E2338", {"start": v(-4.1, 4.87) * mm, "end": v(-4.1, 5.33) * mm});
            skArc(sketch, "E2339", {"start": v(-4.1, 5.33) * mm, "mid": v(-4.1, 5.36) * mm, "end": v(-4.14, 5.38) * mm});
            skLineSegment(sketch, "E2340", {"start": v(-4.14, 5.38) * mm, "end": v(-4.54, 5.38) * mm});
            skArc(sketch, "E2341", {"start": v(-4.54, 5.38) * mm, "mid": v(-4.57, 5.36) * mm, "end": v(-4.58, 5.33) * mm});
            skLineSegment(sketch, "E2342", {"start": v(-12.96, -0.54) * mm, "end": v(-12.52, -0.68) * mm});
            skArc(sketch, "E2343", {"start": v(-12.52, -0.68) * mm, "mid": v(-12.48, -0.68) * mm, "end": v(-12.46, -0.65) * mm});
            skLineSegment(sketch, "E2344", {"start": v(-12.46, -0.65) * mm, "end": v(-12.34, -0.28) * mm});
            skArc(sketch, "E2345", {"start": v(-12.34, -0.28) * mm, "mid": v(-12.34, -0.24) * mm, "end": v(-12.37, -0.22) * mm});
            skLineSegment(sketch, "E2346", {"start": v(-12.37, -0.22) * mm, "end": v(-12.8, -0.07) * mm});
            skArc(sketch, "E2347", {"start": v(-12.8, -0.07) * mm, "mid": v(-12.85, -0.08) * mm, "end": v(-12.87, -0.1) * mm});
            skLineSegment(sketch, "E2348", {"start": v(-12.87, -0.1) * mm, "end": v(-13, -0.48) * mm});
            skArc(sketch, "E2349", {"start": v(-13, -0.48) * mm, "mid": v(-12.99, -0.52) * mm, "end": v(-12.96, -0.54) * mm});
            skLineSegment(sketch, "E2350", {"start": v(-13.23, -1.38) * mm, "end": v(-12.8, -1.52) * mm});
            skArc(sketch, "E2351", {"start": v(-12.8, -1.52) * mm, "mid": v(-12.75, -1.52) * mm, "end": v(-12.73, -1.5) * mm});
            skLineSegment(sketch, "E2352", {"start": v(-12.73, -1.5) * mm, "end": v(-12.6, -1.11) * mm});
            skArc(sketch, "E2353", {"start": v(-12.6, -1.11) * mm, "mid": v(-12.61, -1.08) * mm, "end": v(-12.64, -1.06) * mm});
            skLineSegment(sketch, "E2354", {"start": v(-12.64, -1.06) * mm, "end": v(-13.08, -0.91) * mm});
            skArc(sketch, "E2355", {"start": v(-13.08, -0.91) * mm, "mid": v(-13.12, -0.91) * mm, "end": v(-13.14, -0.94) * mm});
            skLineSegment(sketch, "E2356", {"start": v(-13.14, -0.94) * mm, "end": v(-13.26, -1.32) * mm});
            skArc(sketch, "E2357", {"start": v(-13.26, -1.32) * mm, "mid": v(-13.26, -1.35) * mm, "end": v(-13.23, -1.38) * mm});
            skLineSegment(sketch, "E2358", {"start": v(-6.13, -13.94) * mm, "end": v(-5.85, -13.56) * mm});
            skArc(sketch, "E2359", {"start": v(-5.85, -13.56) * mm, "mid": v(-5.84, -13.53) * mm, "end": v(-5.86, -13.5) * mm});
            skLineSegment(sketch, "E2360", {"start": v(-5.86, -13.5) * mm, "end": v(-6.18, -13.27) * mm});
            skArc(sketch, "E2361", {"start": v(-6.18, -13.27) * mm, "mid": v(-6.22, -13.26) * mm, "end": v(-6.25, -13.28) * mm});
            skLineSegment(sketch, "E2362", {"start": v(-6.25, -13.28) * mm, "end": v(-6.52, -13.65) * mm});
            skArc(sketch, "E2363", {"start": v(-6.52, -13.65) * mm, "mid": v(-6.53, -13.69) * mm, "end": v(-6.51, -13.72) * mm});
            skLineSegment(sketch, "E2364", {"start": v(-6.51, -13.72) * mm, "end": v(-6.2, -13.95) * mm});
            skArc(sketch, "E2365", {"start": v(-6.2, -13.95) * mm, "mid": v(-6.16, -13.96) * mm, "end": v(-6.13, -13.94) * mm});
            skLineSegment(sketch, "E2366", {"start": v(-5.41, -14.46) * mm, "end": v(-5.14, -14.08) * mm});
            skArc(sketch, "E2367", {"start": v(-5.14, -14.08) * mm, "mid": v(-5.13, -14.05) * mm, "end": v(-5.15, -14.02) * mm});
            skLineSegment(sketch, "E2368", {"start": v(-5.15, -14.02) * mm, "end": v(-5.47, -13.78) * mm});
            skArc(sketch, "E2369", {"start": v(-5.47, -13.78) * mm, "mid": v(-5.5, -13.78) * mm, "end": v(-5.53, -13.8) * mm});
            skLineSegment(sketch, "E2370", {"start": v(-5.53, -13.8) * mm, "end": v(-5.8, -14.17) * mm});
            skArc(sketch, "E2371", {"start": v(-5.8, -14.17) * mm, "mid": v(-5.82, -14.2) * mm, "end": v(-5.8, -14.24) * mm});
            skLineSegment(sketch, "E2372", {"start": v(-5.8, -14.24) * mm, "end": v(-5.48, -14.47) * mm});
            skArc(sketch, "E2373", {"start": v(-5.48, -14.47) * mm, "mid": v(-5.44, -14.48) * mm, "end": v(-5.41, -14.46) * mm});
            skLineSegment(sketch, "E2374", {"start": v(8.3, -2.97) * mm, "end": v(8.3, -3.43) * mm});
            skArc(sketch, "E2375", {"start": v(8.3, -3.43) * mm, "mid": v(8.3, -3.46) * mm, "end": v(8.34, -3.48) * mm});
            skLineSegment(sketch, "E2376", {"start": v(8.34, -3.48) * mm, "end": v(8.74, -3.48) * mm});
            skArc(sketch, "E2377", {"start": v(8.74, -3.48) * mm, "mid": v(8.77, -3.46) * mm, "end": v(8.78, -3.43) * mm});
            skLineSegment(sketch, "E2378", {"start": v(8.78, -3.43) * mm, "end": v(8.78, -2.97) * mm});
            skArc(sketch, "E2379", {"start": v(8.78, -2.97) * mm, "mid": v(8.77, -2.93) * mm, "end": v(8.74, -2.92) * mm});
            skLineSegment(sketch, "E2380", {"start": v(8.74, -2.92) * mm, "end": v(8.34, -2.92) * mm});
            skArc(sketch, "E2381", {"start": v(8.34, -2.92) * mm, "mid": v(8.3, -2.93) * mm, "end": v(8.3, -2.97) * mm});
            skLineSegment(sketch, "E2382", {"start": v(7.42, -2.97) * mm, "end": v(7.42, -3.43) * mm});
            skArc(sketch, "E2383", {"start": v(7.42, -3.43) * mm, "mid": v(7.43, -3.46) * mm, "end": v(7.46, -3.48) * mm});
            skLineSegment(sketch, "E2384", {"start": v(7.46, -3.48) * mm, "end": v(7.86, -3.48) * mm});
            skArc(sketch, "E2385", {"start": v(7.86, -3.48) * mm, "mid": v(7.9, -3.46) * mm, "end": v(7.9, -3.43) * mm});
            skLineSegment(sketch, "E2386", {"start": v(7.9, -3.43) * mm, "end": v(7.9, -2.97) * mm});
            skArc(sketch, "E2387", {"start": v(7.9, -2.97) * mm, "mid": v(7.9, -2.93) * mm, "end": v(7.86, -2.92) * mm});
            skLineSegment(sketch, "E2388", {"start": v(7.86, -2.92) * mm, "end": v(7.46, -2.92) * mm});
            skArc(sketch, "E2389", {"start": v(7.46, -2.92) * mm, "mid": v(7.43, -2.93) * mm, "end": v(7.42, -2.97) * mm});
            skLineSegment(sketch, "E2390", {"start": v(7.4, 1.67) * mm, "end": v(7.4, 2.13) * mm});
            skArc(sketch, "E2391", {"start": v(7.4, 2.13) * mm, "mid": v(7.4, 2.17) * mm, "end": v(7.36, 2.18) * mm});
            skLineSegment(sketch, "E2392", {"start": v(7.36, 2.18) * mm, "end": v(6.96, 2.18) * mm});
            skArc(sketch, "E2393", {"start": v(6.96, 2.18) * mm, "mid": v(6.93, 2.17) * mm, "end": v(6.92, 2.13) * mm});
            skLineSegment(sketch, "E2394", {"start": v(6.92, 2.13) * mm, "end": v(6.92, 1.67) * mm});
            skArc(sketch, "E2395", {"start": v(6.92, 1.67) * mm, "mid": v(6.93, 1.64) * mm, "end": v(6.96, 1.62) * mm});
            skLineSegment(sketch, "E2396", {"start": v(6.96, 1.62) * mm, "end": v(7.36, 1.62) * mm});
            skArc(sketch, "E2397", {"start": v(7.36, 1.62) * mm, "mid": v(7.4, 1.64) * mm, "end": v(7.4, 1.67) * mm});
            skLineSegment(sketch, "E2398", {"start": v(8.28, 1.67) * mm, "end": v(8.28, 2.13) * mm});
            skArc(sketch, "E2399", {"start": v(8.28, 2.13) * mm, "mid": v(8.27, 2.17) * mm, "end": v(8.24, 2.18) * mm});
            skLineSegment(sketch, "E2400", {"start": v(8.24, 2.18) * mm, "end": v(7.84, 2.18) * mm});
            skArc(sketch, "E2401", {"start": v(7.84, 2.18) * mm, "mid": v(7.8, 2.17) * mm, "end": v(7.8, 2.13) * mm});
            skLineSegment(sketch, "E2402", {"start": v(7.8, 2.13) * mm, "end": v(7.8, 1.67) * mm});
            skArc(sketch, "E2403", {"start": v(7.8, 1.67) * mm, "mid": v(7.8, 1.64) * mm, "end": v(7.84, 1.62) * mm});
            skLineSegment(sketch, "E2404", {"start": v(7.84, 1.62) * mm, "end": v(8.24, 1.62) * mm});
            skArc(sketch, "E2405", {"start": v(8.24, 1.62) * mm, "mid": v(8.27, 1.64) * mm, "end": v(8.28, 1.67) * mm});
            skLineSegment(sketch, "E2406", {"start": v(8.3, -1.77) * mm, "end": v(8.3, -2.23) * mm});
            skArc(sketch, "E2407", {"start": v(8.3, -2.23) * mm, "mid": v(8.3, -2.26) * mm, "end": v(8.34, -2.28) * mm});
            skLineSegment(sketch, "E2408", {"start": v(8.34, -2.28) * mm, "end": v(8.74, -2.28) * mm});
            skArc(sketch, "E2409", {"start": v(8.74, -2.28) * mm, "mid": v(8.77, -2.26) * mm, "end": v(8.78, -2.23) * mm});
            skLineSegment(sketch, "E2410", {"start": v(8.78, -2.23) * mm, "end": v(8.78, -1.77) * mm});
            skArc(sketch, "E2411", {"start": v(8.78, -1.77) * mm, "mid": v(8.77, -1.73) * mm, "end": v(8.74, -1.72) * mm});
            skLineSegment(sketch, "E2412", {"start": v(8.74, -1.72) * mm, "end": v(8.34, -1.72) * mm});
            skArc(sketch, "E2413", {"start": v(8.34, -1.72) * mm, "mid": v(8.3, -1.73) * mm, "end": v(8.3, -1.77) * mm});
            skLineSegment(sketch, "E2414", {"start": v(7.42, -1.77) * mm, "end": v(7.42, -2.23) * mm});
            skArc(sketch, "E2415", {"start": v(7.42, -2.23) * mm, "mid": v(7.43, -2.26) * mm, "end": v(7.46, -2.28) * mm});
            skLineSegment(sketch, "E2416", {"start": v(7.46, -2.28) * mm, "end": v(7.86, -2.28) * mm});
            skArc(sketch, "E2417", {"start": v(7.86, -2.28) * mm, "mid": v(7.9, -2.26) * mm, "end": v(7.9, -2.23) * mm});
            skLineSegment(sketch, "E2418", {"start": v(7.9, -2.23) * mm, "end": v(7.9, -1.77) * mm});
            skArc(sketch, "E2419", {"start": v(7.9, -1.77) * mm, "mid": v(7.9, -1.73) * mm, "end": v(7.86, -1.72) * mm});
            skLineSegment(sketch, "E2420", {"start": v(7.86, -1.72) * mm, "end": v(7.46, -1.72) * mm});
            skArc(sketch, "E2421", {"start": v(7.46, -1.72) * mm, "mid": v(7.43, -1.73) * mm, "end": v(7.42, -1.77) * mm});
            skLineSegment(sketch, "E2422", {"start": v(3.7, 4.87) * mm, "end": v(3.7, 5.33) * mm});
            skArc(sketch, "E2423", {"start": v(3.7, 5.33) * mm, "mid": v(3.7, 5.36) * mm, "end": v(3.66, 5.38) * mm});
            skLineSegment(sketch, "E2424", {"start": v(3.66, 5.38) * mm, "end": v(3.26, 5.38) * mm});
            skArc(sketch, "E2425", {"start": v(3.26, 5.38) * mm, "mid": v(3.23, 5.36) * mm, "end": v(3.22, 5.33) * mm});
            skLineSegment(sketch, "E2426", {"start": v(3.22, 5.33) * mm, "end": v(3.22, 4.87) * mm});
            skArc(sketch, "E2427", {"start": v(3.22, 4.87) * mm, "mid": v(3.23, 4.83) * mm, "end": v(3.26, 4.82) * mm});
            skLineSegment(sketch, "E2428", {"start": v(3.26, 4.82) * mm, "end": v(3.66, 4.82) * mm});
            skArc(sketch, "E2429", {"start": v(3.66, 4.82) * mm, "mid": v(3.7, 4.83) * mm, "end": v(3.7, 4.87) * mm});
            skLineSegment(sketch, "E2430", {"start": v(4.58, 4.87) * mm, "end": v(4.58, 5.33) * mm});
            skArc(sketch, "E2431", {"start": v(4.58, 5.33) * mm, "mid": v(4.57, 5.36) * mm, "end": v(4.54, 5.38) * mm});
            skLineSegment(sketch, "E2432", {"start": v(4.54, 5.38) * mm, "end": v(4.14, 5.38) * mm});
            skArc(sketch, "E2433", {"start": v(4.14, 5.38) * mm, "mid": v(4.1, 5.36) * mm, "end": v(4.1, 5.33) * mm});
            skLineSegment(sketch, "E2434", {"start": v(4.1, 5.33) * mm, "end": v(4.1, 4.87) * mm});
            skArc(sketch, "E2435", {"start": v(4.1, 4.87) * mm, "mid": v(4.1, 4.83) * mm, "end": v(4.14, 4.82) * mm});
            skLineSegment(sketch, "E2436", {"start": v(4.14, 4.82) * mm, "end": v(4.54, 4.82) * mm});
            skArc(sketch, "E2437", {"start": v(4.54, 4.82) * mm, "mid": v(4.57, 4.83) * mm, "end": v(4.58, 4.87) * mm});
            skLineSegment(sketch, "E2438", {"start": v(8.3, -4.17) * mm, "end": v(8.3, -4.63) * mm});
            skArc(sketch, "E2439", {"start": v(8.3, -4.63) * mm, "mid": v(8.3, -4.66) * mm, "end": v(8.34, -4.68) * mm});
            skLineSegment(sketch, "E2440", {"start": v(8.34, -4.68) * mm, "end": v(8.74, -4.68) * mm});
            skArc(sketch, "E2441", {"start": v(8.74, -4.68) * mm, "mid": v(8.77, -4.66) * mm, "end": v(8.78, -4.63) * mm});
            skLineSegment(sketch, "E2442", {"start": v(8.78, -4.63) * mm, "end": v(8.78, -4.17) * mm});
            skArc(sketch, "E2443", {"start": v(8.78, -4.17) * mm, "mid": v(8.77, -4.13) * mm, "end": v(8.74, -4.12) * mm});
            skLineSegment(sketch, "E2444", {"start": v(8.74, -4.12) * mm, "end": v(8.34, -4.12) * mm});
            skArc(sketch, "E2445", {"start": v(8.34, -4.12) * mm, "mid": v(8.3, -4.13) * mm, "end": v(8.3, -4.17) * mm});
            skLineSegment(sketch, "E2446", {"start": v(7.42, -4.17) * mm, "end": v(7.42, -4.63) * mm});
            skArc(sketch, "E2447", {"start": v(7.42, -4.63) * mm, "mid": v(7.43, -4.66) * mm, "end": v(7.46, -4.68) * mm});
            skLineSegment(sketch, "E2448", {"start": v(7.46, -4.68) * mm, "end": v(7.86, -4.68) * mm});
            skArc(sketch, "E2449", {"start": v(7.86, -4.68) * mm, "mid": v(7.9, -4.66) * mm, "end": v(7.9, -4.63) * mm});
            skLineSegment(sketch, "E2450", {"start": v(7.9, -4.63) * mm, "end": v(7.9, -4.17) * mm});
            skArc(sketch, "E2451", {"start": v(7.9, -4.17) * mm, "mid": v(7.9, -4.13) * mm, "end": v(7.86, -4.12) * mm});
            skLineSegment(sketch, "E2452", {"start": v(7.86, -4.12) * mm, "end": v(7.46, -4.12) * mm});
            skArc(sketch, "E2453", {"start": v(7.46, -4.12) * mm, "mid": v(7.43, -4.13) * mm, "end": v(7.42, -4.17) * mm});
            skLineSegment(sketch, "E2454", {"start": v(-20.4, 1.89) * mm, "end": v(-16.97, 0.79) * mm});
            skArc(sketch, "E2455", {"start": v(-17.01, 0.67) * mm, "mid": v(-16.85, 0.75) * mm, "end": v(-16.93, 0.9) * mm});
            skArc(sketch, "E2456", {"start": v(-20.36, 2) * mm, "mid": v(-20.52, 1.93) * mm, "end": v(-20.44, 1.77) * mm});
            skLineSegment(sketch, "E2457", {"start": v(-16.97, 0.79) * mm, "end": v(-16.75, 0.75) * mm});
            skArc(sketch, "E2458", {"start": v(-16.77, 0.63) * mm, "mid": v(-16.63, 0.73) * mm, "end": v(-16.73, 0.87) * mm});
            skArc(sketch, "E2459", {"start": v(-16.95, 0.9) * mm, "mid": v(-17.1, 0.8) * mm, "end": v(-17, 0.66) * mm});
            skLineSegment(sketch, "E2460", {"start": v(-16.75, 0.75) * mm, "end": v(-16.53, 0.74) * mm});
            skArc(sketch, "E2461", {"start": v(-16.53, 0.61) * mm, "mid": v(-16.4, 0.73) * mm, "end": v(-16.52, 0.86) * mm});
            skArc(sketch, "E2462", {"start": v(-16.74, 0.88) * mm, "mid": v(-16.87, 0.76) * mm, "end": v(-16.76, 0.63) * mm});
            skLineSegment(sketch, "E2463", {"start": v(-16.53, 0.74) * mm, "end": v(-16.3, 0.75) * mm});
            skArc(sketch, "E2464", {"start": v(-16.3, 0.62) * mm, "mid": v(-16.18, 0.75) * mm, "end": v(-16.31, 0.87) * mm});
            skArc(sketch, "E2465", {"start": v(-16.53, 0.86) * mm, "mid": v(-16.65, 0.73) * mm, "end": v(-16.52, 0.61) * mm});
            skLineSegment(sketch, "E2466", {"start": v(-16.3, 0.75) * mm, "end": v(-16.1, 0.78) * mm});
            skArc(sketch, "E2467", {"start": v(-16.07, 0.65) * mm, "mid": v(-15.97, 0.8) * mm, "end": v(-16.1, 0.9) * mm});
            skArc(sketch, "E2468", {"start": v(-16.32, 0.87) * mm, "mid": v(-16.43, 0.73) * mm, "end": v(-16.3, 0.62) * mm});
            skLineSegment(sketch, "E2469", {"start": v(-16.1, 0.78) * mm, "end": v(-15.88, 0.83) * mm});
            skArc(sketch, "E2470", {"start": v(-15.85, 0.7) * mm, "mid": v(-15.76, 0.86) * mm, "end": v(-15.91, 0.95) * mm});
            skArc(sketch, "E2471", {"start": v(-16.12, 0.9) * mm, "mid": v(-16.21, 0.75) * mm, "end": v(-16.06, 0.66) * mm});
            skLineSegment(sketch, "E2472", {"start": v(-15.88, 0.83) * mm, "end": v(-15.68, 0.9) * mm});
            skArc(sketch, "E2473", {"start": v(-15.64, 0.78) * mm, "mid": v(-15.56, 0.94) * mm, "end": v(-15.72, 1.02) * mm});
            skArc(sketch, "E2474", {"start": v(-15.92, 0.95) * mm, "mid": v(-16, 0.79) * mm, "end": v(-15.84, 0.71) * mm});
            skLineSegment(sketch, "E2475", {"start": v(-15.68, 0.9) * mm, "end": v(-15.48, 0.99) * mm});
            skArc(sketch, "E2476", {"start": v(-15.43, 0.88) * mm, "mid": v(-15.37, 1.04) * mm, "end": v(-15.53, 1.1) * mm});
            skArc(sketch, "E2477", {"start": v(-15.73, 1.01) * mm, "mid": v(-15.79, 0.85) * mm, "end": v(-15.62, 0.79) * mm});
            skLineSegment(sketch, "E2478", {"start": v(-15.48, 0.99) * mm, "end": v(-15.3, 1.1) * mm});
            skArc(sketch, "E2479", {"start": v(-15.23, 0.99) * mm, "mid": v(-15.18, 1.16) * mm, "end": v(-15.36, 1.2) * mm});
            skArc(sketch, "E2480", {"start": v(-15.54, 1.1) * mm, "mid": v(-15.59, 0.93) * mm, "end": v(-15.42, 0.88) * mm});
            skLineSegment(sketch, "E2481", {"start": v(-15.3, 1.1) * mm, "end": v(-15.12, 1.22) * mm});
            skArc(sketch, "E2482", {"start": v(-15.04, 1.12) * mm, "mid": v(-15.01, 1.3) * mm, "end": v(-15.19, 1.33) * mm});
            skArc(sketch, "E2483", {"start": v(-15.37, 1.2) * mm, "mid": v(-15.4, 1.02) * mm, "end": v(-15.22, 1) * mm});
            skLineSegment(sketch, "E2484", {"start": v(-15.12, 1.22) * mm, "end": v(-14.95, 1.37) * mm});
            skArc(sketch, "E2485", {"start": v(-14.87, 1.27) * mm, "mid": v(-14.86, 1.45) * mm, "end": v(-15.03, 1.46) * mm});
            skArc(sketch, "E2486", {"start": v(-15.2, 1.32) * mm, "mid": v(-15.21, 1.14) * mm, "end": v(-15.03, 1.13) * mm});
            skLineSegment(sketch, "E2487", {"start": v(-14.95, 1.37) * mm, "end": v(-14.8, 1.52) * mm});
            skArc(sketch, "E2488", {"start": v(-14.71, 1.44) * mm, "mid": v(-14.72, 1.62) * mm, "end": v(-14.9, 1.61) * mm});
            skArc(sketch, "E2489", {"start": v(-15.04, 1.45) * mm, "mid": v(-15.04, 1.27) * mm, "end": v(-14.86, 1.28) * mm});
            skLineSegment(sketch, "E2490", {"start": v(-14.8, 1.52) * mm, "end": v(-14.67, 1.7) * mm});
            skArc(sketch, "E2491", {"start": v(-14.57, 1.62) * mm, "mid": v(-14.6, 1.8) * mm, "end": v(-14.77, 1.77) * mm});
            skArc(sketch, "E2492", {"start": v(-14.9, 1.6) * mm, "mid": v(-14.88, 1.43) * mm, "end": v(-14.7, 1.45) * mm});
            skLineSegment(sketch, "E2493", {"start": v(-14.67, 1.7) * mm, "end": v(-14.55, 1.89) * mm});
            skArc(sketch, "E2494", {"start": v(-14.44, 1.82) * mm, "mid": v(-14.48, 2) * mm, "end": v(-14.66, 1.95) * mm});
            skArc(sketch, "E2495", {"start": v(-14.77, 1.76) * mm, "mid": v(-14.73, 1.6) * mm, "end": v(-14.56, 1.63) * mm});
            skLineSegment(sketch, "E2496", {"start": v(-14.55, 1.89) * mm, "end": v(-14.45, 2.09) * mm});
            skArc(sketch, "E2497", {"start": v(-14.34, 2.03) * mm, "mid": v(-14.4, 2.2) * mm, "end": v(-14.56, 2.15) * mm});
            skArc(sketch, "E2498", {"start": v(-14.66, 1.94) * mm, "mid": v(-14.6, 1.77) * mm, "end": v(-14.44, 1.83) * mm});
            skLineSegment(sketch, "E2499", {"start": v(-14.45, 2.09) * mm, "end": v(-14.37, 2.3) * mm});
            skArc(sketch, "E2500", {"start": v(-14.26, 2.25) * mm, "mid": v(-14.33, 2.4) * mm, "end": v(-14.49, 2.34) * mm});
            skArc(sketch, "E2501", {"start": v(-14.57, 2.13) * mm, "mid": v(-14.5, 1.97) * mm, "end": v(-14.33, 2.05) * mm});
            skLineSegment(sketch, "E2502", {"start": v(-14.37, 2.3) * mm, "end": v(-14.3, 2.53) * mm});
            skArc(sketch, "E2503", {"start": v(-14.19, 2.5) * mm, "mid": v(-14.28, 2.65) * mm, "end": v(-14.43, 2.56) * mm});
            skArc(sketch, "E2504", {"start": v(-14.5, 2.33) * mm, "mid": v(-14.4, 2.17) * mm, "end": v(-14.25, 2.26) * mm});
            skLineSegment(sketch, "E2505", {"start": v(-14.3, 2.53) * mm, "end": v(-14.27, 2.75) * mm});
            skArc(sketch, "E2506", {"start": v(-14.15, 2.73) * mm, "mid": v(-14.25, 2.88) * mm, "end": v(-14.4, 2.77) * mm});
            skArc(sketch, "E2507", {"start": v(-14.43, 2.55) * mm, "mid": v(-14.33, 2.4) * mm, "end": v(-14.19, 2.5) * mm});
            skLineSegment(sketch, "E2508", {"start": v(-14.27, 2.75) * mm, "end": v(-14.26, 2.97) * mm});
            skArc(sketch, "E2509", {"start": v(-14.14, 2.97) * mm, "mid": v(-14.25, 3.1) * mm, "end": v(-14.39, 2.98) * mm});
            skArc(sketch, "E2510", {"start": v(-14.4, 2.76) * mm, "mid": v(-14.28, 2.63) * mm, "end": v(-14.15, 2.74) * mm});
            skLineSegment(sketch, "E2511", {"start": v(-14.26, 2.97) * mm, "end": v(-14.27, 3.2) * mm});
            skArc(sketch, "E2512", {"start": v(-14.15, 3.2) * mm, "mid": v(-14.28, 3.32) * mm, "end": v(-14.4, 3.19) * mm});
            skArc(sketch, "E2513", {"start": v(-14.39, 2.97) * mm, "mid": v(-14.26, 2.85) * mm, "end": v(-14.14, 2.98) * mm});
            skLineSegment(sketch, "E2514", {"start": v(-14.27, 3.2) * mm, "end": v(-14.3, 3.4) * mm});
            skArc(sketch, "E2515", {"start": v(-14.18, 3.43) * mm, "mid": v(-14.32, 3.53) * mm, "end": v(-14.42, 3.4) * mm});
            skArc(sketch, "E2516", {"start": v(-14.4, 3.18) * mm, "mid": v(-14.25, 3.07) * mm, "end": v(-14.15, 3.21) * mm});
            skLineSegment(sketch, "E2517", {"start": v(-14.3, 3.4) * mm, "end": v(-14.35, 3.62) * mm});
            skArc(sketch, "E2518", {"start": v(-14.23, 3.65) * mm, "mid": v(-14.38, 3.74) * mm, "end": v(-14.47, 3.6) * mm});
            skArc(sketch, "E2519", {"start": v(-14.42, 3.38) * mm, "mid": v(-14.27, 3.29) * mm, "end": v(-14.18, 3.44) * mm});
            skLineSegment(sketch, "E2520", {"start": v(-14.35, 3.62) * mm, "end": v(-14.42, 3.82) * mm});
            skArc(sketch, "E2521", {"start": v(-14.3, 3.87) * mm, "mid": v(-14.46, 3.94) * mm, "end": v(-14.54, 3.78) * mm});
            skArc(sketch, "E2522", {"start": v(-14.47, 3.58) * mm, "mid": v(-14.31, 3.5) * mm, "end": v(-14.23, 3.66) * mm});
            skLineSegment(sketch, "E2523", {"start": v(-14.42, 3.82) * mm, "end": v(-14.51, 4.02) * mm});
            skArc(sketch, "E2524", {"start": v(-14.4, 4.07) * mm, "mid": v(-14.56, 4.13) * mm, "end": v(-14.63, 3.97) * mm});
            skArc(sketch, "E2525", {"start": v(-14.54, 3.77) * mm, "mid": v(-14.37, 3.71) * mm, "end": v(-14.3, 3.88) * mm});
            skLineSegment(sketch, "E2526", {"start": v(-14.51, 4.02) * mm, "end": v(-14.62, 4.2) * mm});
            skArc(sketch, "E2527", {"start": v(-14.51, 4.27) * mm, "mid": v(-14.68, 4.32) * mm, "end": v(-14.73, 4.15) * mm});
            skArc(sketch, "E2528", {"start": v(-14.62, 3.96) * mm, "mid": v(-14.45, 3.91) * mm, "end": v(-14.4, 4.08) * mm});
            skLineSegment(sketch, "E2529", {"start": v(-14.62, 4.2) * mm, "end": v(-14.75, 4.38) * mm});
            skArc(sketch, "E2530", {"start": v(-14.64, 4.46) * mm, "mid": v(-14.82, 4.49) * mm, "end": v(-14.85, 4.31) * mm});
            skArc(sketch, "E2531", {"start": v(-14.72, 4.14) * mm, "mid": v(-14.55, 4.1) * mm, "end": v(-14.52, 4.28) * mm});
            skLineSegment(sketch, "E2532", {"start": v(-14.75, 4.38) * mm, "end": v(-14.89, 4.55) * mm});
            skArc(sketch, "E2533", {"start": v(-14.8, 4.63) * mm, "mid": v(-14.97, 4.64) * mm, "end": v(-14.98, 4.47) * mm});
            skArc(sketch, "E2534", {"start": v(-14.84, 4.3) * mm, "mid": v(-14.66, 4.29) * mm, "end": v(-14.65, 4.47) * mm});
            skLineSegment(sketch, "E2535", {"start": v(-14.89, 4.55) * mm, "end": v(-15.05, 4.7) * mm});
            skArc(sketch, "E2536", {"start": v(-14.96, 4.79) * mm, "mid": v(-15.14, 4.78) * mm, "end": v(-15.13, 4.6) * mm});
            skArc(sketch, "E2537", {"start": v(-14.97, 4.46) * mm, "mid": v(-14.8, 4.46) * mm, "end": v(-14.8, 4.64) * mm});
            skLineSegment(sketch, "E2538", {"start": v(-15.05, 4.7) * mm, "end": v(-15.22, 4.83) * mm});
            skArc(sketch, "E2539", {"start": v(-15.14, 4.93) * mm, "mid": v(-15.32, 4.9) * mm, "end": v(-15.3, 4.73) * mm});
            skArc(sketch, "E2540", {"start": v(-15.12, 4.6) * mm, "mid": v(-14.95, 4.62) * mm, "end": v(-14.97, 4.8) * mm});
            skLineSegment(sketch, "E2541", {"start": v(-15.22, 4.83) * mm, "end": v(-15.41, 4.95) * mm});
            skArc(sketch, "E2542", {"start": v(-15.34, 5.06) * mm, "mid": v(-15.52, 5.02) * mm, "end": v(-15.48, 4.85) * mm});
            skArc(sketch, "E2543", {"start": v(-15.29, 4.73) * mm, "mid": v(-15.12, 4.77) * mm, "end": v(-15.16, 4.94) * mm});
            skLineSegment(sketch, "E2544", {"start": v(-15.41, 4.95) * mm, "end": v(-15.61, 5.05) * mm});
            skArc(sketch, "E2545", {"start": v(-15.56, 5.16) * mm, "mid": v(-15.72, 5.1) * mm, "end": v(-15.67, 4.94) * mm});
            skArc(sketch, "E2546", {"start": v(-15.47, 4.84) * mm, "mid": v(-15.3, 4.9) * mm, "end": v(-15.35, 5.06) * mm});
            skLineSegment(sketch, "E2547", {"start": v(-15.61, 5.05) * mm, "end": v(-15.84, 5.14) * mm});
            skArc(sketch, "E2548", {"start": v(-15.8, 5.26) * mm, "mid": v(-15.96, 5.18) * mm, "end": v(-15.89, 5.02) * mm});
            skArc(sketch, "E2549", {"start": v(-15.66, 4.93) * mm, "mid": v(-15.5, 5) * mm, "end": v(-15.57, 5.17) * mm});
            skLineSegment(sketch, "E2550", {"start": v(-15.84, 5.14) * mm, "end": v(-19.01, 6.17) * mm});
            skArc(sketch, "E2551", {"start": v(-18.97, 6.29) * mm, "mid": v(-19.13, 6.2) * mm, "end": v(-19.05, 6.05) * mm});
            skArc(sketch, "E2552", {"start": v(-15.88, 5.02) * mm, "mid": v(-15.73, 5.1) * mm, "end": v(-15.8, 5.26) * mm});
            skLineSegment(sketch, "E2553", {"start": v(-19.01, 6.17) * mm, "end": v(-21.34, 6.17) * mm});
            skArc(sketch, "E2554", {"start": v(-21.34, 6.3) * mm, "mid": v(-21.47, 6.17) * mm, "end": v(-21.34, 6.04) * mm});
            skArc(sketch, "E2555", {"start": v(-19.01, 6.04) * mm, "mid": v(-18.89, 6.17) * mm, "end": v(-19.01, 6.3) * mm});
            skLineSegment(sketch, "E2556", {"start": v(-21.34, 6.17) * mm, "end": v(-22.36, 5.9) * mm});
            skArc(sketch, "E2557", {"start": v(-22.4, 6.01) * mm, "mid": v(-22.48, 5.86) * mm, "end": v(-22.33, 5.77) * mm});
            skArc(sketch, "E2558", {"start": v(-21.3, 6.05) * mm, "mid": v(-21.22, 6.2) * mm, "end": v(-21.37, 6.29) * mm});
            skLineSegment(sketch, "E2559", {"start": v(-22.36, 5.9) * mm, "end": v(-22.95, 4.08) * mm});
            skArc(sketch, "E2560", {"start": v(-23.07, 4.12) * mm, "mid": v(-22.99, 3.96) * mm, "end": v(-22.83, 4.04) * mm});
            skArc(sketch, "E2561", {"start": v(-22.24, 5.85) * mm, "mid": v(-22.32, 6.01) * mm, "end": v(-22.48, 5.93) * mm});
            skLineSegment(sketch, "E2562", {"start": v(-22.95, 4.08) * mm, "end": v(-22.29, 3.26) * mm});
            skArc(sketch, "E2563", {"start": v(-22.38, 3.18) * mm, "mid": v(-22.2, 3.16) * mm, "end": v(-22.19, 3.34) * mm});
            skArc(sketch, "E2564", {"start": v(-22.85, 4.16) * mm, "mid": v(-23.03, 4.18) * mm, "end": v(-23.05, 4) * mm});
            skLineSegment(sketch, "E2565", {"start": v(-22.29, 3.26) * mm, "end": v(-20.4, 1.89) * mm});
            skArc(sketch, "E2566", {"start": v(-20.47, 1.79) * mm, "mid": v(-20.3, 1.81) * mm, "end": v(-20.33, 1.99) * mm});
            skArc(sketch, "E2567", {"start": v(-22.21, 3.36) * mm, "mid": v(-22.39, 3.33) * mm, "end": v(-22.36, 3.16) * mm});
            skLineSegment(sketch, "E2568", {"start": v(-14.93, 1.4) * mm, "end": v(-14.3, 3.35) * mm});
            skArc(sketch, "E2569", {"start": v(-14.17, 3.31) * mm, "mid": v(-14.25, 3.47) * mm, "end": v(-14.41, 3.39) * mm});
            skArc(sketch, "E2570", {"start": v(-15.05, 1.43) * mm, "mid": v(-14.97, 1.27) * mm, "end": v(-14.8, 1.35) * mm});
            skLineSegment(sketch, "E2571", {"start": v(-15.6, 0.93) * mm, "end": v(-14.57, 4.12) * mm});
            skArc(sketch, "E2572", {"start": v(-14.45, 4.08) * mm, "mid": v(-14.53, 4.24) * mm, "end": v(-14.69, 4.16) * mm});
            skArc(sketch, "E2573", {"start": v(-15.72, 0.97) * mm, "mid": v(-15.64, 0.81) * mm, "end": v(-15.48, 0.9) * mm});
            skLineSegment(sketch, "E2574", {"start": v(-16.18, 0.76) * mm, "end": v(-14.94, 4.6) * mm});
            skArc(sketch, "E2575", {"start": v(-14.82, 4.56) * mm, "mid": v(-14.9, 4.71) * mm, "end": v(-15.06, 4.63) * mm});
            skArc(sketch, "E2576", {"start": v(-16.3, 0.8) * mm, "mid": v(-16.22, 0.65) * mm, "end": v(-16.06, 0.73) * mm});
            skLineSegment(sketch, "E2577", {"start": v(-16.71, 0.75) * mm, "end": v(-15.36, 4.92) * mm});
            skArc(sketch, "E2578", {"start": v(-15.24, 4.88) * mm, "mid": v(-15.32, 5.04) * mm, "end": v(-15.48, 4.96) * mm});
            skArc(sketch, "E2579", {"start": v(-16.83, 0.79) * mm, "mid": v(-16.75, 0.63) * mm, "end": v(-16.6, 0.7) * mm});
            skLineSegment(sketch, "E2580", {"start": v(-17.2, 0.86) * mm, "end": v(-15.82, 5.13) * mm});
            skArc(sketch, "E2581", {"start": v(-15.7, 5.09) * mm, "mid": v(-15.78, 5.25) * mm, "end": v(-15.94, 5.17) * mm});
            skArc(sketch, "E2582", {"start": v(-17.32, 0.9) * mm, "mid": v(-17.24, 0.74) * mm, "end": v(-17.09, 0.82) * mm});
            skLineSegment(sketch, "E2583", {"start": v(-17.68, 1.01) * mm, "end": v(-16.3, 5.28) * mm});
            skArc(sketch, "E2584", {"start": v(-16.17, 5.25) * mm, "mid": v(-16.25, 5.4) * mm, "end": v(-16.41, 5.32) * mm});
            skArc(sketch, "E2585", {"start": v(-17.8, 1.05) * mm, "mid": v(-17.72, 0.9) * mm, "end": v(-17.56, 0.97) * mm});
            skLineSegment(sketch, "E2586", {"start": v(-18.16, 1.17) * mm, "end": v(-16.77, 5.44) * mm});
            skArc(sketch, "E2587", {"start": v(-16.65, 5.4) * mm, "mid": v(-16.73, 5.56) * mm, "end": v(-16.89, 5.48) * mm});
            skArc(sketch, "E2588", {"start": v(-18.27, 1.2) * mm, "mid": v(-18.2, 1.05) * mm, "end": v(-18.04, 1.13) * mm});
            skLineSegment(sketch, "E2589", {"start": v(-18.63, 1.32) * mm, "end": v(-17.24, 5.6) * mm});
            skArc(sketch, "E2590", {"start": v(-17.12, 5.55) * mm, "mid": v(-17.2, 5.71) * mm, "end": v(-17.36, 5.63) * mm});
            skArc(sketch, "E2591", {"start": v(-18.75, 1.36) * mm, "mid": v(-18.67, 1.2) * mm, "end": v(-18.51, 1.28) * mm});
            skLineSegment(sketch, "E2592", {"start": v(-19.1, 1.47) * mm, "end": v(-17.72, 5.75) * mm});
            skArc(sketch, "E2593", {"start": v(-17.6, 5.7) * mm, "mid": v(-17.68, 5.87) * mm, "end": v(-17.84, 5.79) * mm});
            skArc(sketch, "E2594", {"start": v(-19.23, 1.51) * mm, "mid": v(-19.15, 1.35) * mm, "end": v(-18.99, 1.43) * mm});
            skLineSegment(sketch, "E2595", {"start": v(-19.58, 1.63) * mm, "end": v(-18.2, 5.9) * mm});
            skArc(sketch, "E2596", {"start": v(-18.08, 5.86) * mm, "mid": v(-18.16, 6.02) * mm, "end": v(-18.31, 5.94) * mm});
            skArc(sketch, "E2597", {"start": v(-19.7, 1.66) * mm, "mid": v(-19.62, 1.5) * mm, "end": v(-19.47, 1.59) * mm});
            skLineSegment(sketch, "E2598", {"start": v(-20.06, 1.78) * mm, "end": v(-18.67, 6.06) * mm});
            skArc(sketch, "E2599", {"start": v(-18.55, 6.02) * mm, "mid": v(-18.63, 6.18) * mm, "end": v(-18.79, 6.1) * mm});
            skArc(sketch, "E2600", {"start": v(-20.18, 1.82) * mm, "mid": v(-20.1, 1.66) * mm, "end": v(-19.94, 1.74) * mm});
            skLineSegment(sketch, "E2601", {"start": v(-20.52, 1.98) * mm, "end": v(-19.16, 6.17) * mm});
            skArc(sketch, "E2602", {"start": v(-19.04, 6.13) * mm, "mid": v(-19.12, 6.29) * mm, "end": v(-19.28, 6.2) * mm});
            skArc(sketch, "E2603", {"start": v(-20.64, 2.01) * mm, "mid": v(-20.56, 1.86) * mm, "end": v(-20.4, 1.94) * mm});
            skLineSegment(sketch, "E2604", {"start": v(-20.95, 2.28) * mm, "end": v(-19.69, 6.17) * mm});
            skArc(sketch, "E2605", {"start": v(-19.57, 6.13) * mm, "mid": v(-19.65, 6.29) * mm, "end": v(-19.8, 6.2) * mm});
            skArc(sketch, "E2606", {"start": v(-21.07, 2.32) * mm, "mid": v(-20.99, 2.17) * mm, "end": v(-20.83, 2.25) * mm});
            skLineSegment(sketch, "E2607", {"start": v(-21.37, 2.6) * mm, "end": v(-20.21, 6.17) * mm});
            skArc(sketch, "E2608", {"start": v(-20.1, 6.13) * mm, "mid": v(-20.17, 6.29) * mm, "end": v(-20.33, 6.2) * mm});
            skArc(sketch, "E2609", {"start": v(-21.5, 2.63) * mm, "mid": v(-21.41, 2.48) * mm, "end": v(-21.25, 2.56) * mm});
            skLineSegment(sketch, "E2610", {"start": v(-21.8, 2.9) * mm, "end": v(-20.74, 6.17) * mm});
            skArc(sketch, "E2611", {"start": v(-20.62, 6.13) * mm, "mid": v(-20.7, 6.29) * mm, "end": v(-20.86, 6.2) * mm});
            skArc(sketch, "E2612", {"start": v(-21.92, 2.94) * mm, "mid": v(-21.84, 2.78) * mm, "end": v(-21.68, 2.86) * mm});
            skLineSegment(sketch, "E2613", {"start": v(-22.22, 3.21) * mm, "end": v(-21.26, 6.17) * mm});
            skArc(sketch, "E2614", {"start": v(-21.14, 6.13) * mm, "mid": v(-21.22, 6.29) * mm, "end": v(-21.38, 6.2) * mm});
            skArc(sketch, "E2615", {"start": v(-22.34, 3.25) * mm, "mid": v(-22.26, 3.1) * mm, "end": v(-22.1, 3.17) * mm});
            skLineSegment(sketch, "E2616", {"start": v(-22.6, 3.65) * mm, "end": v(-21.83, 6.04) * mm});
            skArc(sketch, "E2617", {"start": v(-21.71, 6) * mm, "mid": v(-21.8, 6.15) * mm, "end": v(-21.95, 6.07) * mm});
            skArc(sketch, "E2618", {"start": v(-22.72, 3.7) * mm, "mid": v(-22.64, 3.53) * mm, "end": v(-22.49, 3.61) * mm});
            skLineSegment(sketch, "E2619", {"start": v(-30, 4.81) * mm, "end": v(-29.88, 4.88) * mm});
            skArc(sketch, "E2620", {"start": v(-29.86, 4.83) * mm, "mid": v(-29.83, 4.9) * mm, "end": v(-29.9, 4.92) * mm});
            skArc(sketch, "E2621", {"start": v(-30.03, 4.86) * mm, "mid": v(-30.05, 4.79) * mm, "end": v(-29.98, 4.77) * mm});
            skLineSegment(sketch, "E2622", {"start": v(-29.88, 4.88) * mm, "end": v(-29.75, 4.97) * mm});
            skArc(sketch, "E2623", {"start": v(-29.72, 4.93) * mm, "mid": v(-29.71, 5) * mm, "end": v(-29.78, 5.01) * mm});
            skArc(sketch, "E2624", {"start": v(-29.9, 4.92) * mm, "mid": v(-29.92, 4.85) * mm, "end": v(-29.85, 4.84) * mm});
            skLineSegment(sketch, "E2625", {"start": v(-29.75, 4.97) * mm, "end": v(-29.65, 5.08) * mm});
            skArc(sketch, "E2626", {"start": v(-29.61, 5.05) * mm, "mid": v(-29.61, 5.12) * mm, "end": v(-29.68, 5.12) * mm});
            skArc(sketch, "E2627", {"start": v(-29.8, 5) * mm, "mid": v(-29.79, 4.93) * mm, "end": v(-29.72, 4.94) * mm});
            skLineSegment(sketch, "E2628", {"start": v(-29.65, 5.08) * mm, "end": v(-29.56, 5.22) * mm});
            skArc(sketch, "E2629", {"start": v(-29.52, 5.2) * mm, "mid": v(-29.53, 5.26) * mm, "end": v(-29.6, 5.24) * mm});
            skArc(sketch, "E2630", {"start": v(-29.69, 5.11) * mm, "mid": v(-29.68, 5.04) * mm, "end": v(-29.6, 5.06) * mm});
            skLineSegment(sketch, "E2631", {"start": v(-29.56, 5.22) * mm, "end": v(-29.53, 5.29) * mm});
            skArc(sketch, "E2632", {"start": v(-29.48, 5.27) * mm, "mid": v(-29.5, 5.34) * mm, "end": v(-29.57, 5.31) * mm});
            skArc(sketch, "E2633", {"start": v(-29.6, 5.24) * mm, "mid": v(-29.58, 5.17) * mm, "end": v(-29.52, 5.2) * mm});
            skLineSegment(sketch, "E2634", {"start": v(-29.53, 5.29) * mm, "end": v(-28.38, 8.86) * mm});
            skArc(sketch, "E2635", {"start": v(-28.33, 8.85) * mm, "mid": v(-28.36, 8.91) * mm, "end": v(-28.43, 8.88) * mm});
            skArc(sketch, "E2636", {"start": v(-29.57, 5.3) * mm, "mid": v(-29.54, 5.24) * mm, "end": v(-29.48, 5.27) * mm});
            skLineSegment(sketch, "E2637", {"start": v(-28.38, 8.86) * mm, "end": v(-28.37, 9.02) * mm});
            skArc(sketch, "E2638", {"start": v(-28.32, 9.02) * mm, "mid": v(-28.37, 9.07) * mm, "end": v(-28.42, 9.02) * mm});
            skArc(sketch, "E2639", {"start": v(-28.43, 8.87) * mm, "mid": v(-28.38, 8.81) * mm, "end": v(-28.33, 8.86) * mm});
            skLineSegment(sketch, "E2640", {"start": v(-28.37, 9.02) * mm, "end": v(-28.4, 9.18) * mm});
            skArc(sketch, "E2641", {"start": v(-28.34, 9.18) * mm, "mid": v(-28.4, 9.23) * mm, "end": v(-28.44, 9.17) * mm});
            skArc(sketch, "E2642", {"start": v(-28.42, 9.01) * mm, "mid": v(-28.37, 8.97) * mm, "end": v(-28.32, 9.03) * mm});
            skLineSegment(sketch, "E2643", {"start": v(-28.4, 9.18) * mm, "end": v(-28.44, 9.32) * mm});
            skArc(sketch, "E2644", {"start": v(-28.4, 9.34) * mm, "mid": v(-28.45, 9.37) * mm, "end": v(-28.49, 9.3) * mm});
            skArc(sketch, "E2645", {"start": v(-28.44, 9.16) * mm, "mid": v(-28.38, 9.13) * mm, "end": v(-28.35, 9.2) * mm});
            skLineSegment(sketch, "E2646", {"start": v(-28.44, 9.32) * mm, "end": v(-28.5, 9.44) * mm});
            skArc(sketch, "E2647", {"start": v(-28.45, 9.46) * mm, "mid": v(-28.52, 9.49) * mm, "end": v(-28.54, 9.42) * mm});
            skArc(sketch, "E2648", {"start": v(-28.48, 9.3) * mm, "mid": v(-28.42, 9.28) * mm, "end": v(-28.4, 9.35) * mm});
            skLineSegment(sketch, "E2649", {"start": v(-28.5, 9.44) * mm, "end": v(-28.62, 9.38) * mm});
            skArc(sketch, "E2650", {"start": v(-28.65, 9.42) * mm, "mid": v(-28.67, 9.35) * mm, "end": v(-28.6, 9.33) * mm});
            skArc(sketch, "E2651", {"start": v(-28.48, 9.4) * mm, "mid": v(-28.45, 9.46) * mm, "end": v(-28.52, 9.49) * mm});
            skLineSegment(sketch, "E2652", {"start": v(-28.62, 9.38) * mm, "end": v(-28.75, 9.28) * mm});
            skArc(sketch, "E2653", {"start": v(-28.78, 9.32) * mm, "mid": v(-28.79, 9.25) * mm, "end": v(-28.72, 9.24) * mm});
            skArc(sketch, "E2654", {"start": v(-28.6, 9.34) * mm, "mid": v(-28.58, 9.4) * mm, "end": v(-28.65, 9.42) * mm});
            skLineSegment(sketch, "E2655", {"start": v(-28.75, 9.28) * mm, "end": v(-28.86, 9.17) * mm});
            skArc(sketch, "E2656", {"start": v(-28.9, 9.2) * mm, "mid": v(-28.89, 9.13) * mm, "end": v(-28.82, 9.13) * mm});
            skArc(sketch, "E2657", {"start": v(-28.71, 9.25) * mm, "mid": v(-28.71, 9.32) * mm, "end": v(-28.79, 9.32) * mm});
            skLineSegment(sketch, "E2658", {"start": v(-28.86, 9.17) * mm, "end": v(-28.94, 9.04) * mm});
            skArc(sketch, "E2659", {"start": v(-28.98, 9.06) * mm, "mid": v(-28.97, 9) * mm, "end": v(-28.9, 9) * mm});
            skArc(sketch, "E2660", {"start": v(-28.81, 9.14) * mm, "mid": v(-28.83, 9.21) * mm, "end": v(-28.9, 9.2) * mm});
            skLineSegment(sketch, "E2661", {"start": v(-28.94, 9.04) * mm, "end": v(-28.98, 8.96) * mm});
            skArc(sketch, "E2662", {"start": v(-29.02, 8.99) * mm, "mid": v(-29, 8.92) * mm, "end": v(-28.93, 8.94) * mm});
            skArc(sketch, "E2663", {"start": v(-28.9, 9.01) * mm, "mid": v(-28.92, 9.08) * mm, "end": v(-28.99, 9.06) * mm});
            skLineSegment(sketch, "E2664", {"start": v(-28.98, 8.96) * mm, "end": v(-30.12, 5.39) * mm});
            skArc(sketch, "E2665", {"start": v(-30.17, 5.4) * mm, "mid": v(-30.14, 5.34) * mm, "end": v(-30.08, 5.37) * mm});
            skArc(sketch, "E2666", {"start": v(-28.93, 8.95) * mm, "mid": v(-28.96, 9.01) * mm, "end": v(-29.02, 8.98) * mm});
            skLineSegment(sketch, "E2667", {"start": v(-30.12, 5.39) * mm, "end": v(-30.13, 5.23) * mm});
            skArc(sketch, "E2668", {"start": v(-30.18, 5.23) * mm, "mid": v(-30.13, 5.18) * mm, "end": v(-30.08, 5.23) * mm});
            skArc(sketch, "E2669", {"start": v(-30.07, 5.39) * mm, "mid": v(-30.12, 5.44) * mm, "end": v(-30.17, 5.4) * mm});
            skLineSegment(sketch, "E2670", {"start": v(-30.13, 5.23) * mm, "end": v(-30.11, 5.08) * mm});
            skArc(sketch, "E2671", {"start": v(-30.16, 5.07) * mm, "mid": v(-30.1, 5.03) * mm, "end": v(-30.06, 5.08) * mm});
            skArc(sketch, "E2672", {"start": v(-30.08, 5.24) * mm, "mid": v(-30.14, 5.28) * mm, "end": v(-30.18, 5.23) * mm});
            skLineSegment(sketch, "E2673", {"start": v(-30.11, 5.08) * mm, "end": v(-30.06, 4.93) * mm});
            skArc(sketch, "E2674", {"start": v(-30.11, 4.92) * mm, "mid": v(-30.05, 4.88) * mm, "end": v(-30.02, 4.95) * mm});
            skArc(sketch, "E2675", {"start": v(-30.06, 5.1) * mm, "mid": v(-30.13, 5.13) * mm, "end": v(-30.16, 5.06) * mm});
            skLineSegment(sketch, "E2676", {"start": v(-30.06, 4.93) * mm, "end": v(-30, 4.81) * mm});
            skArc(sketch, "E2677", {"start": v(-30.05, 4.8) * mm, "mid": v(-29.98, 4.77) * mm, "end": v(-29.96, 4.84) * mm});
            skArc(sketch, "E2678", {"start": v(-30.02, 4.95) * mm, "mid": v(-30.09, 4.97) * mm, "end": v(-30.1, 4.9) * mm});
            skLineSegment(sketch, "E2679", {"start": v(-29.74, 4.98) * mm, "end": v(-28.39, 9.15) * mm});
            skArc(sketch, "E2680", {"start": v(-28.34, 9.14) * mm, "mid": v(-28.37, 9.2) * mm, "end": v(-28.44, 9.17) * mm});
            skArc(sketch, "E2681", {"start": v(-29.8, 5) * mm, "mid": v(-29.76, 4.93) * mm, "end": v(-29.7, 4.97) * mm});
            skLineSegment(sketch, "E2682", {"start": v(-30, 4.82) * mm, "end": v(-28.5, 9.44) * mm});
            skArc(sketch, "E2683", {"start": v(-28.46, 9.42) * mm, "mid": v(-28.5, 9.48) * mm, "end": v(-28.55, 9.45) * mm});
            skArc(sketch, "E2684", {"start": v(-30.05, 4.83) * mm, "mid": v(-30.02, 4.77) * mm, "end": v(-29.96, 4.8) * mm});
            skLineSegment(sketch, "E2685", {"start": v(-30.12, 5.13) * mm, "end": v(-28.78, 9.25) * mm});
            skArc(sketch, "E2686", {"start": v(-28.73, 9.24) * mm, "mid": v(-28.76, 9.3) * mm, "end": v(-28.82, 9.27) * mm});
            skArc(sketch, "E2687", {"start": v(-30.16, 5.14) * mm, "mid": v(-30.13, 5.08) * mm, "end": v(-30.07, 5.11) * mm});
            skCircle(sketch, "E2688", {"center": v(-16.51, 2.99) * mm, "radius": 1.7 * mm});
            skArc(sketch, "E2689", {"start": v(-16.51, 2.11) * mm, "mid": v(-15.64, 2.99) * mm, "end": v(-16.51, 3.86) * mm});
            skArc(sketch, "E2690", {"start": v(-16.51, 3.86) * mm, "mid": v(-17.39, 2.99) * mm, "end": v(-16.51, 2.11) * mm});
            skCircle(sketch, "E2691", {"center": v(-26.02, 6.08) * mm, "radius": 1.7 * mm});
            skArc(sketch, "E2692", {"start": v(-26.02, 5.2) * mm, "mid": v(-25.15, 6.08) * mm, "end": v(-26.02, 6.95) * mm});
            skArc(sketch, "E2693", {"start": v(-26.02, 6.95) * mm, "mid": v(-26.9, 6.08) * mm, "end": v(-26.02, 5.2) * mm});
            skLineSegment(sketch, "E2694", {"start": v(-10.35, -20.46) * mm, "end": v(-8.24, -17.54) * mm});
            skArc(sketch, "E2695", {"start": v(-8.14, -17.62) * mm, "mid": v(-8.17, -17.44) * mm, "end": v(-8.34, -17.47) * mm});
            skArc(sketch, "E2696", {"start": v(-10.45, -20.39) * mm, "mid": v(-10.42, -20.56) * mm, "end": v(-10.25, -20.54) * mm});
            skLineSegment(sketch, "E2697", {"start": v(-8.24, -17.54) * mm, "end": v(-8.14, -17.34) * mm});
            skArc(sketch, "E2698", {"start": v(-8.03, -17.4) * mm, "mid": v(-8.08, -17.23) * mm, "end": v(-8.25, -17.28) * mm});
            skArc(sketch, "E2699", {"start": v(-8.35, -17.49) * mm, "mid": v(-8.3, -17.65) * mm, "end": v(-8.13, -17.6) * mm});
            skLineSegment(sketch, "E2700", {"start": v(-8.14, -17.34) * mm, "end": v(-8.06, -17.13) * mm});
            skArc(sketch, "E2701", {"start": v(-7.94, -17.18) * mm, "mid": v(-8.01, -17.02) * mm, "end": v(-8.18, -17.09) * mm});
            skArc(sketch, "E2702", {"start": v(-8.26, -17.3) * mm, "mid": v(-8.19, -17.46) * mm, "end": v(-8.02, -17.39) * mm});
            skLineSegment(sketch, "E2703", {"start": v(-8.06, -17.13) * mm, "end": v(-8, -16.92) * mm});
            skArc(sketch, "E2704", {"start": v(-7.88, -16.96) * mm, "mid": v(-7.97, -16.8) * mm, "end": v(-8.12, -16.89) * mm});
            skArc(sketch, "E2705", {"start": v(-8.18, -17.1) * mm, "mid": v(-8.1, -17.25) * mm, "end": v(-7.94, -17.17) * mm});
            skLineSegment(sketch, "E2706", {"start": v(-8, -16.92) * mm, "end": v(-7.96, -16.7) * mm});
            skArc(sketch, "E2707", {"start": v(-7.84, -16.73) * mm, "mid": v(-7.94, -16.58) * mm, "end": v(-8.09, -16.69) * mm});
            skArc(sketch, "E2708", {"start": v(-8.12, -16.9) * mm, "mid": v(-8.02, -17.05) * mm, "end": v(-7.88, -16.94) * mm});
            skLineSegment(sketch, "E2709", {"start": v(-7.96, -16.7) * mm, "end": v(-7.95, -16.5) * mm});
            skArc(sketch, "E2710", {"start": v(-7.82, -16.5) * mm, "mid": v(-7.94, -16.37) * mm, "end": v(-8.07, -16.48) * mm});
            skArc(sketch, "E2711", {"start": v(-8.09, -16.7) * mm, "mid": v(-7.97, -16.83) * mm, "end": v(-7.84, -16.72) * mm});
            skLineSegment(sketch, "E2712", {"start": v(-7.95, -16.5) * mm, "end": v(-7.95, -16.27) * mm});
            skArc(sketch, "E2713", {"start": v(-7.82, -16.27) * mm, "mid": v(-7.95, -16.15) * mm, "end": v(-8.07, -16.28) * mm});
            skArc(sketch, "E2714", {"start": v(-8.07, -16.5) * mm, "mid": v(-7.94, -16.62) * mm, "end": v(-7.82, -16.49) * mm});
            skLineSegment(sketch, "E2715", {"start": v(-7.95, -16.27) * mm, "end": v(-7.97, -16.06) * mm});
            skArc(sketch, "E2716", {"start": v(-7.85, -16.05) * mm, "mid": v(-7.99, -15.94) * mm, "end": v(-8.1, -16.07) * mm});
            skArc(sketch, "E2717", {"start": v(-8.07, -16.29) * mm, "mid": v(-7.94, -16.4) * mm, "end": v(-7.83, -16.26) * mm});
            skLineSegment(sketch, "E2718", {"start": v(-7.97, -16.06) * mm, "end": v(-8.02, -15.85) * mm});
            skArc(sketch, "E2719", {"start": v(-7.9, -15.82) * mm, "mid": v(-8.05, -15.73) * mm, "end": v(-8.14, -15.87) * mm});
            skArc(sketch, "E2720", {"start": v(-8.1, -16.09) * mm, "mid": v(-7.95, -16.18) * mm, "end": v(-7.85, -16.03) * mm});
            skLineSegment(sketch, "E2721", {"start": v(-8.02, -15.85) * mm, "end": v(-8.08, -15.64) * mm});
            skArc(sketch, "E2722", {"start": v(-7.97, -15.6) * mm, "mid": v(-8.12, -15.52) * mm, "end": v(-8.2, -15.68) * mm});
            skArc(sketch, "E2723", {"start": v(-8.14, -15.89) * mm, "mid": v(-7.98, -15.97) * mm, "end": v(-7.9, -15.81) * mm});
            skLineSegment(sketch, "E2724", {"start": v(-8.08, -15.64) * mm, "end": v(-8.17, -15.44) * mm});
            skArc(sketch, "E2725", {"start": v(-8.05, -15.4) * mm, "mid": v(-8.22, -15.33) * mm, "end": v(-8.28, -15.5) * mm});
            skArc(sketch, "E2726", {"start": v(-8.2, -15.7) * mm, "mid": v(-8.04, -15.76) * mm, "end": v(-7.97, -15.6) * mm});
            skLineSegment(sketch, "E2727", {"start": v(-8.17, -15.44) * mm, "end": v(-8.27, -15.25) * mm});
            skArc(sketch, "E2728", {"start": v(-8.16, -15.2) * mm, "mid": v(-8.33, -15.14) * mm, "end": v(-8.38, -15.31) * mm});
            skArc(sketch, "E2729", {"start": v(-8.28, -15.5) * mm, "mid": v(-8.1, -15.55) * mm, "end": v(-8.06, -15.38) * mm});
            skLineSegment(sketch, "E2730", {"start": v(-8.27, -15.25) * mm, "end": v(-8.4, -15.07) * mm});
            skArc(sketch, "E2731", {"start": v(-8.3, -15) * mm, "mid": v(-8.47, -14.96) * mm, "end": v(-8.5, -15.14) * mm});
            skArc(sketch, "E2732", {"start": v(-8.38, -15.32) * mm, "mid": v(-8.2, -15.35) * mm, "end": v(-8.17, -15.18) * mm});
            skLineSegment(sketch, "E2733", {"start": v(-8.4, -15.07) * mm, "end": v(-8.54, -14.9) * mm});
            skArc(sketch, "E2734", {"start": v(-8.44, -14.82) * mm, "mid": v(-8.62, -14.8) * mm, "end": v(-8.64, -14.98) * mm});
            skArc(sketch, "E2735", {"start": v(-8.5, -15.15) * mm, "mid": v(-8.32, -15.16) * mm, "end": v(-8.3, -14.99) * mm});
            skLineSegment(sketch, "E2736", {"start": v(-8.54, -14.9) * mm, "end": v(-8.7, -14.74) * mm});
            skArc(sketch, "E2737", {"start": v(-8.62, -14.65) * mm, "mid": v(-8.8, -14.65) * mm, "end": v(-8.79, -14.83) * mm});
            skArc(sketch, "E2738", {"start": v(-8.63, -14.99) * mm, "mid": v(-8.45, -14.99) * mm, "end": v(-8.45, -14.8) * mm});
            skLineSegment(sketch, "E2739", {"start": v(-8.7, -14.74) * mm, "end": v(-8.87, -14.6) * mm});
            skArc(sketch, "E2740", {"start": v(-8.8, -14.5) * mm, "mid": v(-8.97, -14.53) * mm, "end": v(-8.95, -14.7) * mm});
            skArc(sketch, "E2741", {"start": v(-8.78, -14.84) * mm, "mid": v(-8.6, -14.82) * mm, "end": v(-8.62, -14.64) * mm});
            skLineSegment(sketch, "E2742", {"start": v(-8.87, -14.6) * mm, "end": v(-9.08, -14.47) * mm});
            skArc(sketch, "E2743", {"start": v(-9, -14.37) * mm, "mid": v(-9.18, -14.4) * mm, "end": v(-9.15, -14.58) * mm});
            skArc(sketch, "E2744", {"start": v(-8.94, -14.7) * mm, "mid": v(-8.77, -14.67) * mm, "end": v(-8.8, -14.5) * mm});
            skLineSegment(sketch, "E2745", {"start": v(-9.08, -14.47) * mm, "end": v(-9.28, -14.37) * mm});
            skArc(sketch, "E2746", {"start": v(-9.22, -14.26) * mm, "mid": v(-9.39, -14.31) * mm, "end": v(-9.33, -14.48) * mm});
            skArc(sketch, "E2747", {"start": v(-9.13, -14.58) * mm, "mid": v(-8.97, -14.53) * mm, "end": v(-9.02, -14.36) * mm});
            skLineSegment(sketch, "E2748", {"start": v(-9.28, -14.37) * mm, "end": v(-9.49, -14.29) * mm});
            skArc(sketch, "E2749", {"start": v(-9.44, -14.17) * mm, "mid": v(-9.6, -14.24) * mm, "end": v(-9.53, -14.4) * mm});
            skArc(sketch, "E2750", {"start": v(-9.32, -14.48) * mm, "mid": v(-9.16, -14.41) * mm, "end": v(-9.23, -14.25) * mm});
            skLineSegment(sketch, "E2751", {"start": v(-9.49, -14.29) * mm, "end": v(-9.7, -14.23) * mm});
            skArc(sketch, "E2752", {"start": v(-9.66, -14.1) * mm, "mid": v(-9.82, -14.2) * mm, "end": v(-9.73, -14.35) * mm});
            skArc(sketch, "E2753", {"start": v(-9.52, -14.4) * mm, "mid": v(-9.36, -14.32) * mm, "end": v(-9.45, -14.17) * mm});
            skLineSegment(sketch, "E2754", {"start": v(-9.7, -14.23) * mm, "end": v(-9.91, -14.2) * mm});
            skArc(sketch, "E2755", {"start": v(-9.9, -14.07) * mm, "mid": v(-10.03, -14.17) * mm, "end": v(-9.93, -14.31) * mm});
            skArc(sketch, "E2756", {"start": v(-9.72, -14.35) * mm, "mid": v(-9.57, -14.25) * mm, "end": v(-9.67, -14.1) * mm});
            skLineSegment(sketch, "E2757", {"start": v(-9.91, -14.2) * mm, "end": v(-10.13, -14.17) * mm});
            skArc(sketch, "E2758", {"start": v(-10.12, -14.05) * mm, "mid": v(-10.25, -14.16) * mm, "end": v(-10.14, -14.3) * mm});
            skArc(sketch, "E2759", {"start": v(-9.92, -14.32) * mm, "mid": v(-9.79, -14.2) * mm, "end": v(-9.9, -14.07) * mm});
            skLineSegment(sketch, "E2760", {"start": v(-10.13, -14.17) * mm, "end": v(-10.34, -14.18) * mm});
            skArc(sketch, "E2761", {"start": v(-10.35, -14.05) * mm, "mid": v(-10.47, -14.18) * mm, "end": v(-10.34, -14.3) * mm});
            skArc(sketch, "E2762", {"start": v(-10.13, -14.3) * mm, "mid": v(-10, -14.17) * mm, "end": v(-10.13, -14.05) * mm});
            skLineSegment(sketch, "E2763", {"start": v(-10.34, -14.18) * mm, "end": v(-10.56, -14.2) * mm});
            skArc(sketch, "E2764", {"start": v(-10.57, -14.08) * mm, "mid": v(-10.68, -14.22) * mm, "end": v(-10.54, -14.33) * mm});
            skArc(sketch, "E2765", {"start": v(-10.33, -14.3) * mm, "mid": v(-10.22, -14.16) * mm, "end": v(-10.36, -14.05) * mm});
            skLineSegment(sketch, "E2766", {"start": v(-10.56, -14.2) * mm, "end": v(-10.77, -14.25) * mm});
            skArc(sketch, "E2767", {"start": v(-10.8, -14.13) * mm, "mid": v(-10.9, -14.27) * mm, "end": v(-10.74, -14.37) * mm});
            skArc(sketch, "E2768", {"start": v(-10.53, -14.33) * mm, "mid": v(-10.44, -14.18) * mm, "end": v(-10.59, -14.08) * mm});
            skLineSegment(sketch, "E2769", {"start": v(-10.77, -14.25) * mm, "end": v(-10.98, -14.31) * mm});
            skArc(sketch, "E2770", {"start": v(-11.01, -14.2) * mm, "mid": v(-11.1, -14.35) * mm, "end": v(-10.94, -14.43) * mm});
            skArc(sketch, "E2771", {"start": v(-10.73, -14.37) * mm, "mid": v(-10.65, -14.21) * mm, "end": v(-10.8, -14.13) * mm});
            skLineSegment(sketch, "E2772", {"start": v(-10.98, -14.31) * mm, "end": v(-11.18, -14.4) * mm});
            skArc(sketch, "E2773", {"start": v(-11.23, -14.28) * mm, "mid": v(-11.3, -14.45) * mm, "end": v(-11.13, -14.51) * mm});
            skArc(sketch, "E2774", {"start": v(-10.93, -14.43) * mm, "mid": v(-10.86, -14.26) * mm, "end": v(-11.03, -14.2) * mm});
            skLineSegment(sketch, "E2775", {"start": v(-11.18, -14.4) * mm, "end": v(-11.37, -14.5) * mm});
            skArc(sketch, "E2776", {"start": v(-11.43, -14.4) * mm, "mid": v(-11.48, -14.56) * mm, "end": v(-11.3, -14.61) * mm});
            skArc(sketch, "E2777", {"start": v(-11.12, -14.5) * mm, "mid": v(-11.07, -14.34) * mm, "end": v(-11.24, -14.29) * mm});
            skLineSegment(sketch, "E2778", {"start": v(-11.37, -14.5) * mm, "end": v(-11.55, -14.63) * mm});
            skArc(sketch, "E2779", {"start": v(-11.62, -14.52) * mm, "mid": v(-11.65, -14.7) * mm, "end": v(-11.48, -14.73) * mm});
            skArc(sketch, "E2780", {"start": v(-11.3, -14.6) * mm, "mid": v(-11.26, -14.43) * mm, "end": v(-11.44, -14.4) * mm});
            skLineSegment(sketch, "E2781", {"start": v(-11.55, -14.63) * mm, "end": v(-11.72, -14.77) * mm});
            skArc(sketch, "E2782", {"start": v(-11.8, -14.67) * mm, "mid": v(-11.82, -14.85) * mm, "end": v(-11.64, -14.87) * mm});
            skArc(sketch, "E2783", {"start": v(-11.47, -14.72) * mm, "mid": v(-11.45, -14.55) * mm, "end": v(-11.63, -14.53) * mm});
            skLineSegment(sketch, "E2784", {"start": v(-11.72, -14.77) * mm, "end": v(-11.88, -14.93) * mm});
            skArc(sketch, "E2785", {"start": v(-11.97, -14.84) * mm, "mid": v(-11.97, -15.02) * mm, "end": v(-11.8, -15.02) * mm});
            skArc(sketch, "E2786", {"start": v(-11.63, -14.86) * mm, "mid": v(-11.63, -14.68) * mm, "end": v(-11.81, -14.68) * mm});
            skLineSegment(sketch, "E2787", {"start": v(-11.88, -14.93) * mm, "end": v(-12.03, -15.12) * mm});
            skArc(sketch, "E2788", {"start": v(-12.13, -15.05) * mm, "mid": v(-12.11, -15.22) * mm, "end": v(-11.94, -15.2) * mm});
            skArc(sketch, "E2789", {"start": v(-11.78, -15) * mm, "mid": v(-11.8, -14.83) * mm, "end": v(-11.98, -14.85) * mm});
            skLineSegment(sketch, "E2790", {"start": v(-12.03, -15.12) * mm, "end": v(-14, -17.82) * mm});
            skArc(sketch, "E2791", {"start": v(-14.1, -17.74) * mm, "mid": v(-14.06, -17.92) * mm, "end": v(-13.89, -17.9) * mm});
            skArc(sketch, "E2792", {"start": v(-11.93, -15.2) * mm, "mid": v(-11.96, -15.02) * mm, "end": v(-12.14, -15.05) * mm});
            skLineSegment(sketch, "E2793", {"start": v(-14, -17.82) * mm, "end": v(-14.7, -20.04) * mm});
            skArc(sketch, "E2794", {"start": v(-14.83, -20) * mm, "mid": v(-14.75, -20.15) * mm, "end": v(-14.6, -20.07) * mm});
            skArc(sketch, "E2795", {"start": v(-13.87, -17.86) * mm, "mid": v(-13.95, -17.7) * mm, "end": v(-14.1, -17.78) * mm});
            skLineSegment(sketch, "E2796", {"start": v(-14.7, -20.04) * mm, "end": v(-14.77, -21.1) * mm});
            skArc(sketch, "E2797", {"start": v(-14.89, -21.08) * mm, "mid": v(-14.77, -21.21) * mm, "end": v(-14.64, -21.1) * mm});
            skArc(sketch, "E2798", {"start": v(-14.59, -20.04) * mm, "mid": v(-14.7, -19.91) * mm, "end": v(-14.83, -20.03) * mm});
            skLineSegment(sketch, "E2799", {"start": v(-14.77, -21.1) * mm, "end": v(-13.22, -22.21) * mm});
            skArc(sketch, "E2800", {"start": v(-13.3, -22.31) * mm, "mid": v(-13.12, -22.28) * mm, "end": v(-13.15, -22.1) * mm});
            skArc(sketch, "E2801", {"start": v(-14.7, -20.99) * mm, "mid": v(-14.87, -21.02) * mm, "end": v(-14.84, -21.2) * mm});
            skLineSegment(sketch, "E2802", {"start": v(-13.22, -22.21) * mm, "end": v(-12.24, -21.83) * mm});
            skArc(sketch, "E2803", {"start": v(-12.2, -21.95) * mm, "mid": v(-12.12, -21.79) * mm, "end": v(-12.28, -21.72) * mm});
            skArc(sketch, "E2804", {"start": v(-13.27, -22.1) * mm, "mid": v(-13.34, -22.26) * mm, "end": v(-13.18, -22.33) * mm});
            skLineSegment(sketch, "E2805", {"start": v(-12.24, -21.83) * mm, "end": v(-10.35, -20.46) * mm});
            skArc(sketch, "E2806", {"start": v(-10.28, -20.56) * mm, "mid": v(-10.25, -20.39) * mm, "end": v(-10.42, -20.36) * mm});
            skArc(sketch, "E2807", {"start": v(-12.31, -21.73) * mm, "mid": v(-12.34, -21.9) * mm, "end": v(-12.16, -21.93) * mm});
            skLineSegment(sketch, "E2808", {"start": v(-8.19, -15.41) * mm, "end": v(-9.85, -14.2) * mm});
            skArc(sketch, "E2809", {"start": v(-9.78, -14.1) * mm, "mid": v(-9.95, -14.13) * mm, "end": v(-9.93, -14.3) * mm});
            skArc(sketch, "E2810", {"start": v(-8.26, -15.51) * mm, "mid": v(-8.09, -15.49) * mm, "end": v(-8.11, -15.31) * mm});
            skLineSegment(sketch, "E2811", {"start": v(-7.96, -16.2) * mm, "end": v(-10.67, -14.23) * mm});
            skArc(sketch, "E2812", {"start": v(-10.6, -14.13) * mm, "mid": v(-10.77, -14.15) * mm, "end": v(-10.74, -14.33) * mm});
            skArc(sketch, "E2813", {"start": v(-8.03, -16.3) * mm, "mid": v(-7.86, -16.27) * mm, "end": v(-7.89, -16.1) * mm});
            skLineSegment(sketch, "E2814", {"start": v(-7.98, -16.8) * mm, "end": v(-11.24, -14.43) * mm});
            skArc(sketch, "E2815", {"start": v(-11.16, -14.33) * mm, "mid": v(-11.34, -14.36) * mm, "end": v(-11.31, -14.53) * mm});
            skArc(sketch, "E2816", {"start": v(-8.05, -16.9) * mm, "mid": v(-7.88, -16.87) * mm, "end": v(-7.9, -16.7) * mm});
            skLineSegment(sketch, "E2817", {"start": v(-8.13, -17.3) * mm, "end": v(-11.68, -14.73) * mm});
            skArc(sketch, "E2818", {"start": v(-11.6, -14.63) * mm, "mid": v(-11.78, -14.66) * mm, "end": v(-11.75, -14.83) * mm});
            skArc(sketch, "E2819", {"start": v(-8.2, -17.4) * mm, "mid": v(-8.03, -17.38) * mm, "end": v(-8.05, -17.2) * mm});
            skLineSegment(sketch, "E2820", {"start": v(-8.38, -17.74) * mm, "end": v(-12.02, -15.1) * mm});
            skArc(sketch, "E2821", {"start": v(-11.94, -15) * mm, "mid": v(-12.12, -15.03) * mm, "end": v(-12.09, -15.2) * mm});
            skArc(sketch, "E2822", {"start": v(-8.46, -17.84) * mm, "mid": v(-8.28, -17.81) * mm, "end": v(-8.31, -17.64) * mm});
            skLineSegment(sketch, "E2823", {"start": v(-8.68, -18.15) * mm, "end": v(-12.31, -15.5) * mm});
            skArc(sketch, "E2824", {"start": v(-12.24, -15.4) * mm, "mid": v(-12.41, -15.43) * mm, "end": v(-12.38, -15.6) * mm});
            skArc(sketch, "E2825", {"start": v(-8.75, -18.25) * mm, "mid": v(-8.58, -18.22) * mm, "end": v(-8.6, -18.04) * mm});
            skLineSegment(sketch, "E2826", {"start": v(-8.97, -18.55) * mm, "end": v(-12.6, -15.9) * mm});
            skArc(sketch, "E2827", {"start": v(-12.53, -15.8) * mm, "mid": v(-12.7, -15.84) * mm, "end": v(-12.68, -16.01) * mm});
            skArc(sketch, "E2828", {"start": v(-9.04, -18.65) * mm, "mid": v(-8.87, -18.62) * mm, "end": v(-8.9, -18.45) * mm});
            skLineSegment(sketch, "E2829", {"start": v(-9.26, -18.96) * mm, "end": v(-12.9, -16.31) * mm});
            skArc(sketch, "E2830", {"start": v(-12.82, -16.21) * mm, "mid": v(-13, -16.24) * mm, "end": v(-12.97, -16.42) * mm});
            skArc(sketch, "E2831", {"start": v(-9.34, -19.06) * mm, "mid": v(-9.16, -19.03) * mm, "end": v(-9.19, -18.85) * mm});
            skLineSegment(sketch, "E2832", {"start": v(-9.56, -19.36) * mm, "end": v(-13.2, -16.72) * mm});
            skArc(sketch, "E2833", {"start": v(-13.12, -16.62) * mm, "mid": v(-13.3, -16.65) * mm, "end": v(-13.27, -16.82) * mm});
            skArc(sketch, "E2834", {"start": v(-9.63, -19.46) * mm, "mid": v(-9.45, -19.43) * mm, "end": v(-9.48, -19.26) * mm});
            skLineSegment(sketch, "E2835", {"start": v(-9.85, -19.77) * mm, "end": v(-13.49, -17.12) * mm});
            skArc(sketch, "E2836", {"start": v(-13.41, -17.02) * mm, "mid": v(-13.59, -17.05) * mm, "end": v(-13.56, -17.22) * mm});
            skArc(sketch, "E2837", {"start": v(-9.92, -19.87) * mm, "mid": v(-9.75, -19.84) * mm, "end": v(-9.77, -19.67) * mm});
            skLineSegment(sketch, "E2838", {"start": v(-10.14, -20.17) * mm, "end": v(-13.78, -17.53) * mm});
            skArc(sketch, "E2839", {"start": v(-13.7, -17.43) * mm, "mid": v(-13.88, -17.45) * mm, "end": v(-13.85, -17.63) * mm});
            skArc(sketch, "E2840", {"start": v(-10.21, -20.27) * mm, "mid": v(-10.04, -20.25) * mm, "end": v(-10.07, -20.07) * mm});
            skLineSegment(sketch, "E2841", {"start": v(-10.47, -20.55) * mm, "end": v(-14.04, -17.96) * mm});
            skArc(sketch, "E2842", {"start": v(-13.96, -17.86) * mm, "mid": v(-14.14, -17.89) * mm, "end": v(-14.11, -18.06) * mm});
            skArc(sketch, "E2843", {"start": v(-10.54, -20.65) * mm, "mid": v(-10.37, -20.62) * mm, "end": v(-10.4, -20.45) * mm});
            skLineSegment(sketch, "E2844", {"start": v(-10.9, -20.86) * mm, "end": v(-14.2, -18.46) * mm});
            skArc(sketch, "E2845", {"start": v(-14.13, -18.36) * mm, "mid": v(-14.3, -18.39) * mm, "end": v(-14.27, -18.56) * mm});
            skArc(sketch, "E2846", {"start": v(-10.97, -20.96) * mm, "mid": v(-10.8, -20.93) * mm, "end": v(-10.82, -20.76) * mm});
            skLineSegment(sketch, "E2847", {"start": v(-11.32, -21.17) * mm, "end": v(-14.36, -18.96) * mm});
            skArc(sketch, "E2848", {"start": v(-14.29, -18.86) * mm, "mid": v(-14.46, -18.89) * mm, "end": v(-14.43, -19.06) * mm});
            skArc(sketch, "E2849", {"start": v(-11.4, -21.27) * mm, "mid": v(-11.22, -21.24) * mm, "end": v(-11.25, -21.07) * mm});
            skLineSegment(sketch, "E2850", {"start": v(-11.75, -21.48) * mm, "end": v(-14.52, -19.46) * mm});
            skArc(sketch, "E2851", {"start": v(-14.45, -19.36) * mm, "mid": v(-14.62, -19.39) * mm, "end": v(-14.6, -19.56) * mm});
            skArc(sketch, "E2852", {"start": v(-11.82, -21.58) * mm, "mid": v(-11.65, -21.55) * mm, "end": v(-11.67, -21.38) * mm});
            skLineSegment(sketch, "E2853", {"start": v(-12.17, -21.79) * mm, "end": v(-14.69, -19.96) * mm});
            skArc(sketch, "E2854", {"start": v(-14.61, -19.86) * mm, "mid": v(-14.79, -19.89) * mm, "end": v(-14.76, -20.06) * mm});
            skArc(sketch, "E2855", {"start": v(-12.25, -21.89) * mm, "mid": v(-12.07, -21.86) * mm, "end": v(-12.1, -21.68) * mm});
            skLineSegment(sketch, "E2856", {"start": v(-12.7, -22.01) * mm, "end": v(-14.74, -20.54) * mm});
            skArc(sketch, "E2857", {"start": v(-14.66, -20.44) * mm, "mid": v(-14.84, -20.47) * mm, "end": v(-14.8, -20.64) * mm});
            skArc(sketch, "E2858", {"start": v(-12.78, -22.11) * mm, "mid": v(-12.6, -22.09) * mm, "end": v(-12.64, -21.91) * mm});
            skLineSegment(sketch, "E2859", {"start": v(-16.1, -28.7) * mm, "end": v(-16.12, -28.55) * mm});
            skArc(sketch, "E2860", {"start": v(-16.07, -28.54) * mm, "mid": v(-16.13, -28.5) * mm, "end": v(-16.17, -28.56) * mm});
            skArc(sketch, "E2861", {"start": v(-16.15, -28.7) * mm, "mid": v(-16.1, -28.74) * mm, "end": v(-16.05, -28.68) * mm});
            skLineSegment(sketch, "E2862", {"start": v(-16.12, -28.55) * mm, "end": v(-16.17, -28.4) * mm});
            skArc(sketch, "E2863", {"start": v(-16.13, -28.39) * mm, "mid": v(-16.19, -28.36) * mm, "end": v(-16.22, -28.42) * mm});
            skArc(sketch, "E2864", {"start": v(-16.17, -28.57) * mm, "mid": v(-16.1, -28.6) * mm, "end": v(-16.08, -28.54) * mm});
            skLineSegment(sketch, "E2865", {"start": v(-16.17, -28.4) * mm, "end": v(-16.25, -28.27) * mm});
            skArc(sketch, "E2866", {"start": v(-16.2, -28.24) * mm, "mid": v(-16.27, -28.23) * mm, "end": v(-16.3, -28.3) * mm});
            skArc(sketch, "E2867", {"start": v(-16.22, -28.43) * mm, "mid": v(-16.15, -28.45) * mm, "end": v(-16.13, -28.38) * mm});
            skLineSegment(sketch, "E2868", {"start": v(-16.25, -28.27) * mm, "end": v(-16.35, -28.15) * mm});
            skArc(sketch, "E2869", {"start": v(-16.3, -28.11) * mm, "mid": v(-16.38, -28.1) * mm, "end": v(-16.39, -28.18) * mm});
            skArc(sketch, "E2870", {"start": v(-16.29, -28.3) * mm, "mid": v(-16.22, -28.3) * mm, "end": v(-16.2, -28.24) * mm});
            skLineSegment(sketch, "E2871", {"start": v(-16.35, -28.15) * mm, "end": v(-16.4, -28.1) * mm});
            skArc(sketch, "E2872", {"start": v(-16.37, -28.05) * mm, "mid": v(-16.44, -28.06) * mm, "end": v(-16.44, -28.13) * mm});
            skArc(sketch, "E2873", {"start": v(-16.38, -28.18) * mm, "mid": v(-16.31, -28.18) * mm, "end": v(-16.31, -28.1) * mm});
            skLineSegment(sketch, "E2874", {"start": v(-16.4, -28.1) * mm, "end": v(-19.45, -25.9) * mm});
            skArc(sketch, "E2875", {"start": v(-19.42, -25.85) * mm, "mid": v(-19.5, -25.86) * mm, "end": v(-19.48, -25.93) * mm});
            skArc(sketch, "E2876", {"start": v(-16.43, -28.13) * mm, "mid": v(-16.37, -28.12) * mm, "end": v(-16.38, -28.05) * mm});
            skLineSegment(sketch, "E2877", {"start": v(-19.45, -25.9) * mm, "end": v(-19.6, -25.84) * mm});
            skArc(sketch, "E2878", {"start": v(-19.58, -25.8) * mm, "mid": v(-19.64, -25.82) * mm, "end": v(-19.62, -25.89) * mm});
            skArc(sketch, "E2879", {"start": v(-19.47, -25.94) * mm, "mid": v(-19.4, -25.91) * mm, "end": v(-19.43, -25.85) * mm});
            skLineSegment(sketch, "E2880", {"start": v(-19.6, -25.84) * mm, "end": v(-19.75, -25.81) * mm});
            skArc(sketch, "E2881", {"start": v(-19.74, -25.76) * mm, "mid": v(-19.8, -25.8) * mm, "end": v(-19.76, -25.86) * mm});
            skArc(sketch, "E2882", {"start": v(-19.6, -25.89) * mm, "mid": v(-19.55, -25.85) * mm, "end": v(-19.59, -25.79) * mm});
            skLineSegment(sketch, "E2883", {"start": v(-19.75, -25.81) * mm, "end": v(-19.9, -25.8) * mm});
            skArc(sketch, "E2884", {"start": v(-19.9, -25.76) * mm, "mid": v(-19.96, -25.8) * mm, "end": v(-19.9, -25.86) * mm});
            skArc(sketch, "E2885", {"start": v(-19.75, -25.86) * mm, "mid": v(-19.7, -25.81) * mm, "end": v(-19.75, -25.76) * mm});
            skLineSegment(sketch, "E2886", {"start": v(-19.9, -25.8) * mm, "end": v(-20.04, -25.83) * mm});
            skArc(sketch, "E2887", {"start": v(-20.04, -25.78) * mm, "mid": v(-20.09, -25.84) * mm, "end": v(-20.03, -25.88) * mm});
            skArc(sketch, "E2888", {"start": v(-19.9, -25.86) * mm, "mid": v(-19.86, -25.8) * mm, "end": v(-19.91, -25.76) * mm});
            skLineSegment(sketch, "E2889", {"start": v(-20.04, -25.83) * mm, "end": v(-20.01, -25.97) * mm});
            skArc(sketch, "E2890", {"start": v(-20.06, -25.98) * mm, "mid": v(-20, -26.02) * mm, "end": v(-19.96, -25.96) * mm});
            skArc(sketch, "E2891", {"start": v(-19.99, -25.82) * mm, "mid": v(-20.04, -25.78) * mm, "end": v(-20.09, -25.84) * mm});
            skLineSegment(sketch, "E2892", {"start": v(-20.01, -25.97) * mm, "end": v(-19.96, -26.12) * mm});
            skArc(sketch, "E2893", {"start": v(-20, -26.13) * mm, "mid": v(-19.95, -26.16) * mm, "end": v(-19.92, -26.1) * mm});
            skArc(sketch, "E2894", {"start": v(-19.97, -25.95) * mm, "mid": v(-20.03, -25.92) * mm, "end": v(-20.06, -25.99) * mm});
            skLineSegment(sketch, "E2895", {"start": v(-19.96, -26.12) * mm, "end": v(-19.89, -26.25) * mm});
            skArc(sketch, "E2896", {"start": v(-19.93, -26.28) * mm, "mid": v(-19.86, -26.3) * mm, "end": v(-19.84, -26.23) * mm});
            skArc(sketch, "E2897", {"start": v(-19.92, -26.1) * mm, "mid": v(-19.99, -26.07) * mm, "end": v(-20, -26.14) * mm});
            skLineSegment(sketch, "E2898", {"start": v(-19.89, -26.25) * mm, "end": v(-19.79, -26.38) * mm});
            skArc(sketch, "E2899", {"start": v(-19.83, -26.4) * mm, "mid": v(-19.76, -26.42) * mm, "end": v(-19.75, -26.34) * mm});
            skArc(sketch, "E2900", {"start": v(-19.85, -26.22) * mm, "mid": v(-19.92, -26.21) * mm, "end": v(-19.93, -26.28) * mm});
            skLineSegment(sketch, "E2901", {"start": v(-19.79, -26.38) * mm, "end": v(-19.73, -26.43) * mm});
            skArc(sketch, "E2902", {"start": v(-19.76, -26.47) * mm, "mid": v(-19.7, -26.47) * mm, "end": v(-19.7, -26.4) * mm});
            skArc(sketch, "E2903", {"start": v(-19.75, -26.34) * mm, "mid": v(-19.82, -26.34) * mm, "end": v(-19.82, -26.41) * mm});
            skLineSegment(sketch, "E2904", {"start": v(-19.73, -26.43) * mm, "end": v(-16.69, -28.63) * mm});
            skArc(sketch, "E2905", {"start": v(-16.71, -28.67) * mm, "mid": v(-16.64, -28.66) * mm, "end": v(-16.66, -28.59) * mm});
            skArc(sketch, "E2906", {"start": v(-19.7, -26.4) * mm, "mid": v(-19.77, -26.4) * mm, "end": v(-19.76, -26.47) * mm});
            skLineSegment(sketch, "E2907", {"start": v(-16.69, -28.63) * mm, "end": v(-16.54, -28.68) * mm});
            skArc(sketch, "E2908", {"start": v(-16.55, -28.73) * mm, "mid": v(-16.5, -28.7) * mm, "end": v(-16.52, -28.64) * mm});
            skArc(sketch, "E2909", {"start": v(-16.67, -28.58) * mm, "mid": v(-16.73, -28.61) * mm, "end": v(-16.7, -28.68) * mm});
            skLineSegment(sketch, "E2910", {"start": v(-16.54, -28.68) * mm, "end": v(-16.38, -28.71) * mm});
            skArc(sketch, "E2911", {"start": v(-16.4, -28.76) * mm, "mid": v(-16.34, -28.72) * mm, "end": v(-16.38, -28.66) * mm});
            skArc(sketch, "E2912", {"start": v(-16.53, -28.63) * mm, "mid": v(-16.59, -28.67) * mm, "end": v(-16.55, -28.73) * mm});
            skLineSegment(sketch, "E2913", {"start": v(-16.38, -28.71) * mm, "end": v(-16.23, -28.71) * mm});
            skArc(sketch, "E2914", {"start": v(-16.23, -28.76) * mm, "mid": v(-16.18, -28.71) * mm, "end": v(-16.23, -28.66) * mm});
            skArc(sketch, "E2915", {"start": v(-16.38, -28.66) * mm, "mid": v(-16.43, -28.71) * mm, "end": v(-16.38, -28.76) * mm});
            skLineSegment(sketch, "E2916", {"start": v(-16.23, -28.71) * mm, "end": v(-16.1, -28.7) * mm});
            skArc(sketch, "E2917", {"start": v(-16.1, -28.74) * mm, "mid": v(-16.05, -28.68) * mm, "end": v(-16.1, -28.64) * mm});
            skArc(sketch, "E2918", {"start": v(-16.24, -28.66) * mm, "mid": v(-16.28, -28.72) * mm, "end": v(-16.22, -28.76) * mm});
            skLineSegment(sketch, "E2919", {"start": v(-16.18, -28.4) * mm, "end": v(-19.73, -25.82) * mm});
            skArc(sketch, "E2920", {"start": v(-19.7, -25.78) * mm, "mid": v(-19.77, -25.79) * mm, "end": v(-19.76, -25.86) * mm});
            skArc(sketch, "E2921", {"start": v(-16.2, -28.43) * mm, "mid": v(-16.14, -28.42) * mm, "end": v(-16.15, -28.35) * mm});
            skLineSegment(sketch, "E2922", {"start": v(-16.1, -28.7) * mm, "end": v(-20.03, -25.84) * mm});
            skArc(sketch, "E2923", {"start": v(-20, -25.8) * mm, "mid": v(-20.08, -25.8) * mm, "end": v(-20.06, -25.88) * mm});
            skArc(sketch, "E2924", {"start": v(-16.14, -28.73) * mm, "mid": v(-16.07, -28.72) * mm, "end": v(-16.08, -28.65) * mm});
            skLineSegment(sketch, "E2925", {"start": v(-16.43, -28.7) * mm, "end": v(-19.94, -26.15) * mm});
            skArc(sketch, "E2926", {"start": v(-19.91, -26.11) * mm, "mid": v(-19.98, -26.12) * mm, "end": v(-19.97, -26.2) * mm});
            skArc(sketch, "E2927", {"start": v(-16.46, -28.74) * mm, "mid": v(-16.4, -28.73) * mm, "end": v(-16.4, -28.66) * mm});
            skCircle(sketch, "E2928", {"center": v(-10.2, -16.42) * mm, "radius": 1.7 * mm});
            skArc(sketch, "E2929", {"start": v(-10.2, -17.3) * mm, "mid": v(-9.32, -16.42) * mm, "end": v(-10.2, -15.55) * mm});
            skArc(sketch, "E2930", {"start": v(-10.2, -15.55) * mm, "mid": v(-11.07, -16.42) * mm, "end": v(-10.2, -17.3) * mm});
            skCircle(sketch, "E2931", {"center": v(-16.07, -24.51) * mm, "radius": 1.7 * mm});
            skArc(sketch, "E2932", {"start": v(-16.07, -25.4) * mm, "mid": v(-15.2, -24.51) * mm, "end": v(-16.07, -23.64) * mm});
            skArc(sketch, "E2933", {"start": v(-16.07, -23.64) * mm, "mid": v(-16.95, -24.51) * mm, "end": v(-16.07, -25.4) * mm});
            skLineSegment(sketch, "E2934", {"start": v(4.19, 11.1) * mm, "end": v(4.19, 11.14) * mm});
            skArc(sketch, "E2935", {"start": v(4.21, 11.14) * mm, "mid": v(4.19, 11.17) * mm, "end": v(4.16, 11.14) * mm});
            skArc(sketch, "E2936", {"start": v(4.16, 11.1) * mm, "mid": v(4.19, 11.07) * mm, "end": v(4.21, 11.1) * mm});
            skLineSegment(sketch, "E2937", {"start": v(4.19, 11.14) * mm, "end": v(3.69, 11.3) * mm});
            skArc(sketch, "E2938", {"start": v(3.7, 11.32) * mm, "mid": v(3.66, 11.3) * mm, "end": v(3.68, 11.27) * mm});
            skArc(sketch, "E2939", {"start": v(4.18, 11.12) * mm, "mid": v(4.21, 11.13) * mm, "end": v(4.2, 11.17) * mm});
            skLineSegment(sketch, "E2940", {"start": v(3.69, 11.3) * mm, "end": v(3.19, 11.3) * mm});
            skArc(sketch, "E2941", {"start": v(3.19, 11.32) * mm, "mid": v(3.16, 11.3) * mm, "end": v(3.19, 11.27) * mm});
            skArc(sketch, "E2942", {"start": v(3.69, 11.27) * mm, "mid": v(3.71, 11.3) * mm, "end": v(3.69, 11.32) * mm});
            skLineSegment(sketch, "E2943", {"start": v(3.19, 11.3) * mm, "end": v(3.19, 11.1) * mm});
            skArc(sketch, "E2944", {"start": v(3.16, 11.1) * mm, "mid": v(3.19, 11.07) * mm, "end": v(3.21, 11.1) * mm});
            skArc(sketch, "E2945", {"start": v(3.21, 11.3) * mm, "mid": v(3.19, 11.32) * mm, "end": v(3.16, 11.3) * mm});
            skLineSegment(sketch, "E2946", {"start": v(3.19, 11.1) * mm, "end": v(4.19, 11.1) * mm});
            skArc(sketch, "E2947", {"start": v(4.19, 11.07) * mm, "mid": v(4.21, 11.1) * mm, "end": v(4.19, 11.12) * mm});
            skArc(sketch, "E2948", {"start": v(3.19, 11.12) * mm, "mid": v(3.16, 11.1) * mm, "end": v(3.19, 11.07) * mm});
            skLineSegment(sketch, "E2949", {"start": v(4.02, 11.2) * mm, "end": v(3.19, 11.2) * mm});
            skArc(sketch, "E2950", {"start": v(3.19, 11.22) * mm, "mid": v(3.16, 11.2) * mm, "end": v(3.19, 11.17) * mm});
            skArc(sketch, "E2951", {"start": v(4.02, 11.17) * mm, "mid": v(4.05, 11.2) * mm, "end": v(4.02, 11.22) * mm});
            skLineSegment(sketch, "E2952", {"start": v(-4.21, 11.1) * mm, "end": v(-4.21, 11.14) * mm});
            skArc(sketch, "E2953", {"start": v(-4.19, 11.14) * mm, "mid": v(-4.21, 11.17) * mm, "end": v(-4.24, 11.14) * mm});
            skArc(sketch, "E2954", {"start": v(-4.24, 11.1) * mm, "mid": v(-4.21, 11.07) * mm, "end": v(-4.19, 11.1) * mm});
            skLineSegment(sketch, "E2955", {"start": v(-4.21, 11.14) * mm, "end": v(-3.71, 11.3) * mm});
            skArc(sketch, "E2956", {"start": v(-3.7, 11.27) * mm, "mid": v(-3.69, 11.3) * mm, "end": v(-3.72, 11.32) * mm});
            skArc(sketch, "E2957", {"start": v(-4.22, 11.17) * mm, "mid": v(-4.24, 11.13) * mm, "end": v(-4.2, 11.12) * mm});
            skLineSegment(sketch, "E2958", {"start": v(-3.71, 11.3) * mm, "end": v(-3.21, 11.3) * mm});
            skArc(sketch, "E2959", {"start": v(-3.21, 11.27) * mm, "mid": v(-3.19, 11.3) * mm, "end": v(-3.21, 11.32) * mm});
            skArc(sketch, "E2960", {"start": v(-3.71, 11.32) * mm, "mid": v(-3.74, 11.3) * mm, "end": v(-3.71, 11.27) * mm});
            skLineSegment(sketch, "E2961", {"start": v(-3.21, 11.3) * mm, "end": v(-3.21, 11.1) * mm});
            skArc(sketch, "E2962", {"start": v(-3.24, 11.1) * mm, "mid": v(-3.21, 11.07) * mm, "end": v(-3.19, 11.1) * mm});
            skArc(sketch, "E2963", {"start": v(-3.19, 11.3) * mm, "mid": v(-3.21, 11.32) * mm, "end": v(-3.24, 11.3) * mm});
            skLineSegment(sketch, "E2964", {"start": v(-3.21, 11.1) * mm, "end": v(-4.21, 11.1) * mm});
            skArc(sketch, "E2965", {"start": v(-4.21, 11.12) * mm, "mid": v(-4.24, 11.1) * mm, "end": v(-4.21, 11.07) * mm});
            skArc(sketch, "E2966", {"start": v(-3.21, 11.07) * mm, "mid": v(-3.19, 11.1) * mm, "end": v(-3.21, 11.12) * mm});
            skLineSegment(sketch, "E2967", {"start": v(-3.21, 11.3) * mm, "end": v(-3.71, 11.3) * mm});
            skLineSegment(sketch, "E2968", {"start": v(-3.21, 11.2) * mm, "end": v(-4.05, 11.2) * mm});
            skArc(sketch, "E2969", {"start": v(-4.05, 11.22) * mm, "mid": v(-4.07, 11.2) * mm, "end": v(-4.05, 11.17) * mm});
            skArc(sketch, "E2970", {"start": v(-3.21, 11.17) * mm, "mid": v(-3.19, 11.2) * mm, "end": v(-3.21, 11.22) * mm});
            skCircle(sketch, "E2971", {"center": v(1.49, 9.1) * mm, "radius": 0.45 * mm});
            skArc(sketch, "E2972", {"start": v(1.49, 8.84) * mm, "mid": v(1.74, 9.1) * mm, "end": v(1.49, 9.34) * mm});
            skArc(sketch, "E2973", {"start": v(1.49, 9.34) * mm, "mid": v(1.24, 9.1) * mm, "end": v(1.49, 8.84) * mm});
            skCircle(sketch, "E2974", {"center": v(-1.51, 9.1) * mm, "radius": 0.45 * mm});
            skArc(sketch, "E2975", {"start": v(-1.51, 8.84) * mm, "mid": v(-1.26, 9.1) * mm, "end": v(-1.51, 9.34) * mm});
            skArc(sketch, "E2976", {"start": v(-1.51, 9.34) * mm, "mid": v(-1.76, 9.1) * mm, "end": v(-1.51, 8.84) * mm});
            skLineSegment(sketch, "E2977", {"start": v(2.68, 5.86) * mm, "end": v(2.68, 7.22) * mm});
            skArc(sketch, "E2978", {"start": v(2.68, 7.22) * mm, "mid": v(2.66, 7.26) * mm, "end": v(2.62, 7.28) * mm});
            skLineSegment(sketch, "E2979", {"start": v(2.62, 7.28) * mm, "end": v(2.06, 7.28) * mm});
            skArc(sketch, "E2980", {"start": v(2.06, 7.28) * mm, "mid": v(2.01, 7.26) * mm, "end": v(2, 7.22) * mm});
            skLineSegment(sketch, "E2981", {"start": v(2, 7.22) * mm, "end": v(2, 5.86) * mm});
            skArc(sketch, "E2982", {"start": v(2, 5.86) * mm, "mid": v(2.01, 5.82) * mm, "end": v(2.06, 5.8) * mm});
            skLineSegment(sketch, "E2983", {"start": v(2.06, 5.8) * mm, "end": v(2.62, 5.8) * mm});
            skArc(sketch, "E2984", {"start": v(2.62, 5.8) * mm, "mid": v(2.66, 5.82) * mm, "end": v(2.68, 5.86) * mm});
            skLineSegment(sketch, "E2985", {"start": v(-0.42, 5.86) * mm, "end": v(-0.42, 7.22) * mm});
            skArc(sketch, "E2986", {"start": v(-0.42, 7.22) * mm, "mid": v(-0.44, 7.26) * mm, "end": v(-0.48, 7.28) * mm});
            skLineSegment(sketch, "E2987", {"start": v(-0.48, 7.28) * mm, "end": v(-1.04, 7.28) * mm});
            skArc(sketch, "E2988", {"start": v(-1.04, 7.28) * mm, "mid": v(-1.09, 7.26) * mm, "end": v(-1.1, 7.22) * mm});
            skLineSegment(sketch, "E2989", {"start": v(-1.1, 7.22) * mm, "end": v(-1.1, 5.86) * mm});
            skArc(sketch, "E2990", {"start": v(-1.1, 5.86) * mm, "mid": v(-1.09, 5.82) * mm, "end": v(-1.04, 5.8) * mm});
            skLineSegment(sketch, "E2991", {"start": v(-1.04, 5.8) * mm, "end": v(-0.48, 5.8) * mm});
            skArc(sketch, "E2992", {"start": v(-0.48, 5.8) * mm, "mid": v(-0.44, 5.82) * mm, "end": v(-0.42, 5.86) * mm});
            skLineSegment(sketch, "E2993", {"start": v(-1.92, 5.86) * mm, "end": v(-1.92, 7.22) * mm});
            skArc(sketch, "E2994", {"start": v(-1.92, 7.22) * mm, "mid": v(-1.94, 7.26) * mm, "end": v(-1.98, 7.28) * mm});
            skLineSegment(sketch, "E2995", {"start": v(-1.98, 7.28) * mm, "end": v(-2.54, 7.28) * mm});
            skArc(sketch, "E2996", {"start": v(-2.54, 7.28) * mm, "mid": v(-2.59, 7.26) * mm, "end": v(-2.6, 7.22) * mm});
            skLineSegment(sketch, "E2997", {"start": v(-2.6, 7.22) * mm, "end": v(-2.6, 5.86) * mm});
            skArc(sketch, "E2998", {"start": v(-2.6, 5.86) * mm, "mid": v(-2.59, 5.82) * mm, "end": v(-2.54, 5.8) * mm});
            skLineSegment(sketch, "E2999", {"start": v(-2.54, 5.8) * mm, "end": v(-1.98, 5.8) * mm});
            skArc(sketch, "E3000", {"start": v(-1.98, 5.8) * mm, "mid": v(-1.94, 5.82) * mm, "end": v(-1.92, 5.86) * mm});
            skLineSegment(sketch, "E3001", {"start": v(2.58, 10.96) * mm, "end": v(2.58, 12.32) * mm});
            skArc(sketch, "E3002", {"start": v(2.58, 12.32) * mm, "mid": v(2.56, 12.36) * mm, "end": v(2.52, 12.38) * mm});
            skLineSegment(sketch, "E3003", {"start": v(2.52, 12.38) * mm, "end": v(1.96, 12.38) * mm});
            skArc(sketch, "E3004", {"start": v(1.96, 12.38) * mm, "mid": v(1.91, 12.36) * mm, "end": v(1.9, 12.32) * mm});
            skLineSegment(sketch, "E3005", {"start": v(1.9, 12.32) * mm, "end": v(1.9, 10.96) * mm});
            skArc(sketch, "E3006", {"start": v(1.9, 10.96) * mm, "mid": v(1.91, 10.92) * mm, "end": v(1.96, 10.9) * mm});
            skLineSegment(sketch, "E3007", {"start": v(1.96, 10.9) * mm, "end": v(2.52, 10.9) * mm});
            skArc(sketch, "E3008", {"start": v(2.52, 10.9) * mm, "mid": v(2.56, 10.92) * mm, "end": v(2.58, 10.96) * mm});
            skLineSegment(sketch, "E3009", {"start": v(-0.42, 10.96) * mm, "end": v(-0.42, 12.32) * mm});
            skArc(sketch, "E3010", {"start": v(-0.42, 12.32) * mm, "mid": v(-0.44, 12.36) * mm, "end": v(-0.48, 12.38) * mm});
            skLineSegment(sketch, "E3011", {"start": v(-0.48, 12.38) * mm, "end": v(-1.04, 12.38) * mm});
            skArc(sketch, "E3012", {"start": v(-1.04, 12.38) * mm, "mid": v(-1.09, 12.36) * mm, "end": v(-1.1, 12.32) * mm});
            skLineSegment(sketch, "E3013", {"start": v(-1.1, 12.32) * mm, "end": v(-1.1, 10.96) * mm});
            skArc(sketch, "E3014", {"start": v(-1.1, 10.96) * mm, "mid": v(-1.09, 10.92) * mm, "end": v(-1.04, 10.9) * mm});
            skLineSegment(sketch, "E3015", {"start": v(-1.04, 10.9) * mm, "end": v(-0.48, 10.9) * mm});
            skArc(sketch, "E3016", {"start": v(-0.48, 10.9) * mm, "mid": v(-0.44, 10.92) * mm, "end": v(-0.42, 10.96) * mm});
            skLineSegment(sketch, "E3017", {"start": v(-1.92, 10.96) * mm, "end": v(-1.92, 12.32) * mm});
            skArc(sketch, "E3018", {"start": v(-1.92, 12.32) * mm, "mid": v(-1.94, 12.36) * mm, "end": v(-1.98, 12.38) * mm});
            skLineSegment(sketch, "E3019", {"start": v(-1.98, 12.38) * mm, "end": v(-2.54, 12.38) * mm});
            skArc(sketch, "E3020", {"start": v(-2.54, 12.38) * mm, "mid": v(-2.59, 12.36) * mm, "end": v(-2.6, 12.32) * mm});
            skLineSegment(sketch, "E3021", {"start": v(-2.6, 12.32) * mm, "end": v(-2.6, 10.96) * mm});
            skArc(sketch, "E3022", {"start": v(-2.6, 10.96) * mm, "mid": v(-2.59, 10.92) * mm, "end": v(-2.54, 10.9) * mm});
            skLineSegment(sketch, "E3023", {"start": v(-2.54, 10.9) * mm, "end": v(-1.98, 10.9) * mm});
            skArc(sketch, "E3024", {"start": v(-1.98, 10.9) * mm, "mid": v(-1.94, 10.92) * mm, "end": v(-1.92, 10.96) * mm});
            skLineSegment(sketch, "E3025", {"start": v(3.2, 7.6) * mm, "end": v(3.2, 6.98) * mm});
            skArc(sketch, "E3026", {"start": v(3.2, 6.98) * mm, "mid": v(3.22, 6.93) * mm, "end": v(3.27, 6.9) * mm});
            skLineSegment(sketch, "E3027", {"start": v(3.27, 6.9) * mm, "end": v(4.1, 6.9) * mm});
            skArc(sketch, "E3028", {"start": v(4.1, 6.9) * mm, "mid": v(4.15, 6.93) * mm, "end": v(4.17, 6.98) * mm});
            skLineSegment(sketch, "E3029", {"start": v(4.17, 6.98) * mm, "end": v(4.17, 7.6) * mm});
            skArc(sketch, "E3030", {"start": v(4.17, 7.6) * mm, "mid": v(4.15, 7.65) * mm, "end": v(4.1, 7.67) * mm});
            skLineSegment(sketch, "E3031", {"start": v(4.1, 7.67) * mm, "end": v(3.27, 7.67) * mm});
            skArc(sketch, "E3032", {"start": v(3.27, 7.67) * mm, "mid": v(3.22, 7.65) * mm, "end": v(3.2, 7.6) * mm});
            skLineSegment(sketch, "E3033", {"start": v(3.19, 11.04) * mm, "end": v(3.19, 10.55) * mm});
            skArc(sketch, "E3034", {"start": v(3.19, 10.55) * mm, "mid": v(3.2, 10.5) * mm, "end": v(3.24, 10.5) * mm});
            skLineSegment(sketch, "E3035", {"start": v(3.24, 10.5) * mm, "end": v(4.13, 10.5) * mm});
            skArc(sketch, "E3036", {"start": v(4.13, 10.5) * mm, "mid": v(4.17, 10.5) * mm, "end": v(4.19, 10.55) * mm});
            skLineSegment(sketch, "E3037", {"start": v(4.19, 10.55) * mm, "end": v(4.19, 11.04) * mm});
            skArc(sketch, "E3038", {"start": v(4.19, 11.04) * mm, "mid": v(4.17, 11.07) * mm, "end": v(4.13, 11.09) * mm});
            skLineSegment(sketch, "E3039", {"start": v(4.13, 11.09) * mm, "end": v(3.24, 11.09) * mm});
            skArc(sketch, "E3040", {"start": v(3.24, 11.09) * mm, "mid": v(3.2, 11.07) * mm, "end": v(3.19, 11.04) * mm});
            skLineSegment(sketch, "E3041", {"start": v(-4.2, 7.6) * mm, "end": v(-4.2, 6.98) * mm});
            skArc(sketch, "E3042", {"start": v(-4.2, 6.98) * mm, "mid": v(-4.18, 6.93) * mm, "end": v(-4.13, 6.9) * mm});
            skLineSegment(sketch, "E3043", {"start": v(-4.13, 6.9) * mm, "end": v(-3.3, 6.9) * mm});
            skArc(sketch, "E3044", {"start": v(-3.3, 6.9) * mm, "mid": v(-3.25, 6.93) * mm, "end": v(-3.23, 6.98) * mm});
            skLineSegment(sketch, "E3045", {"start": v(-3.23, 6.98) * mm, "end": v(-3.23, 7.6) * mm});
            skArc(sketch, "E3046", {"start": v(-3.23, 7.6) * mm, "mid": v(-3.25, 7.65) * mm, "end": v(-3.3, 7.67) * mm});
            skLineSegment(sketch, "E3047", {"start": v(-3.3, 7.67) * mm, "end": v(-4.13, 7.67) * mm});
            skArc(sketch, "E3048", {"start": v(-4.13, 7.67) * mm, "mid": v(-4.18, 7.65) * mm, "end": v(-4.2, 7.6) * mm});
            skLineSegment(sketch, "E3049", {"start": v(-4.21, 11.04) * mm, "end": v(-4.21, 10.55) * mm});
            skArc(sketch, "E3050", {"start": v(-4.21, 10.55) * mm, "mid": v(-4.2, 10.5) * mm, "end": v(-4.16, 10.5) * mm});
            skLineSegment(sketch, "E3051", {"start": v(-4.16, 10.5) * mm, "end": v(-3.27, 10.5) * mm});
            skArc(sketch, "E3052", {"start": v(-3.27, 10.5) * mm, "mid": v(-3.23, 10.5) * mm, "end": v(-3.21, 10.55) * mm});
            skLineSegment(sketch, "E3053", {"start": v(-3.21, 10.55) * mm, "end": v(-3.21, 11.04) * mm});
            skArc(sketch, "E3054", {"start": v(-3.21, 11.04) * mm, "mid": v(-3.23, 11.07) * mm, "end": v(-3.27, 11.09) * mm});
            skLineSegment(sketch, "E3055", {"start": v(-3.27, 11.09) * mm, "end": v(-4.16, 11.09) * mm});
            skArc(sketch, "E3056", {"start": v(-4.16, 11.09) * mm, "mid": v(-4.2, 11.07) * mm, "end": v(-4.21, 11.04) * mm});
            skLineSegment(sketch, "E3057", {"start": v(-1.48, -12.76) * mm, "end": v(-1.48, -14.14) * mm});
            skArc(sketch, "E3058", {"start": v(-1.48, -14.14) * mm, "mid": v(-1.46, -14.18) * mm, "end": v(-1.42, -14.2) * mm});
            skLineSegment(sketch, "E3059", {"start": v(-1.42, -14.2) * mm, "end": v(-1.18, -14.2) * mm});
            skArc(sketch, "E3060", {"start": v(-1.18, -14.2) * mm, "mid": v(-1.14, -14.18) * mm, "end": v(-1.12, -14.14) * mm});
            skLineSegment(sketch, "E3061", {"start": v(-1.12, -14.14) * mm, "end": v(-1.12, -12.76) * mm});
            skArc(sketch, "E3062", {"start": v(-1.12, -12.76) * mm, "mid": v(-1.14, -12.71) * mm, "end": v(-1.18, -12.7) * mm});
            skLineSegment(sketch, "E3063", {"start": v(-1.18, -12.7) * mm, "end": v(-1.42, -12.7) * mm});
            skArc(sketch, "E3064", {"start": v(-1.42, -12.7) * mm, "mid": v(-1.46, -12.71) * mm, "end": v(-1.48, -12.76) * mm});
            skLineSegment(sketch, "E3065", {"start": v(-0.83, -12.76) * mm, "end": v(-0.83, -14.14) * mm});
            skArc(sketch, "E3066", {"start": v(-0.83, -14.14) * mm, "mid": v(-0.81, -14.18) * mm, "end": v(-0.77, -14.2) * mm});
            skLineSegment(sketch, "E3067", {"start": v(-0.77, -14.2) * mm, "end": v(-0.53, -14.2) * mm});
            skArc(sketch, "E3068", {"start": v(-0.53, -14.2) * mm, "mid": v(-0.49, -14.18) * mm, "end": v(-0.47, -14.14) * mm});
            skLineSegment(sketch, "E3069", {"start": v(-0.47, -14.14) * mm, "end": v(-0.47, -12.76) * mm});
            skArc(sketch, "E3070", {"start": v(-0.47, -12.76) * mm, "mid": v(-0.49, -12.71) * mm, "end": v(-0.53, -12.7) * mm});
            skLineSegment(sketch, "E3071", {"start": v(-0.53, -12.7) * mm, "end": v(-0.77, -12.7) * mm});
            skArc(sketch, "E3072", {"start": v(-0.77, -12.7) * mm, "mid": v(-0.81, -12.71) * mm, "end": v(-0.83, -12.76) * mm});
            skLineSegment(sketch, "E3073", {"start": v(-0.18, -12.76) * mm, "end": v(-0.18, -14.14) * mm});
            skArc(sketch, "E3074", {"start": v(-0.18, -14.14) * mm, "mid": v(-0.16, -14.18) * mm, "end": v(-0.12, -14.2) * mm});
            skLineSegment(sketch, "E3075", {"start": v(-0.12, -14.2) * mm, "end": v(0.12, -14.2) * mm});
            skArc(sketch, "E3076", {"start": v(0.12, -14.2) * mm, "mid": v(0.16, -14.18) * mm, "end": v(0.18, -14.14) * mm});
            skLineSegment(sketch, "E3077", {"start": v(0.18, -14.14) * mm, "end": v(0.18, -12.76) * mm});
            skArc(sketch, "E3078", {"start": v(0.18, -12.76) * mm, "mid": v(0.16, -12.71) * mm, "end": v(0.12, -12.7) * mm});
            skLineSegment(sketch, "E3079", {"start": v(0.12, -12.7) * mm, "end": v(-0.12, -12.7) * mm});
            skArc(sketch, "E3080", {"start": v(-0.12, -12.7) * mm, "mid": v(-0.16, -12.71) * mm, "end": v(-0.18, -12.76) * mm});
            skLineSegment(sketch, "E3081", {"start": v(0.47, -12.76) * mm, "end": v(0.47, -14.14) * mm});
            skArc(sketch, "E3082", {"start": v(0.47, -14.14) * mm, "mid": v(0.49, -14.18) * mm, "end": v(0.53, -14.2) * mm});
            skLineSegment(sketch, "E3083", {"start": v(0.53, -14.2) * mm, "end": v(0.77, -14.2) * mm});
            skArc(sketch, "E3084", {"start": v(0.77, -14.2) * mm, "mid": v(0.81, -14.18) * mm, "end": v(0.83, -14.14) * mm});
            skLineSegment(sketch, "E3085", {"start": v(0.83, -14.14) * mm, "end": v(0.83, -12.76) * mm});
            skArc(sketch, "E3086", {"start": v(0.83, -12.76) * mm, "mid": v(0.81, -12.71) * mm, "end": v(0.77, -12.7) * mm});
            skLineSegment(sketch, "E3087", {"start": v(0.77, -12.7) * mm, "end": v(0.53, -12.7) * mm});
            skArc(sketch, "E3088", {"start": v(0.53, -12.7) * mm, "mid": v(0.49, -12.71) * mm, "end": v(0.47, -12.76) * mm});
            skLineSegment(sketch, "E3089", {"start": v(1.12, -12.76) * mm, "end": v(1.12, -14.14) * mm});
            skArc(sketch, "E3090", {"start": v(1.12, -14.14) * mm, "mid": v(1.14, -14.18) * mm, "end": v(1.18, -14.2) * mm});
            skLineSegment(sketch, "E3091", {"start": v(1.18, -14.2) * mm, "end": v(1.42, -14.2) * mm});
            skArc(sketch, "E3092", {"start": v(1.42, -14.2) * mm, "mid": v(1.46, -14.18) * mm, "end": v(1.48, -14.14) * mm});
            skLineSegment(sketch, "E3093", {"start": v(1.48, -14.14) * mm, "end": v(1.48, -12.76) * mm});
            skArc(sketch, "E3094", {"start": v(1.48, -12.76) * mm, "mid": v(1.46, -12.71) * mm, "end": v(1.42, -12.7) * mm});
            skLineSegment(sketch, "E3095", {"start": v(1.42, -12.7) * mm, "end": v(1.18, -12.7) * mm});
            skArc(sketch, "E3096", {"start": v(1.18, -12.7) * mm, "mid": v(1.14, -12.71) * mm, "end": v(1.12, -12.76) * mm});
            skLineSegment(sketch, "E3097", {"start": v(-2.92, -13.06) * mm, "end": v(-3.88, -13.06) * mm});
            skArc(sketch, "E3098", {"start": v(-3.88, -13.06) * mm, "mid": v(-4, -13.12) * mm, "end": v(-4.06, -13.25) * mm});
            skLineSegment(sketch, "E3099", {"start": v(-4.06, -13.25) * mm, "end": v(-4.06, -14) * mm});
            skArc(sketch, "E3100", {"start": v(-4.06, -14) * mm, "mid": v(-4, -14.13) * mm, "end": v(-3.88, -14.19) * mm});
            skLineSegment(sketch, "E3101", {"start": v(-3.88, -14.19) * mm, "end": v(-2.92, -14.19) * mm});
            skArc(sketch, "E3102", {"start": v(-2.92, -14.19) * mm, "mid": v(-2.8, -14.13) * mm, "end": v(-2.74, -14) * mm});
            skLineSegment(sketch, "E3103", {"start": v(-2.74, -14) * mm, "end": v(-2.74, -13.25) * mm});
            skArc(sketch, "E3104", {"start": v(-2.74, -13.25) * mm, "mid": v(-2.8, -13.12) * mm, "end": v(-2.92, -13.06) * mm});
            skLineSegment(sketch, "E3105", {"start": v(-3.23, -16.93) * mm, "end": v(-3.23, -15.81) * mm});
            skArc(sketch, "E3106", {"start": v(-2.98, -15.81) * mm, "mid": v(-3.23, -15.56) * mm, "end": v(-3.48, -15.81) * mm});
            skArc(sketch, "E3107", {"start": v(-3.48, -16.93) * mm, "mid": v(-3.23, -17.18) * mm, "end": v(-2.98, -16.93) * mm});
            skLineSegment(sketch, "E3108", {"start": v(-0.4, -17.1) * mm, "end": v(-0.4, -16.3) * mm});
            skArc(sketch, "E3109", {"start": v(-0.4, -16.3) * mm, "mid": v(-0.46, -16.16) * mm, "end": v(-0.6, -16.1) * mm});
            skLineSegment(sketch, "E3110", {"start": v(-0.6, -16.1) * mm, "end": v(-1.4, -16.1) * mm});
            skArc(sketch, "E3111", {"start": v(-1.4, -16.1) * mm, "mid": v(-1.54, -16.16) * mm, "end": v(-1.6, -16.3) * mm});
            skLineSegment(sketch, "E3112", {"start": v(-1.6, -16.3) * mm, "end": v(-1.6, -17.1) * mm});
            skArc(sketch, "E3113", {"start": v(-1.6, -17.1) * mm, "mid": v(-1.54, -17.24) * mm, "end": v(-1.4, -17.3) * mm});
            skLineSegment(sketch, "E3114", {"start": v(-1.4, -17.3) * mm, "end": v(-0.6, -17.3) * mm});
            skArc(sketch, "E3115", {"start": v(-0.6, -17.3) * mm, "mid": v(-0.46, -17.24) * mm, "end": v(-0.4, -17.1) * mm});
            skLineSegment(sketch, "E3116", {"start": v(1.6, -17.1) * mm, "end": v(1.6, -16.3) * mm});
            skArc(sketch, "E3117", {"start": v(1.6, -16.3) * mm, "mid": v(1.54, -16.16) * mm, "end": v(1.4, -16.1) * mm});
            skLineSegment(sketch, "E3118", {"start": v(1.4, -16.1) * mm, "end": v(0.6, -16.1) * mm});
            skArc(sketch, "E3119", {"start": v(0.6, -16.1) * mm, "mid": v(0.46, -16.16) * mm, "end": v(0.4, -16.3) * mm});
            skLineSegment(sketch, "E3120", {"start": v(0.4, -16.3) * mm, "end": v(0.4, -17.1) * mm});
            skArc(sketch, "E3121", {"start": v(0.4, -17.1) * mm, "mid": v(0.46, -17.24) * mm, "end": v(0.6, -17.3) * mm});
            skLineSegment(sketch, "E3122", {"start": v(0.6, -17.3) * mm, "end": v(1.4, -17.3) * mm});
            skArc(sketch, "E3123", {"start": v(1.4, -17.3) * mm, "mid": v(1.54, -17.24) * mm, "end": v(1.6, -17.1) * mm});
            skLineSegment(sketch, "E3124", {"start": v(3.23, -16.93) * mm, "end": v(3.23, -15.81) * mm});
            skArc(sketch, "E3125", {"start": v(3.48, -15.81) * mm, "mid": v(3.23, -15.56) * mm, "end": v(2.98, -15.81) * mm});
            skArc(sketch, "E3126", {"start": v(2.98, -16.93) * mm, "mid": v(3.23, -17.18) * mm, "end": v(3.48, -16.93) * mm});
            skLineSegment(sketch, "E3127", {"start": v(3.88, -13.06) * mm, "end": v(2.92, -13.06) * mm});
            skArc(sketch, "E3128", {"start": v(2.92, -13.06) * mm, "mid": v(2.8, -13.12) * mm, "end": v(2.74, -13.25) * mm});
            skLineSegment(sketch, "E3129", {"start": v(2.74, -13.25) * mm, "end": v(2.74, -14) * mm});
            skArc(sketch, "E3130", {"start": v(2.74, -14) * mm, "mid": v(2.8, -14.13) * mm, "end": v(2.92, -14.19) * mm});
            skLineSegment(sketch, "E3131", {"start": v(2.92, -14.19) * mm, "end": v(3.88, -14.19) * mm});
            skArc(sketch, "E3132", {"start": v(3.88, -14.19) * mm, "mid": v(4, -14.13) * mm, "end": v(4.06, -14) * mm});
            skLineSegment(sketch, "E3133", {"start": v(4.06, -14) * mm, "end": v(4.06, -13.25) * mm});
            skArc(sketch, "E3134", {"start": v(4.06, -13.25) * mm, "mid": v(4, -13.12) * mm, "end": v(3.88, -13.06) * mm});
            skLineSegment(sketch, "E3135", {"start": v(0.86, -6.42) * mm, "end": v(0.86, -7.98) * mm});
            skArc(sketch, "E3136", {"start": v(0.86, -7.98) * mm, "mid": v(0.88, -8.02) * mm, "end": v(0.92, -8.04) * mm});
            skLineSegment(sketch, "E3137", {"start": v(0.92, -8.04) * mm, "end": v(1.48, -8.04) * mm});
            skArc(sketch, "E3138", {"start": v(1.48, -8.04) * mm, "mid": v(1.52, -8.02) * mm, "end": v(1.54, -7.98) * mm});
            skLineSegment(sketch, "E3139", {"start": v(1.54, -7.98) * mm, "end": v(1.54, -6.42) * mm});
            skArc(sketch, "E3140", {"start": v(1.54, -6.42) * mm, "mid": v(1.52, -6.37) * mm, "end": v(1.48, -6.36) * mm});
            skLineSegment(sketch, "E3141", {"start": v(1.48, -6.36) * mm, "end": v(0.92, -6.36) * mm});
            skArc(sketch, "E3142", {"start": v(0.92, -6.36) * mm, "mid": v(0.88, -6.37) * mm, "end": v(0.86, -6.42) * mm});
            skLineSegment(sketch, "E3143", {"start": v(-0.34, -6.42) * mm, "end": v(-0.34, -7.98) * mm});
            skArc(sketch, "E3144", {"start": v(-0.34, -7.98) * mm, "mid": v(-0.32, -8.02) * mm, "end": v(-0.28, -8.04) * mm});
            skLineSegment(sketch, "E3145", {"start": v(-0.28, -8.04) * mm, "end": v(0.28, -8.04) * mm});
            skArc(sketch, "E3146", {"start": v(0.28, -8.04) * mm, "mid": v(0.32, -8.02) * mm, "end": v(0.34, -7.98) * mm});
            skLineSegment(sketch, "E3147", {"start": v(0.34, -7.98) * mm, "end": v(0.34, -6.42) * mm});
            skArc(sketch, "E3148", {"start": v(0.34, -6.42) * mm, "mid": v(0.32, -6.37) * mm, "end": v(0.28, -6.36) * mm});
            skLineSegment(sketch, "E3149", {"start": v(0.28, -6.36) * mm, "end": v(-0.28, -6.36) * mm});
            skArc(sketch, "E3150", {"start": v(-0.28, -6.36) * mm, "mid": v(-0.32, -6.37) * mm, "end": v(-0.34, -6.42) * mm});
            skLineSegment(sketch, "E3151", {"start": v(-1.54, -6.42) * mm, "end": v(-1.54, -7.98) * mm});
            skArc(sketch, "E3152", {"start": v(-1.54, -7.98) * mm, "mid": v(-1.52, -8.02) * mm, "end": v(-1.48, -8.04) * mm});
            skLineSegment(sketch, "E3153", {"start": v(-1.48, -8.04) * mm, "end": v(-0.92, -8.04) * mm});
            skArc(sketch, "E3154", {"start": v(-0.92, -8.04) * mm, "mid": v(-0.88, -8.02) * mm, "end": v(-0.86, -7.98) * mm});
            skLineSegment(sketch, "E3155", {"start": v(-0.86, -7.98) * mm, "end": v(-0.86, -6.42) * mm});
            skArc(sketch, "E3156", {"start": v(-0.86, -6.42) * mm, "mid": v(-0.88, -6.37) * mm, "end": v(-0.92, -6.36) * mm});
            skLineSegment(sketch, "E3157", {"start": v(-0.92, -6.36) * mm, "end": v(-1.48, -6.36) * mm});
            skArc(sketch, "E3158", {"start": v(-1.48, -6.36) * mm, "mid": v(-1.52, -6.37) * mm, "end": v(-1.54, -6.42) * mm});
            skArc(sketch, "E3159", {"start": v(-5.6, -0.65) * mm, "mid": v(-5.35, -0.4) * mm, "end": v(-5.6, -0.15) * mm});
            skArc(sketch, "E3160", {"start": v(-5.6, -0.15) * mm, "mid": v(-5.85, -0.4) * mm, "end": v(-5.6, -0.65) * mm});
            skArc(sketch, "E3161", {"start": v(-5.6, -10.55) * mm, "mid": v(-5.35, -10.3) * mm, "end": v(-5.6, -10.05) * mm});
            skArc(sketch, "E3162", {"start": v(-5.6, -10.05) * mm, "mid": v(-5.85, -10.3) * mm, "end": v(-5.6, -10.55) * mm});
            skArc(sketch, "E3163", {"start": v(-5.6, -11.75) * mm, "mid": v(-5.35, -11.5) * mm, "end": v(-5.6, -11.25) * mm});
            skArc(sketch, "E3164", {"start": v(-5.6, -11.25) * mm, "mid": v(-5.85, -11.5) * mm, "end": v(-5.6, -11.75) * mm});
            skArc(sketch, "E3165", {"start": v(-4.5, -0.35) * mm, "mid": v(-4.25, -0.1) * mm, "end": v(-4.5, 0.15) * mm});
            skArc(sketch, "E3166", {"start": v(-4.5, 0.15) * mm, "mid": v(-4.75, -0.1) * mm, "end": v(-4.5, -0.35) * mm});
            skArc(sketch, "E3167", {"start": v(13.5, -2.75) * mm, "mid": v(13.75, -2.5) * mm, "end": v(13.5, -2.25) * mm});
            skArc(sketch, "E3168", {"start": v(13.5, -2.25) * mm, "mid": v(13.25, -2.5) * mm, "end": v(13.5, -2.75) * mm});
            skArc(sketch, "E3169", {"start": v(-13.4, -2.75) * mm, "mid": v(-13.15, -2.5) * mm, "end": v(-13.4, -2.25) * mm});
            skArc(sketch, "E3170", {"start": v(-13.4, -2.25) * mm, "mid": v(-13.65, -2.5) * mm, "end": v(-13.4, -2.75) * mm});
            skArc(sketch, "E3171", {"start": v(-12.3, -5.05) * mm, "mid": v(-12.05, -4.8) * mm, "end": v(-12.3, -4.55) * mm});
            skArc(sketch, "E3172", {"start": v(-12.3, -4.55) * mm, "mid": v(-12.55, -4.8) * mm, "end": v(-12.3, -5.05) * mm});
            skArc(sketch, "E3173", {"start": v(-2.38, -0.94) * mm, "mid": v(-2.13, -0.69) * mm, "end": v(-2.38, -0.44) * mm});
            skArc(sketch, "E3174", {"start": v(-2.38, -0.44) * mm, "mid": v(-2.63, -0.69) * mm, "end": v(-2.38, -0.94) * mm});
            skArc(sketch, "E3175", {"start": v(3.6, -6.75) * mm, "mid": v(3.85, -6.5) * mm, "end": v(3.6, -6.25) * mm});
            skArc(sketch, "E3176", {"start": v(3.6, -6.25) * mm, "mid": v(3.35, -6.5) * mm, "end": v(3.6, -6.75) * mm});
            skArc(sketch, "E3177", {"start": v(-3.45, 1.91) * mm, "mid": v(-3.2, 2.16) * mm, "end": v(-3.45, 2.41) * mm});
            skArc(sketch, "E3178", {"start": v(-3.45, 2.41) * mm, "mid": v(-3.7, 2.16) * mm, "end": v(-3.45, 1.91) * mm});
            skArc(sketch, "E3179", {"start": v(-6.8, -0.95) * mm, "mid": v(-6.55, -0.7) * mm, "end": v(-6.8, -0.45) * mm});
            skArc(sketch, "E3180", {"start": v(-6.8, -0.45) * mm, "mid": v(-7.05, -0.7) * mm, "end": v(-6.8, -0.95) * mm});
            skArc(sketch, "E3181", {"start": v(10.1, -8.45) * mm, "mid": v(10.35, -8.2) * mm, "end": v(10.1, -7.95) * mm});
            skArc(sketch, "E3182", {"start": v(10.1, -7.95) * mm, "mid": v(9.85, -8.2) * mm, "end": v(10.1, -8.45) * mm});
            skArc(sketch, "E3183", {"start": v(-9, 7.85) * mm, "mid": v(-8.75, 8.1) * mm, "end": v(-9, 8.35) * mm});
            skArc(sketch, "E3184", {"start": v(-9, 8.35) * mm, "mid": v(-9.25, 8.1) * mm, "end": v(-9, 7.85) * mm});
            skArc(sketch, "E3185", {"start": v(-10, -8.65) * mm, "mid": v(-9.75, -8.4) * mm, "end": v(-10, -8.15) * mm});
            skArc(sketch, "E3186", {"start": v(-10, -8.15) * mm, "mid": v(-10.25, -8.4) * mm, "end": v(-10, -8.65) * mm});
            skArc(sketch, "E3187", {"start": v(8.6, -9.9) * mm, "mid": v(8.85, -9.65) * mm, "end": v(8.6, -9.4) * mm});
            skArc(sketch, "E3188", {"start": v(8.6, -9.4) * mm, "mid": v(8.35, -9.65) * mm, "end": v(8.6, -9.9) * mm});
            skArc(sketch, "E3189", {"start": v(10.6, -6.35) * mm, "mid": v(10.85, -6.1) * mm, "end": v(10.6, -5.85) * mm});
            skArc(sketch, "E3190", {"start": v(10.6, -5.85) * mm, "mid": v(10.35, -6.1) * mm, "end": v(10.6, -6.35) * mm});
            skArc(sketch, "E3191", {"start": v(0.96, -2.22) * mm, "mid": v(1.2, -1.97) * mm, "end": v(0.96, -1.72) * mm});
            skArc(sketch, "E3192", {"start": v(0.96, -1.72) * mm, "mid": v(0.7, -1.97) * mm, "end": v(0.96, -2.22) * mm});
            skArc(sketch, "E3193", {"start": v(-0.24, -0.23) * mm, "mid": v(0, 0.02) * mm, "end": v(-0.24, 0.27) * mm});
            skArc(sketch, "E3194", {"start": v(-0.24, 0.27) * mm, "mid": v(-0.5, 0.02) * mm, "end": v(-0.24, -0.23) * mm});
            skArc(sketch, "E3195", {"start": v(-1.25, -2.14) * mm, "mid": v(-1, -1.89) * mm, "end": v(-1.25, -1.64) * mm});
            skArc(sketch, "E3196", {"start": v(-1.25, -1.64) * mm, "mid": v(-1.5, -1.89) * mm, "end": v(-1.25, -2.14) * mm});
            skArc(sketch, "E3197", {"start": v(-4.94, -13.4) * mm, "mid": v(-4.7, -13.14) * mm, "end": v(-4.94, -12.9) * mm});
            skArc(sketch, "E3198", {"start": v(-4.94, -12.9) * mm, "mid": v(-5.2, -13.14) * mm, "end": v(-4.94, -13.4) * mm});
            skArc(sketch, "E3199", {"start": v(4.95, -13.41) * mm, "mid": v(5.2, -13.16) * mm, "end": v(4.95, -12.91) * mm});
            skArc(sketch, "E3200", {"start": v(4.95, -12.91) * mm, "mid": v(4.7, -13.16) * mm, "end": v(4.95, -13.41) * mm});
            skArc(sketch, "E3201", {"start": v(-1.07, -9.25) * mm, "mid": v(-0.82, -9) * mm, "end": v(-1.07, -8.75) * mm});
            skArc(sketch, "E3202", {"start": v(-1.07, -8.75) * mm, "mid": v(-1.32, -9) * mm, "end": v(-1.07, -9.25) * mm});
            skArc(sketch, "E3203", {"start": v(2.3, -8.49) * mm, "mid": v(2.54, -8.24) * mm, "end": v(2.3, -7.99) * mm});
            skArc(sketch, "E3204", {"start": v(2.3, -7.99) * mm, "mid": v(2.04, -8.24) * mm, "end": v(2.3, -8.49) * mm});
            skArc(sketch, "E3205", {"start": v(-2.2, -15.55) * mm, "mid": v(-1.95, -15.3) * mm, "end": v(-2.2, -15.05) * mm});
            skArc(sketch, "E3206", {"start": v(-2.2, -15.05) * mm, "mid": v(-2.45, -15.3) * mm, "end": v(-2.2, -15.55) * mm});
            skArc(sketch, "E3207", {"start": v(2.2, -15.55) * mm, "mid": v(2.45, -15.3) * mm, "end": v(2.2, -15.05) * mm});
            skArc(sketch, "E3208", {"start": v(2.2, -15.05) * mm, "mid": v(1.95, -15.3) * mm, "end": v(2.2, -15.55) * mm});
            skArc(sketch, "E3209", {"start": v(1.15, 10.65) * mm, "mid": v(1.4, 10.9) * mm, "end": v(1.15, 11.15) * mm});
            skArc(sketch, "E3210", {"start": v(1.15, 11.15) * mm, "mid": v(0.9, 10.9) * mm, "end": v(1.15, 10.65) * mm});
            skArc(sketch, "E3211", {"start": v(2.93, 6.02) * mm, "mid": v(3.18, 6.27) * mm, "end": v(2.93, 6.52) * mm});
            skArc(sketch, "E3212", {"start": v(2.93, 6.52) * mm, "mid": v(2.68, 6.27) * mm, "end": v(2.93, 6.02) * mm});
            skArc(sketch, "E3213", {"start": v(-9.9, -6.55) * mm, "mid": v(-9.65, -6.3) * mm, "end": v(-9.9, -6.05) * mm});
            skArc(sketch, "E3214", {"start": v(-9.9, -6.05) * mm, "mid": v(-10.15, -6.3) * mm, "end": v(-9.9, -6.55) * mm});
            skArc(sketch, "E3215", {"start": v(-8.5, -4.75) * mm, "mid": v(-8.25, -4.5) * mm, "end": v(-8.5, -4.25) * mm});
            skArc(sketch, "E3216", {"start": v(-8.5, -4.25) * mm, "mid": v(-8.75, -4.5) * mm, "end": v(-8.5, -4.75) * mm});
            skArc(sketch, "E3217", {"start": v(10.1, 3.55) * mm, "mid": v(10.35, 3.8) * mm, "end": v(10.1, 4.05) * mm});
            skArc(sketch, "E3218", {"start": v(10.1, 4.05) * mm, "mid": v(9.85, 3.8) * mm, "end": v(10.1, 3.55) * mm});
            skArc(sketch, "E3219", {"start": v(8.09, -11.76) * mm, "mid": v(8.34, -11.5) * mm, "end": v(8.09, -11.26) * mm});
            skArc(sketch, "E3220", {"start": v(8.09, -11.26) * mm, "mid": v(7.84, -11.5) * mm, "end": v(8.09, -11.76) * mm});
            skArc(sketch, "E3221", {"start": v(-8.05, -11.76) * mm, "mid": v(-7.8, -11.5) * mm, "end": v(-8.05, -11.26) * mm});
            skArc(sketch, "E3222", {"start": v(-8.05, -11.26) * mm, "mid": v(-8.3, -11.5) * mm, "end": v(-8.05, -11.76) * mm});
            skArc(sketch, "E3223", {"start": v(-11, 0.97) * mm, "mid": v(-10.74, 1.22) * mm, "end": v(-11, 1.47) * mm});
            skArc(sketch, "E3224", {"start": v(-11, 1.47) * mm, "mid": v(-11.24, 1.22) * mm, "end": v(-11, 0.97) * mm});
            skArc(sketch, "E3225", {"start": v(-4.4, 9.63) * mm, "mid": v(-4.14, 9.88) * mm, "end": v(-4.4, 10.13) * mm});
            skArc(sketch, "E3226", {"start": v(-4.4, 10.13) * mm, "mid": v(-4.64, 9.88) * mm, "end": v(-4.4, 9.63) * mm});
            skArc(sketch, "E3227", {"start": v(2.22, -1.16) * mm, "mid": v(2.47, -0.9) * mm, "end": v(2.22, -0.66) * mm});
            skArc(sketch, "E3228", {"start": v(2.22, -0.66) * mm, "mid": v(1.97, -0.9) * mm, "end": v(2.22, -1.16) * mm});
            skArc(sketch, "E3229", {"start": v(5.72, 4.94) * mm, "mid": v(5.97, 5.19) * mm, "end": v(5.72, 5.44) * mm});
            skArc(sketch, "E3230", {"start": v(5.72, 5.44) * mm, "mid": v(5.47, 5.19) * mm, "end": v(5.72, 4.94) * mm});
            skArc(sketch, "E3231", {"start": v(1.3, -10.1) * mm, "mid": v(1.55, -9.84) * mm, "end": v(1.3, -9.6) * mm});
            skArc(sketch, "E3232", {"start": v(1.3, -9.6) * mm, "mid": v(1.05, -9.84) * mm, "end": v(1.3, -10.1) * mm});
            skArc(sketch, "E3233", {"start": v(-2.33, 7.2) * mm, "mid": v(-2.08, 7.45) * mm, "end": v(-2.33, 7.7) * mm});
            skArc(sketch, "E3234", {"start": v(-2.33, 7.7) * mm, "mid": v(-2.58, 7.45) * mm, "end": v(-2.33, 7.2) * mm});
            skArc(sketch, "E3235", {"start": v(-2.6, 8.27) * mm, "mid": v(-2.35, 8.52) * mm, "end": v(-2.6, 8.77) * mm});
            skArc(sketch, "E3236", {"start": v(-2.6, 8.77) * mm, "mid": v(-2.85, 8.52) * mm, "end": v(-2.6, 8.27) * mm});
            skArc(sketch, "E3237", {"start": v(-1.27, 2.3) * mm, "mid": v(-1.02, 2.54) * mm, "end": v(-1.27, 2.8) * mm});
            skArc(sketch, "E3238", {"start": v(-1.27, 2.8) * mm, "mid": v(-1.52, 2.54) * mm, "end": v(-1.27, 2.3) * mm});
            skArc(sketch, "E3239", {"start": v(-8.63, -0.99) * mm, "mid": v(-8.38, -0.74) * mm, "end": v(-8.63, -0.49) * mm});
            skArc(sketch, "E3240", {"start": v(-8.63, -0.49) * mm, "mid": v(-8.88, -0.74) * mm, "end": v(-8.63, -0.99) * mm});
            skArc(sketch, "E3241", {"start": v(-5.84, -5.99) * mm, "mid": v(-5.6, -5.74) * mm, "end": v(-5.84, -5.49) * mm});
            skArc(sketch, "E3242", {"start": v(-5.84, -5.49) * mm, "mid": v(-6.1, -5.74) * mm, "end": v(-5.84, -5.99) * mm});
            skArc(sketch, "E3243", {"start": v(-3, -11.75) * mm, "mid": v(-2.75, -11.5) * mm, "end": v(-3, -11.25) * mm});
            skArc(sketch, "E3244", {"start": v(-3, -11.25) * mm, "mid": v(-3.25, -11.5) * mm, "end": v(-3, -11.75) * mm});
            skArc(sketch, "E3245", {"start": v(0, -15.15) * mm, "mid": v(0.25, -14.9) * mm, "end": v(0, -14.65) * mm});
            skArc(sketch, "E3246", {"start": v(0, -14.65) * mm, "mid": v(-0.25, -14.9) * mm, "end": v(0, -15.15) * mm});
            skArc(sketch, "E3247", {"start": v(4.4, 1.7) * mm, "mid": v(4.65, 1.95) * mm, "end": v(4.4, 2.2) * mm});
            skArc(sketch, "E3248", {"start": v(4.4, 2.2) * mm, "mid": v(4.15, 1.95) * mm, "end": v(4.4, 1.7) * mm});
            skArc(sketch, "E3249", {"start": v(4.13, 3.8) * mm, "mid": v(4.38, 4.05) * mm, "end": v(4.13, 4.3) * mm});
            skArc(sketch, "E3250", {"start": v(4.13, 4.3) * mm, "mid": v(3.88, 4.05) * mm, "end": v(4.13, 3.8) * mm});
            skArc(sketch, "E3251", {"start": v(-10.57, 4.14) * mm, "mid": v(-10.32, 4.4) * mm, "end": v(-10.57, 4.64) * mm});
            skArc(sketch, "E3252", {"start": v(-10.57, 4.64) * mm, "mid": v(-10.82, 4.4) * mm, "end": v(-10.57, 4.14) * mm});
            skArc(sketch, "E3253", {"start": v(4.24, 5.99) * mm, "mid": v(4.5, 6.24) * mm, "end": v(4.24, 6.49) * mm});
            skArc(sketch, "E3254", {"start": v(4.24, 6.49) * mm, "mid": v(4, 6.24) * mm, "end": v(4.24, 5.99) * mm});
            skArc(sketch, "E3255", {"start": v(6.4, 1.65) * mm, "mid": v(6.65, 1.9) * mm, "end": v(6.4, 2.15) * mm});
            skArc(sketch, "E3256", {"start": v(6.4, 2.15) * mm, "mid": v(6.15, 1.9) * mm, "end": v(6.4, 1.65) * mm});
            skArc(sketch, "E3257", {"start": v(11.2, 4.8) * mm, "mid": v(11.45, 5.04) * mm, "end": v(11.2, 5.3) * mm});
            skArc(sketch, "E3258", {"start": v(11.2, 5.3) * mm, "mid": v(10.95, 5.04) * mm, "end": v(11.2, 4.8) * mm});
            skArc(sketch, "E3259", {"start": v(3.4, 1.25) * mm, "mid": v(3.65, 1.5) * mm, "end": v(3.4, 1.75) * mm});
            skArc(sketch, "E3260", {"start": v(3.4, 1.75) * mm, "mid": v(3.15, 1.5) * mm, "end": v(3.4, 1.25) * mm});
            skArc(sketch, "E3261", {"start": v(3.06, 3.76) * mm, "mid": v(3.31, 4) * mm, "end": v(3.06, 4.26) * mm});
            skArc(sketch, "E3262", {"start": v(3.06, 4.26) * mm, "mid": v(2.81, 4) * mm, "end": v(3.06, 3.76) * mm});
            skArc(sketch, "E3263", {"start": v(9.23, -2.53) * mm, "mid": v(9.48, -2.28) * mm, "end": v(9.23, -2.03) * mm});
            skArc(sketch, "E3264", {"start": v(9.23, -2.03) * mm, "mid": v(8.98, -2.28) * mm, "end": v(9.23, -2.53) * mm});
            skArc(sketch, "E3265", {"start": v(11.5, -8.55) * mm, "mid": v(11.75, -8.3) * mm, "end": v(11.5, -8.05) * mm});
            skArc(sketch, "E3266", {"start": v(11.5, -8.05) * mm, "mid": v(11.25, -8.3) * mm, "end": v(11.5, -8.55) * mm});
            skArc(sketch, "E3267", {"start": v(10.8, -11.37) * mm, "mid": v(11.05, -11.12) * mm, "end": v(10.8, -10.87) * mm});
            skArc(sketch, "E3268", {"start": v(10.8, -10.87) * mm, "mid": v(10.55, -11.12) * mm, "end": v(10.8, -11.37) * mm});
            skArc(sketch, "E3269", {"start": v(-3.35, -5.54) * mm, "mid": v(-3.1, -5.29) * mm, "end": v(-3.35, -5.04) * mm});
            skArc(sketch, "E3270", {"start": v(-3.35, -5.04) * mm, "mid": v(-3.6, -5.29) * mm, "end": v(-3.35, -5.54) * mm});
            skArc(sketch, "E3271", {"start": v(-10.68, -11.48) * mm, "mid": v(-10.43, -11.23) * mm, "end": v(-10.68, -10.98) * mm});
            skArc(sketch, "E3272", {"start": v(-10.68, -10.98) * mm, "mid": v(-10.93, -11.23) * mm, "end": v(-10.68, -11.48) * mm});
            skArc(sketch, "E3273", {"start": v(6.1, -11.35) * mm, "mid": v(6.35, -11.1) * mm, "end": v(6.1, -10.85) * mm});
            skArc(sketch, "E3274", {"start": v(6.1, -10.85) * mm, "mid": v(5.85, -11.1) * mm, "end": v(6.1, -11.35) * mm});
            skArc(sketch, "E3275", {"start": v(10.35, -0.85) * mm, "mid": v(10.6, -0.6) * mm, "end": v(10.35, -0.35) * mm});
            skArc(sketch, "E3276", {"start": v(10.35, -0.35) * mm, "mid": v(10.1, -0.6) * mm, "end": v(10.35, -0.85) * mm});
            skArc(sketch, "E3277", {"start": v(8.8, 1.65) * mm, "mid": v(9.05, 1.9) * mm, "end": v(8.8, 2.15) * mm});
            skArc(sketch, "E3278", {"start": v(8.8, 2.15) * mm, "mid": v(8.55, 1.9) * mm, "end": v(8.8, 1.65) * mm});
            skArc(sketch, "E3279", {"start": v(8.9, 3.85) * mm, "mid": v(9.16, 4.1) * mm, "end": v(8.9, 4.35) * mm});
            skArc(sketch, "E3280", {"start": v(8.9, 4.35) * mm, "mid": v(8.66, 4.1) * mm, "end": v(8.9, 3.85) * mm});
            skArc(sketch, "E3281", {"start": v(-0.74, 7.09) * mm, "mid": v(-0.5, 7.34) * mm, "end": v(-0.74, 7.59) * mm});
            skArc(sketch, "E3282", {"start": v(-0.74, 7.59) * mm, "mid": v(-1, 7.34) * mm, "end": v(-0.74, 7.09) * mm});
            skArc(sketch, "E3283", {"start": v(0, -4.49) * mm, "mid": v(0.26, -4.24) * mm, "end": v(0, -3.99) * mm});
            skArc(sketch, "E3284", {"start": v(0, -3.99) * mm, "mid": v(-0.24, -4.24) * mm, "end": v(0, -4.49) * mm});
            skArc(sketch, "E3285", {"start": v(0.85, -3.72) * mm, "mid": v(1.1, -3.47) * mm, "end": v(0.85, -3.22) * mm});
            skArc(sketch, "E3286", {"start": v(0.85, -3.22) * mm, "mid": v(0.6, -3.47) * mm, "end": v(0.85, -3.72) * mm});
            skArc(sketch, "E3287", {"start": v(1.73, -2.98) * mm, "mid": v(1.98, -2.73) * mm, "end": v(1.73, -2.48) * mm});
            skArc(sketch, "E3288", {"start": v(1.73, -2.48) * mm, "mid": v(1.48, -2.73) * mm, "end": v(1.73, -2.98) * mm});
            skArc(sketch, "E3289", {"start": v(2.3, -6.75) * mm, "mid": v(2.55, -6.5) * mm, "end": v(2.3, -6.25) * mm});
            skArc(sketch, "E3290", {"start": v(2.3, -6.25) * mm, "mid": v(2.05, -6.5) * mm, "end": v(2.3, -6.75) * mm});
            skArc(sketch, "E3291", {"start": v(9.65, 0) * mm, "mid": v(9.9, 0.25) * mm, "end": v(9.65, 0.5) * mm});
            skArc(sketch, "E3292", {"start": v(9.65, 0.5) * mm, "mid": v(9.4, 0.25) * mm, "end": v(9.65, 0) * mm});
            skArc(sketch, "E3293", {"start": v(7.9, 0) * mm, "mid": v(8.15, 0.25) * mm, "end": v(7.9, 0.5) * mm});
            skArc(sketch, "E3294", {"start": v(7.9, 0.5) * mm, "mid": v(7.65, 0.25) * mm, "end": v(7.9, 0) * mm});
            skArc(sketch, "E3295", {"start": v(-7.3, -6.05) * mm, "mid": v(-7.05, -5.8) * mm, "end": v(-7.3, -5.55) * mm});
            skArc(sketch, "E3296", {"start": v(-7.3, -5.55) * mm, "mid": v(-7.55, -5.8) * mm, "end": v(-7.3, -6.05) * mm});
            skArc(sketch, "E3297", {"start": v(-5.9, -8.35) * mm, "mid": v(-5.65, -8.1) * mm, "end": v(-5.9, -7.85) * mm});
            skArc(sketch, "E3298", {"start": v(-5.9, -7.85) * mm, "mid": v(-6.15, -8.1) * mm, "end": v(-5.9, -8.35) * mm});
            skArc(sketch, "E3299", {"start": v(-9.9, -2.95) * mm, "mid": v(-9.65, -2.7) * mm, "end": v(-9.9, -2.45) * mm});
            skArc(sketch, "E3300", {"start": v(-9.9, -2.45) * mm, "mid": v(-10.15, -2.7) * mm, "end": v(-9.9, -2.95) * mm});
            skArc(sketch, "E3301", {"start": v(-2.32, -3.23) * mm, "mid": v(-2.07, -2.98) * mm, "end": v(-2.32, -2.73) * mm});
            skArc(sketch, "E3302", {"start": v(-2.32, -2.73) * mm, "mid": v(-2.57, -2.98) * mm, "end": v(-2.32, -3.23) * mm});
            skArc(sketch, "E3303", {"start": v(2.62, -10.61) * mm, "mid": v(2.87, -10.36) * mm, "end": v(2.62, -10.11) * mm});
            skArc(sketch, "E3304", {"start": v(2.62, -10.11) * mm, "mid": v(2.37, -10.36) * mm, "end": v(2.62, -10.61) * mm});
            skArc(sketch, "E3305", {"start": v(-1.2, -10.53) * mm, "mid": v(-0.96, -10.28) * mm, "end": v(-1.2, -10.03) * mm});
            skArc(sketch, "E3306", {"start": v(-1.2, -10.03) * mm, "mid": v(-1.46, -10.28) * mm, "end": v(-1.2, -10.53) * mm});
            skArc(sketch, "E3307", {"start": v(-6.7, -7.45) * mm, "mid": v(-6.45, -7.2) * mm, "end": v(-6.7, -6.95) * mm});
            skArc(sketch, "E3308", {"start": v(-6.7, -6.95) * mm, "mid": v(-6.95, -7.2) * mm, "end": v(-6.7, -7.45) * mm});
            skArc(sketch, "E3309", {"start": v(-2.24, 0.23) * mm, "mid": v(-2, 0.48) * mm, "end": v(-2.24, 0.73) * mm});
            skArc(sketch, "E3310", {"start": v(-2.24, 0.73) * mm, "mid": v(-2.5, 0.48) * mm, "end": v(-2.24, 0.23) * mm});
            skArc(sketch, "E3311", {"start": v(9, 7.85) * mm, "mid": v(9.25, 8.1) * mm, "end": v(9, 8.35) * mm});
            skArc(sketch, "E3312", {"start": v(9, 8.35) * mm, "mid": v(8.75, 8.1) * mm, "end": v(9, 7.85) * mm});
            skArc(sketch, "E3313", {"start": v(3.95, 8.43) * mm, "mid": v(4.2, 8.68) * mm, "end": v(3.95, 8.93) * mm});
            skArc(sketch, "E3314", {"start": v(3.95, 8.93) * mm, "mid": v(3.7, 8.68) * mm, "end": v(3.95, 8.43) * mm});
            skArc(sketch, "E3315", {"start": v(0.84, 6.2) * mm, "mid": v(1.09, 6.45) * mm, "end": v(0.84, 6.7) * mm});
            skArc(sketch, "E3316", {"start": v(0.84, 6.7) * mm, "mid": v(0.59, 6.45) * mm, "end": v(0.84, 6.2) * mm});
            skSolve(sketch);
        }
        {
            var Q0;
            Q0=qCreatedBy(makeId("Top.planeOp"),FACE);
            var sketch = newSketch(context, id + "F1", { "sketchPlane" : qUnion([Q0])});
            skPoint(sketch, "E3317.0", {"position": v(-15, -2.36) * mm});
            skPoint(sketch, "E3318.0", {"position": v(-12, -11.35) * mm});
            skPoint(sketch, "E3319.0", {"position": v(15, -2.36) * mm});
            skPoint(sketch, "E3320.0", {"position": v(12.04, -11.28) * mm});
            skArc(sketch, "E3321", {"start": v(-15, -2.36) * mm, "mid": v(-14.22, -7.1) * mm, "end": v(-12, -11.35) * mm});
            skArc(sketch, "E3322", {"start": v(12.04, -11.28) * mm, "mid": v(14.24, -7.06) * mm, "end": v(15, -2.36) * mm});
            skPoint(sketch, "E3323.0", {"position": v(-12.44, 6) * mm});
            skPoint(sketch, "E3324.0", {"position": v(12.59, 5.8) * mm});
            skLineSegment(sketch, "E3325", {"start": v(-15, -2.36) * mm, "end": v(-12.44, 6) * mm});
            skLineSegment(sketch, "E3326", {"start": v(15, -2.36) * mm, "end": v(12.59, 5.8) * mm});
            skLineSegment(sketch, "E3327", {"start": v(12.04, -11.28) * mm, "end": v(-12, -11.35) * mm});
            skLineSegment(sketch, "E3328", {"start": v(-12.44, 6) * mm, "end": v(-5.84, 3.99) * mm});
            skLineSegment(sketch, "E3329", {"start": v(-5.84, 3.99) * mm, "end": v(-5.28, 5.8) * mm});
            skLineSegment(sketch, "E3330", {"start": v(-5.28, 5.8) * mm, "end": v(0, 5.8) * mm});
            skLineSegment(sketch, "E3331.MirrorCS", {"start": v(5.28, 5.8) * mm, "end": v(0, 5.8) * mm});
            skLineSegment(sketch, "E3332.MirrorCS", {"start": v(5.84, 3.99) * mm, "end": v(5.28, 5.8) * mm});
            skLineSegment(sketch, "E3333.MirrorCS", {"start": v(12.44, 6) * mm, "end": v(5.84, 3.99) * mm});
            skLineSegment(sketch, "E3334", {"start": v(12.59, 5.8) * mm, "end": v(12.44, 6) * mm});
            skArc(sketch, "E3335.0", {"start": v(-17, -2.37) * mm, "mid": v(-16.34, -7.04) * mm, "end": v(-14.42, -11.35) * mm});
            skArc(sketch, "E3336.0", {"start": v(14.46, -11.28) * mm, "mid": v(16.35, -7) * mm, "end": v(17, -2.37) * mm});
            skLineSegment(sketch, "E3337", {"start": v(15, -2.36) * mm, "end": v(17, -2.37) * mm});
            skLineSegment(sketch, "E3338", {"start": v(-15, -2.36) * mm, "end": v(-17, -2.37) * mm});
            skArc(sketch, "E3339.0", {"start": v(-15.5, -2.36) * mm, "mid": v(-14.76, -7.08) * mm, "end": v(-12.62, -11.34) * mm});
            skArc(sketch, "E3340.0", {"start": v(12.66, -11.28) * mm, "mid": v(14.77, -7.04) * mm, "end": v(15.5, -2.36) * mm});
            skLineSegment(sketch, "E3341", {"start": v(-12, -11.35) * mm, "end": v(-14.42, -11.35) * mm});
            skLineSegment(sketch, "E3342", {"start": v(-14.42, -11.35) * mm, "end": v(12.04, -11.28) * mm});
            skLineSegment(sketch, "E3343", {"start": v(12.04, -11.28) * mm, "end": v(14.46, -11.28) * mm});
            skSolve(sketch);
        }
        {
            var Q0;
            {var subQ0=sQuery(id+"F1.wireOp",EDGE,"E3335.0");Q0=makeQuery(id+"F1.imprint","IMPRINT",FACE,{"disambiguationData":[TD([[makeQuery(id+"F1.imprint","IMPRINT",EDGE,{"derivedFrom":subQ0}),1.0]])]});}
            var Q1;
            {var subQ5=sQuery(id+"F1.wireOp",EDGE,"E3339.0");Q1=makeQuery(id+"F1.imprint","IMPRINT",FACE,{"disambiguationData":[TD([[makeQuery(id+"F1.imprint","IMPRINT",EDGE,{"derivedFrom":subQ5}),1.0]])]});}
            var Q2;
            {var subQ4=sQuery(id+"F1.wireOp",EDGE,"E3322");Q2=makeQuery(id+"F1.imprint","IMPRINT",FACE,{"disambiguationData":[TD([[makeQuery(id+"F1.imprint","IMPRINT",EDGE,{"derivedFrom":subQ4}),1.0]])]});}
            var Q3;
            {var subQ0=sQuery(id+"F1.wireOp",EDGE,"E3322");Q3=makeQuery(id+"F1.imprint","IMPRINT",FACE,{"disambiguationData":[TD([[makeQuery(id+"F1.imprint","IMPRINT",EDGE,{"derivedFrom":subQ0}),-1.0]])]});}
            var Q4;
            {var subQ0=sQuery(id+"F1.wireOp",EDGE,"E3336.0");Q4=makeQuery(id+"F1.imprint","IMPRINT",FACE,{"disambiguationData":[TD([[makeQuery(id+"F1.imprint","IMPRINT",EDGE,{"derivedFrom":subQ0}),1.0]])]});}
            extrude(context, id + "F2", {"entities" : qUnion([Q0, Q1, Q2, Q3, Q4]), "depth" : 2 * mm});
        }
        {
            var Q0;
            Q0=makeQuery(id+"F2.opExtrude","CAP_FACE",FACE,{"disambiguationData":[OSD([sQuery(id+"F1.wireOp",EDGE,"E3325"),sQuery(id+"F1.wireOp",EDGE,"E3326"),sQuery(id+"F1.wireOp",EDGE,"E3328"),sQuery(id+"F1.wireOp",EDGE,"E3329"),sQuery(id+"F1.wireOp",EDGE,"E3330"),sQuery(id+"F1.wireOp",EDGE,"E3331.MirrorCS"),sQuery(id+"F1.wireOp",EDGE,"E3332.MirrorCS"),sQuery(id+"F1.wireOp",EDGE,"E3333.MirrorCS"),sQuery(id+"F1.wireOp",EDGE,"E3334"),sQuery(id+"F1.wireOp",EDGE,"E3335.0"),sQuery(id+"F1.wireOp",EDGE,"E3336.0"),sQuery(id+"F1.wireOp",EDGE,"E3337"),sQuery(id+"F1.wireOp",EDGE,"E3338"),sQuery(id+"F1.wireOp",EDGE,"E3342"),sQuery(id+"F1.wireOp",EDGE,"E3343")])],"isStart":false});
            var sketch = newSketch(context, id + "F3", { "sketchPlane" : qUnion([Q0])});
            skArc(sketch, "E3344.0", {"start": v(-15, -2.36) * mm, "mid": v(-14.22, -7.1) * mm, "end": v(-12, -11.35) * mm});
            skArc(sketch, "E3345.0", {"start": v(-17, -2.37) * mm, "mid": v(-16.34, -7.04) * mm, "end": v(-14.42, -11.35) * mm});
            skPoint(sketch, "E3346.0", {"position": v(-16, -2.37) * mm});
            skLineSegment(sketch, "E3347.0", {"start": v(-14.42, -11.35) * mm, "end": v(12.04, -11.28) * mm});
            skLineSegment(sketch, "E3348.0", {"start": v(12.04, -11.28) * mm, "end": v(14.46, -11.28) * mm});
            skArc(sketch, "E3349.0", {"start": v(14.46, -11.28) * mm, "mid": v(16.35, -7) * mm, "end": v(17, -2.37) * mm});
            skLineSegment(sketch, "E3350.0", {"start": v(15, -2.36) * mm, "end": v(17, -2.37) * mm});
            skArc(sketch, "E3351.0", {"start": v(12.04, -11.28) * mm, "mid": v(14.24, -7.06) * mm, "end": v(15, -2.36) * mm});
            skArc(sketch, "E3352.0", {"start": v(-15.5, -2.36) * mm, "mid": v(-14.76, -7.08) * mm, "end": v(-12.62, -11.34) * mm});
            skArc(sketch, "E3353.0", {"start": v(12.66, -11.28) * mm, "mid": v(14.77, -7.04) * mm, "end": v(15.5, -2.36) * mm});
            skSolve(sketch);
        }
        {
            var Q0;
            {var subQ0=sQuery(id+"F3.wireOp",EDGE,"E3345.0");Q0=makeQuery(id+"F3.imprint","IMPRINT",FACE,{"disambiguationData":[TD([[makeQuery(id+"F3.imprint","IMPRINT",EDGE,{"derivedFrom":subQ0}),1.0]])]});}
            var Q1;
            {var subQ0=sQuery(id+"F3.wireOp",EDGE,"E3349.0");Q1=makeQuery(id+"F3.imprint","IMPRINT",FACE,{"disambiguationData":[TD([[makeQuery(id+"F3.imprint","IMPRINT",EDGE,{"derivedFrom":subQ0}),1.0]])]});}
            extrude(context, id + "F4", {"entities" : qUnion([Q0, Q1]), "operationType" : NewBodyOperationType.ADD, "depth" : 2.75 * mm});
        }
        {
            var Q0;
            Q0=makeQuery(id+"F4.opExtrude","CAP_FACE",FACE,{"disambiguationData":[OSD([sQuery(id+"F1.wireOp",EDGE,"E3338"),sQuery(id+"F3.wireOp",EDGE,"E3344.0"),sQuery(id+"F3.wireOp",EDGE,"E3345.0"),sQuery(id+"F3.wireOp",EDGE,"E3347.0")])],"isStart":false});
            var sketch = newSketch(context, id + "F5", { "sketchPlane" : qUnion([Q0])});
            skArc(sketch, "E3354.0", {"start": v(-15, -2.36) * mm, "mid": v(-14.22, -7.1) * mm, "end": v(-12, -11.35) * mm});
            skLineSegment(sketch, "E3355.0", {"start": v(-15, -2.36) * mm, "end": v(-17, -2.37) * mm});
            skArc(sketch, "E3356.0", {"start": v(-17, -2.37) * mm, "mid": v(-16.34, -7.04) * mm, "end": v(-14.42, -11.35) * mm});
            skLineSegment(sketch, "E3357.0", {"start": v(-14.42, -11.35) * mm, "end": v(12.04, -11.28) * mm});
            skArc(sketch, "E3358.0", {"start": v(14.46, -11.28) * mm, "mid": v(16.35, -7) * mm, "end": v(17, -2.37) * mm});
            skLineSegment(sketch, "E3359.0", {"start": v(12.04, -11.28) * mm, "end": v(14.46, -11.28) * mm});
            skArc(sketch, "E3360.0", {"start": v(12.04, -11.28) * mm, "mid": v(14.24, -7.06) * mm, "end": v(15, -2.36) * mm});
            skLineSegment(sketch, "E3361.0", {"start": v(15, -2.36) * mm, "end": v(17, -2.37) * mm});
            skArc(sketch, "E3362.0", {"start": v(-13, -2.36) * mm, "mid": v(-12.06, -7.2) * mm, "end": v(-9.38, -11.34) * mm});
            skArc(sketch, "E3363.0", {"start": v(9.43, -11.3) * mm, "mid": v(12.07, -7.17) * mm, "end": v(13, -2.36) * mm});
            skLineSegment(sketch, "E3364", {"start": v(-13, -2.36) * mm, "end": v(-15, -2.36) * mm});
            skLineSegment(sketch, "E3365", {"start": v(13, -2.36) * mm, "end": v(15, -2.36) * mm});
            skSolve(sketch);
        }
        {
            var Q0;
            {var subQ0=sQuery(id+"F5.wireOp",EDGE,"E3355.0");Q0=makeQuery(id+"F5.imprint","IMPRINT",FACE,{"disambiguationData":[TD([[makeQuery(id+"F5.imprint","IMPRINT",EDGE,{"derivedFrom":subQ0}),1.0]])]});}
            var Q1;
            {var subQ4=sQuery(id+"F5.wireOp",EDGE,"E3362.0");Q1=makeQuery(id+"F5.imprint","IMPRINT",FACE,{"disambiguationData":[TD([[makeQuery(id+"F5.imprint","IMPRINT",EDGE,{"derivedFrom":subQ4}),-1.0]])]});}
            var Q2;
            {var subQ0=sQuery(id+"F5.wireOp",EDGE,"E3360.0");Q2=makeQuery(id+"F5.imprint","IMPRINT",FACE,{"disambiguationData":[TD([[makeQuery(id+"F5.imprint","IMPRINT",EDGE,{"derivedFrom":subQ0}),1.0]])]});}
            var Q3;
            Q3=makeQuery(id+"F5.imprint","IMPRINT",FACE,{"disambiguationData":[TD([[makeQuery(id+"F5.imprint","IMPRINT",EDGE,{"derivedFrom":sQuery(id+"F5.wireOp",EDGE,"E3358.0")}),1.0]])]});
            extrude(context, id + "F6", {"entities" : qUnion([Q0, Q1, Q2, Q3]), "operationType" : NewBodyOperationType.ADD, "depth" : 2 * mm});
        }
        {
            var Q0;
            Q0=makeQuery(id+"F6.opExtrude","CAP_EDGE",EDGE,{"disambiguationData":[OSD([sQuery(id+"F5.wireOp",EDGE,"E3362.0")])],"isStart":false});
            var Q1;
            Q1=makeQuery(id+"F6.opExtrude","CAP_EDGE",EDGE,{"disambiguationData":[OSD([sQuery(id+"F5.wireOp",EDGE,"E3363.0")])],"isStart":false});
            chamfer(context, id + "F7", {"entities" : qUnion([Q0, Q1]), "width" : 3 * mm, "tangentPropagation" : true});
        }
        {
            var Q0;
            {var subQ0=sQuery(id+"F1.wireOp",EDGE,"E3336.0");Q0=makeQuery(id+"F1.imprint","IMPRINT",FACE,{"disambiguationData":[TD([[makeQuery(id+"F1.imprint","IMPRINT",EDGE,{"derivedFrom":subQ0}),1.0]])]});}
            var sketch = newSketch(context, id + "F8", { "sketchPlane" : qUnion([Q0])});
            skArc(sketch, "E3366.0", {"start": v(14.46, -11.28) * mm, "mid": v(16.35, -7) * mm, "end": v(17, -2.37) * mm});
            skPoint(sketch, "E3367.1.internal.snap0", {"position": v(16.35, -7) * mm});
            skFitSpline(sketch, "E3367", {"points": [v(16.35, -7) * mm, v(21.7, -7) * mm, v(30.04, -5.02) * mm, v(35.35, 0.87) * mm, v(34.72, 3.95) * mm, v(33.7, 6.4) * mm, v(31.7, 10.12) * mm, v(32.15, 12.29) * mm, v(33.18, 12.06) * mm, v(33.06, 10.12) * mm, v(33.46, 8.57) * mm, v(34.66, 7.6) * mm, v(34.38, 9.89) * mm, v(34.26, 11.83) * mm, v(35.4, 12) * mm, v(35.46, 9.72) * mm, v(35.46, 8.18) * mm, v(36.03, 7.32) * mm, v(36.5, 9.03) * mm, v(36.5, 10.97) * mm, v(36.66, 12.17) * mm, v(37.98, 11.94) * mm, v(38.03, 9.83) * mm, v(37.69, 7.78) * mm, v(38.2, 7.26) * mm, v(39, 9.6) * mm, v(39.23, 11.66) * mm, v(40.83, 11.72) * mm, v(40.15, 9.43) * mm, v(39.35, 7.38) * mm, v(39, 5.55) * mm, v(38.6, 4) * mm, v(38.09, 2.35) * mm, v(36.15, -2.96) * mm, v(30.72, -7.59) * mm, v(19.7, -9.41) * mm, v(15.56, -9.18) * mm, v(16.35, -7) * mm]});
            skFitSpline(sketch, "E3368.MirrorC", {"points": [v(-16.35, -7) * mm, v(-21.7, -7) * mm, v(-30.04, -5.02) * mm, v(-35.35, 0.87) * mm, v(-34.72, 3.95) * mm, v(-33.7, 6.4) * mm, v(-31.7, 10.12) * mm, v(-32.15, 12.29) * mm, v(-33.18, 12.06) * mm, v(-33.06, 10.12) * mm, v(-33.46, 8.57) * mm, v(-34.66, 7.6) * mm, v(-34.38, 9.89) * mm, v(-34.26, 11.83) * mm, v(-35.4, 12) * mm, v(-35.46, 9.72) * mm, v(-35.46, 8.18) * mm, v(-36.03, 7.32) * mm, v(-36.5, 9.03) * mm, v(-36.5, 10.97) * mm, v(-36.66, 12.17) * mm, v(-37.98, 11.94) * mm, v(-38.03, 9.83) * mm, v(-37.69, 7.78) * mm, v(-38.2, 7.26) * mm, v(-39, 9.6) * mm, v(-39.23, 11.66) * mm, v(-40.83, 11.72) * mm, v(-40.15, 9.43) * mm, v(-39.35, 7.38) * mm, v(-39, 5.55) * mm, v(-38.6, 4) * mm, v(-38.09, 2.35) * mm, v(-36.15, -2.96) * mm, v(-30.72, -7.59) * mm, v(-19.7, -9.41) * mm, v(-15.56, -9.18) * mm, v(-16.35, -7) * mm]});
            skSolve(sketch);
        }
        {
            var Q0;
            {var subQ0=sQuery(id+"F8.wireOp",EDGE,"E3367");var subQ1=sQuery(id+"F8.wireOp",EDGE,"E3366.0");var subQ2=makeQuery(id+"F8.imprint","INTERSECT",VERTEX,{"disambiguationData":[OD(0.0)],"derivedFrom":[subQ1,subQ0]});Q0=makeQuery(id+"F8.imprint","IMPRINT",FACE,{"disambiguationData":[TD([[makeQuery(id+"F8.imprint","IMPRINT",EDGE,{"disambiguationData":[TD([[subQ2,-1.0]])],"derivedFrom":subQ1}),-1.0]])]});}
            var Q1;
            Q1=makeQuery(id+"F8.imprint","IMPRINT",FACE,{"disambiguationData":[TD([[makeQuery(id+"F8.imprint","IMPRINT",EDGE,{"derivedFrom":sQuery(id+"F8.wireOp",EDGE,"E3368.MirrorC")}),1.0]])]});
            extrude(context, id + "F9", {"entities" : qUnion([Q0, Q1]), "operationType" : NewBodyOperationType.ADD, "depth" : 2 * mm});
        }
        {
            var Q0;
            {var subQ4=sQuery(id+"F1.wireOp",EDGE,"E3322");Q0=makeQuery(id+"F1.imprint","IMPRINT",FACE,{"disambiguationData":[TD([[makeQuery(id+"F1.imprint","IMPRINT",EDGE,{"derivedFrom":subQ4}),1.0]])]});}
            var sketch = newSketch(context, id + "F10", { "sketchPlane" : qUnion([Q0])});
            skCircle(sketch, "E3369", {"center": v(5.15, 0) * mm, "radius": 1.5 * mm});
            skCircle(sketch, "E3370", {"center": v(-5.15, 0) * mm, "radius": 1.5 * mm});
            skArc(sketch, "E3371", {"start": v(-6.35, -8.2) * mm, "mid": v(1.17, -8) * mm, "end": v(8.18, -5.25) * mm});
            skLineSegment(sketch, "E3372", {"start": v(8.18, -5.25) * mm, "end": v(-6.35, -8.2) * mm});
            skSolve(sketch);
        }
        {
            var Q0;
            Q0=makeQuery(id+"F10.imprint","IMPRINT",FACE,{"disambiguationData":[TD([[makeQuery(id+"F10.imprint","IMPRINT",EDGE,{"derivedFrom":sQuery(id+"F10.wireOp",EDGE,"E3369")}),1.0]])]});
            var Q1;
            Q1=makeQuery(id+"F10.imprint","IMPRINT",FACE,{"disambiguationData":[TD([[makeQuery(id+"F10.imprint","IMPRINT",EDGE,{"derivedFrom":sQuery(id+"F10.wireOp",EDGE,"E3370")}),1.0]])]});
            extrude(context, id + "F11", {"entities" : qUnion([Q0, Q1]), "oppositeDirection" : true, "depth" : 1 * mm});
        }
        {
            var Q0;
            Q0=makeQuery(id+"F10.imprint","IMPRINT",FACE,{"disambiguationData":[TD([[makeQuery(id+"F10.imprint","IMPRINT",EDGE,{"derivedFrom":sQuery(id+"F10.wireOp",EDGE,"E3371")}),1.0]])]});
            extrude(context, id + "F12", {"entities" : qUnion([Q0]), "operationType" : NewBodyOperationType.REMOVE, "depth" : 2 * mm});
        }
        {
            var Q0;
            Q0=makeQuery(id+"F2.opExtrude","CAP_FACE",FACE,{"disambiguationData":[OSD([sQuery(id+"F1.wireOp",EDGE,"E3325"),sQuery(id+"F1.wireOp",EDGE,"E3326"),sQuery(id+"F1.wireOp",EDGE,"E3328"),sQuery(id+"F1.wireOp",EDGE,"E3329"),sQuery(id+"F1.wireOp",EDGE,"E3330"),sQuery(id+"F1.wireOp",EDGE,"E3331.MirrorCS"),sQuery(id+"F1.wireOp",EDGE,"E3332.MirrorCS"),sQuery(id+"F1.wireOp",EDGE,"E3333.MirrorCS"),sQuery(id+"F1.wireOp",EDGE,"E3334"),sQuery(id+"F1.wireOp",EDGE,"E3335.0"),sQuery(id+"F1.wireOp",EDGE,"E3336.0"),sQuery(id+"F1.wireOp",EDGE,"E3337"),sQuery(id+"F1.wireOp",EDGE,"E3338"),sQuery(id+"F1.wireOp",EDGE,"E3342"),sQuery(id+"F1.wireOp",EDGE,"E3343")])],"isStart":false});
            var sketch = newSketch(context, id + "F13", { "sketchPlane" : qUnion([Q0])});
            skLineSegment(sketch, "E3373.0.0", {"start": v(30.23, 5.25) * mm, "end": v(30.22, 5.42) * mm});
            skLineSegment(sketch, "E3373.0.1", {"start": v(30.22, 5.42) * mm, "end": v(30.18, 5.6) * mm});
            skLineSegment(sketch, "E3373.0.2", {"start": v(30.18, 5.6) * mm, "end": v(29.1, 8.94) * mm});
            skLineSegment(sketch, "E3373.0.3", {"start": v(29.1, 8.94) * mm, "end": v(29.03, 9.1) * mm});
            skLineSegment(sketch, "E3373.0.4", {"start": v(29.03, 9.1) * mm, "end": v(28.93, 9.25) * mm});
            skLineSegment(sketch, "E3373.0.5", {"start": v(28.93, 9.25) * mm, "end": v(28.81, 9.38) * mm});
            skLineSegment(sketch, "E3373.0.6", {"start": v(28.81, 9.38) * mm, "end": v(28.67, 9.48) * mm});
            skLineSegment(sketch, "E3373.0.7", {"start": v(28.67, 9.48) * mm, "end": v(28.52, 9.56) * mm});
            skLineSegment(sketch, "E3373.0.8", {"start": v(28.52, 9.56) * mm, "end": v(28.36, 9.6) * mm});
            skLineSegment(sketch, "E3373.0.9", {"start": v(28.36, 9.6) * mm, "end": v(28.18, 9.63) * mm});
            skLineSegment(sketch, "E3373.0.10", {"start": v(28.18, 9.63) * mm, "end": v(28, 9.62) * mm});
            skLineSegment(sketch, "E3373.0.11", {"start": v(28, 9.62) * mm, "end": v(22.92, 8.87) * mm});
            skLineSegment(sketch, "E3373.0.12", {"start": v(22.92, 8.87) * mm, "end": v(21.71, 8.48) * mm});
            skLineSegment(sketch, "E3373.0.13", {"start": v(21.71, 8.48) * mm, "end": v(21.66, 8.46) * mm});
            skLineSegment(sketch, "E3373.0.14", {"start": v(21.66, 8.46) * mm, "end": v(21.62, 8.44) * mm});
            skLineSegment(sketch, "E3373.0.15", {"start": v(21.62, 8.44) * mm, "end": v(21.58, 8.4) * mm});
            skLineSegment(sketch, "E3373.0.16", {"start": v(21.58, 8.4) * mm, "end": v(21.54, 8.38) * mm});
            skLineSegment(sketch, "E3373.0.17", {"start": v(21.54, 8.38) * mm, "end": v(21.5, 8.34) * mm});
            skLineSegment(sketch, "E3373.0.18", {"start": v(21.5, 8.34) * mm, "end": v(21.47, 8.3) * mm});
            skLineSegment(sketch, "E3373.0.19", {"start": v(21.47, 8.3) * mm, "end": v(21.44, 8.26) * mm});
            skLineSegment(sketch, "E3373.0.20", {"start": v(21.44, 8.26) * mm, "end": v(21.32, 8.03) * mm});
            skLineSegment(sketch, "E3373.0.21", {"start": v(21.32, 8.03) * mm, "end": v(21.2, 7.86) * mm});
            skLineSegment(sketch, "E3373.0.22", {"start": v(21.2, 7.86) * mm, "end": v(21.07, 7.7) * mm});
            skLineSegment(sketch, "E3373.0.23", {"start": v(21.07, 7.7) * mm, "end": v(20.92, 7.56) * mm});
            skLineSegment(sketch, "E3373.0.24", {"start": v(20.92, 7.56) * mm, "end": v(20.77, 7.43) * mm});
            skLineSegment(sketch, "E3373.0.25", {"start": v(20.77, 7.43) * mm, "end": v(20.6, 7.32) * mm});
            skLineSegment(sketch, "E3373.0.26", {"start": v(20.6, 7.32) * mm, "end": v(20.4, 7.22) * mm});
            skLineSegment(sketch, "E3373.0.27", {"start": v(20.4, 7.22) * mm, "end": v(20.22, 7.15) * mm});
            skLineSegment(sketch, "E3373.0.28", {"start": v(20.22, 7.15) * mm, "end": v(20.02, 7.1) * mm});
            skLineSegment(sketch, "E3373.0.29", {"start": v(20.02, 7.1) * mm, "end": v(19.81, 7.06) * mm});
            skLineSegment(sketch, "E3373.0.30", {"start": v(19.81, 7.06) * mm, "end": v(19.6, 7.05) * mm});
            skLineSegment(sketch, "E3373.0.31", {"start": v(19.6, 7.05) * mm, "end": v(19.4, 7.06) * mm});
            skLineSegment(sketch, "E3373.0.32", {"start": v(19.4, 7.06) * mm, "end": v(19.2, 7.1) * mm});
            skLineSegment(sketch, "E3373.0.33", {"start": v(19.2, 7.1) * mm, "end": v(19, 7.14) * mm});
            skLineSegment(sketch, "E3373.0.34", {"start": v(19, 7.14) * mm, "end": v(18.8, 7.21) * mm});
            skLineSegment(sketch, "E3373.0.35", {"start": v(18.8, 7.21) * mm, "end": v(18.58, 7.33) * mm});
            skLineSegment(sketch, "E3373.0.36", {"start": v(18.58, 7.33) * mm, "end": v(18.53, 7.35) * mm});
            skLineSegment(sketch, "E3373.0.37", {"start": v(18.53, 7.35) * mm, "end": v(18.48, 7.36) * mm});
            skLineSegment(sketch, "E3373.0.38", {"start": v(18.48, 7.36) * mm, "end": v(18.43, 7.37) * mm});
            skLineSegment(sketch, "E3373.0.39", {"start": v(18.43, 7.37) * mm, "end": v(18.38, 7.37) * mm});
            skLineSegment(sketch, "E3373.0.40", {"start": v(18.38, 7.37) * mm, "end": v(18.33, 7.37) * mm});
            skLineSegment(sketch, "E3373.0.41", {"start": v(18.33, 7.37) * mm, "end": v(18.28, 7.36) * mm});
            skLineSegment(sketch, "E3373.0.42", {"start": v(18.28, 7.36) * mm, "end": v(18.23, 7.34) * mm});
            skLineSegment(sketch, "E3373.0.43", {"start": v(18.23, 7.34) * mm, "end": v(13.03, 5.66) * mm});
            skLineSegment(sketch, "E3373.0.44", {"start": v(13.03, 5.66) * mm, "end": v(13, 5.65) * mm});
            skLineSegment(sketch, "E3373.0.45", {"start": v(13, 5.65) * mm, "end": v(12.96, 5.65) * mm});
            skLineSegment(sketch, "E3373.0.46", {"start": v(12.96, 5.65) * mm, "end": v(12.92, 5.64) * mm});
            skLineSegment(sketch, "E3373.0.47", {"start": v(12.92, 5.64) * mm, "end": v(12.88, 5.64) * mm});
            skLineSegment(sketch, "E3373.0.48", {"start": v(12.88, 5.64) * mm, "end": v(12.83, 5.64) * mm});
            skLineSegment(sketch, "E3373.0.49", {"start": v(12.83, 5.64) * mm, "end": v(12.8, 5.64) * mm});
            skLineSegment(sketch, "E3373.0.50", {"start": v(12.8, 5.64) * mm, "end": v(12.76, 5.65) * mm});
            skLineSegment(sketch, "E3373.0.51", {"start": v(12.76, 5.65) * mm, "end": v(12.73, 5.66) * mm});
            skLineSegment(sketch, "E3373.0.52", {"start": v(12.73, 5.66) * mm, "end": v(12.7, 5.68) * mm});
            skLineSegment(sketch, "E3373.0.53", {"start": v(12.7, 5.68) * mm, "end": v(12.67, 5.7) * mm});
            skLineSegment(sketch, "E3373.0.54", {"start": v(12.67, 5.7) * mm, "end": v(12.65, 5.72) * mm});
            skLineSegment(sketch, "E3373.0.55", {"start": v(12.65, 5.72) * mm, "end": v(12.63, 5.74) * mm});
            skLineSegment(sketch, "E3373.0.56", {"start": v(12.63, 5.74) * mm, "end": v(12.6, 5.77) * mm});
            skLineSegment(sketch, "E3373.0.57", {"start": v(12.6, 5.77) * mm, "end": v(12.59, 5.8) * mm});
            skLineSegment(sketch, "E3373.0.58", {"start": v(12.59, 5.8) * mm, "end": v(12.4, 6.07) * mm});
            skLineSegment(sketch, "E3373.0.59", {"start": v(12.4, 6.07) * mm, "end": v(12.1, 6.48) * mm});
            skLineSegment(sketch, "E3373.0.60", {"start": v(12.1, 6.48) * mm, "end": v(12.1, 6.5) * mm});
            skLineSegment(sketch, "E3373.0.61", {"start": v(12.1, 6.5) * mm, "end": v(12.09, 6.52) * mm});
            skLineSegment(sketch, "E3373.0.62", {"start": v(12.09, 6.52) * mm, "end": v(12.08, 6.54) * mm});
            skLineSegment(sketch, "E3373.0.63", {"start": v(12.08, 6.54) * mm, "end": v(12.07, 6.56) * mm});
            skLineSegment(sketch, "E3373.0.64", {"start": v(12.07, 6.56) * mm, "end": v(12.06, 6.58) * mm});
            skLineSegment(sketch, "E3373.0.65", {"start": v(12.06, 6.58) * mm, "end": v(12.06, 6.6) * mm});
            skLineSegment(sketch, "E3373.0.66", {"start": v(12.06, 6.6) * mm, "end": v(12.06, 6.63) * mm});
            skLineSegment(sketch, "E3373.0.67", {"start": v(12.06, 6.63) * mm, "end": v(12.05, 6.65) * mm});
            skLineSegment(sketch, "E3373.0.68", {"start": v(12.05, 6.65) * mm, "end": v(12.05, 6.67) * mm});
            skLineSegment(sketch, "E3373.0.69", {"start": v(12.05, 6.67) * mm, "end": v(12.06, 6.7) * mm});
            skLineSegment(sketch, "E3373.0.70", {"start": v(12.06, 6.7) * mm, "end": v(12.06, 6.71) * mm});
            skLineSegment(sketch, "E3373.0.71", {"start": v(12.06, 6.71) * mm, "end": v(12.06, 6.73) * mm});
            skLineSegment(sketch, "E3373.0.72", {"start": v(12.06, 6.73) * mm, "end": v(12.06, 6.73) * mm});
            skLineSegment(sketch, "E3373.0.73", {"start": v(12.06, 6.73) * mm, "end": v(12.09, 6.78) * mm});
            skLineSegment(sketch, "E3373.0.74", {"start": v(12.09, 6.78) * mm, "end": v(12.2, 7.09) * mm});
            skLineSegment(sketch, "E3373.0.75", {"start": v(12.2, 7.09) * mm, "end": v(12.28, 7.42) * mm});
            skLineSegment(sketch, "E3373.0.76", {"start": v(12.28, 7.42) * mm, "end": v(12.34, 7.75) * mm});
            skLineSegment(sketch, "E3373.0.77", {"start": v(12.34, 7.75) * mm, "end": v(12.35, 8.1) * mm});
            skLineSegment(sketch, "E3373.0.78", {"start": v(12.35, 8.1) * mm, "end": v(12.34, 8.45) * mm});
            skLineSegment(sketch, "E3373.0.79", {"start": v(12.34, 8.45) * mm, "end": v(12.28, 8.79) * mm});
            skLineSegment(sketch, "E3373.0.80", {"start": v(12.28, 8.79) * mm, "end": v(12.2, 9.11) * mm});
            skLineSegment(sketch, "E3373.0.81", {"start": v(12.2, 9.11) * mm, "end": v(12.09, 9.42) * mm});
            skLineSegment(sketch, "E3373.0.82", {"start": v(12.09, 9.42) * mm, "end": v(11.94, 9.72) * mm});
            skLineSegment(sketch, "E3373.0.83", {"start": v(11.94, 9.72) * mm, "end": v(11.77, 10) * mm});
            skLineSegment(sketch, "E3373.0.84", {"start": v(11.77, 10) * mm, "end": v(11.58, 10.26) * mm});
            skLineSegment(sketch, "E3373.0.85", {"start": v(11.58, 10.26) * mm, "end": v(11.36, 10.5) * mm});
            skLineSegment(sketch, "E3373.0.86", {"start": v(11.36, 10.5) * mm, "end": v(11.12, 10.72) * mm});
            skLineSegment(sketch, "E3373.0.87", {"start": v(11.12, 10.72) * mm, "end": v(10.85, 10.92) * mm});
            skLineSegment(sketch, "E3373.0.88", {"start": v(10.85, 10.92) * mm, "end": v(10.57, 11.09) * mm});
            skLineSegment(sketch, "E3373.0.89", {"start": v(10.57, 11.09) * mm, "end": v(10.28, 11.23) * mm});
            skLineSegment(sketch, "E3373.0.90", {"start": v(10.28, 11.23) * mm, "end": v(9.96, 11.35) * mm});
            skLineSegment(sketch, "E3373.0.91", {"start": v(9.96, 11.35) * mm, "end": v(9.64, 11.43) * mm});
            skLineSegment(sketch, "E3373.0.92", {"start": v(9.64, 11.43) * mm, "end": v(9.3, 11.48) * mm});
            skLineSegment(sketch, "E3373.0.93", {"start": v(9.3, 11.48) * mm, "end": v(8.95, 11.5) * mm});
            skLineSegment(sketch, "E3373.0.94", {"start": v(8.95, 11.5) * mm, "end": v(8.6, 11.48) * mm});
            skLineSegment(sketch, "E3373.0.95", {"start": v(8.6, 11.48) * mm, "end": v(8.27, 11.43) * mm});
            skLineSegment(sketch, "E3373.0.96", {"start": v(8.27, 11.43) * mm, "end": v(7.94, 11.35) * mm});
            skLineSegment(sketch, "E3373.0.97", {"start": v(7.94, 11.35) * mm, "end": v(7.63, 11.23) * mm});
            skLineSegment(sketch, "E3373.0.98", {"start": v(7.63, 11.23) * mm, "end": v(7.33, 11.1) * mm});
            skLineSegment(sketch, "E3373.0.99", {"start": v(7.33, 11.1) * mm, "end": v(7.05, 10.92) * mm});
            skLineSegment(sketch, "E3373.0.100", {"start": v(7.05, 10.92) * mm, "end": v(6.8, 10.72) * mm});
            skLineSegment(sketch, "E3373.0.101", {"start": v(6.8, 10.72) * mm, "end": v(6.63, 10.58) * mm});
            skLineSegment(sketch, "E3373.0.102", {"start": v(6.63, 10.58) * mm, "end": v(6.55, 10.51) * mm});
            skLineSegment(sketch, "E3373.0.103", {"start": v(6.55, 10.51) * mm, "end": v(6.47, 10.47) * mm});
            skLineSegment(sketch, "E3373.0.104", {"start": v(6.47, 10.47) * mm, "end": v(6.37, 10.44) * mm});
            skLineSegment(sketch, "E3373.0.105", {"start": v(6.37, 10.44) * mm, "end": v(6.27, 10.43) * mm});
            skLineSegment(sketch, "E3373.0.106", {"start": v(6.27, 10.43) * mm, "end": v(6.17, 10.44) * mm});
            skLineSegment(sketch, "E3373.0.107", {"start": v(6.17, 10.44) * mm, "end": v(6.08, 10.47) * mm});
            skLineSegment(sketch, "E3373.0.108", {"start": v(6.08, 10.47) * mm, "end": v(6.02, 10.5) * mm});
            skLineSegment(sketch, "E3373.0.109", {"start": v(6.02, 10.5) * mm, "end": v(5.84, 10.58) * mm});
            skLineSegment(sketch, "E3373.0.110", {"start": v(5.84, 10.58) * mm, "end": v(5.53, 10.72) * mm});
            skLineSegment(sketch, "E3373.0.111", {"start": v(5.53, 10.72) * mm, "end": v(5.2, 10.85) * mm});
            skLineSegment(sketch, "E3373.0.112", {"start": v(5.2, 10.85) * mm, "end": v(4.88, 10.97) * mm});
            skLineSegment(sketch, "E3373.0.113", {"start": v(4.88, 10.97) * mm, "end": v(4.56, 11.1) * mm});
            skLineSegment(sketch, "E3373.0.114", {"start": v(4.56, 11.1) * mm, "end": v(4.22, 11.2) * mm});
            skLineSegment(sketch, "E3373.0.115", {"start": v(4.22, 11.2) * mm, "end": v(4.02, 11.26) * mm});
            skLineSegment(sketch, "E3373.0.116", {"start": v(4.02, 11.26) * mm, "end": v(3.9, 11.29) * mm});
            skLineSegment(sketch, "E3373.0.117", {"start": v(3.9, 11.29) * mm, "end": v(3.82, 11.34) * mm});
            skLineSegment(sketch, "E3373.0.118", {"start": v(3.82, 11.34) * mm, "end": v(3.75, 11.4) * mm});
            skLineSegment(sketch, "E3373.0.119", {"start": v(3.75, 11.4) * mm, "end": v(3.68, 11.47) * mm});
            skLineSegment(sketch, "E3373.0.120", {"start": v(3.68, 11.47) * mm, "end": v(3.64, 11.56) * mm});
            skLineSegment(sketch, "E3373.0.121", {"start": v(3.64, 11.56) * mm, "end": v(3.6, 11.65) * mm});
            skLineSegment(sketch, "E3373.0.122", {"start": v(3.6, 11.65) * mm, "end": v(3.6, 11.76) * mm});
            skLineSegment(sketch, "E3373.0.123", {"start": v(3.6, 11.76) * mm, "end": v(3.6, 17.97) * mm});
            skLineSegment(sketch, "E3373.0.124", {"start": v(3.6, 17.97) * mm, "end": v(3.6, 18.02) * mm});
            skLineSegment(sketch, "E3373.0.125", {"start": v(3.6, 18.02) * mm, "end": v(3.59, 18.07) * mm});
            skLineSegment(sketch, "E3373.0.126", {"start": v(3.59, 18.07) * mm, "end": v(3.58, 18.12) * mm});
            skLineSegment(sketch, "E3373.0.127", {"start": v(3.58, 18.12) * mm, "end": v(3.56, 18.17) * mm});
            skLineSegment(sketch, "E3373.0.128", {"start": v(3.56, 18.17) * mm, "end": v(3.54, 18.21) * mm});
            skLineSegment(sketch, "E3373.0.129", {"start": v(3.54, 18.21) * mm, "end": v(3.5, 18.26) * mm});
            skLineSegment(sketch, "E3373.0.130", {"start": v(3.5, 18.26) * mm, "end": v(3.48, 18.3) * mm});
            skLineSegment(sketch, "E3373.0.131", {"start": v(3.48, 18.3) * mm, "end": v(3.3, 18.48) * mm});
            skLineSegment(sketch, "E3373.0.132", {"start": v(3.3, 18.48) * mm, "end": v(3.17, 18.65) * mm});
            skLineSegment(sketch, "E3373.0.133", {"start": v(3.17, 18.65) * mm, "end": v(3.06, 18.82) * mm});
            skLineSegment(sketch, "E3373.0.134", {"start": v(3.06, 18.82) * mm, "end": v(2.97, 19) * mm});
            skLineSegment(sketch, "E3373.0.135", {"start": v(2.97, 19) * mm, "end": v(2.9, 19.2) * mm});
            skLineSegment(sketch, "E3373.0.136", {"start": v(2.9, 19.2) * mm, "end": v(2.84, 19.4) * mm});
            skLineSegment(sketch, "E3373.0.137", {"start": v(2.84, 19.4) * mm, "end": v(2.81, 19.6) * mm});
            skLineSegment(sketch, "E3373.0.138", {"start": v(2.81, 19.6) * mm, "end": v(2.8, 19.8) * mm});
            skLineSegment(sketch, "E3373.0.139", {"start": v(2.8, 19.8) * mm, "end": v(2.81, 20) * mm});
            skLineSegment(sketch, "E3373.0.140", {"start": v(2.81, 20) * mm, "end": v(2.84, 20.21) * mm});
            skLineSegment(sketch, "E3373.0.141", {"start": v(2.84, 20.21) * mm, "end": v(2.9, 20.41) * mm});
            skLineSegment(sketch, "E3373.0.142", {"start": v(2.9, 20.41) * mm, "end": v(2.97, 20.6) * mm});
            skLineSegment(sketch, "E3373.0.143", {"start": v(2.97, 20.6) * mm, "end": v(3.06, 20.78) * mm});
            skLineSegment(sketch, "E3373.0.144", {"start": v(3.06, 20.78) * mm, "end": v(3.17, 20.96) * mm});
            skLineSegment(sketch, "E3373.0.145", {"start": v(3.17, 20.96) * mm, "end": v(3.3, 21.12) * mm});
            skLineSegment(sketch, "E3373.0.146", {"start": v(3.3, 21.12) * mm, "end": v(3.48, 21.3) * mm});
            skLineSegment(sketch, "E3373.0.147", {"start": v(3.48, 21.3) * mm, "end": v(3.5, 21.35) * mm});
            skLineSegment(sketch, "E3373.0.148", {"start": v(3.5, 21.35) * mm, "end": v(3.54, 21.39) * mm});
            skLineSegment(sketch, "E3373.0.149", {"start": v(3.54, 21.39) * mm, "end": v(3.56, 21.44) * mm});
            skLineSegment(sketch, "E3373.0.150", {"start": v(3.56, 21.44) * mm, "end": v(3.58, 21.48) * mm});
            skLineSegment(sketch, "E3373.0.151", {"start": v(3.58, 21.48) * mm, "end": v(3.59, 21.53) * mm});
            skLineSegment(sketch, "E3373.0.152", {"start": v(3.59, 21.53) * mm, "end": v(3.6, 21.58) * mm});
            skLineSegment(sketch, "E3373.0.153", {"start": v(3.6, 21.58) * mm, "end": v(3.6, 21.63) * mm});
            skLineSegment(sketch, "E3373.0.154", {"start": v(3.6, 21.63) * mm, "end": v(3.6, 22.9) * mm});
            skLineSegment(sketch, "E3373.0.155", {"start": v(3.6, 22.9) * mm, "end": v(2.74, 27.97) * mm});
            skLineSegment(sketch, "E3373.0.156", {"start": v(2.74, 27.97) * mm, "end": v(2.7, 28.14) * mm});
            skLineSegment(sketch, "E3373.0.157", {"start": v(2.7, 28.14) * mm, "end": v(2.62, 28.3) * mm});
            skLineSegment(sketch, "E3373.0.158", {"start": v(2.62, 28.3) * mm, "end": v(2.52, 28.44) * mm});
            skLineSegment(sketch, "E3373.0.159", {"start": v(2.52, 28.44) * mm, "end": v(2.4, 28.57) * mm});
            skLineSegment(sketch, "E3373.0.160", {"start": v(2.4, 28.57) * mm, "end": v(2.26, 28.67) * mm});
            skLineSegment(sketch, "E3373.0.161", {"start": v(2.26, 28.67) * mm, "end": v(2.1, 28.74) * mm});
            skLineSegment(sketch, "E3373.0.162", {"start": v(2.1, 28.74) * mm, "end": v(1.93, 28.79) * mm});
            skLineSegment(sketch, "E3373.0.163", {"start": v(1.93, 28.79) * mm, "end": v(1.76, 28.8) * mm});
            skLineSegment(sketch, "E3373.0.164", {"start": v(1.76, 28.8) * mm, "end": v(-1.4, 28.8) * mm});
            skLineSegment(sketch, "E3373.0.165", {"start": v(-1.4, 28.8) * mm, "end": v(-1.7, 28.8) * mm});
            skLineSegment(sketch, "E3373.0.166", {"start": v(-1.7, 28.8) * mm, "end": v(-1.76, 28.8) * mm});
            skLineSegment(sketch, "E3373.0.167", {"start": v(-1.76, 28.8) * mm, "end": v(-1.93, 28.79) * mm});
            skLineSegment(sketch, "E3373.0.168", {"start": v(-1.93, 28.79) * mm, "end": v(-2.1, 28.74) * mm});
            skLineSegment(sketch, "E3373.0.169", {"start": v(-2.1, 28.74) * mm, "end": v(-2.26, 28.67) * mm});
            skLineSegment(sketch, "E3373.0.170", {"start": v(-2.26, 28.67) * mm, "end": v(-2.4, 28.57) * mm});
            skLineSegment(sketch, "E3373.0.171", {"start": v(-2.4, 28.57) * mm, "end": v(-2.52, 28.44) * mm});
            skLineSegment(sketch, "E3373.0.172", {"start": v(-2.52, 28.44) * mm, "end": v(-2.62, 28.3) * mm});
            skLineSegment(sketch, "E3373.0.173", {"start": v(-2.62, 28.3) * mm, "end": v(-2.7, 28.14) * mm});
            skLineSegment(sketch, "E3373.0.174", {"start": v(-2.7, 28.14) * mm, "end": v(-2.74, 27.97) * mm});
            skLineSegment(sketch, "E3373.0.175", {"start": v(-2.74, 27.97) * mm, "end": v(-3.6, 22.9) * mm});
            skLineSegment(sketch, "E3373.0.176", {"start": v(-3.6, 22.9) * mm, "end": v(-3.6, 21.63) * mm});
            skLineSegment(sketch, "E3373.0.177", {"start": v(-3.6, 21.63) * mm, "end": v(-3.6, 21.58) * mm});
            skLineSegment(sketch, "E3373.0.178", {"start": v(-3.6, 21.58) * mm, "end": v(-3.59, 21.53) * mm});
            skLineSegment(sketch, "E3373.0.179", {"start": v(-3.59, 21.53) * mm, "end": v(-3.58, 21.48) * mm});
            skLineSegment(sketch, "E3373.0.180", {"start": v(-3.58, 21.48) * mm, "end": v(-3.56, 21.44) * mm});
            skLineSegment(sketch, "E3373.0.181", {"start": v(-3.56, 21.44) * mm, "end": v(-3.53, 21.39) * mm});
            skLineSegment(sketch, "E3373.0.182", {"start": v(-3.53, 21.39) * mm, "end": v(-3.5, 21.35) * mm});
            skLineSegment(sketch, "E3373.0.183", {"start": v(-3.5, 21.35) * mm, "end": v(-3.48, 21.3) * mm});
            skLineSegment(sketch, "E3373.0.184", {"start": v(-3.48, 21.3) * mm, "end": v(-3.3, 21.12) * mm});
            skLineSegment(sketch, "E3373.0.185", {"start": v(-3.3, 21.12) * mm, "end": v(-3.17, 20.96) * mm});
            skLineSegment(sketch, "E3373.0.186", {"start": v(-3.17, 20.96) * mm, "end": v(-3.06, 20.78) * mm});
            skLineSegment(sketch, "E3373.0.187", {"start": v(-3.06, 20.78) * mm, "end": v(-2.97, 20.6) * mm});
            skLineSegment(sketch, "E3373.0.188", {"start": v(-2.97, 20.6) * mm, "end": v(-2.9, 20.41) * mm});
            skLineSegment(sketch, "E3373.0.189", {"start": v(-2.9, 20.41) * mm, "end": v(-2.84, 20.21) * mm});
            skLineSegment(sketch, "E3373.0.190", {"start": v(-2.84, 20.21) * mm, "end": v(-2.8, 20) * mm});
            skLineSegment(sketch, "E3373.0.191", {"start": v(-2.8, 20) * mm, "end": v(-2.8, 19.8) * mm});
            skLineSegment(sketch, "E3373.0.192", {"start": v(-2.8, 19.8) * mm, "end": v(-2.8, 19.6) * mm});
            skLineSegment(sketch, "E3373.0.193", {"start": v(-2.8, 19.6) * mm, "end": v(-2.84, 19.4) * mm});
            skLineSegment(sketch, "E3373.0.194", {"start": v(-2.84, 19.4) * mm, "end": v(-2.9, 19.2) * mm});
            skLineSegment(sketch, "E3373.0.195", {"start": v(-2.9, 19.2) * mm, "end": v(-2.97, 19) * mm});
            skLineSegment(sketch, "E3373.0.196", {"start": v(-2.97, 19) * mm, "end": v(-3.06, 18.82) * mm});
            skLineSegment(sketch, "E3373.0.197", {"start": v(-3.06, 18.82) * mm, "end": v(-3.17, 18.65) * mm});
            skLineSegment(sketch, "E3373.0.198", {"start": v(-3.17, 18.65) * mm, "end": v(-3.3, 18.48) * mm});
            skLineSegment(sketch, "E3373.0.199", {"start": v(-3.3, 18.48) * mm, "end": v(-3.48, 18.3) * mm});
            skLineSegment(sketch, "E3373.0.200", {"start": v(-3.48, 18.3) * mm, "end": v(-3.5, 18.26) * mm});
            skLineSegment(sketch, "E3373.0.201", {"start": v(-3.5, 18.26) * mm, "end": v(-3.53, 18.21) * mm});
            skLineSegment(sketch, "E3373.0.202", {"start": v(-3.53, 18.21) * mm, "end": v(-3.56, 18.17) * mm});
            skLineSegment(sketch, "E3373.0.203", {"start": v(-3.56, 18.17) * mm, "end": v(-3.58, 18.12) * mm});
            skLineSegment(sketch, "E3373.0.204", {"start": v(-3.58, 18.12) * mm, "end": v(-3.59, 18.07) * mm});
            skLineSegment(sketch, "E3373.0.205", {"start": v(-3.59, 18.07) * mm, "end": v(-3.6, 18.02) * mm});
            skLineSegment(sketch, "E3373.0.206", {"start": v(-3.6, 18.02) * mm, "end": v(-3.6, 17.97) * mm});
            skLineSegment(sketch, "E3373.0.207", {"start": v(-3.6, 17.97) * mm, "end": v(-3.6, 11.83) * mm});
            skLineSegment(sketch, "E3373.0.208", {"start": v(-3.6, 11.83) * mm, "end": v(-3.6, 11.66) * mm});
            skLineSegment(sketch, "E3373.0.209", {"start": v(-3.6, 11.66) * mm, "end": v(-3.63, 11.56) * mm});
            skLineSegment(sketch, "E3373.0.210", {"start": v(-3.63, 11.56) * mm, "end": v(-3.68, 11.48) * mm});
            skLineSegment(sketch, "E3373.0.211", {"start": v(-3.68, 11.48) * mm, "end": v(-3.74, 11.4) * mm});
            skLineSegment(sketch, "E3373.0.212", {"start": v(-3.74, 11.4) * mm, "end": v(-3.81, 11.34) * mm});
            skLineSegment(sketch, "E3373.0.213", {"start": v(-3.81, 11.34) * mm, "end": v(-3.9, 11.3) * mm});
            skLineSegment(sketch, "E3373.0.214", {"start": v(-3.9, 11.3) * mm, "end": v(-3.94, 11.28) * mm});
            skLineSegment(sketch, "E3373.0.215", {"start": v(-3.94, 11.28) * mm, "end": v(-3.94, 11.28) * mm});
            skLineSegment(sketch, "E3373.0.216", {"start": v(-3.94, 11.28) * mm, "end": v(-4, 11.27) * mm});
            skLineSegment(sketch, "E3373.0.217", {"start": v(-4, 11.27) * mm, "end": v(-4.22, 11.2) * mm});
            skLineSegment(sketch, "E3373.0.218", {"start": v(-4.22, 11.2) * mm, "end": v(-4.55, 11.1) * mm});
            skLineSegment(sketch, "E3373.0.219", {"start": v(-4.55, 11.1) * mm, "end": v(-4.88, 10.97) * mm});
            skLineSegment(sketch, "E3373.0.220", {"start": v(-4.88, 10.97) * mm, "end": v(-5.2, 10.85) * mm});
            skLineSegment(sketch, "E3373.0.221", {"start": v(-5.2, 10.85) * mm, "end": v(-5.53, 10.72) * mm});
            skLineSegment(sketch, "E3373.0.222", {"start": v(-5.53, 10.72) * mm, "end": v(-5.84, 10.58) * mm});
            skLineSegment(sketch, "E3373.0.223", {"start": v(-5.84, 10.58) * mm, "end": v(-6.12, 10.45) * mm});
            skLineSegment(sketch, "E3373.0.224", {"start": v(-6.12, 10.45) * mm, "end": v(-6.12, 10.45) * mm});
            skLineSegment(sketch, "E3373.0.225", {"start": v(-6.12, 10.45) * mm, "end": v(-6.22, 10.42) * mm});
            skLineSegment(sketch, "E3373.0.226", {"start": v(-6.22, 10.42) * mm, "end": v(-6.32, 10.41) * mm});
            skLineSegment(sketch, "E3373.0.227", {"start": v(-6.32, 10.41) * mm, "end": v(-6.42, 10.42) * mm});
            skLineSegment(sketch, "E3373.0.228", {"start": v(-6.42, 10.42) * mm, "end": v(-6.51, 10.45) * mm});
            skLineSegment(sketch, "E3373.0.229", {"start": v(-6.51, 10.45) * mm, "end": v(-6.6, 10.5) * mm});
            skLineSegment(sketch, "E3373.0.230", {"start": v(-6.6, 10.5) * mm, "end": v(-6.66, 10.55) * mm});
            skLineSegment(sketch, "E3373.0.231", {"start": v(-6.66, 10.55) * mm, "end": v(-6.66, 10.55) * mm});
            skLineSegment(sketch, "E3373.0.232", {"start": v(-6.66, 10.55) * mm, "end": v(-6.85, 10.72) * mm});
            skLineSegment(sketch, "E3373.0.233", {"start": v(-6.85, 10.72) * mm, "end": v(-7.12, 10.92) * mm});
            skLineSegment(sketch, "E3373.0.234", {"start": v(-7.12, 10.92) * mm, "end": v(-7.4, 11.09) * mm});
            skLineSegment(sketch, "E3373.0.235", {"start": v(-7.4, 11.09) * mm, "end": v(-7.7, 11.23) * mm});
            skLineSegment(sketch, "E3373.0.236", {"start": v(-7.7, 11.23) * mm, "end": v(-8, 11.35) * mm});
            skLineSegment(sketch, "E3373.0.237", {"start": v(-8, 11.35) * mm, "end": v(-8.33, 11.43) * mm});
            skLineSegment(sketch, "E3373.0.238", {"start": v(-8.33, 11.43) * mm, "end": v(-8.67, 11.48) * mm});
            skLineSegment(sketch, "E3373.0.239", {"start": v(-8.67, 11.48) * mm, "end": v(-9.02, 11.5) * mm});
            skLineSegment(sketch, "E3373.0.240", {"start": v(-9.02, 11.5) * mm, "end": v(-9.36, 11.48) * mm});
            skLineSegment(sketch, "E3373.0.241", {"start": v(-9.36, 11.48) * mm, "end": v(-9.7, 11.43) * mm});
            skLineSegment(sketch, "E3373.0.242", {"start": v(-9.7, 11.43) * mm, "end": v(-10.03, 11.35) * mm});
            skLineSegment(sketch, "E3373.0.243", {"start": v(-10.03, 11.35) * mm, "end": v(-10.34, 11.23) * mm});
            skLineSegment(sketch, "E3373.0.244", {"start": v(-10.34, 11.23) * mm, "end": v(-10.64, 11.09) * mm});
            skLineSegment(sketch, "E3373.0.245", {"start": v(-10.64, 11.09) * mm, "end": v(-10.92, 10.92) * mm});
            skLineSegment(sketch, "E3373.0.246", {"start": v(-10.92, 10.92) * mm, "end": v(-11.18, 10.72) * mm});
            skLineSegment(sketch, "E3373.0.247", {"start": v(-11.18, 10.72) * mm, "end": v(-11.42, 10.5) * mm});
            skLineSegment(sketch, "E3373.0.248", {"start": v(-11.42, 10.5) * mm, "end": v(-11.64, 10.26) * mm});
            skLineSegment(sketch, "E3373.0.249", {"start": v(-11.64, 10.26) * mm, "end": v(-11.84, 10) * mm});
            skLineSegment(sketch, "E3373.0.250", {"start": v(-11.84, 10) * mm, "end": v(-12, 9.72) * mm});
            skLineSegment(sketch, "E3373.0.251", {"start": v(-12, 9.72) * mm, "end": v(-12.15, 9.42) * mm});
            skLineSegment(sketch, "E3373.0.252", {"start": v(-12.15, 9.42) * mm, "end": v(-12.26, 9.11) * mm});
            skLineSegment(sketch, "E3373.0.253", {"start": v(-12.26, 9.11) * mm, "end": v(-12.35, 8.79) * mm});
            skLineSegment(sketch, "E3373.0.254", {"start": v(-12.35, 8.79) * mm, "end": v(-12.4, 8.45) * mm});
            skLineSegment(sketch, "E3373.0.255", {"start": v(-12.4, 8.45) * mm, "end": v(-12.42, 8.1) * mm});
            skLineSegment(sketch, "E3373.0.256", {"start": v(-12.42, 8.1) * mm, "end": v(-12.4, 7.75) * mm});
            skLineSegment(sketch, "E3373.0.257", {"start": v(-12.4, 7.75) * mm, "end": v(-12.35, 7.42) * mm});
            skLineSegment(sketch, "E3373.0.258", {"start": v(-12.35, 7.42) * mm, "end": v(-12.26, 7.09) * mm});
            skLineSegment(sketch, "E3373.0.259", {"start": v(-12.26, 7.09) * mm, "end": v(-12.15, 6.78) * mm});
            skLineSegment(sketch, "E3373.0.260", {"start": v(-12.15, 6.78) * mm, "end": v(-12.1, 6.67) * mm});
            skLineSegment(sketch, "E3373.0.261", {"start": v(-12.1, 6.67) * mm, "end": v(-12.1, 6.67) * mm});
            skLineSegment(sketch, "E3373.0.262", {"start": v(-12.1, 6.67) * mm, "end": v(-12.1, 6.64) * mm});
            skLineSegment(sketch, "E3373.0.263", {"start": v(-12.1, 6.64) * mm, "end": v(-12.1, 6.61) * mm});
            skLineSegment(sketch, "E3373.0.264", {"start": v(-12.1, 6.61) * mm, "end": v(-12.1, 6.58) * mm});
            skLineSegment(sketch, "E3373.0.265", {"start": v(-12.1, 6.58) * mm, "end": v(-12.1, 6.56) * mm});
            skLineSegment(sketch, "E3373.0.266", {"start": v(-12.1, 6.56) * mm, "end": v(-12.1, 6.53) * mm});
            skLineSegment(sketch, "E3373.0.267", {"start": v(-12.1, 6.53) * mm, "end": v(-12.1, 6.51) * mm});
            skLineSegment(sketch, "E3373.0.268", {"start": v(-12.1, 6.51) * mm, "end": v(-12.11, 6.5) * mm});
            skLineSegment(sketch, "E3373.0.269", {"start": v(-12.11, 6.5) * mm, "end": v(-12.12, 6.47) * mm});
            skLineSegment(sketch, "E3373.0.270", {"start": v(-12.12, 6.47) * mm, "end": v(-12.13, 6.45) * mm});
            skLineSegment(sketch, "E3373.0.271", {"start": v(-12.13, 6.45) * mm, "end": v(-12.15, 6.43) * mm});
            skLineSegment(sketch, "E3373.0.272", {"start": v(-12.15, 6.43) * mm, "end": v(-12.44, 6) * mm});
            skLineSegment(sketch, "E3373.0.273", {"start": v(-12.44, 6) * mm, "end": v(-12.56, 5.83) * mm});
            skLineSegment(sketch, "E3373.0.274", {"start": v(-12.56, 5.83) * mm, "end": v(-12.58, 5.8) * mm});
            skLineSegment(sketch, "E3373.0.275", {"start": v(-12.58, 5.8) * mm, "end": v(-12.6, 5.77) * mm});
            skLineSegment(sketch, "E3373.0.276", {"start": v(-12.6, 5.77) * mm, "end": v(-12.63, 5.74) * mm});
            skLineSegment(sketch, "E3373.0.277", {"start": v(-12.63, 5.74) * mm, "end": v(-12.66, 5.71) * mm});
            skLineSegment(sketch, "E3373.0.278", {"start": v(-12.66, 5.71) * mm, "end": v(-12.69, 5.7) * mm});
            skLineSegment(sketch, "E3373.0.279", {"start": v(-12.69, 5.7) * mm, "end": v(-12.72, 5.67) * mm});
            skLineSegment(sketch, "E3373.0.280", {"start": v(-12.72, 5.67) * mm, "end": v(-12.76, 5.66) * mm});
            skLineSegment(sketch, "E3373.0.281", {"start": v(-12.76, 5.66) * mm, "end": v(-12.8, 5.65) * mm});
            skLineSegment(sketch, "E3373.0.282", {"start": v(-12.8, 5.65) * mm, "end": v(-12.84, 5.64) * mm});
            skLineSegment(sketch, "E3373.0.283", {"start": v(-12.84, 5.64) * mm, "end": v(-12.88, 5.64) * mm});
            skLineSegment(sketch, "E3373.0.284", {"start": v(-12.88, 5.64) * mm, "end": v(-12.93, 5.65) * mm});
            skLineSegment(sketch, "E3373.0.285", {"start": v(-12.93, 5.65) * mm, "end": v(-13, 5.65) * mm});
            skLineSegment(sketch, "E3373.0.286", {"start": v(-13, 5.65) * mm, "end": v(-13.03, 5.66) * mm});
            skLineSegment(sketch, "E3373.0.287", {"start": v(-13.03, 5.66) * mm, "end": v(-18.23, 7.34) * mm});
            skLineSegment(sketch, "E3373.0.288", {"start": v(-18.23, 7.34) * mm, "end": v(-18.28, 7.36) * mm});
            skLineSegment(sketch, "E3373.0.289", {"start": v(-18.28, 7.36) * mm, "end": v(-18.33, 7.37) * mm});
            skLineSegment(sketch, "E3373.0.290", {"start": v(-18.33, 7.37) * mm, "end": v(-18.38, 7.37) * mm});
            skLineSegment(sketch, "E3373.0.291", {"start": v(-18.38, 7.37) * mm, "end": v(-18.43, 7.37) * mm});
            skLineSegment(sketch, "E3373.0.292", {"start": v(-18.43, 7.37) * mm, "end": v(-18.48, 7.36) * mm});
            skLineSegment(sketch, "E3373.0.293", {"start": v(-18.48, 7.36) * mm, "end": v(-18.53, 7.35) * mm});
            skLineSegment(sketch, "E3373.0.294", {"start": v(-18.53, 7.35) * mm, "end": v(-18.58, 7.33) * mm});
            skLineSegment(sketch, "E3373.0.295", {"start": v(-18.58, 7.33) * mm, "end": v(-18.8, 7.21) * mm});
            skLineSegment(sketch, "E3373.0.296", {"start": v(-18.8, 7.21) * mm, "end": v(-19, 7.14) * mm});
            skLineSegment(sketch, "E3373.0.297", {"start": v(-19, 7.14) * mm, "end": v(-19.2, 7.1) * mm});
            skLineSegment(sketch, "E3373.0.298", {"start": v(-19.2, 7.1) * mm, "end": v(-19.4, 7.06) * mm});
            skLineSegment(sketch, "E3373.0.299", {"start": v(-19.4, 7.06) * mm, "end": v(-19.6, 7.05) * mm});
            skLineSegment(sketch, "E3373.0.300", {"start": v(-19.6, 7.05) * mm, "end": v(-19.81, 7.06) * mm});
            skLineSegment(sketch, "E3373.0.301", {"start": v(-19.81, 7.06) * mm, "end": v(-20.02, 7.1) * mm});
            skLineSegment(sketch, "E3373.0.302", {"start": v(-20.02, 7.1) * mm, "end": v(-20.22, 7.15) * mm});
            skLineSegment(sketch, "E3373.0.303", {"start": v(-20.22, 7.15) * mm, "end": v(-20.4, 7.22) * mm});
            skLineSegment(sketch, "E3373.0.304", {"start": v(-20.4, 7.22) * mm, "end": v(-20.6, 7.32) * mm});
            skLineSegment(sketch, "E3373.0.305", {"start": v(-20.6, 7.32) * mm, "end": v(-20.77, 7.43) * mm});
            skLineSegment(sketch, "E3373.0.306", {"start": v(-20.77, 7.43) * mm, "end": v(-20.92, 7.56) * mm});
            skLineSegment(sketch, "E3373.0.307", {"start": v(-20.92, 7.56) * mm, "end": v(-21.07, 7.7) * mm});
            skLineSegment(sketch, "E3373.0.308", {"start": v(-21.07, 7.7) * mm, "end": v(-21.2, 7.86) * mm});
            skLineSegment(sketch, "E3373.0.309", {"start": v(-21.2, 7.86) * mm, "end": v(-21.32, 8.03) * mm});
            skLineSegment(sketch, "E3373.0.310", {"start": v(-21.32, 8.03) * mm, "end": v(-21.44, 8.26) * mm});
            skLineSegment(sketch, "E3373.0.311", {"start": v(-21.44, 8.26) * mm, "end": v(-21.47, 8.3) * mm});
            skLineSegment(sketch, "E3373.0.312", {"start": v(-21.47, 8.3) * mm, "end": v(-21.5, 8.34) * mm});
            skLineSegment(sketch, "E3373.0.313", {"start": v(-21.5, 8.34) * mm, "end": v(-21.53, 8.38) * mm});
            skLineSegment(sketch, "E3373.0.314", {"start": v(-21.53, 8.38) * mm, "end": v(-21.57, 8.4) * mm});
            skLineSegment(sketch, "E3373.0.315", {"start": v(-21.57, 8.4) * mm, "end": v(-21.62, 8.44) * mm});
            skLineSegment(sketch, "E3373.0.316", {"start": v(-21.62, 8.44) * mm, "end": v(-21.66, 8.46) * mm});
            skLineSegment(sketch, "E3373.0.317", {"start": v(-21.66, 8.46) * mm, "end": v(-21.71, 8.48) * mm});
            skLineSegment(sketch, "E3373.0.318", {"start": v(-21.71, 8.48) * mm, "end": v(-22.92, 8.87) * mm});
            skLineSegment(sketch, "E3373.0.319", {"start": v(-22.92, 8.87) * mm, "end": v(-28, 9.62) * mm});
            skLineSegment(sketch, "E3373.0.320", {"start": v(-28, 9.62) * mm, "end": v(-28.18, 9.63) * mm});
            skLineSegment(sketch, "E3373.0.321", {"start": v(-28.18, 9.63) * mm, "end": v(-28.36, 9.6) * mm});
            skLineSegment(sketch, "E3373.0.322", {"start": v(-28.36, 9.6) * mm, "end": v(-28.52, 9.56) * mm});
            skLineSegment(sketch, "E3373.0.323", {"start": v(-28.52, 9.56) * mm, "end": v(-28.67, 9.48) * mm});
            skLineSegment(sketch, "E3373.0.324", {"start": v(-28.67, 9.48) * mm, "end": v(-28.81, 9.37) * mm});
            skLineSegment(sketch, "E3373.0.325", {"start": v(-28.81, 9.37) * mm, "end": v(-28.93, 9.25) * mm});
            skLineSegment(sketch, "E3373.0.326", {"start": v(-28.93, 9.25) * mm, "end": v(-29.03, 9.1) * mm});
            skLineSegment(sketch, "E3373.0.327", {"start": v(-29.03, 9.1) * mm, "end": v(-29.1, 8.94) * mm});
            skLineSegment(sketch, "E3373.0.328", {"start": v(-29.1, 8.94) * mm, "end": v(-30.18, 5.6) * mm});
            skLineSegment(sketch, "E3373.0.329", {"start": v(-30.18, 5.6) * mm, "end": v(-30.22, 5.42) * mm});
            skLineSegment(sketch, "E3373.0.330", {"start": v(-30.22, 5.42) * mm, "end": v(-30.23, 5.25) * mm});
            skLineSegment(sketch, "E3373.0.331", {"start": v(-30.23, 5.25) * mm, "end": v(-30.2, 5.08) * mm});
            skLineSegment(sketch, "E3373.0.332", {"start": v(-30.2, 5.08) * mm, "end": v(-30.16, 4.91) * mm});
            skLineSegment(sketch, "E3373.0.333", {"start": v(-30.16, 4.91) * mm, "end": v(-30.08, 4.76) * mm});
            skLineSegment(sketch, "E3373.0.334", {"start": v(-30.08, 4.76) * mm, "end": v(-29.98, 4.62) * mm});
            skLineSegment(sketch, "E3373.0.335", {"start": v(-29.98, 4.62) * mm, "end": v(-29.85, 4.5) * mm});
            skLineSegment(sketch, "E3373.0.336", {"start": v(-29.85, 4.5) * mm, "end": v(-29.7, 4.4) * mm});
            skLineSegment(sketch, "E3373.0.337", {"start": v(-29.7, 4.4) * mm, "end": v(-25.14, 2.02) * mm});
            skLineSegment(sketch, "E3373.0.338", {"start": v(-25.14, 2.02) * mm, "end": v(-23.94, 1.63) * mm});
            skLineSegment(sketch, "E3373.0.339", {"start": v(-23.94, 1.63) * mm, "end": v(-23.89, 1.62) * mm});
            skLineSegment(sketch, "E3373.0.340", {"start": v(-23.89, 1.62) * mm, "end": v(-23.84, 1.6) * mm});
            skLineSegment(sketch, "E3373.0.341", {"start": v(-23.84, 1.6) * mm, "end": v(-23.79, 1.6) * mm});
            skLineSegment(sketch, "E3373.0.342", {"start": v(-23.79, 1.6) * mm, "end": v(-23.73, 1.6) * mm});
            skLineSegment(sketch, "E3373.0.343", {"start": v(-23.73, 1.6) * mm, "end": v(-23.68, 1.61) * mm});
            skLineSegment(sketch, "E3373.0.344", {"start": v(-23.68, 1.61) * mm, "end": v(-23.63, 1.63) * mm});
            skLineSegment(sketch, "E3373.0.345", {"start": v(-23.63, 1.63) * mm, "end": v(-23.59, 1.65) * mm});
            skLineSegment(sketch, "E3373.0.346", {"start": v(-23.59, 1.65) * mm, "end": v(-23.35, 1.76) * mm});
            skLineSegment(sketch, "E3373.0.347", {"start": v(-23.35, 1.76) * mm, "end": v(-23.16, 1.83) * mm});
            skLineSegment(sketch, "E3373.0.348", {"start": v(-23.16, 1.83) * mm, "end": v(-22.96, 1.88) * mm});
            skLineSegment(sketch, "E3373.0.349", {"start": v(-22.96, 1.88) * mm, "end": v(-22.76, 1.91) * mm});
            skLineSegment(sketch, "E3373.0.350", {"start": v(-22.76, 1.91) * mm, "end": v(-22.55, 1.92) * mm});
            skLineSegment(sketch, "E3373.0.351", {"start": v(-22.55, 1.92) * mm, "end": v(-22.35, 1.91) * mm});
            skLineSegment(sketch, "E3373.0.352", {"start": v(-22.35, 1.91) * mm, "end": v(-22.15, 1.88) * mm});
            skLineSegment(sketch, "E3373.0.353", {"start": v(-22.15, 1.88) * mm, "end": v(-21.95, 1.82) * mm});
            skLineSegment(sketch, "E3373.0.354", {"start": v(-21.95, 1.82) * mm, "end": v(-21.75, 1.75) * mm});
            skLineSegment(sketch, "E3373.0.355", {"start": v(-21.75, 1.75) * mm, "end": v(-21.57, 1.66) * mm});
            skLineSegment(sketch, "E3373.0.356", {"start": v(-21.57, 1.66) * mm, "end": v(-21.4, 1.55) * mm});
            skLineSegment(sketch, "E3373.0.357", {"start": v(-21.4, 1.55) * mm, "end": v(-21.24, 1.42) * mm});
            skLineSegment(sketch, "E3373.0.358", {"start": v(-21.24, 1.42) * mm, "end": v(-21.1, 1.27) * mm});
            skLineSegment(sketch, "E3373.0.359", {"start": v(-21.1, 1.27) * mm, "end": v(-20.96, 1.12) * mm});
            skLineSegment(sketch, "E3373.0.360", {"start": v(-20.96, 1.12) * mm, "end": v(-20.85, 0.95) * mm});
            skLineSegment(sketch, "E3373.0.361", {"start": v(-20.85, 0.95) * mm, "end": v(-20.72, 0.72) * mm});
            skLineSegment(sketch, "E3373.0.362", {"start": v(-20.72, 0.72) * mm, "end": v(-20.7, 0.67) * mm});
            skLineSegment(sketch, "E3373.0.363", {"start": v(-20.7, 0.67) * mm, "end": v(-20.66, 0.63) * mm});
            skLineSegment(sketch, "E3373.0.364", {"start": v(-20.66, 0.63) * mm, "end": v(-20.63, 0.6) * mm});
            skLineSegment(sketch, "E3373.0.365", {"start": v(-20.63, 0.6) * mm, "end": v(-20.59, 0.57) * mm});
            skLineSegment(sketch, "E3373.0.366", {"start": v(-20.59, 0.57) * mm, "end": v(-20.54, 0.54) * mm});
            skLineSegment(sketch, "E3373.0.367", {"start": v(-20.54, 0.54) * mm, "end": v(-20.5, 0.52) * mm});
            skLineSegment(sketch, "E3373.0.368", {"start": v(-20.5, 0.52) * mm, "end": v(-20.45, 0.5) * mm});
            skLineSegment(sketch, "E3373.0.369", {"start": v(-20.45, 0.5) * mm, "end": v(-15.32, -1.17) * mm});
            skLineSegment(sketch, "E3373.0.370", {"start": v(-15.32, -1.17) * mm, "end": v(-15.3, -1.18) * mm});
            skLineSegment(sketch, "E3373.0.371", {"start": v(-15.3, -1.18) * mm, "end": v(-15.25, -1.2) * mm});
            skLineSegment(sketch, "E3373.0.372", {"start": v(-15.25, -1.2) * mm, "end": v(-15.21, -1.21) * mm});
            skLineSegment(sketch, "E3373.0.373", {"start": v(-15.21, -1.21) * mm, "end": v(-15.16, -1.23) * mm});
            skLineSegment(sketch, "E3373.0.374", {"start": v(-15.16, -1.23) * mm, "end": v(-15.12, -1.26) * mm});
            skLineSegment(sketch, "E3373.0.375", {"start": v(-15.12, -1.26) * mm, "end": v(-15.08, -1.29) * mm});
            skLineSegment(sketch, "E3373.0.376", {"start": v(-15.08, -1.29) * mm, "end": v(-15.05, -1.32) * mm});
            skLineSegment(sketch, "E3373.0.377", {"start": v(-15.05, -1.32) * mm, "end": v(-15.03, -1.35) * mm});
            skLineSegment(sketch, "E3373.0.378", {"start": v(-15.03, -1.35) * mm, "end": v(-15.01, -1.39) * mm});
            skLineSegment(sketch, "E3373.0.379", {"start": v(-15.01, -1.39) * mm, "end": v(-15, -1.43) * mm});
            skLineSegment(sketch, "E3373.0.380", {"start": v(-15, -1.43) * mm, "end": v(-14.99, -1.46) * mm});
            skLineSegment(sketch, "E3373.0.381", {"start": v(-14.99, -1.46) * mm, "end": v(-14.98, -1.5) * mm});
            skLineSegment(sketch, "E3373.0.382", {"start": v(-14.98, -1.5) * mm, "end": v(-14.98, -1.54) * mm});
            skLineSegment(sketch, "E3373.0.383", {"start": v(-14.98, -1.54) * mm, "end": v(-14.98, -1.58) * mm});
            skLineSegment(sketch, "E3373.0.384", {"start": v(-14.98, -1.58) * mm, "end": v(-15, -2.18) * mm});
            skLineSegment(sketch, "E3373.0.385", {"start": v(-15, -2.18) * mm, "end": v(-15, -2.36) * mm});
            skLineSegment(sketch, "E3373.0.386", {"start": v(-15, -2.36) * mm, "end": v(-14.94, -3.7) * mm});
            skLineSegment(sketch, "E3373.0.387", {"start": v(-14.94, -3.7) * mm, "end": v(-14.77, -5) * mm});
            skLineSegment(sketch, "E3373.0.388", {"start": v(-14.77, -5) * mm, "end": v(-14.49, -6.26) * mm});
            skLineSegment(sketch, "E3373.0.389", {"start": v(-14.49, -6.26) * mm, "end": v(-14.1, -7.48) * mm});
            skLineSegment(sketch, "E3373.0.390", {"start": v(-14.1, -7.48) * mm, "end": v(-13.62, -8.65) * mm});
            skLineSegment(sketch, "E3373.0.391", {"start": v(-13.62, -8.65) * mm, "end": v(-13.04, -9.77) * mm});
            skLineSegment(sketch, "E3373.0.392", {"start": v(-13.04, -9.77) * mm, "end": v(-12.38, -10.84) * mm});
            skLineSegment(sketch, "E3373.0.393", {"start": v(-12.38, -10.84) * mm, "end": v(-11.6, -11.86) * mm});
            skLineSegment(sketch, "E3373.0.394", {"start": v(-11.6, -11.86) * mm, "end": v(-11.6, -11.88) * mm});
            skLineSegment(sketch, "E3373.0.395", {"start": v(-11.6, -11.88) * mm, "end": v(-11.59, -11.9) * mm});
            skLineSegment(sketch, "E3373.0.396", {"start": v(-11.59, -11.9) * mm, "end": v(-11.58, -11.93) * mm});
            skLineSegment(sketch, "E3373.0.397", {"start": v(-11.58, -11.93) * mm, "end": v(-11.57, -11.95) * mm});
            skLineSegment(sketch, "E3373.0.398", {"start": v(-11.57, -11.95) * mm, "end": v(-11.57, -11.98) * mm});
            skLineSegment(sketch, "E3373.0.399", {"start": v(-11.57, -11.98) * mm, "end": v(-11.57, -12) * mm});
            skLineSegment(sketch, "E3373.0.400", {"start": v(-11.57, -12) * mm, "end": v(-11.57, -12.03) * mm});
            skLineSegment(sketch, "E3373.0.401", {"start": v(-11.57, -12.03) * mm, "end": v(-11.57, -12.06) * mm});
            skLineSegment(sketch, "E3373.0.402", {"start": v(-11.57, -12.06) * mm, "end": v(-11.58, -12.1) * mm});
            skLineSegment(sketch, "E3373.0.403", {"start": v(-11.58, -12.1) * mm, "end": v(-11.6, -12.14) * mm});
            skLineSegment(sketch, "E3373.0.404", {"start": v(-11.6, -12.14) * mm, "end": v(-11.6, -12.18) * mm});
            skLineSegment(sketch, "E3373.0.405", {"start": v(-11.6, -12.18) * mm, "end": v(-11.62, -12.22) * mm});
            skLineSegment(sketch, "E3373.0.406", {"start": v(-11.62, -12.22) * mm, "end": v(-11.65, -12.27) * mm});
            skLineSegment(sketch, "E3373.0.407", {"start": v(-11.65, -12.27) * mm, "end": v(-11.65, -12.28) * mm});
            skLineSegment(sketch, "E3373.0.408", {"start": v(-11.65, -12.28) * mm, "end": v(-14.87, -16.7) * mm});
            skLineSegment(sketch, "E3373.0.409", {"start": v(-14.87, -16.7) * mm, "end": v(-14.9, -16.75) * mm});
            skLineSegment(sketch, "E3373.0.410", {"start": v(-14.9, -16.75) * mm, "end": v(-14.92, -16.8) * mm});
            skLineSegment(sketch, "E3373.0.411", {"start": v(-14.92, -16.8) * mm, "end": v(-14.94, -16.84) * mm});
            skLineSegment(sketch, "E3373.0.412", {"start": v(-14.94, -16.84) * mm, "end": v(-14.95, -16.89) * mm});
            skLineSegment(sketch, "E3373.0.413", {"start": v(-14.95, -16.89) * mm, "end": v(-14.96, -16.94) * mm});
            skLineSegment(sketch, "E3373.0.414", {"start": v(-14.96, -16.94) * mm, "end": v(-14.96, -16.99) * mm});
            skLineSegment(sketch, "E3373.0.415", {"start": v(-14.96, -16.99) * mm, "end": v(-14.96, -17.04) * mm});
            skLineSegment(sketch, "E3373.0.416", {"start": v(-14.96, -17.04) * mm, "end": v(-14.92, -17.3) * mm});
            skLineSegment(sketch, "E3373.0.417", {"start": v(-14.92, -17.3) * mm, "end": v(-14.92, -17.5) * mm});
            skLineSegment(sketch, "E3373.0.418", {"start": v(-14.92, -17.5) * mm, "end": v(-14.93, -17.7) * mm});
            skLineSegment(sketch, "E3373.0.419", {"start": v(-14.93, -17.7) * mm, "end": v(-14.96, -17.9) * mm});
            skLineSegment(sketch, "E3373.0.420", {"start": v(-14.96, -17.9) * mm, "end": v(-15.02, -18.1) * mm});
            skLineSegment(sketch, "E3373.0.421", {"start": v(-15.02, -18.1) * mm, "end": v(-15.1, -18.3) * mm});
            skLineSegment(sketch, "E3373.0.422", {"start": v(-15.1, -18.3) * mm, "end": v(-15.18, -18.48) * mm});
            skLineSegment(sketch, "E3373.0.423", {"start": v(-15.18, -18.48) * mm, "end": v(-15.3, -18.65) * mm});
            skLineSegment(sketch, "E3373.0.424", {"start": v(-15.3, -18.65) * mm, "end": v(-15.43, -18.82) * mm});
            skLineSegment(sketch, "E3373.0.425", {"start": v(-15.43, -18.82) * mm, "end": v(-15.57, -18.96) * mm});
            skLineSegment(sketch, "E3373.0.426", {"start": v(-15.57, -18.96) * mm, "end": v(-15.73, -19.1) * mm});
            skLineSegment(sketch, "E3373.0.427", {"start": v(-15.73, -19.1) * mm, "end": v(-15.9, -19.2) * mm});
            skLineSegment(sketch, "E3373.0.428", {"start": v(-15.9, -19.2) * mm, "end": v(-16.08, -19.3) * mm});
            skLineSegment(sketch, "E3373.0.429", {"start": v(-16.08, -19.3) * mm, "end": v(-16.27, -19.37) * mm});
            skLineSegment(sketch, "E3373.0.430", {"start": v(-16.27, -19.37) * mm, "end": v(-16.47, -19.43) * mm});
            skLineSegment(sketch, "E3373.0.431", {"start": v(-16.47, -19.43) * mm, "end": v(-16.73, -19.47) * mm});
            skLineSegment(sketch, "E3373.0.432", {"start": v(-16.73, -19.47) * mm, "end": v(-16.78, -19.49) * mm});
            skLineSegment(sketch, "E3373.0.433", {"start": v(-16.78, -19.49) * mm, "end": v(-16.83, -19.5) * mm});
            skLineSegment(sketch, "E3373.0.434", {"start": v(-16.83, -19.5) * mm, "end": v(-16.87, -19.53) * mm});
            skLineSegment(sketch, "E3373.0.435", {"start": v(-16.87, -19.53) * mm, "end": v(-16.91, -19.56) * mm});
            skLineSegment(sketch, "E3373.0.436", {"start": v(-16.91, -19.56) * mm, "end": v(-16.95, -19.6) * mm});
            skLineSegment(sketch, "E3373.0.437", {"start": v(-16.95, -19.6) * mm, "end": v(-16.99, -19.63) * mm});
            skLineSegment(sketch, "E3373.0.438", {"start": v(-16.99, -19.63) * mm, "end": v(-17.02, -19.67) * mm});
            skLineSegment(sketch, "E3373.0.439", {"start": v(-17.02, -19.67) * mm, "end": v(-17.77, -20.7) * mm});
            skLineSegment(sketch, "E3373.0.440", {"start": v(-17.77, -20.7) * mm, "end": v(-20.05, -25.3) * mm});
            skLineSegment(sketch, "E3373.0.441", {"start": v(-20.05, -25.3) * mm, "end": v(-20.12, -25.46) * mm});
            skLineSegment(sketch, "E3373.0.442", {"start": v(-20.12, -25.46) * mm, "end": v(-20.15, -25.64) * mm});
            skLineSegment(sketch, "E3373.0.443", {"start": v(-20.15, -25.64) * mm, "end": v(-20.15, -25.8) * mm});
            skLineSegment(sketch, "E3373.0.444", {"start": v(-20.15, -25.8) * mm, "end": v(-20.13, -25.98) * mm});
            skLineSegment(sketch, "E3373.0.445", {"start": v(-20.13, -25.98) * mm, "end": v(-20.07, -26.14) * mm});
            skLineSegment(sketch, "E3373.0.446", {"start": v(-20.07, -26.14) * mm, "end": v(-19.99, -26.3) * mm});
            skLineSegment(sketch, "E3373.0.447", {"start": v(-19.99, -26.3) * mm, "end": v(-19.88, -26.43) * mm});
            skLineSegment(sketch, "E3373.0.448", {"start": v(-19.88, -26.43) * mm, "end": v(-19.74, -26.55) * mm});
            skLineSegment(sketch, "E3373.0.449", {"start": v(-19.74, -26.55) * mm, "end": v(-16.9, -28.61) * mm});
            skLineSegment(sketch, "E3373.0.450", {"start": v(-16.9, -28.61) * mm, "end": v(-16.75, -28.7) * mm});
            skLineSegment(sketch, "E3373.0.451", {"start": v(-16.75, -28.7) * mm, "end": v(-16.58, -28.77) * mm});
            skLineSegment(sketch, "E3373.0.452", {"start": v(-16.58, -28.77) * mm, "end": v(-16.41, -28.8) * mm});
            skLineSegment(sketch, "E3373.0.453", {"start": v(-16.41, -28.8) * mm, "end": v(-16.24, -28.8) * mm});
            skLineSegment(sketch, "E3373.0.454", {"start": v(-16.24, -28.8) * mm, "end": v(-16.07, -28.78) * mm});
            skLineSegment(sketch, "E3373.0.455", {"start": v(-16.07, -28.78) * mm, "end": v(-15.9, -28.72) * mm});
            skLineSegment(sketch, "E3373.0.456", {"start": v(-15.9, -28.72) * mm, "end": v(-15.75, -28.63) * mm});
            skLineSegment(sketch, "E3373.0.457", {"start": v(-15.75, -28.63) * mm, "end": v(-15.61, -28.52) * mm});
            skLineSegment(sketch, "E3373.0.458", {"start": v(-15.61, -28.52) * mm, "end": v(-11.94, -24.92) * mm});
            skLineSegment(sketch, "E3373.0.459", {"start": v(-11.94, -24.92) * mm, "end": v(-11.2, -23.9) * mm});
            skLineSegment(sketch, "E3373.0.460", {"start": v(-11.2, -23.9) * mm, "end": v(-11.17, -23.86) * mm});
            skLineSegment(sketch, "E3373.0.461", {"start": v(-11.17, -23.86) * mm, "end": v(-11.15, -23.81) * mm});
            skLineSegment(sketch, "E3373.0.462", {"start": v(-11.15, -23.81) * mm, "end": v(-11.13, -23.76) * mm});
            skLineSegment(sketch, "E3373.0.463", {"start": v(-11.13, -23.76) * mm, "end": v(-11.11, -23.71) * mm});
            skLineSegment(sketch, "E3373.0.464", {"start": v(-11.11, -23.71) * mm, "end": v(-11.1, -23.66) * mm});
            skLineSegment(sketch, "E3373.0.465", {"start": v(-11.1, -23.66) * mm, "end": v(-11.1, -23.61) * mm});
            skLineSegment(sketch, "E3373.0.466", {"start": v(-11.1, -23.61) * mm, "end": v(-11.1, -23.56) * mm});
            skLineSegment(sketch, "E3373.0.467", {"start": v(-11.1, -23.56) * mm, "end": v(-11.14, -23.3) * mm});
            skLineSegment(sketch, "E3373.0.468", {"start": v(-11.14, -23.3) * mm, "end": v(-11.15, -23.1) * mm});
            skLineSegment(sketch, "E3373.0.469", {"start": v(-11.15, -23.1) * mm, "end": v(-11.14, -22.9) * mm});
            skLineSegment(sketch, "E3373.0.470", {"start": v(-11.14, -22.9) * mm, "end": v(-11.1, -22.7) * mm});
            skLineSegment(sketch, "E3373.0.471", {"start": v(-11.1, -22.7) * mm, "end": v(-11.05, -22.5) * mm});
            skLineSegment(sketch, "E3373.0.472", {"start": v(-11.05, -22.5) * mm, "end": v(-10.97, -22.3) * mm});
            skLineSegment(sketch, "E3373.0.473", {"start": v(-10.97, -22.3) * mm, "end": v(-10.88, -22.12) * mm});
            skLineSegment(sketch, "E3373.0.474", {"start": v(-10.88, -22.12) * mm, "end": v(-10.77, -21.95) * mm});
            skLineSegment(sketch, "E3373.0.475", {"start": v(-10.77, -21.95) * mm, "end": v(-10.64, -21.78) * mm});
            skLineSegment(sketch, "E3373.0.476", {"start": v(-10.64, -21.78) * mm, "end": v(-10.5, -21.64) * mm});
            skLineSegment(sketch, "E3373.0.477", {"start": v(-10.5, -21.64) * mm, "end": v(-10.33, -21.51) * mm});
            skLineSegment(sketch, "E3373.0.478", {"start": v(-10.33, -21.51) * mm, "end": v(-10.16, -21.4) * mm});
            skLineSegment(sketch, "E3373.0.479", {"start": v(-10.16, -21.4) * mm, "end": v(-9.98, -21.3) * mm});
            skLineSegment(sketch, "E3373.0.480", {"start": v(-9.98, -21.3) * mm, "end": v(-9.79, -21.23) * mm});
            skLineSegment(sketch, "E3373.0.481", {"start": v(-9.79, -21.23) * mm, "end": v(-9.6, -21.17) * mm});
            skLineSegment(sketch, "E3373.0.482", {"start": v(-9.6, -21.17) * mm, "end": v(-9.34, -21.13) * mm});
            skLineSegment(sketch, "E3373.0.483", {"start": v(-9.34, -21.13) * mm, "end": v(-9.29, -21.11) * mm});
            skLineSegment(sketch, "E3373.0.484", {"start": v(-9.29, -21.11) * mm, "end": v(-9.24, -21.1) * mm});
            skLineSegment(sketch, "E3373.0.485", {"start": v(-9.24, -21.1) * mm, "end": v(-9.2, -21.07) * mm});
            skLineSegment(sketch, "E3373.0.486", {"start": v(-9.2, -21.07) * mm, "end": v(-9.15, -21.04) * mm});
            skLineSegment(sketch, "E3373.0.487", {"start": v(-9.15, -21.04) * mm, "end": v(-9.11, -21.01) * mm});
            skLineSegment(sketch, "E3373.0.488", {"start": v(-9.11, -21.01) * mm, "end": v(-9.07, -20.97) * mm});
            skLineSegment(sketch, "E3373.0.489", {"start": v(-9.07, -20.97) * mm, "end": v(-9.04, -20.93) * mm});
            skLineSegment(sketch, "E3373.0.490", {"start": v(-9.04, -20.93) * mm, "end": v(-6.75, -17.8) * mm});
            skLineSegment(sketch, "E3373.0.491", {"start": v(-6.75, -17.8) * mm, "end": v(-6.7, -17.7) * mm});
            skLineSegment(sketch, "E3373.0.492", {"start": v(-6.7, -17.7) * mm, "end": v(-6.67, -17.6) * mm});
            skLineSegment(sketch, "E3373.0.493", {"start": v(-6.67, -17.6) * mm, "end": v(-6.66, -17.52) * mm});
            skLineSegment(sketch, "E3373.0.494", {"start": v(-6.66, -17.52) * mm, "end": v(-6.66, -17.02) * mm});
            skLineSegment(sketch, "E3373.0.495", {"start": v(-6.66, -17.02) * mm, "end": v(-6.65, -16.9) * mm});
            skLineSegment(sketch, "E3373.0.496", {"start": v(-6.65, -16.9) * mm, "end": v(-6.62, -16.8) * mm});
            skLineSegment(sketch, "E3373.0.497", {"start": v(-6.62, -16.8) * mm, "end": v(-6.58, -16.72) * mm});
            skLineSegment(sketch, "E3373.0.498", {"start": v(-6.58, -16.72) * mm, "end": v(-6.52, -16.65) * mm});
            skLineSegment(sketch, "E3373.0.499", {"start": v(-6.52, -16.65) * mm, "end": v(-6.44, -16.59) * mm});
            skLineSegment(sketch, "E3373.0.500", {"start": v(-6.44, -16.59) * mm, "end": v(-6.36, -16.54) * mm});
            skLineSegment(sketch, "E3373.0.501", {"start": v(-6.36, -16.54) * mm, "end": v(-6.26, -16.51) * mm});
            skLineSegment(sketch, "E3373.0.502", {"start": v(-6.26, -16.51) * mm, "end": v(-6.18, -16.5) * mm});
            skLineSegment(sketch, "E3373.0.503", {"start": v(-6.18, -16.5) * mm, "end": v(-4.7, -16.5) * mm});
            skLineSegment(sketch, "E3373.0.504", {"start": v(-4.7, -16.5) * mm, "end": v(-4.7, -16.5) * mm});
            skLineSegment(sketch, "E3373.0.505", {"start": v(-4.7, -16.5) * mm, "end": v(-4.6, -16.51) * mm});
            skLineSegment(sketch, "E3373.0.506", {"start": v(-4.6, -16.51) * mm, "end": v(-4.51, -16.54) * mm});
            skLineSegment(sketch, "E3373.0.507", {"start": v(-4.51, -16.54) * mm, "end": v(-4.43, -16.59) * mm});
            skLineSegment(sketch, "E3373.0.508", {"start": v(-4.43, -16.59) * mm, "end": v(-4.35, -16.65) * mm});
            skLineSegment(sketch, "E3373.0.509", {"start": v(-4.35, -16.65) * mm, "end": v(-4.3, -16.72) * mm});
            skLineSegment(sketch, "E3373.0.510", {"start": v(-4.3, -16.72) * mm, "end": v(-4.24, -16.8) * mm});
            skLineSegment(sketch, "E3373.0.511", {"start": v(-4.24, -16.8) * mm, "end": v(-4.21, -16.9) * mm});
            skLineSegment(sketch, "E3373.0.512", {"start": v(-4.21, -16.9) * mm, "end": v(-4.2, -17.05) * mm});
            skLineSegment(sketch, "E3373.0.513", {"start": v(-4.2, -17.05) * mm, "end": v(-4.2, -17.37) * mm});
            skLineSegment(sketch, "E3373.0.514", {"start": v(-4.2, -17.37) * mm, "end": v(-4.2, -17.5) * mm});
            skLineSegment(sketch, "E3373.0.515", {"start": v(-4.2, -17.5) * mm, "end": v(-4.17, -17.59) * mm});
            skLineSegment(sketch, "E3373.0.516", {"start": v(-4.17, -17.59) * mm, "end": v(-4.12, -17.67) * mm});
            skLineSegment(sketch, "E3373.0.517", {"start": v(-4.12, -17.67) * mm, "end": v(-4.06, -17.75) * mm});
            skLineSegment(sketch, "E3373.0.518", {"start": v(-4.06, -17.75) * mm, "end": v(-3.99, -17.8) * mm});
            skLineSegment(sketch, "E3373.0.519", {"start": v(-3.99, -17.8) * mm, "end": v(-3.9, -17.85) * mm});
            skLineSegment(sketch, "E3373.0.520", {"start": v(-3.9, -17.85) * mm, "end": v(-3.8, -17.88) * mm});
            skLineSegment(sketch, "E3373.0.521", {"start": v(-3.8, -17.88) * mm, "end": v(-3.7, -17.9) * mm});
            skLineSegment(sketch, "E3373.0.522", {"start": v(-3.7, -17.9) * mm, "end": v(3.71, -17.9) * mm});
            skLineSegment(sketch, "E3373.0.523", {"start": v(3.71, -17.9) * mm, "end": v(3.81, -17.89) * mm});
            skLineSegment(sketch, "E3373.0.524", {"start": v(3.81, -17.89) * mm, "end": v(3.9, -17.86) * mm});
            skLineSegment(sketch, "E3373.0.525", {"start": v(3.9, -17.86) * mm, "end": v(4, -17.81) * mm});
            skLineSegment(sketch, "E3373.0.526", {"start": v(4, -17.81) * mm, "end": v(4.06, -17.75) * mm});
            skLineSegment(sketch, "E3373.0.527", {"start": v(4.06, -17.75) * mm, "end": v(4.13, -17.68) * mm});
            skLineSegment(sketch, "E3373.0.528", {"start": v(4.13, -17.68) * mm, "end": v(4.17, -17.6) * mm});
            skLineSegment(sketch, "E3373.0.529", {"start": v(4.17, -17.6) * mm, "end": v(4.2, -17.5) * mm});
            skLineSegment(sketch, "E3373.0.530", {"start": v(4.2, -17.5) * mm, "end": v(4.21, -17.37) * mm});
            skLineSegment(sketch, "E3373.0.531", {"start": v(4.21, -17.37) * mm, "end": v(4.21, -17) * mm});
            skLineSegment(sketch, "E3373.0.532", {"start": v(4.21, -17) * mm, "end": v(4.22, -16.9) * mm});
            skLineSegment(sketch, "E3373.0.533", {"start": v(4.22, -16.9) * mm, "end": v(4.25, -16.8) * mm});
            skLineSegment(sketch, "E3373.0.534", {"start": v(4.25, -16.8) * mm, "end": v(4.3, -16.72) * mm});
            skLineSegment(sketch, "E3373.0.535", {"start": v(4.3, -16.72) * mm, "end": v(4.36, -16.64) * mm});
            skLineSegment(sketch, "E3373.0.536", {"start": v(4.36, -16.64) * mm, "end": v(4.43, -16.58) * mm});
            skLineSegment(sketch, "E3373.0.537", {"start": v(4.43, -16.58) * mm, "end": v(4.52, -16.54) * mm});
            skLineSegment(sketch, "E3373.0.538", {"start": v(4.52, -16.54) * mm, "end": v(4.6, -16.5) * mm});
            skLineSegment(sketch, "E3373.0.539", {"start": v(4.6, -16.5) * mm, "end": v(4.71, -16.5) * mm});
            skLineSegment(sketch, "E3373.0.540", {"start": v(4.71, -16.5) * mm, "end": v(4.71, -16.5) * mm});
            skLineSegment(sketch, "E3373.0.541", {"start": v(4.71, -16.5) * mm, "end": v(4.71, -16.5) * mm});
            skLineSegment(sketch, "E3373.0.542", {"start": v(4.71, -16.5) * mm, "end": v(6.16, -16.5) * mm});
            skLineSegment(sketch, "E3373.0.543", {"start": v(6.16, -16.5) * mm, "end": v(6.16, -16.5) * mm});
            skLineSegment(sketch, "E3373.0.544", {"start": v(6.16, -16.5) * mm, "end": v(6.26, -16.5) * mm});
            skLineSegment(sketch, "E3373.0.545", {"start": v(6.26, -16.5) * mm, "end": v(6.35, -16.54) * mm});
            skLineSegment(sketch, "E3373.0.546", {"start": v(6.35, -16.54) * mm, "end": v(6.44, -16.58) * mm});
            skLineSegment(sketch, "E3373.0.547", {"start": v(6.44, -16.58) * mm, "end": v(6.51, -16.64) * mm});
            skLineSegment(sketch, "E3373.0.548", {"start": v(6.51, -16.64) * mm, "end": v(6.57, -16.72) * mm});
            skLineSegment(sketch, "E3373.0.549", {"start": v(6.57, -16.72) * mm, "end": v(6.62, -16.8) * mm});
            skLineSegment(sketch, "E3373.0.550", {"start": v(6.62, -16.8) * mm, "end": v(6.65, -16.9) * mm});
            skLineSegment(sketch, "E3373.0.551", {"start": v(6.65, -16.9) * mm, "end": v(6.66, -17) * mm});
            skLineSegment(sketch, "E3373.0.552", {"start": v(6.66, -17) * mm, "end": v(6.66, -17) * mm});
            skLineSegment(sketch, "E3373.0.553", {"start": v(6.66, -17) * mm, "end": v(6.66, -17.52) * mm});
            skLineSegment(sketch, "E3373.0.554", {"start": v(6.66, -17.52) * mm, "end": v(6.67, -17.6) * mm});
            skLineSegment(sketch, "E3373.0.555", {"start": v(6.67, -17.6) * mm, "end": v(6.7, -17.7) * mm});
            skLineSegment(sketch, "E3373.0.556", {"start": v(6.7, -17.7) * mm, "end": v(6.75, -17.79) * mm});
            skLineSegment(sketch, "E3373.0.557", {"start": v(6.75, -17.79) * mm, "end": v(6.76, -17.8) * mm});
            skLineSegment(sketch, "E3373.0.558", {"start": v(6.76, -17.8) * mm, "end": v(9.04, -20.93) * mm});
            skLineSegment(sketch, "E3373.0.559", {"start": v(9.04, -20.93) * mm, "end": v(9.07, -20.97) * mm});
            skLineSegment(sketch, "E3373.0.560", {"start": v(9.07, -20.97) * mm, "end": v(9.1, -21) * mm});
            skLineSegment(sketch, "E3373.0.561", {"start": v(9.1, -21) * mm, "end": v(9.15, -21.04) * mm});
            skLineSegment(sketch, "E3373.0.562", {"start": v(9.15, -21.04) * mm, "end": v(9.2, -21.07) * mm});
            skLineSegment(sketch, "E3373.0.563", {"start": v(9.2, -21.07) * mm, "end": v(9.24, -21.1) * mm});
            skLineSegment(sketch, "E3373.0.564", {"start": v(9.24, -21.1) * mm, "end": v(9.29, -21.1) * mm});
            skLineSegment(sketch, "E3373.0.565", {"start": v(9.29, -21.1) * mm, "end": v(9.33, -21.12) * mm});
            skLineSegment(sketch, "E3373.0.566", {"start": v(9.33, -21.12) * mm, "end": v(9.59, -21.17) * mm});
            skLineSegment(sketch, "E3373.0.567", {"start": v(9.59, -21.17) * mm, "end": v(9.79, -21.22) * mm});
            skLineSegment(sketch, "E3373.0.568", {"start": v(9.79, -21.22) * mm, "end": v(9.98, -21.3) * mm});
            skLineSegment(sketch, "E3373.0.569", {"start": v(9.98, -21.3) * mm, "end": v(10.16, -21.4) * mm});
            skLineSegment(sketch, "E3373.0.570", {"start": v(10.16, -21.4) * mm, "end": v(10.33, -21.5) * mm});
            skLineSegment(sketch, "E3373.0.571", {"start": v(10.33, -21.5) * mm, "end": v(10.49, -21.64) * mm});
            skLineSegment(sketch, "E3373.0.572", {"start": v(10.49, -21.64) * mm, "end": v(10.63, -21.78) * mm});
            skLineSegment(sketch, "E3373.0.573", {"start": v(10.63, -21.78) * mm, "end": v(10.77, -21.94) * mm});
            skLineSegment(sketch, "E3373.0.574", {"start": v(10.77, -21.94) * mm, "end": v(10.88, -22.12) * mm});
            skLineSegment(sketch, "E3373.0.575", {"start": v(10.88, -22.12) * mm, "end": v(10.97, -22.3) * mm});
            skLineSegment(sketch, "E3373.0.576", {"start": v(10.97, -22.3) * mm, "end": v(11.05, -22.5) * mm});
            skLineSegment(sketch, "E3373.0.577", {"start": v(11.05, -22.5) * mm, "end": v(11.1, -22.69) * mm});
            skLineSegment(sketch, "E3373.0.578", {"start": v(11.1, -22.69) * mm, "end": v(11.13, -22.89) * mm});
            skLineSegment(sketch, "E3373.0.579", {"start": v(11.13, -22.89) * mm, "end": v(11.15, -23.1) * mm});
            skLineSegment(sketch, "E3373.0.580", {"start": v(11.15, -23.1) * mm, "end": v(11.14, -23.3) * mm});
            skLineSegment(sketch, "E3373.0.581", {"start": v(11.14, -23.3) * mm, "end": v(11.1, -23.56) * mm});
            skLineSegment(sketch, "E3373.0.582", {"start": v(11.1, -23.56) * mm, "end": v(11.1, -23.6) * mm});
            skLineSegment(sketch, "E3373.0.583", {"start": v(11.1, -23.6) * mm, "end": v(11.1, -23.66) * mm});
            skLineSegment(sketch, "E3373.0.584", {"start": v(11.1, -23.66) * mm, "end": v(11.11, -23.7) * mm});
            skLineSegment(sketch, "E3373.0.585", {"start": v(11.11, -23.7) * mm, "end": v(11.13, -23.76) * mm});
            skLineSegment(sketch, "E3373.0.586", {"start": v(11.13, -23.76) * mm, "end": v(11.14, -23.8) * mm});
            skLineSegment(sketch, "E3373.0.587", {"start": v(11.14, -23.8) * mm, "end": v(11.17, -23.85) * mm});
            skLineSegment(sketch, "E3373.0.588", {"start": v(11.17, -23.85) * mm, "end": v(11.2, -23.9) * mm});
            skLineSegment(sketch, "E3373.0.589", {"start": v(11.2, -23.9) * mm, "end": v(11.94, -24.92) * mm});
            skLineSegment(sketch, "E3373.0.590", {"start": v(11.94, -24.92) * mm, "end": v(15.61, -28.51) * mm});
            skLineSegment(sketch, "E3373.0.591", {"start": v(15.61, -28.51) * mm, "end": v(15.75, -28.63) * mm});
            skLineSegment(sketch, "E3373.0.592", {"start": v(15.75, -28.63) * mm, "end": v(15.9, -28.71) * mm});
            skLineSegment(sketch, "E3373.0.593", {"start": v(15.9, -28.71) * mm, "end": v(16.07, -28.77) * mm});
            skLineSegment(sketch, "E3373.0.594", {"start": v(16.07, -28.77) * mm, "end": v(16.24, -28.8) * mm});
            skLineSegment(sketch, "E3373.0.595", {"start": v(16.24, -28.8) * mm, "end": v(16.41, -28.8) * mm});
            skLineSegment(sketch, "E3373.0.596", {"start": v(16.41, -28.8) * mm, "end": v(16.58, -28.76) * mm});
            skLineSegment(sketch, "E3373.0.597", {"start": v(16.58, -28.76) * mm, "end": v(16.75, -28.7) * mm});
            skLineSegment(sketch, "E3373.0.598", {"start": v(16.75, -28.7) * mm, "end": v(16.9, -28.6) * mm});
            skLineSegment(sketch, "E3373.0.599", {"start": v(16.9, -28.6) * mm, "end": v(19.74, -26.55) * mm});
            skLineSegment(sketch, "E3373.0.600", {"start": v(19.74, -26.55) * mm, "end": v(19.88, -26.43) * mm});
            skLineSegment(sketch, "E3373.0.601", {"start": v(19.88, -26.43) * mm, "end": v(19.99, -26.3) * mm});
            skLineSegment(sketch, "E3373.0.602", {"start": v(19.99, -26.3) * mm, "end": v(20.07, -26.14) * mm});
            skLineSegment(sketch, "E3373.0.603", {"start": v(20.07, -26.14) * mm, "end": v(20.12, -25.97) * mm});
            skLineSegment(sketch, "E3373.0.604", {"start": v(20.12, -25.97) * mm, "end": v(20.15, -25.8) * mm});
            skLineSegment(sketch, "E3373.0.605", {"start": v(20.15, -25.8) * mm, "end": v(20.15, -25.63) * mm});
            skLineSegment(sketch, "E3373.0.606", {"start": v(20.15, -25.63) * mm, "end": v(20.11, -25.46) * mm});
            skLineSegment(sketch, "E3373.0.607", {"start": v(20.11, -25.46) * mm, "end": v(20.05, -25.3) * mm});
            skLineSegment(sketch, "E3373.0.608", {"start": v(20.05, -25.3) * mm, "end": v(17.76, -20.69) * mm});
            skLineSegment(sketch, "E3373.0.609", {"start": v(17.76, -20.69) * mm, "end": v(17.02, -19.66) * mm});
            skLineSegment(sketch, "E3373.0.610", {"start": v(17.02, -19.66) * mm, "end": v(16.99, -19.62) * mm});
            skLineSegment(sketch, "E3373.0.611", {"start": v(16.99, -19.62) * mm, "end": v(16.95, -19.59) * mm});
            skLineSegment(sketch, "E3373.0.612", {"start": v(16.95, -19.59) * mm, "end": v(16.91, -19.55) * mm});
            skLineSegment(sketch, "E3373.0.613", {"start": v(16.91, -19.55) * mm, "end": v(16.87, -19.53) * mm});
            skLineSegment(sketch, "E3373.0.614", {"start": v(16.87, -19.53) * mm, "end": v(16.82, -19.5) * mm});
            skLineSegment(sketch, "E3373.0.615", {"start": v(16.82, -19.5) * mm, "end": v(16.78, -19.48) * mm});
            skLineSegment(sketch, "E3373.0.616", {"start": v(16.78, -19.48) * mm, "end": v(16.73, -19.47) * mm});
            skLineSegment(sketch, "E3373.0.617", {"start": v(16.73, -19.47) * mm, "end": v(16.47, -19.42) * mm});
            skLineSegment(sketch, "E3373.0.618", {"start": v(16.47, -19.42) * mm, "end": v(16.27, -19.37) * mm});
            skLineSegment(sketch, "E3373.0.619", {"start": v(16.27, -19.37) * mm, "end": v(16.08, -19.3) * mm});
            skLineSegment(sketch, "E3373.0.620", {"start": v(16.08, -19.3) * mm, "end": v(15.9, -19.2) * mm});
            skLineSegment(sketch, "E3373.0.621", {"start": v(15.9, -19.2) * mm, "end": v(15.73, -19.09) * mm});
            skLineSegment(sketch, "E3373.0.622", {"start": v(15.73, -19.09) * mm, "end": v(15.57, -18.96) * mm});
            skLineSegment(sketch, "E3373.0.623", {"start": v(15.57, -18.96) * mm, "end": v(15.43, -18.81) * mm});
            skLineSegment(sketch, "E3373.0.624", {"start": v(15.43, -18.81) * mm, "end": v(15.3, -18.65) * mm});
            skLineSegment(sketch, "E3373.0.625", {"start": v(15.3, -18.65) * mm, "end": v(15.18, -18.48) * mm});
            skLineSegment(sketch, "E3373.0.626", {"start": v(15.18, -18.48) * mm, "end": v(15.09, -18.3) * mm});
            skLineSegment(sketch, "E3373.0.627", {"start": v(15.09, -18.3) * mm, "end": v(15.01, -18.1) * mm});
            skLineSegment(sketch, "E3373.0.628", {"start": v(15.01, -18.1) * mm, "end": v(14.96, -17.9) * mm});
            skLineSegment(sketch, "E3373.0.629", {"start": v(14.96, -17.9) * mm, "end": v(14.93, -17.7) * mm});
            skLineSegment(sketch, "E3373.0.630", {"start": v(14.93, -17.7) * mm, "end": v(14.91, -17.5) * mm});
            skLineSegment(sketch, "E3373.0.631", {"start": v(14.91, -17.5) * mm, "end": v(14.92, -17.3) * mm});
            skLineSegment(sketch, "E3373.0.632", {"start": v(14.92, -17.3) * mm, "end": v(14.96, -17.04) * mm});
            skLineSegment(sketch, "E3373.0.633", {"start": v(14.96, -17.04) * mm, "end": v(14.96, -16.98) * mm});
            skLineSegment(sketch, "E3373.0.634", {"start": v(14.96, -16.98) * mm, "end": v(14.96, -16.93) * mm});
            skLineSegment(sketch, "E3373.0.635", {"start": v(14.96, -16.93) * mm, "end": v(14.95, -16.88) * mm});
            skLineSegment(sketch, "E3373.0.636", {"start": v(14.95, -16.88) * mm, "end": v(14.94, -16.83) * mm});
            skLineSegment(sketch, "E3373.0.637", {"start": v(14.94, -16.83) * mm, "end": v(14.92, -16.79) * mm});
            skLineSegment(sketch, "E3373.0.638", {"start": v(14.92, -16.79) * mm, "end": v(14.9, -16.74) * mm});
            skLineSegment(sketch, "E3373.0.639", {"start": v(14.9, -16.74) * mm, "end": v(14.87, -16.7) * mm});
            skLineSegment(sketch, "E3373.0.640", {"start": v(14.87, -16.7) * mm, "end": v(11.63, -12.24) * mm});
            skLineSegment(sketch, "E3373.0.641", {"start": v(11.63, -12.24) * mm, "end": v(11.6, -12.2) * mm});
            skLineSegment(sketch, "E3373.0.642", {"start": v(11.6, -12.2) * mm, "end": v(11.6, -12.16) * mm});
            skLineSegment(sketch, "E3373.0.643", {"start": v(11.6, -12.16) * mm, "end": v(11.58, -12.13) * mm});
            skLineSegment(sketch, "E3373.0.644", {"start": v(11.58, -12.13) * mm, "end": v(11.57, -12.1) * mm});
            skLineSegment(sketch, "E3373.0.645", {"start": v(11.57, -12.1) * mm, "end": v(11.57, -12.06) * mm});
            skLineSegment(sketch, "E3373.0.646", {"start": v(11.57, -12.06) * mm, "end": v(11.57, -12.04) * mm});
            skLineSegment(sketch, "E3373.0.647", {"start": v(11.57, -12.04) * mm, "end": v(11.57, -12) * mm});
            skLineSegment(sketch, "E3373.0.648", {"start": v(11.57, -12) * mm, "end": v(11.57, -11.96) * mm});
            skLineSegment(sketch, "E3373.0.649", {"start": v(11.57, -11.96) * mm, "end": v(11.58, -11.93) * mm});
            skLineSegment(sketch, "E3373.0.650", {"start": v(11.58, -11.93) * mm, "end": v(11.6, -11.9) * mm});
            skLineSegment(sketch, "E3373.0.651", {"start": v(11.6, -11.9) * mm, "end": v(11.6, -11.87) * mm});
            skLineSegment(sketch, "E3373.0.652", {"start": v(11.6, -11.87) * mm, "end": v(11.63, -11.84) * mm});
            skLineSegment(sketch, "E3373.0.653", {"start": v(11.63, -11.84) * mm, "end": v(11.65, -11.81) * mm});
            skLineSegment(sketch, "E3373.0.654", {"start": v(11.65, -11.81) * mm, "end": v(11.67, -11.78) * mm});
            skLineSegment(sketch, "E3373.0.655", {"start": v(11.67, -11.78) * mm, "end": v(12.41, -10.79) * mm});
            skLineSegment(sketch, "E3373.0.656", {"start": v(12.41, -10.79) * mm, "end": v(13.07, -9.73) * mm});
            skLineSegment(sketch, "E3373.0.657", {"start": v(13.07, -9.73) * mm, "end": v(13.64, -8.61) * mm});
            skLineSegment(sketch, "E3373.0.658", {"start": v(13.64, -8.61) * mm, "end": v(14.12, -7.45) * mm});
            skLineSegment(sketch, "E3373.0.659", {"start": v(14.12, -7.45) * mm, "end": v(14.5, -6.23) * mm});
            skLineSegment(sketch, "E3373.0.660", {"start": v(14.5, -6.23) * mm, "end": v(14.77, -4.98) * mm});
            skLineSegment(sketch, "E3373.0.661", {"start": v(14.77, -4.98) * mm, "end": v(14.94, -3.69) * mm});
            skLineSegment(sketch, "E3373.0.662", {"start": v(14.94, -3.69) * mm, "end": v(15, -2.36) * mm});
            skLineSegment(sketch, "E3373.0.663", {"start": v(15, -2.36) * mm, "end": v(15, -2) * mm});
            skLineSegment(sketch, "E3373.0.664", {"start": v(15, -2) * mm, "end": v(14.98, -1.58) * mm});
            skLineSegment(sketch, "E3373.0.665", {"start": v(14.98, -1.58) * mm, "end": v(14.98, -1.55) * mm});
            skLineSegment(sketch, "E3373.0.666", {"start": v(14.98, -1.55) * mm, "end": v(14.98, -1.5) * mm});
            skLineSegment(sketch, "E3373.0.667", {"start": v(14.98, -1.5) * mm, "end": v(14.99, -1.47) * mm});
            skLineSegment(sketch, "E3373.0.668", {"start": v(14.99, -1.47) * mm, "end": v(15, -1.43) * mm});
            skLineSegment(sketch, "E3373.0.669", {"start": v(15, -1.43) * mm, "end": v(15, -1.4) * mm});
            skLineSegment(sketch, "E3373.0.670", {"start": v(15, -1.4) * mm, "end": v(15.02, -1.36) * mm});
            skLineSegment(sketch, "E3373.0.671", {"start": v(15.02, -1.36) * mm, "end": v(15.04, -1.33) * mm});
            skLineSegment(sketch, "E3373.0.672", {"start": v(15.04, -1.33) * mm, "end": v(15.06, -1.3) * mm});
            skLineSegment(sketch, "E3373.0.673", {"start": v(15.06, -1.3) * mm, "end": v(15.1, -1.28) * mm});
            skLineSegment(sketch, "E3373.0.674", {"start": v(15.1, -1.28) * mm, "end": v(15.12, -1.26) * mm});
            skLineSegment(sketch, "E3373.0.675", {"start": v(15.12, -1.26) * mm, "end": v(15.15, -1.24) * mm});
            skLineSegment(sketch, "E3373.0.676", {"start": v(15.15, -1.24) * mm, "end": v(15.18, -1.22) * mm});
            skLineSegment(sketch, "E3373.0.677", {"start": v(15.18, -1.22) * mm, "end": v(15.2, -1.21) * mm});
            skLineSegment(sketch, "E3373.0.678", {"start": v(15.2, -1.21) * mm, "end": v(15.23, -1.2) * mm});
            skLineSegment(sketch, "E3373.0.679", {"start": v(15.23, -1.2) * mm, "end": v(20.45, 0.5) * mm});
            skLineSegment(sketch, "E3373.0.680", {"start": v(20.45, 0.5) * mm, "end": v(20.5, 0.52) * mm});
            skLineSegment(sketch, "E3373.0.681", {"start": v(20.5, 0.52) * mm, "end": v(20.54, 0.54) * mm});
            skLineSegment(sketch, "E3373.0.682", {"start": v(20.54, 0.54) * mm, "end": v(20.59, 0.57) * mm});
            skLineSegment(sketch, "E3373.0.683", {"start": v(20.59, 0.57) * mm, "end": v(20.63, 0.6) * mm});
            skLineSegment(sketch, "E3373.0.684", {"start": v(20.63, 0.6) * mm, "end": v(20.66, 0.63) * mm});
            skLineSegment(sketch, "E3373.0.685", {"start": v(20.66, 0.63) * mm, "end": v(20.7, 0.67) * mm});
            skLineSegment(sketch, "E3373.0.686", {"start": v(20.7, 0.67) * mm, "end": v(20.73, 0.72) * mm});
            skLineSegment(sketch, "E3373.0.687", {"start": v(20.73, 0.72) * mm, "end": v(20.85, 0.95) * mm});
            skLineSegment(sketch, "E3373.0.688", {"start": v(20.85, 0.95) * mm, "end": v(20.96, 1.12) * mm});
            skLineSegment(sketch, "E3373.0.689", {"start": v(20.96, 1.12) * mm, "end": v(21.1, 1.27) * mm});
            skLineSegment(sketch, "E3373.0.690", {"start": v(21.1, 1.27) * mm, "end": v(21.24, 1.42) * mm});
            skLineSegment(sketch, "E3373.0.691", {"start": v(21.24, 1.42) * mm, "end": v(21.4, 1.55) * mm});
            skLineSegment(sketch, "E3373.0.692", {"start": v(21.4, 1.55) * mm, "end": v(21.57, 1.66) * mm});
            skLineSegment(sketch, "E3373.0.693", {"start": v(21.57, 1.66) * mm, "end": v(21.75, 1.75) * mm});
            skLineSegment(sketch, "E3373.0.694", {"start": v(21.75, 1.75) * mm, "end": v(21.95, 1.82) * mm});
            skLineSegment(sketch, "E3373.0.695", {"start": v(21.95, 1.82) * mm, "end": v(22.15, 1.88) * mm});
            skLineSegment(sketch, "E3373.0.696", {"start": v(22.15, 1.88) * mm, "end": v(22.35, 1.91) * mm});
            skLineSegment(sketch, "E3373.0.697", {"start": v(22.35, 1.91) * mm, "end": v(22.55, 1.92) * mm});
            skLineSegment(sketch, "E3373.0.698", {"start": v(22.55, 1.92) * mm, "end": v(22.76, 1.91) * mm});
            skLineSegment(sketch, "E3373.0.699", {"start": v(22.76, 1.91) * mm, "end": v(22.96, 1.88) * mm});
            skLineSegment(sketch, "E3373.0.700", {"start": v(22.96, 1.88) * mm, "end": v(23.16, 1.83) * mm});
            skLineSegment(sketch, "E3373.0.701", {"start": v(23.16, 1.83) * mm, "end": v(23.35, 1.76) * mm});
            skLineSegment(sketch, "E3373.0.702", {"start": v(23.35, 1.76) * mm, "end": v(23.59, 1.65) * mm});
            skLineSegment(sketch, "E3373.0.703", {"start": v(23.59, 1.65) * mm, "end": v(23.63, 1.63) * mm});
            skLineSegment(sketch, "E3373.0.704", {"start": v(23.63, 1.63) * mm, "end": v(23.68, 1.61) * mm});
            skLineSegment(sketch, "E3373.0.705", {"start": v(23.68, 1.61) * mm, "end": v(23.73, 1.6) * mm});
            skLineSegment(sketch, "E3373.0.706", {"start": v(23.73, 1.6) * mm, "end": v(23.79, 1.6) * mm});
            skLineSegment(sketch, "E3373.0.707", {"start": v(23.79, 1.6) * mm, "end": v(23.84, 1.6) * mm});
            skLineSegment(sketch, "E3373.0.708", {"start": v(23.84, 1.6) * mm, "end": v(23.89, 1.62) * mm});
            skLineSegment(sketch, "E3373.0.709", {"start": v(23.89, 1.62) * mm, "end": v(23.94, 1.63) * mm});
            skLineSegment(sketch, "E3373.0.710", {"start": v(23.94, 1.63) * mm, "end": v(25.14, 2.02) * mm});
            skLineSegment(sketch, "E3373.0.711", {"start": v(25.14, 2.02) * mm, "end": v(29.7, 4.4) * mm});
            skLineSegment(sketch, "E3373.0.712", {"start": v(29.7, 4.4) * mm, "end": v(29.85, 4.5) * mm});
            skLineSegment(sketch, "E3373.0.713", {"start": v(29.85, 4.5) * mm, "end": v(29.98, 4.62) * mm});
            skLineSegment(sketch, "E3373.0.714", {"start": v(29.98, 4.62) * mm, "end": v(30.08, 4.76) * mm});
            skLineSegment(sketch, "E3373.0.715", {"start": v(30.08, 4.76) * mm, "end": v(30.16, 4.91) * mm});
            skLineSegment(sketch, "E3373.0.716", {"start": v(30.16, 4.91) * mm, "end": v(30.2, 5.08) * mm});
            skLineSegment(sketch, "E3373.0.717", {"start": v(30.2, 5.08) * mm, "end": v(30.23, 5.25) * mm});
            skCircle(sketch, "E3374.0", {"center": v(16.1, -24.5) * mm, "radius": 1.7 * mm});
            skCircle(sketch, "E3375.0", {"center": v(-16.07, -24.51) * mm, "radius": 1.7 * mm});
            skCircle(sketch, "E3376.0", {"center": v(-26.02, 6.08) * mm, "radius": 1.7 * mm});
            skCircle(sketch, "E3377.0", {"center": v(26.03, 6.09) * mm, "radius": 1.7 * mm});
            skCircle(sketch, "E3378.0", {"center": v(0, 25) * mm, "radius": 1.7 * mm});
            skSolve(sketch);
        }
        {
            var Q0;
            Q0=makeQuery(id+"F13.imprint","IMPRINT",FACE,{"disambiguationData":[TD([[makeQuery(id+"F13.imprint","IMPRINT",EDGE,{"derivedFrom":sQuery(id+"F13.wireOp",EDGE,"E3373.0.58")}),1.0]])]});
            var Q1;
            Q1=makeQuery(id+"F13.imprint","IMPRINT",FACE,{"disambiguationData":[TD([[makeQuery(id+"F13.imprint","IMPRINT",EDGE,{"derivedFrom":sQuery(id+"F13.wireOp",EDGE,"E3373.0.0")}),1.0]])]});
            var Q2;
            {var subQ4=sQuery(id+"F13.wireOp",EDGE,"E3373.0.394");Q2=makeQuery(id+"F13.imprint","IMPRINT",FACE,{"disambiguationData":[TD([[makeQuery(id+"F13.imprint","IMPRINT",EDGE,{"derivedFrom":subQ4}),1.0]])]});}
            var Q3;
            Q3=makeQuery(id+"F13.imprint","IMPRINT",FACE,{"disambiguationData":[TD([[makeQuery(id+"F13.imprint","IMPRINT",EDGE,{"derivedFrom":sQuery(id+"F13.wireOp",EDGE,"E3373.0.273")}),1.0]])]});
            var Q4;
            Q4=makeQuery(id+"F13.imprint","IMPRINT",FACE,{"disambiguationData":[TD([[makeQuery(id+"F13.imprint","IMPRINT",EDGE,{"derivedFrom":sQuery(id+"F13.wireOp",EDGE,"E3373.0.386")}),1.0]])]});
            extrude(context, id + "F14", {"entities" : qUnion([Q0, Q1, Q2, Q3, Q4]), "depth" : 2 * mm});
        }
        {
            var Q0;
            Q0=makeQuery(id+"F11.opExtrude","CAP_FACE",FACE,{"disambiguationData":[OSD([sQuery(id+"F10.wireOp",EDGE,"E3369")])],"isStart":false});
            var sketch = newSketch(context, id + "F15", { "sketchPlane" : qUnion([Q0])});
            skCircle(sketch, "E3379.0", {"center": v(5.15, 0) * mm, "radius": 1.5 * mm});
            skCircle(sketch, "E3380.0.0", {"center": v(-5.15, 0) * mm, "radius": 1.5 * mm});
            skCircle(sketch, "E3381", {"center": v(5.15, 0) * mm, "radius": 0.75 * mm});
            skCircle(sketch, "E3382", {"center": v(-5.15, 0) * mm, "radius": 0.75 * mm});
            skSolve(sketch);
        }
        {
            var Q0;
            Q0=makeQuery(id+"F15.imprint","IMPRINT",FACE,{"disambiguationData":[TD([[makeQuery(id+"F15.imprint","IMPRINT",EDGE,{"derivedFrom":sQuery(id+"F15.wireOp",EDGE,"E3381")}),1.0]])]});
            var Q1;
            Q1=makeQuery(id+"F15.imprint","IMPRINT",FACE,{"disambiguationData":[TD([[makeQuery(id+"F15.imprint","IMPRINT",EDGE,{"derivedFrom":sQuery(id+"F15.wireOp",EDGE,"E3382")}),1.0]])]});
            extrude(context, id + "F16", {"entities" : qUnion([Q0, Q1]), "depth" : 1 * mm});
        }
    });
